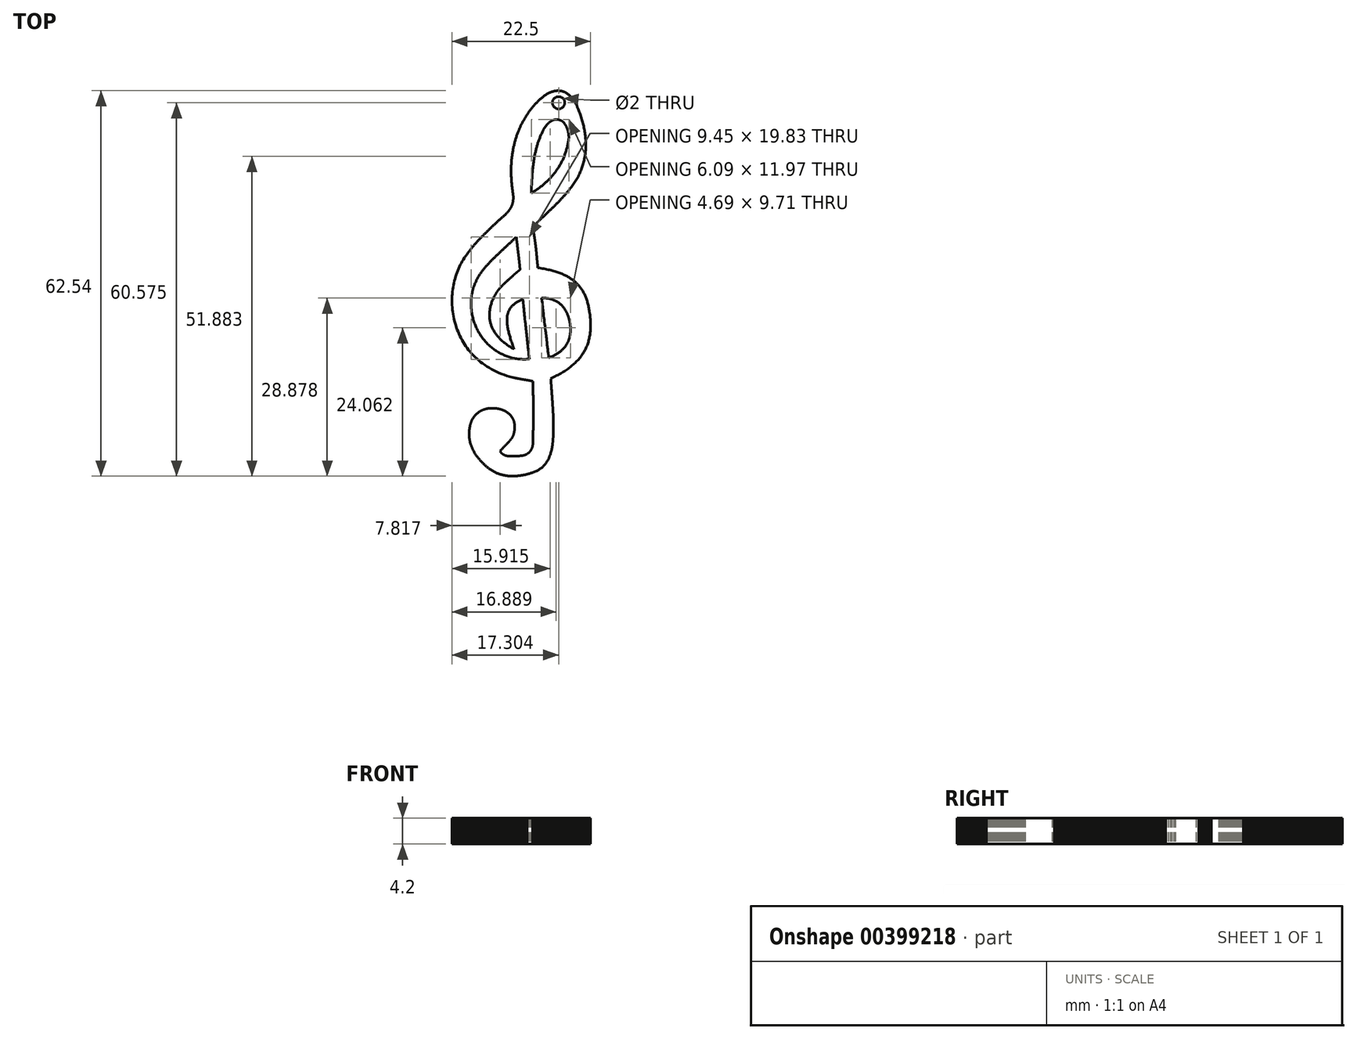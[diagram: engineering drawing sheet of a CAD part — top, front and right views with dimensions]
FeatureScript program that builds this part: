
annotation { "Feature Type Name" : "Feature", "Feature Type Description" : "" }
export const myFeature = defineFeature(function(context is Context, id is Id, definition is map)
    precondition{}
    {
        {
            var Q0;
            Q0=qCreatedBy(makeId("Top.planeOp"),FACE);
            var sketch = newSketch(context, id + "F0", { "sketchPlane" : qUnion([Q0])});
            skLineSegment(sketch, "E0", {"start": v(1.92, -15.87) * mm, "end": v(1.85, -15.86) * mm});
            skLineSegment(sketch, "E1", {"start": v(1.85, -15.86) * mm, "end": v(1.79, -15.85) * mm});
            skLineSegment(sketch, "E2", {"start": v(1.79, -15.85) * mm, "end": v(1.72, -15.84) * mm});
            skLineSegment(sketch, "E3", {"start": v(1.72, -15.84) * mm, "end": v(1.66, -15.82) * mm});
            skLineSegment(sketch, "E4", {"start": v(1.66, -15.82) * mm, "end": v(1.6, -15.81) * mm});
            skLineSegment(sketch, "E5", {"start": v(1.6, -15.81) * mm, "end": v(1.53, -15.8) * mm});
            skLineSegment(sketch, "E6", {"start": v(1.53, -15.8) * mm, "end": v(1.47, -15.8) * mm});
            skLineSegment(sketch, "E7", {"start": v(1.47, -15.8) * mm, "end": v(1.4, -15.78) * mm});
            skLineSegment(sketch, "E8", {"start": v(1.4, -15.78) * mm, "end": v(1.35, -15.77) * mm});
            skLineSegment(sketch, "E9", {"start": v(1.35, -15.77) * mm, "end": v(1.28, -15.76) * mm});
            skLineSegment(sketch, "E10", {"start": v(1.28, -15.76) * mm, "end": v(1.22, -15.75) * mm});
            skLineSegment(sketch, "E11", {"start": v(1.22, -15.75) * mm, "end": v(1.16, -15.74) * mm});
            skLineSegment(sketch, "E12", {"start": v(1.16, -15.74) * mm, "end": v(1.1, -15.73) * mm});
            skLineSegment(sketch, "E13", {"start": v(1.1, -15.73) * mm, "end": v(1.05, -15.72) * mm});
            skLineSegment(sketch, "E14", {"start": v(1.05, -15.72) * mm, "end": v(0.99, -15.7) * mm});
            skLineSegment(sketch, "E15", {"start": v(0.99, -15.7) * mm, "end": v(0.93, -15.7) * mm});
            skLineSegment(sketch, "E16", {"start": v(0.93, -15.7) * mm, "end": v(0.87, -15.69) * mm});
            skLineSegment(sketch, "E17", {"start": v(0.87, -15.69) * mm, "end": v(0.82, -15.68) * mm});
            skLineSegment(sketch, "E18", {"start": v(0.82, -15.68) * mm, "end": v(0.76, -15.67) * mm});
            skLineSegment(sketch, "E19", {"start": v(0.76, -15.67) * mm, "end": v(0.7, -15.66) * mm});
            skLineSegment(sketch, "E20", {"start": v(0.7, -15.66) * mm, "end": v(0.65, -15.65) * mm});
            skLineSegment(sketch, "E21", {"start": v(0.65, -15.65) * mm, "end": v(0.6, -15.64) * mm});
            skLineSegment(sketch, "E22", {"start": v(0.6, -15.64) * mm, "end": v(0.54, -15.63) * mm});
            skLineSegment(sketch, "E23", {"start": v(0.54, -15.63) * mm, "end": v(0.49, -15.62) * mm});
            skLineSegment(sketch, "E24", {"start": v(0.49, -15.62) * mm, "end": v(0.43, -15.61) * mm});
            skLineSegment(sketch, "E25", {"start": v(0.43, -15.61) * mm, "end": v(0.38, -15.6) * mm});
            skLineSegment(sketch, "E26", {"start": v(0.38, -15.6) * mm, "end": v(0.33, -15.6) * mm});
            skLineSegment(sketch, "E27", {"start": v(0.33, -15.6) * mm, "end": v(0.28, -15.58) * mm});
            skLineSegment(sketch, "E28", {"start": v(0.28, -15.58) * mm, "end": v(0.22, -15.57) * mm});
            skLineSegment(sketch, "E29", {"start": v(0.22, -15.57) * mm, "end": v(0.17, -15.57) * mm});
            skLineSegment(sketch, "E30", {"start": v(0.17, -15.57) * mm, "end": v(0.12, -15.56) * mm});
            skLineSegment(sketch, "E31", {"start": v(0.12, -15.56) * mm, "end": v(0.07, -15.55) * mm});
            skLineSegment(sketch, "E32", {"start": v(0.07, -15.55) * mm, "end": v(0.02, -15.54) * mm});
            skLineSegment(sketch, "E33", {"start": v(0.02, -15.54) * mm, "end": v(-0.03, -15.53) * mm});
            skLineSegment(sketch, "E34", {"start": v(-0.03, -15.53) * mm, "end": v(-0.08, -15.52) * mm});
            skLineSegment(sketch, "E35", {"start": v(-0.08, -15.52) * mm, "end": v(-0.13, -15.51) * mm});
            skLineSegment(sketch, "E36", {"start": v(-0.13, -15.51) * mm, "end": v(-0.18, -15.5) * mm});
            skLineSegment(sketch, "E37", {"start": v(-0.18, -15.5) * mm, "end": v(-0.23, -15.5) * mm});
            skLineSegment(sketch, "E38", {"start": v(-0.23, -15.5) * mm, "end": v(-0.28, -15.49) * mm});
            skLineSegment(sketch, "E39", {"start": v(-0.28, -15.49) * mm, "end": v(-0.33, -15.48) * mm});
            skLineSegment(sketch, "E40", {"start": v(-0.33, -15.48) * mm, "end": v(-0.38, -15.47) * mm});
            skLineSegment(sketch, "E41", {"start": v(-0.38, -15.47) * mm, "end": v(-0.42, -15.46) * mm});
            skLineSegment(sketch, "E42", {"start": v(-0.42, -15.46) * mm, "end": v(-0.47, -15.45) * mm});
            skLineSegment(sketch, "E43", {"start": v(-0.47, -15.45) * mm, "end": v(-0.52, -15.44) * mm});
            skLineSegment(sketch, "E44", {"start": v(-0.52, -15.44) * mm, "end": v(-0.57, -15.43) * mm});
            skLineSegment(sketch, "E45", {"start": v(-0.57, -15.43) * mm, "end": v(-0.61, -15.42) * mm});
            skLineSegment(sketch, "E46", {"start": v(-0.61, -15.42) * mm, "end": v(-0.66, -15.41) * mm});
            skLineSegment(sketch, "E47", {"start": v(-0.66, -15.41) * mm, "end": v(-0.7, -15.4) * mm});
            skLineSegment(sketch, "E48", {"start": v(-0.7, -15.4) * mm, "end": v(-0.75, -15.4) * mm});
            skLineSegment(sketch, "E49", {"start": v(-0.75, -15.4) * mm, "end": v(-0.8, -15.38) * mm});
            skLineSegment(sketch, "E50", {"start": v(-0.8, -15.38) * mm, "end": v(-0.85, -15.37) * mm});
            skLineSegment(sketch, "E51", {"start": v(-0.85, -15.37) * mm, "end": v(-0.9, -15.36) * mm});
            skLineSegment(sketch, "E52", {"start": v(-0.9, -15.36) * mm, "end": v(-0.94, -15.35) * mm});
            skLineSegment(sketch, "E53", {"start": v(-0.94, -15.35) * mm, "end": v(-0.98, -15.34) * mm});
            skLineSegment(sketch, "E54", {"start": v(-0.98, -15.34) * mm, "end": v(-1.03, -15.33) * mm});
            skLineSegment(sketch, "E55", {"start": v(-1.03, -15.33) * mm, "end": v(-1.08, -15.32) * mm});
            skLineSegment(sketch, "E56", {"start": v(-1.08, -15.32) * mm, "end": v(-1.12, -15.31) * mm});
            skLineSegment(sketch, "E57", {"start": v(-1.12, -15.31) * mm, "end": v(-1.17, -15.3) * mm});
            skLineSegment(sketch, "E58", {"start": v(-1.17, -15.3) * mm, "end": v(-1.21, -15.3) * mm});
            skLineSegment(sketch, "E59", {"start": v(-1.21, -15.3) * mm, "end": v(-1.26, -15.28) * mm});
            skLineSegment(sketch, "E60", {"start": v(-1.26, -15.28) * mm, "end": v(-1.3, -15.27) * mm});
            skLineSegment(sketch, "E61", {"start": v(-1.3, -15.27) * mm, "end": v(-1.35, -15.26) * mm});
            skLineSegment(sketch, "E62", {"start": v(-1.35, -15.26) * mm, "end": v(-1.4, -15.25) * mm});
            skLineSegment(sketch, "E63", {"start": v(-1.4, -15.25) * mm, "end": v(-1.44, -15.24) * mm});
            skLineSegment(sketch, "E64", {"start": v(-1.44, -15.24) * mm, "end": v(-1.9, -15.11) * mm});
            skLineSegment(sketch, "E65", {"start": v(-1.9, -15.11) * mm, "end": v(-2.36, -14.97) * mm});
            skLineSegment(sketch, "E66", {"start": v(-2.36, -14.97) * mm, "end": v(-2.8, -14.82) * mm});
            skLineSegment(sketch, "E67", {"start": v(-2.8, -14.82) * mm, "end": v(-3.24, -14.66) * mm});
            skLineSegment(sketch, "E68", {"start": v(-3.24, -14.66) * mm, "end": v(-3.66, -14.49) * mm});
            skLineSegment(sketch, "E69", {"start": v(-3.66, -14.49) * mm, "end": v(-4.07, -14.3) * mm});
            skLineSegment(sketch, "E70", {"start": v(-4.07, -14.3) * mm, "end": v(-4.47, -14.11) * mm});
            skLineSegment(sketch, "E71", {"start": v(-4.47, -14.11) * mm, "end": v(-4.85, -13.9) * mm});
            skLineSegment(sketch, "E72", {"start": v(-4.85, -13.9) * mm, "end": v(-5.23, -13.7) * mm});
            skLineSegment(sketch, "E73", {"start": v(-5.23, -13.7) * mm, "end": v(-5.59, -13.47) * mm});
            skLineSegment(sketch, "E74", {"start": v(-5.59, -13.47) * mm, "end": v(-5.94, -13.24) * mm});
            skLineSegment(sketch, "E75", {"start": v(-5.94, -13.24) * mm, "end": v(-6.27, -13) * mm});
            skLineSegment(sketch, "E76", {"start": v(-6.27, -13) * mm, "end": v(-6.6, -12.75) * mm});
            skLineSegment(sketch, "E77", {"start": v(-6.6, -12.75) * mm, "end": v(-6.91, -12.49) * mm});
            skLineSegment(sketch, "E78", {"start": v(-6.91, -12.49) * mm, "end": v(-7.21, -12.22) * mm});
            skLineSegment(sketch, "E79", {"start": v(-7.21, -12.22) * mm, "end": v(-7.5, -11.95) * mm});
            skLineSegment(sketch, "E80", {"start": v(-7.5, -11.95) * mm, "end": v(-7.78, -11.67) * mm});
            skLineSegment(sketch, "E81", {"start": v(-7.78, -11.67) * mm, "end": v(-8.05, -11.38) * mm});
            skLineSegment(sketch, "E82", {"start": v(-8.05, -11.38) * mm, "end": v(-8.3, -11.09) * mm});
            skLineSegment(sketch, "E83", {"start": v(-8.3, -11.09) * mm, "end": v(-8.55, -10.79) * mm});
            skLineSegment(sketch, "E84", {"start": v(-8.55, -10.79) * mm, "end": v(-8.79, -10.48) * mm});
            skLineSegment(sketch, "E85", {"start": v(-8.79, -10.48) * mm, "end": v(-9.01, -10.16) * mm});
            skLineSegment(sketch, "E86", {"start": v(-9.01, -10.16) * mm, "end": v(-9.22, -9.85) * mm});
            skLineSegment(sketch, "E87", {"start": v(-9.22, -9.85) * mm, "end": v(-9.42, -9.52) * mm});
            skLineSegment(sketch, "E88", {"start": v(-9.42, -9.52) * mm, "end": v(-9.61, -9.2) * mm});
            skLineSegment(sketch, "E89", {"start": v(-9.61, -9.2) * mm, "end": v(-9.8, -8.86) * mm});
            skLineSegment(sketch, "E90", {"start": v(-9.8, -8.86) * mm, "end": v(-9.96, -8.52) * mm});
            skLineSegment(sketch, "E91", {"start": v(-9.96, -8.52) * mm, "end": v(-10.12, -8.18) * mm});
            skLineSegment(sketch, "E92", {"start": v(-10.12, -8.18) * mm, "end": v(-10.27, -7.84) * mm});
            skLineSegment(sketch, "E93", {"start": v(-10.27, -7.84) * mm, "end": v(-10.4, -7.49) * mm});
            skLineSegment(sketch, "E94", {"start": v(-10.4, -7.49) * mm, "end": v(-10.53, -7.14) * mm});
            skLineSegment(sketch, "E95", {"start": v(-10.53, -7.14) * mm, "end": v(-10.65, -6.78) * mm});
            skLineSegment(sketch, "E96", {"start": v(-10.65, -6.78) * mm, "end": v(-10.75, -6.43) * mm});
            skLineSegment(sketch, "E97", {"start": v(-10.75, -6.43) * mm, "end": v(-10.85, -6.07) * mm});
            skLineSegment(sketch, "E98", {"start": v(-10.85, -6.07) * mm, "end": v(-10.93, -5.7) * mm});
            skLineSegment(sketch, "E99", {"start": v(-10.93, -5.7) * mm, "end": v(-11, -5.34) * mm});
            skLineSegment(sketch, "E100", {"start": v(-11, -5.34) * mm, "end": v(-11.07, -4.98) * mm});
            skLineSegment(sketch, "E101", {"start": v(-11.07, -4.98) * mm, "end": v(-11.12, -4.62) * mm});
            skLineSegment(sketch, "E102", {"start": v(-11.12, -4.62) * mm, "end": v(-11.17, -4.25) * mm});
            skLineSegment(sketch, "E103", {"start": v(-11.17, -4.25) * mm, "end": v(-11.2, -3.89) * mm});
            skLineSegment(sketch, "E104", {"start": v(-11.2, -3.89) * mm, "end": v(-11.23, -3.52) * mm});
            skLineSegment(sketch, "E105", {"start": v(-11.23, -3.52) * mm, "end": v(-11.24, -3.16) * mm});
            skLineSegment(sketch, "E106", {"start": v(-11.24, -3.16) * mm, "end": v(-11.25, -2.8) * mm});
            skLineSegment(sketch, "E107", {"start": v(-11.25, -2.8) * mm, "end": v(-11.24, -2.43) * mm});
            skLineSegment(sketch, "E108", {"start": v(-11.24, -2.43) * mm, "end": v(-11.23, -2.07) * mm});
            skLineSegment(sketch, "E109", {"start": v(-11.23, -2.07) * mm, "end": v(-11.2, -1.7) * mm});
            skLineSegment(sketch, "E110", {"start": v(-11.2, -1.7) * mm, "end": v(-11.17, -1.35) * mm});
            skLineSegment(sketch, "E111", {"start": v(-11.17, -1.35) * mm, "end": v(-11.13, -1) * mm});
            skLineSegment(sketch, "E112", {"start": v(-11.13, -1) * mm, "end": v(-11.07, -0.64) * mm});
            skLineSegment(sketch, "E113", {"start": v(-11.07, -0.64) * mm, "end": v(-11.01, -0.29) * mm});
            skLineSegment(sketch, "E114", {"start": v(-11.01, -0.29) * mm, "end": v(-10.94, 0.06) * mm});
            skLineSegment(sketch, "E115", {"start": v(-10.94, 0.06) * mm, "end": v(-10.86, 0.4) * mm});
            skLineSegment(sketch, "E116", {"start": v(-10.86, 0.4) * mm, "end": v(-10.77, 0.75) * mm});
            skLineSegment(sketch, "E117", {"start": v(-10.77, 0.75) * mm, "end": v(-10.68, 1.09) * mm});
            skLineSegment(sketch, "E118", {"start": v(-10.68, 1.09) * mm, "end": v(-10.57, 1.42) * mm});
            skLineSegment(sketch, "E119", {"start": v(-10.57, 1.42) * mm, "end": v(-10.45, 1.75) * mm});
            skLineSegment(sketch, "E120", {"start": v(-10.45, 1.75) * mm, "end": v(-10.33, 2.07) * mm});
            skLineSegment(sketch, "E121", {"start": v(-10.33, 2.07) * mm, "end": v(-10.2, 2.39) * mm});
            skLineSegment(sketch, "E122", {"start": v(-10.2, 2.39) * mm, "end": v(-10.06, 2.7) * mm});
            skLineSegment(sketch, "E123", {"start": v(-10.06, 2.7) * mm, "end": v(-9.9, 3) * mm});
            skLineSegment(sketch, "E124", {"start": v(-9.9, 3) * mm, "end": v(-9.75, 3.3) * mm});
            skLineSegment(sketch, "E125", {"start": v(-9.75, 3.3) * mm, "end": v(-9.58, 3.6) * mm});
            skLineSegment(sketch, "E126", {"start": v(-9.58, 3.6) * mm, "end": v(-9.4, 3.9) * mm});
            skLineSegment(sketch, "E127", {"start": v(-9.4, 3.9) * mm, "end": v(-9.22, 4.17) * mm});
            skLineSegment(sketch, "E128", {"start": v(-9.22, 4.17) * mm, "end": v(-9.14, 4.29) * mm});
            skLineSegment(sketch, "E129", {"start": v(-9.14, 4.29) * mm, "end": v(-9.06, 4.4) * mm});
            skLineSegment(sketch, "E130", {"start": v(-9.06, 4.4) * mm, "end": v(-8.97, 4.52) * mm});
            skLineSegment(sketch, "E131", {"start": v(-8.97, 4.52) * mm, "end": v(-8.89, 4.64) * mm});
            skLineSegment(sketch, "E132", {"start": v(-8.89, 4.64) * mm, "end": v(-8.8, 4.76) * mm});
            skLineSegment(sketch, "E133", {"start": v(-8.8, 4.76) * mm, "end": v(-8.72, 4.87) * mm});
            skLineSegment(sketch, "E134", {"start": v(-8.72, 4.87) * mm, "end": v(-8.63, 4.99) * mm});
            skLineSegment(sketch, "E135", {"start": v(-8.63, 4.99) * mm, "end": v(-8.55, 5.1) * mm});
            skLineSegment(sketch, "E136", {"start": v(-8.55, 5.1) * mm, "end": v(-8.46, 5.22) * mm});
            skLineSegment(sketch, "E137", {"start": v(-8.46, 5.22) * mm, "end": v(-8.37, 5.33) * mm});
            skLineSegment(sketch, "E138", {"start": v(-8.37, 5.33) * mm, "end": v(-8.28, 5.44) * mm});
            skLineSegment(sketch, "E139", {"start": v(-8.28, 5.44) * mm, "end": v(-8.2, 5.56) * mm});
            skLineSegment(sketch, "E140", {"start": v(-8.2, 5.56) * mm, "end": v(-8.1, 5.67) * mm});
            skLineSegment(sketch, "E141", {"start": v(-8.1, 5.67) * mm, "end": v(-8, 5.78) * mm});
            skLineSegment(sketch, "E142", {"start": v(-8, 5.78) * mm, "end": v(-7.92, 5.9) * mm});
            skLineSegment(sketch, "E143", {"start": v(-7.92, 5.9) * mm, "end": v(-7.82, 6) * mm});
            skLineSegment(sketch, "E144", {"start": v(-7.82, 6) * mm, "end": v(-7.73, 6.12) * mm});
            skLineSegment(sketch, "E145", {"start": v(-7.73, 6.12) * mm, "end": v(-7.64, 6.23) * mm});
            skLineSegment(sketch, "E146", {"start": v(-7.64, 6.23) * mm, "end": v(-7.54, 6.34) * mm});
            skLineSegment(sketch, "E147", {"start": v(-7.54, 6.34) * mm, "end": v(-7.45, 6.44) * mm});
            skLineSegment(sketch, "E148", {"start": v(-7.45, 6.44) * mm, "end": v(-7.35, 6.55) * mm});
            skLineSegment(sketch, "E149", {"start": v(-7.35, 6.55) * mm, "end": v(-7.25, 6.66) * mm});
            skLineSegment(sketch, "E150", {"start": v(-7.25, 6.66) * mm, "end": v(-7.16, 6.77) * mm});
            skLineSegment(sketch, "E151", {"start": v(-7.16, 6.77) * mm, "end": v(-7.06, 6.88) * mm});
            skLineSegment(sketch, "E152", {"start": v(-7.06, 6.88) * mm, "end": v(-6.96, 6.99) * mm});
            skLineSegment(sketch, "E153", {"start": v(-6.96, 6.99) * mm, "end": v(-6.86, 7.1) * mm});
            skLineSegment(sketch, "E154", {"start": v(-6.86, 7.1) * mm, "end": v(-6.76, 7.2) * mm});
            skLineSegment(sketch, "E155", {"start": v(-6.76, 7.2) * mm, "end": v(-6.66, 7.3) * mm});
            skLineSegment(sketch, "E156", {"start": v(-6.66, 7.3) * mm, "end": v(-6.56, 7.41) * mm});
            skLineSegment(sketch, "E157", {"start": v(-6.56, 7.41) * mm, "end": v(-6.46, 7.52) * mm});
            skLineSegment(sketch, "E158", {"start": v(-6.46, 7.52) * mm, "end": v(-6.36, 7.62) * mm});
            skLineSegment(sketch, "E159", {"start": v(-6.36, 7.62) * mm, "end": v(-6.26, 7.73) * mm});
            skLineSegment(sketch, "E160", {"start": v(-6.26, 7.73) * mm, "end": v(-6.16, 7.83) * mm});
            skLineSegment(sketch, "E161", {"start": v(-6.16, 7.83) * mm, "end": v(-6.06, 7.93) * mm});
            skLineSegment(sketch, "E162", {"start": v(-6.06, 7.93) * mm, "end": v(-5.95, 8.04) * mm});
            skLineSegment(sketch, "E163", {"start": v(-5.95, 8.04) * mm, "end": v(-5.85, 8.14) * mm});
            skLineSegment(sketch, "E164", {"start": v(-5.85, 8.14) * mm, "end": v(-5.75, 8.25) * mm});
            skLineSegment(sketch, "E165", {"start": v(-5.75, 8.25) * mm, "end": v(-5.64, 8.35) * mm});
            skLineSegment(sketch, "E166", {"start": v(-5.64, 8.35) * mm, "end": v(-5.54, 8.45) * mm});
            skLineSegment(sketch, "E167", {"start": v(-5.54, 8.45) * mm, "end": v(-5.43, 8.55) * mm});
            skLineSegment(sketch, "E168", {"start": v(-5.43, 8.55) * mm, "end": v(-5.33, 8.65) * mm});
            skLineSegment(sketch, "E169", {"start": v(-5.33, 8.65) * mm, "end": v(-5.22, 8.76) * mm});
            skLineSegment(sketch, "E170", {"start": v(-5.22, 8.76) * mm, "end": v(-5.12, 8.86) * mm});
            skLineSegment(sketch, "E171", {"start": v(-5.12, 8.86) * mm, "end": v(-5.01, 8.96) * mm});
            skLineSegment(sketch, "E172", {"start": v(-5.01, 8.96) * mm, "end": v(-4.9, 9.06) * mm});
            skLineSegment(sketch, "E173", {"start": v(-4.9, 9.06) * mm, "end": v(-4.8, 9.16) * mm});
            skLineSegment(sketch, "E174", {"start": v(-4.8, 9.16) * mm, "end": v(-4.7, 9.26) * mm});
            skLineSegment(sketch, "E175", {"start": v(-4.7, 9.26) * mm, "end": v(-4.59, 9.36) * mm});
            skLineSegment(sketch, "E176", {"start": v(-4.59, 9.36) * mm, "end": v(-4.48, 9.46) * mm});
            skLineSegment(sketch, "E177", {"start": v(-4.48, 9.46) * mm, "end": v(-4.37, 9.56) * mm});
            skLineSegment(sketch, "E178", {"start": v(-4.37, 9.56) * mm, "end": v(-4.26, 9.65) * mm});
            skLineSegment(sketch, "E179", {"start": v(-4.26, 9.65) * mm, "end": v(-4.16, 9.75) * mm});
            skLineSegment(sketch, "E180", {"start": v(-4.16, 9.75) * mm, "end": v(-4.05, 9.85) * mm});
            skLineSegment(sketch, "E181", {"start": v(-4.05, 9.85) * mm, "end": v(-3.94, 9.95) * mm});
            skLineSegment(sketch, "E182", {"start": v(-3.94, 9.95) * mm, "end": v(-3.83, 10.05) * mm});
            skLineSegment(sketch, "E183", {"start": v(-3.83, 10.05) * mm, "end": v(-3.72, 10.15) * mm});
            skLineSegment(sketch, "E184", {"start": v(-3.72, 10.15) * mm, "end": v(-3.62, 10.24) * mm});
            skLineSegment(sketch, "E185", {"start": v(-3.62, 10.24) * mm, "end": v(-3.5, 10.34) * mm});
            skLineSegment(sketch, "E186", {"start": v(-3.5, 10.34) * mm, "end": v(-3.4, 10.44) * mm});
            skLineSegment(sketch, "E187", {"start": v(-3.4, 10.44) * mm, "end": v(-3.3, 10.53) * mm});
            skLineSegment(sketch, "E188", {"start": v(-3.3, 10.53) * mm, "end": v(-3.18, 10.63) * mm});
            skLineSegment(sketch, "E189", {"start": v(-3.18, 10.63) * mm, "end": v(-3.08, 10.73) * mm});
            skLineSegment(sketch, "E190", {"start": v(-3.08, 10.73) * mm, "end": v(-2.97, 10.82) * mm});
            skLineSegment(sketch, "E191", {"start": v(-2.97, 10.82) * mm, "end": v(-2.86, 10.92) * mm});
            skLineSegment(sketch, "E192", {"start": v(-2.86, 10.92) * mm, "end": v(-2.8, 10.97) * mm});
            skLineSegment(sketch, "E193", {"start": v(-2.8, 10.97) * mm, "end": v(-2.74, 11.02) * mm});
            skLineSegment(sketch, "E194", {"start": v(-2.74, 11.02) * mm, "end": v(-2.69, 11.08) * mm});
            skLineSegment(sketch, "E195", {"start": v(-2.69, 11.08) * mm, "end": v(-2.63, 11.13) * mm});
            skLineSegment(sketch, "E196", {"start": v(-2.63, 11.13) * mm, "end": v(-2.58, 11.18) * mm});
            skLineSegment(sketch, "E197", {"start": v(-2.58, 11.18) * mm, "end": v(-2.52, 11.23) * mm});
            skLineSegment(sketch, "E198", {"start": v(-2.52, 11.23) * mm, "end": v(-2.47, 11.28) * mm});
            skLineSegment(sketch, "E199", {"start": v(-2.47, 11.28) * mm, "end": v(-2.42, 11.33) * mm});
            skLineSegment(sketch, "E200", {"start": v(-2.42, 11.33) * mm, "end": v(-2.37, 11.39) * mm});
            skLineSegment(sketch, "E201", {"start": v(-2.37, 11.39) * mm, "end": v(-2.32, 11.44) * mm});
            skLineSegment(sketch, "E202", {"start": v(-2.32, 11.44) * mm, "end": v(-2.28, 11.49) * mm});
            skLineSegment(sketch, "E203", {"start": v(-2.28, 11.49) * mm, "end": v(-2.23, 11.54) * mm});
            skLineSegment(sketch, "E204", {"start": v(-2.23, 11.54) * mm, "end": v(-2.18, 11.6) * mm});
            skLineSegment(sketch, "E205", {"start": v(-2.18, 11.6) * mm, "end": v(-2.14, 11.64) * mm});
            skLineSegment(sketch, "E206", {"start": v(-2.14, 11.64) * mm, "end": v(-2.1, 11.7) * mm});
            skLineSegment(sketch, "E207", {"start": v(-2.1, 11.7) * mm, "end": v(-2.06, 11.75) * mm});
            skLineSegment(sketch, "E208", {"start": v(-2.06, 11.75) * mm, "end": v(-2.02, 11.8) * mm});
            skLineSegment(sketch, "E209", {"start": v(-2.02, 11.8) * mm, "end": v(-1.98, 11.85) * mm});
            skLineSegment(sketch, "E210", {"start": v(-1.98, 11.85) * mm, "end": v(-1.94, 11.9) * mm});
            skLineSegment(sketch, "E211", {"start": v(-1.94, 11.9) * mm, "end": v(-1.9, 11.96) * mm});
            skLineSegment(sketch, "E212", {"start": v(-1.9, 11.96) * mm, "end": v(-1.87, 12) * mm});
            skLineSegment(sketch, "E213", {"start": v(-1.87, 12) * mm, "end": v(-1.83, 12.06) * mm});
            skLineSegment(sketch, "E214", {"start": v(-1.83, 12.06) * mm, "end": v(-1.8, 12.11) * mm});
            skLineSegment(sketch, "E215", {"start": v(-1.8, 12.11) * mm, "end": v(-1.76, 12.17) * mm});
            skLineSegment(sketch, "E216", {"start": v(-1.76, 12.17) * mm, "end": v(-1.73, 12.22) * mm});
            skLineSegment(sketch, "E217", {"start": v(-1.73, 12.22) * mm, "end": v(-1.7, 12.27) * mm});
            skLineSegment(sketch, "E218", {"start": v(-1.7, 12.27) * mm, "end": v(-1.67, 12.33) * mm});
            skLineSegment(sketch, "E219", {"start": v(-1.67, 12.33) * mm, "end": v(-1.65, 12.38) * mm});
            skLineSegment(sketch, "E220", {"start": v(-1.65, 12.38) * mm, "end": v(-1.62, 12.44) * mm});
            skLineSegment(sketch, "E221", {"start": v(-1.62, 12.44) * mm, "end": v(-1.6, 12.5) * mm});
            skLineSegment(sketch, "E222", {"start": v(-1.6, 12.5) * mm, "end": v(-1.57, 12.55) * mm});
            skLineSegment(sketch, "E223", {"start": v(-1.57, 12.55) * mm, "end": v(-1.54, 12.6) * mm});
            skLineSegment(sketch, "E224", {"start": v(-1.54, 12.6) * mm, "end": v(-1.52, 12.66) * mm});
            skLineSegment(sketch, "E225", {"start": v(-1.52, 12.66) * mm, "end": v(-1.5, 12.71) * mm});
            skLineSegment(sketch, "E226", {"start": v(-1.5, 12.71) * mm, "end": v(-1.48, 12.77) * mm});
            skLineSegment(sketch, "E227", {"start": v(-1.48, 12.77) * mm, "end": v(-1.46, 12.83) * mm});
            skLineSegment(sketch, "E228", {"start": v(-1.46, 12.83) * mm, "end": v(-1.44, 12.88) * mm});
            skLineSegment(sketch, "E229", {"start": v(-1.44, 12.88) * mm, "end": v(-1.43, 12.94) * mm});
            skLineSegment(sketch, "E230", {"start": v(-1.43, 12.94) * mm, "end": v(-1.4, 13) * mm});
            skLineSegment(sketch, "E231", {"start": v(-1.4, 13) * mm, "end": v(-1.4, 13.06) * mm});
            skLineSegment(sketch, "E232", {"start": v(-1.4, 13.06) * mm, "end": v(-1.38, 13.12) * mm});
            skLineSegment(sketch, "E233", {"start": v(-1.38, 13.12) * mm, "end": v(-1.37, 13.18) * mm});
            skLineSegment(sketch, "E234", {"start": v(-1.37, 13.18) * mm, "end": v(-1.36, 13.24) * mm});
            skLineSegment(sketch, "E235", {"start": v(-1.36, 13.24) * mm, "end": v(-1.35, 13.3) * mm});
            skLineSegment(sketch, "E236", {"start": v(-1.35, 13.3) * mm, "end": v(-1.34, 13.36) * mm});
            skLineSegment(sketch, "E237", {"start": v(-1.34, 13.36) * mm, "end": v(-1.33, 13.42) * mm});
            skLineSegment(sketch, "E238", {"start": v(-1.33, 13.42) * mm, "end": v(-1.32, 13.48) * mm});
            skLineSegment(sketch, "E239", {"start": v(-1.32, 13.48) * mm, "end": v(-1.32, 13.55) * mm});
            skLineSegment(sketch, "E240", {"start": v(-1.32, 13.55) * mm, "end": v(-1.31, 13.61) * mm});
            skLineSegment(sketch, "E241", {"start": v(-1.31, 13.61) * mm, "end": v(-1.3, 13.68) * mm});
            skLineSegment(sketch, "E242", {"start": v(-1.3, 13.68) * mm, "end": v(-1.3, 13.74) * mm});
            skLineSegment(sketch, "E243", {"start": v(-1.3, 13.74) * mm, "end": v(-1.3, 13.8) * mm});
            skLineSegment(sketch, "E244", {"start": v(-1.3, 13.8) * mm, "end": v(-1.3, 13.87) * mm});
            skLineSegment(sketch, "E245", {"start": v(-1.3, 13.87) * mm, "end": v(-1.3, 13.94) * mm});
            skLineSegment(sketch, "E246", {"start": v(-1.3, 13.94) * mm, "end": v(-1.3, 14) * mm});
            skLineSegment(sketch, "E247", {"start": v(-1.3, 14) * mm, "end": v(-1.3, 14.08) * mm});
            skLineSegment(sketch, "E248", {"start": v(-1.3, 14.08) * mm, "end": v(-1.3, 14.14) * mm});
            skLineSegment(sketch, "E249", {"start": v(-1.3, 14.14) * mm, "end": v(-1.31, 14.21) * mm});
            skLineSegment(sketch, "E250", {"start": v(-1.31, 14.21) * mm, "end": v(-1.32, 14.29) * mm});
            skLineSegment(sketch, "E251", {"start": v(-1.32, 14.29) * mm, "end": v(-1.33, 14.36) * mm});
            skLineSegment(sketch, "E252", {"start": v(-1.33, 14.36) * mm, "end": v(-1.33, 14.43) * mm});
            skLineSegment(sketch, "E253", {"start": v(-1.33, 14.43) * mm, "end": v(-1.34, 14.5) * mm});
            skLineSegment(sketch, "E254", {"start": v(-1.34, 14.5) * mm, "end": v(-1.35, 14.58) * mm});
            skLineSegment(sketch, "E255", {"start": v(-1.35, 14.58) * mm, "end": v(-1.36, 14.65) * mm});
            skLineSegment(sketch, "E256", {"start": v(-1.36, 14.65) * mm, "end": v(-1.39, 14.81) * mm});
            skLineSegment(sketch, "E257", {"start": v(-1.39, 14.81) * mm, "end": v(-1.41, 14.97) * mm});
            skLineSegment(sketch, "E258", {"start": v(-1.41, 14.97) * mm, "end": v(-1.43, 15.13) * mm});
            skLineSegment(sketch, "E259", {"start": v(-1.43, 15.13) * mm, "end": v(-1.45, 15.3) * mm});
            skLineSegment(sketch, "E260", {"start": v(-1.45, 15.3) * mm, "end": v(-1.47, 15.45) * mm});
            skLineSegment(sketch, "E261", {"start": v(-1.47, 15.45) * mm, "end": v(-1.5, 15.61) * mm});
            skLineSegment(sketch, "E262", {"start": v(-1.5, 15.61) * mm, "end": v(-1.51, 15.77) * mm});
            skLineSegment(sketch, "E263", {"start": v(-1.51, 15.77) * mm, "end": v(-1.53, 15.93) * mm});
            skLineSegment(sketch, "E264", {"start": v(-1.53, 15.93) * mm, "end": v(-1.54, 16.1) * mm});
            skLineSegment(sketch, "E265", {"start": v(-1.54, 16.1) * mm, "end": v(-1.56, 16.25) * mm});
            skLineSegment(sketch, "E266", {"start": v(-1.56, 16.25) * mm, "end": v(-1.57, 16.41) * mm});
            skLineSegment(sketch, "E267", {"start": v(-1.57, 16.41) * mm, "end": v(-1.59, 16.58) * mm});
            skLineSegment(sketch, "E268", {"start": v(-1.59, 16.58) * mm, "end": v(-1.6, 16.74) * mm});
            skLineSegment(sketch, "E269", {"start": v(-1.6, 16.74) * mm, "end": v(-1.6, 16.9) * mm});
            skLineSegment(sketch, "E270", {"start": v(-1.6, 16.9) * mm, "end": v(-1.62, 17.06) * mm});
            skLineSegment(sketch, "E271", {"start": v(-1.62, 17.06) * mm, "end": v(-1.63, 17.22) * mm});
            skLineSegment(sketch, "E272", {"start": v(-1.63, 17.22) * mm, "end": v(-1.63, 17.38) * mm});
            skLineSegment(sketch, "E273", {"start": v(-1.63, 17.38) * mm, "end": v(-1.64, 17.54) * mm});
            skLineSegment(sketch, "E274", {"start": v(-1.64, 17.54) * mm, "end": v(-1.64, 17.7) * mm});
            skLineSegment(sketch, "E275", {"start": v(-1.64, 17.7) * mm, "end": v(-1.65, 17.86) * mm});
            skLineSegment(sketch, "E276", {"start": v(-1.65, 17.86) * mm, "end": v(-1.65, 18.02) * mm});
            skLineSegment(sketch, "E277", {"start": v(-1.65, 18.02) * mm, "end": v(-1.65, 18.18) * mm});
            skLineSegment(sketch, "E278", {"start": v(-1.65, 18.18) * mm, "end": v(-1.65, 18.34) * mm});
            skLineSegment(sketch, "E279", {"start": v(-1.65, 18.34) * mm, "end": v(-1.65, 18.5) * mm});
            skLineSegment(sketch, "E280", {"start": v(-1.65, 18.5) * mm, "end": v(-1.65, 18.65) * mm});
            skLineSegment(sketch, "E281", {"start": v(-1.65, 18.65) * mm, "end": v(-1.64, 18.81) * mm});
            skLineSegment(sketch, "E282", {"start": v(-1.64, 18.81) * mm, "end": v(-1.64, 18.97) * mm});
            skLineSegment(sketch, "E283", {"start": v(-1.64, 18.97) * mm, "end": v(-1.63, 19.13) * mm});
            skLineSegment(sketch, "E284", {"start": v(-1.63, 19.13) * mm, "end": v(-1.62, 19.3) * mm});
            skLineSegment(sketch, "E285", {"start": v(-1.62, 19.3) * mm, "end": v(-1.61, 19.45) * mm});
            skLineSegment(sketch, "E286", {"start": v(-1.61, 19.45) * mm, "end": v(-1.6, 19.6) * mm});
            skLineSegment(sketch, "E287", {"start": v(-1.6, 19.6) * mm, "end": v(-1.6, 19.77) * mm});
            skLineSegment(sketch, "E288", {"start": v(-1.6, 19.77) * mm, "end": v(-1.58, 19.93) * mm});
            skLineSegment(sketch, "E289", {"start": v(-1.58, 19.93) * mm, "end": v(-1.57, 20.08) * mm});
            skLineSegment(sketch, "E290", {"start": v(-1.57, 20.08) * mm, "end": v(-1.55, 20.24) * mm});
            skLineSegment(sketch, "E291", {"start": v(-1.55, 20.24) * mm, "end": v(-1.53, 20.4) * mm});
            skLineSegment(sketch, "E292", {"start": v(-1.53, 20.4) * mm, "end": v(-1.52, 20.56) * mm});
            skLineSegment(sketch, "E293", {"start": v(-1.52, 20.56) * mm, "end": v(-1.5, 20.71) * mm});
            skLineSegment(sketch, "E294", {"start": v(-1.5, 20.71) * mm, "end": v(-1.48, 20.87) * mm});
            skLineSegment(sketch, "E295", {"start": v(-1.48, 20.87) * mm, "end": v(-1.45, 21.03) * mm});
            skLineSegment(sketch, "E296", {"start": v(-1.45, 21.03) * mm, "end": v(-1.43, 21.19) * mm});
            skLineSegment(sketch, "E297", {"start": v(-1.43, 21.19) * mm, "end": v(-1.4, 21.34) * mm});
            skLineSegment(sketch, "E298", {"start": v(-1.4, 21.34) * mm, "end": v(-1.38, 21.5) * mm});
            skLineSegment(sketch, "E299", {"start": v(-1.38, 21.5) * mm, "end": v(-1.35, 21.65) * mm});
            skLineSegment(sketch, "E300", {"start": v(-1.35, 21.65) * mm, "end": v(-1.32, 21.81) * mm});
            skLineSegment(sketch, "E301", {"start": v(-1.32, 21.81) * mm, "end": v(-1.29, 21.97) * mm});
            skLineSegment(sketch, "E302", {"start": v(-1.29, 21.97) * mm, "end": v(-1.26, 22.12) * mm});
            skLineSegment(sketch, "E303", {"start": v(-1.26, 22.12) * mm, "end": v(-1.22, 22.28) * mm});
            skLineSegment(sketch, "E304", {"start": v(-1.22, 22.28) * mm, "end": v(-1.19, 22.43) * mm});
            skLineSegment(sketch, "E305", {"start": v(-1.19, 22.43) * mm, "end": v(-1.15, 22.59) * mm});
            skLineSegment(sketch, "E306", {"start": v(-1.15, 22.59) * mm, "end": v(-1.11, 22.74) * mm});
            skLineSegment(sketch, "E307", {"start": v(-1.11, 22.74) * mm, "end": v(-1.07, 22.9) * mm});
            skLineSegment(sketch, "E308", {"start": v(-1.07, 22.9) * mm, "end": v(-1.03, 23.05) * mm});
            skLineSegment(sketch, "E309", {"start": v(-1.03, 23.05) * mm, "end": v(-0.99, 23.2) * mm});
            skLineSegment(sketch, "E310", {"start": v(-0.99, 23.2) * mm, "end": v(-0.94, 23.35) * mm});
            skLineSegment(sketch, "E311", {"start": v(-0.94, 23.35) * mm, "end": v(-0.9, 23.5) * mm});
            skLineSegment(sketch, "E312", {"start": v(-0.9, 23.5) * mm, "end": v(-0.85, 23.66) * mm});
            skLineSegment(sketch, "E313", {"start": v(-0.85, 23.66) * mm, "end": v(-0.8, 23.81) * mm});
            skLineSegment(sketch, "E314", {"start": v(-0.8, 23.81) * mm, "end": v(-0.75, 23.96) * mm});
            skLineSegment(sketch, "E315", {"start": v(-0.75, 23.96) * mm, "end": v(-0.7, 24.11) * mm});
            skLineSegment(sketch, "E316", {"start": v(-0.7, 24.11) * mm, "end": v(-0.64, 24.26) * mm});
            skLineSegment(sketch, "E317", {"start": v(-0.64, 24.26) * mm, "end": v(-0.58, 24.41) * mm});
            skLineSegment(sketch, "E318", {"start": v(-0.58, 24.41) * mm, "end": v(-0.53, 24.56) * mm});
            skLineSegment(sketch, "E319", {"start": v(-0.53, 24.56) * mm, "end": v(-0.47, 24.71) * mm});
            skLineSegment(sketch, "E320", {"start": v(-0.47, 24.71) * mm, "end": v(-0.43, 24.8) * mm});
            skLineSegment(sketch, "E321", {"start": v(-0.43, 24.8) * mm, "end": v(-0.4, 24.9) * mm});
            skLineSegment(sketch, "E322", {"start": v(-0.4, 24.9) * mm, "end": v(-0.36, 24.99) * mm});
            skLineSegment(sketch, "E323", {"start": v(-0.36, 24.99) * mm, "end": v(-0.32, 25.08) * mm});
            skLineSegment(sketch, "E324", {"start": v(-0.32, 25.08) * mm, "end": v(-0.28, 25.17) * mm});
            skLineSegment(sketch, "E325", {"start": v(-0.28, 25.17) * mm, "end": v(-0.24, 25.26) * mm});
            skLineSegment(sketch, "E326", {"start": v(-0.24, 25.26) * mm, "end": v(-0.2, 25.35) * mm});
            skLineSegment(sketch, "E327", {"start": v(-0.2, 25.35) * mm, "end": v(-0.15, 25.44) * mm});
            skLineSegment(sketch, "E328", {"start": v(-0.15, 25.44) * mm, "end": v(-0.11, 25.53) * mm});
            skLineSegment(sketch, "E329", {"start": v(-0.11, 25.53) * mm, "end": v(-0.07, 25.62) * mm});
            skLineSegment(sketch, "E330", {"start": v(-0.07, 25.62) * mm, "end": v(-0.02, 25.7) * mm});
            skLineSegment(sketch, "E331", {"start": v(-0.02, 25.7) * mm, "end": v(0.02, 25.8) * mm});
            skLineSegment(sketch, "E332", {"start": v(0.02, 25.8) * mm, "end": v(0.07, 25.89) * mm});
            skLineSegment(sketch, "E333", {"start": v(0.07, 25.89) * mm, "end": v(0.11, 25.98) * mm});
            skLineSegment(sketch, "E334", {"start": v(0.11, 25.98) * mm, "end": v(0.16, 26.07) * mm});
            skLineSegment(sketch, "E335", {"start": v(0.16, 26.07) * mm, "end": v(0.2, 26.16) * mm});
            skLineSegment(sketch, "E336", {"start": v(0.2, 26.16) * mm, "end": v(0.25, 26.24) * mm});
            skLineSegment(sketch, "E337", {"start": v(0.25, 26.24) * mm, "end": v(0.3, 26.33) * mm});
            skLineSegment(sketch, "E338", {"start": v(0.3, 26.33) * mm, "end": v(0.35, 26.42) * mm});
            skLineSegment(sketch, "E339", {"start": v(0.35, 26.42) * mm, "end": v(0.4, 26.5) * mm});
            skLineSegment(sketch, "E340", {"start": v(0.4, 26.5) * mm, "end": v(0.45, 26.6) * mm});
            skLineSegment(sketch, "E341", {"start": v(0.45, 26.6) * mm, "end": v(0.5, 26.69) * mm});
            skLineSegment(sketch, "E342", {"start": v(0.5, 26.69) * mm, "end": v(0.55, 26.77) * mm});
            skLineSegment(sketch, "E343", {"start": v(0.55, 26.77) * mm, "end": v(0.6, 26.86) * mm});
            skLineSegment(sketch, "E344", {"start": v(0.6, 26.86) * mm, "end": v(0.66, 26.95) * mm});
            skLineSegment(sketch, "E345", {"start": v(0.66, 26.95) * mm, "end": v(0.71, 27.03) * mm});
            skLineSegment(sketch, "E346", {"start": v(0.71, 27.03) * mm, "end": v(0.77, 27.12) * mm});
            skLineSegment(sketch, "E347", {"start": v(0.77, 27.12) * mm, "end": v(0.82, 27.2) * mm});
            skLineSegment(sketch, "E348", {"start": v(0.82, 27.2) * mm, "end": v(0.88, 27.3) * mm});
            skLineSegment(sketch, "E349", {"start": v(0.88, 27.3) * mm, "end": v(0.93, 27.38) * mm});
            skLineSegment(sketch, "E350", {"start": v(0.93, 27.38) * mm, "end": v(0.99, 27.46) * mm});
            skLineSegment(sketch, "E351", {"start": v(0.99, 27.46) * mm, "end": v(1.04, 27.55) * mm});
            skLineSegment(sketch, "E352", {"start": v(1.04, 27.55) * mm, "end": v(1.1, 27.63) * mm});
            skLineSegment(sketch, "E353", {"start": v(1.1, 27.63) * mm, "end": v(1.16, 27.71) * mm});
            skLineSegment(sketch, "E354", {"start": v(1.16, 27.71) * mm, "end": v(1.22, 27.8) * mm});
            skLineSegment(sketch, "E355", {"start": v(1.22, 27.8) * mm, "end": v(1.28, 27.88) * mm});
            skLineSegment(sketch, "E356", {"start": v(1.28, 27.88) * mm, "end": v(1.34, 27.96) * mm});
            skLineSegment(sketch, "E357", {"start": v(1.34, 27.96) * mm, "end": v(1.4, 28.04) * mm});
            skLineSegment(sketch, "E358", {"start": v(1.4, 28.04) * mm, "end": v(1.46, 28.12) * mm});
            skLineSegment(sketch, "E359", {"start": v(1.46, 28.12) * mm, "end": v(1.52, 28.2) * mm});
            skLineSegment(sketch, "E360", {"start": v(1.52, 28.2) * mm, "end": v(1.58, 28.28) * mm});
            skLineSegment(sketch, "E361", {"start": v(1.58, 28.28) * mm, "end": v(1.64, 28.36) * mm});
            skLineSegment(sketch, "E362", {"start": v(1.64, 28.36) * mm, "end": v(1.7, 28.44) * mm});
            skLineSegment(sketch, "E363", {"start": v(1.7, 28.44) * mm, "end": v(1.77, 28.52) * mm});
            skLineSegment(sketch, "E364", {"start": v(1.77, 28.52) * mm, "end": v(1.83, 28.6) * mm});
            skLineSegment(sketch, "E365", {"start": v(1.83, 28.6) * mm, "end": v(1.9, 28.68) * mm});
            skLineSegment(sketch, "E366", {"start": v(1.9, 28.68) * mm, "end": v(1.96, 28.75) * mm});
            skLineSegment(sketch, "E367", {"start": v(1.96, 28.75) * mm, "end": v(2.03, 28.83) * mm});
            skLineSegment(sketch, "E368", {"start": v(2.03, 28.83) * mm, "end": v(2.1, 28.9) * mm});
            skLineSegment(sketch, "E369", {"start": v(2.1, 28.9) * mm, "end": v(2.16, 28.98) * mm});
            skLineSegment(sketch, "E370", {"start": v(2.16, 28.98) * mm, "end": v(2.23, 29.05) * mm});
            skLineSegment(sketch, "E371", {"start": v(2.23, 29.05) * mm, "end": v(2.3, 29.13) * mm});
            skLineSegment(sketch, "E372", {"start": v(2.3, 29.13) * mm, "end": v(2.36, 29.2) * mm});
            skLineSegment(sketch, "E373", {"start": v(2.36, 29.2) * mm, "end": v(2.43, 29.27) * mm});
            skLineSegment(sketch, "E374", {"start": v(2.43, 29.27) * mm, "end": v(2.5, 29.35) * mm});
            skLineSegment(sketch, "E375", {"start": v(2.5, 29.35) * mm, "end": v(2.57, 29.42) * mm});
            skLineSegment(sketch, "E376", {"start": v(2.57, 29.42) * mm, "end": v(2.64, 29.49) * mm});
            skLineSegment(sketch, "E377", {"start": v(2.64, 29.49) * mm, "end": v(2.7, 29.56) * mm});
            skLineSegment(sketch, "E378", {"start": v(2.7, 29.56) * mm, "end": v(2.78, 29.63) * mm});
            skLineSegment(sketch, "E379", {"start": v(2.78, 29.63) * mm, "end": v(2.85, 29.7) * mm});
            skLineSegment(sketch, "E380", {"start": v(2.85, 29.7) * mm, "end": v(2.92, 29.76) * mm});
            skLineSegment(sketch, "E381", {"start": v(2.92, 29.76) * mm, "end": v(3, 29.83) * mm});
            skLineSegment(sketch, "E382", {"start": v(3, 29.83) * mm, "end": v(3.06, 29.9) * mm});
            skLineSegment(sketch, "E383", {"start": v(3.06, 29.9) * mm, "end": v(3.14, 29.96) * mm});
            skLineSegment(sketch, "E384", {"start": v(3.14, 29.96) * mm, "end": v(3.26, 30.07) * mm});
            skLineSegment(sketch, "E385", {"start": v(3.26, 30.07) * mm, "end": v(3.39, 30.17) * mm});
            skLineSegment(sketch, "E386", {"start": v(3.39, 30.17) * mm, "end": v(3.51, 30.27) * mm});
            skLineSegment(sketch, "E387", {"start": v(3.51, 30.27) * mm, "end": v(3.64, 30.37) * mm});
            skLineSegment(sketch, "E388", {"start": v(3.64, 30.37) * mm, "end": v(3.76, 30.46) * mm});
            skLineSegment(sketch, "E389", {"start": v(3.76, 30.46) * mm, "end": v(3.88, 30.54) * mm});
            skLineSegment(sketch, "E390", {"start": v(3.88, 30.54) * mm, "end": v(4, 30.62) * mm});
            skLineSegment(sketch, "E391", {"start": v(4, 30.62) * mm, "end": v(4.12, 30.7) * mm});
            skLineSegment(sketch, "E392", {"start": v(4.12, 30.7) * mm, "end": v(4.24, 30.76) * mm});
            skLineSegment(sketch, "E393", {"start": v(4.24, 30.76) * mm, "end": v(4.36, 30.83) * mm});
            skLineSegment(sketch, "E394", {"start": v(4.36, 30.83) * mm, "end": v(4.48, 30.9) * mm});
            skLineSegment(sketch, "E395", {"start": v(4.48, 30.9) * mm, "end": v(4.6, 30.95) * mm});
            skLineSegment(sketch, "E396", {"start": v(4.6, 30.95) * mm, "end": v(4.71, 31) * mm});
            skLineSegment(sketch, "E397", {"start": v(4.71, 31) * mm, "end": v(4.83, 31.04) * mm});
            skLineSegment(sketch, "E398", {"start": v(4.83, 31.04) * mm, "end": v(4.94, 31.09) * mm});
            skLineSegment(sketch, "E399", {"start": v(4.94, 31.09) * mm, "end": v(5.05, 31.12) * mm});
            skLineSegment(sketch, "E400", {"start": v(5.05, 31.12) * mm, "end": v(5.17, 31.16) * mm});
            skLineSegment(sketch, "E401", {"start": v(5.17, 31.16) * mm, "end": v(5.28, 31.19) * mm});
            skLineSegment(sketch, "E402", {"start": v(5.28, 31.19) * mm, "end": v(5.39, 31.2) * mm});
            skLineSegment(sketch, "E403", {"start": v(5.39, 31.2) * mm, "end": v(5.5, 31.23) * mm});
            skLineSegment(sketch, "E404", {"start": v(5.5, 31.23) * mm, "end": v(5.6, 31.25) * mm});
            skLineSegment(sketch, "E405", {"start": v(5.6, 31.25) * mm, "end": v(5.71, 31.26) * mm});
            skLineSegment(sketch, "E406", {"start": v(5.71, 31.26) * mm, "end": v(5.82, 31.26) * mm});
            skLineSegment(sketch, "E407", {"start": v(5.82, 31.26) * mm, "end": v(5.92, 31.27) * mm});
            skLineSegment(sketch, "E408", {"start": v(5.92, 31.27) * mm, "end": v(6.03, 31.27) * mm});
            skLineSegment(sketch, "E409", {"start": v(6.03, 31.27) * mm, "end": v(6.13, 31.26) * mm});
            skLineSegment(sketch, "E410", {"start": v(6.13, 31.26) * mm, "end": v(6.23, 31.25) * mm});
            skLineSegment(sketch, "E411", {"start": v(6.23, 31.25) * mm, "end": v(6.33, 31.24) * mm});
            skLineSegment(sketch, "E412", {"start": v(6.33, 31.24) * mm, "end": v(6.43, 31.22) * mm});
            skLineSegment(sketch, "E413", {"start": v(6.43, 31.22) * mm, "end": v(6.53, 31.2) * mm});
            skLineSegment(sketch, "E414", {"start": v(6.53, 31.2) * mm, "end": v(6.63, 31.18) * mm});
            skLineSegment(sketch, "E415", {"start": v(6.63, 31.18) * mm, "end": v(6.73, 31.15) * mm});
            skLineSegment(sketch, "E416", {"start": v(6.73, 31.15) * mm, "end": v(6.82, 31.12) * mm});
            skLineSegment(sketch, "E417", {"start": v(6.82, 31.12) * mm, "end": v(6.91, 31.08) * mm});
            skLineSegment(sketch, "E418", {"start": v(6.91, 31.08) * mm, "end": v(7, 31.04) * mm});
            skLineSegment(sketch, "E419", {"start": v(7, 31.04) * mm, "end": v(7.1, 31) * mm});
            skLineSegment(sketch, "E420", {"start": v(7.1, 31) * mm, "end": v(7.19, 30.95) * mm});
            skLineSegment(sketch, "E421", {"start": v(7.19, 30.95) * mm, "end": v(7.28, 30.9) * mm});
            skLineSegment(sketch, "E422", {"start": v(7.28, 30.9) * mm, "end": v(7.37, 30.84) * mm});
            skLineSegment(sketch, "E423", {"start": v(7.37, 30.84) * mm, "end": v(7.45, 30.79) * mm});
            skLineSegment(sketch, "E424", {"start": v(7.45, 30.79) * mm, "end": v(7.54, 30.73) * mm});
            skLineSegment(sketch, "E425", {"start": v(7.54, 30.73) * mm, "end": v(7.62, 30.66) * mm});
            skLineSegment(sketch, "E426", {"start": v(7.62, 30.66) * mm, "end": v(7.7, 30.6) * mm});
            skLineSegment(sketch, "E427", {"start": v(7.7, 30.6) * mm, "end": v(7.79, 30.52) * mm});
            skLineSegment(sketch, "E428", {"start": v(7.79, 30.52) * mm, "end": v(7.87, 30.45) * mm});
            skLineSegment(sketch, "E429", {"start": v(7.87, 30.45) * mm, "end": v(7.95, 30.37) * mm});
            skLineSegment(sketch, "E430", {"start": v(7.95, 30.37) * mm, "end": v(8.03, 30.3) * mm});
            skLineSegment(sketch, "E431", {"start": v(8.03, 30.3) * mm, "end": v(8.1, 30.2) * mm});
            skLineSegment(sketch, "E432", {"start": v(8.1, 30.2) * mm, "end": v(8.18, 30.12) * mm});
            skLineSegment(sketch, "E433", {"start": v(8.18, 30.12) * mm, "end": v(8.25, 30.03) * mm});
            skLineSegment(sketch, "E434", {"start": v(8.25, 30.03) * mm, "end": v(8.33, 29.94) * mm});
            skLineSegment(sketch, "E435", {"start": v(8.33, 29.94) * mm, "end": v(8.4, 29.84) * mm});
            skLineSegment(sketch, "E436", {"start": v(8.4, 29.84) * mm, "end": v(8.47, 29.75) * mm});
            skLineSegment(sketch, "E437", {"start": v(8.47, 29.75) * mm, "end": v(8.54, 29.65) * mm});
            skLineSegment(sketch, "E438", {"start": v(8.54, 29.65) * mm, "end": v(8.6, 29.54) * mm});
            skLineSegment(sketch, "E439", {"start": v(8.6, 29.54) * mm, "end": v(8.67, 29.43) * mm});
            skLineSegment(sketch, "E440", {"start": v(8.67, 29.43) * mm, "end": v(8.74, 29.33) * mm});
            skLineSegment(sketch, "E441", {"start": v(8.74, 29.33) * mm, "end": v(8.8, 29.21) * mm});
            skLineSegment(sketch, "E442", {"start": v(8.8, 29.21) * mm, "end": v(8.86, 29.1) * mm});
            skLineSegment(sketch, "E443", {"start": v(8.86, 29.1) * mm, "end": v(8.92, 28.98) * mm});
            skLineSegment(sketch, "E444", {"start": v(8.92, 28.98) * mm, "end": v(8.98, 28.86) * mm});
            skLineSegment(sketch, "E445", {"start": v(8.98, 28.86) * mm, "end": v(9.04, 28.74) * mm});
            skLineSegment(sketch, "E446", {"start": v(9.04, 28.74) * mm, "end": v(9.1, 28.61) * mm});
            skLineSegment(sketch, "E447", {"start": v(9.1, 28.61) * mm, "end": v(9.15, 28.49) * mm});
            skLineSegment(sketch, "E448", {"start": v(9.15, 28.49) * mm, "end": v(9.23, 28.27) * mm});
            skLineSegment(sketch, "E449", {"start": v(9.23, 28.27) * mm, "end": v(9.32, 28.06) * mm});
            skLineSegment(sketch, "E450", {"start": v(9.32, 28.06) * mm, "end": v(9.4, 27.84) * mm});
            skLineSegment(sketch, "E451", {"start": v(9.4, 27.84) * mm, "end": v(9.48, 27.63) * mm});
            skLineSegment(sketch, "E452", {"start": v(9.48, 27.63) * mm, "end": v(9.56, 27.42) * mm});
            skLineSegment(sketch, "E453", {"start": v(9.56, 27.42) * mm, "end": v(9.63, 27.2) * mm});
            skLineSegment(sketch, "E454", {"start": v(9.63, 27.2) * mm, "end": v(9.7, 26.99) * mm});
            skLineSegment(sketch, "E455", {"start": v(9.7, 26.99) * mm, "end": v(9.77, 26.77) * mm});
            skLineSegment(sketch, "E456", {"start": v(9.77, 26.77) * mm, "end": v(9.84, 26.56) * mm});
            skLineSegment(sketch, "E457", {"start": v(9.84, 26.56) * mm, "end": v(9.9, 26.34) * mm});
            skLineSegment(sketch, "E458", {"start": v(9.9, 26.34) * mm, "end": v(9.96, 26.13) * mm});
            skLineSegment(sketch, "E459", {"start": v(9.96, 26.13) * mm, "end": v(10.02, 25.92) * mm});
            skLineSegment(sketch, "E460", {"start": v(10.02, 25.92) * mm, "end": v(10.07, 25.7) * mm});
            skLineSegment(sketch, "E461", {"start": v(10.07, 25.7) * mm, "end": v(10.12, 25.49) * mm});
            skLineSegment(sketch, "E462", {"start": v(10.12, 25.49) * mm, "end": v(10.17, 25.27) * mm});
            skLineSegment(sketch, "E463", {"start": v(10.17, 25.27) * mm, "end": v(10.21, 25.06) * mm});
            skLineSegment(sketch, "E464", {"start": v(10.21, 25.06) * mm, "end": v(10.25, 24.84) * mm});
            skLineSegment(sketch, "E465", {"start": v(10.25, 24.84) * mm, "end": v(10.29, 24.63) * mm});
            skLineSegment(sketch, "E466", {"start": v(10.29, 24.63) * mm, "end": v(10.32, 24.42) * mm});
            skLineSegment(sketch, "E467", {"start": v(10.32, 24.42) * mm, "end": v(10.35, 24.2) * mm});
            skLineSegment(sketch, "E468", {"start": v(10.35, 24.2) * mm, "end": v(10.38, 24) * mm});
            skLineSegment(sketch, "E469", {"start": v(10.38, 24) * mm, "end": v(10.4, 23.78) * mm});
            skLineSegment(sketch, "E470", {"start": v(10.4, 23.78) * mm, "end": v(10.42, 23.57) * mm});
            skLineSegment(sketch, "E471", {"start": v(10.42, 23.57) * mm, "end": v(10.44, 23.35) * mm});
            skLineSegment(sketch, "E472", {"start": v(10.44, 23.35) * mm, "end": v(10.45, 23.14) * mm});
            skLineSegment(sketch, "E473", {"start": v(10.45, 23.14) * mm, "end": v(10.46, 22.93) * mm});
            skLineSegment(sketch, "E474", {"start": v(10.46, 22.93) * mm, "end": v(10.47, 22.72) * mm});
            skLineSegment(sketch, "E475", {"start": v(10.47, 22.72) * mm, "end": v(10.47, 22.5) * mm});
            skLineSegment(sketch, "E476", {"start": v(10.47, 22.5) * mm, "end": v(10.47, 22.3) * mm});
            skLineSegment(sketch, "E477", {"start": v(10.47, 22.3) * mm, "end": v(10.46, 22.08) * mm});
            skLineSegment(sketch, "E478", {"start": v(10.46, 22.08) * mm, "end": v(10.45, 21.87) * mm});
            skLineSegment(sketch, "E479", {"start": v(10.45, 21.87) * mm, "end": v(10.44, 21.66) * mm});
            skLineSegment(sketch, "E480", {"start": v(10.44, 21.66) * mm, "end": v(10.42, 21.45) * mm});
            skLineSegment(sketch, "E481", {"start": v(10.42, 21.45) * mm, "end": v(10.4, 21.24) * mm});
            skLineSegment(sketch, "E482", {"start": v(10.4, 21.24) * mm, "end": v(10.38, 21.03) * mm});
            skLineSegment(sketch, "E483", {"start": v(10.38, 21.03) * mm, "end": v(10.35, 20.83) * mm});
            skLineSegment(sketch, "E484", {"start": v(10.35, 20.83) * mm, "end": v(10.32, 20.62) * mm});
            skLineSegment(sketch, "E485", {"start": v(10.32, 20.62) * mm, "end": v(10.28, 20.4) * mm});
            skLineSegment(sketch, "E486", {"start": v(10.28, 20.4) * mm, "end": v(10.24, 20.2) * mm});
            skLineSegment(sketch, "E487", {"start": v(10.24, 20.2) * mm, "end": v(10.2, 20) * mm});
            skLineSegment(sketch, "E488", {"start": v(10.2, 20) * mm, "end": v(10.15, 19.79) * mm});
            skLineSegment(sketch, "E489", {"start": v(10.15, 19.79) * mm, "end": v(10.1, 19.58) * mm});
            skLineSegment(sketch, "E490", {"start": v(10.1, 19.58) * mm, "end": v(10.04, 19.38) * mm});
            skLineSegment(sketch, "E491", {"start": v(10.04, 19.38) * mm, "end": v(9.98, 19.17) * mm});
            skLineSegment(sketch, "E492", {"start": v(9.98, 19.17) * mm, "end": v(9.91, 18.97) * mm});
            skLineSegment(sketch, "E493", {"start": v(9.91, 18.97) * mm, "end": v(9.84, 18.76) * mm});
            skLineSegment(sketch, "E494", {"start": v(9.84, 18.76) * mm, "end": v(9.77, 18.56) * mm});
            skLineSegment(sketch, "E495", {"start": v(9.77, 18.56) * mm, "end": v(9.69, 18.36) * mm});
            skLineSegment(sketch, "E496", {"start": v(9.69, 18.36) * mm, "end": v(9.6, 18.15) * mm});
            skLineSegment(sketch, "E497", {"start": v(9.6, 18.15) * mm, "end": v(9.52, 17.95) * mm});
            skLineSegment(sketch, "E498", {"start": v(9.52, 17.95) * mm, "end": v(9.42, 17.75) * mm});
            skLineSegment(sketch, "E499", {"start": v(9.42, 17.75) * mm, "end": v(9.33, 17.55) * mm});
            skLineSegment(sketch, "E500", {"start": v(9.33, 17.55) * mm, "end": v(9.23, 17.35) * mm});
            skLineSegment(sketch, "E501", {"start": v(9.23, 17.35) * mm, "end": v(9.12, 17.15) * mm});
            skLineSegment(sketch, "E502", {"start": v(9.12, 17.15) * mm, "end": v(9, 16.95) * mm});
            skLineSegment(sketch, "E503", {"start": v(9, 16.95) * mm, "end": v(8.9, 16.76) * mm});
            skLineSegment(sketch, "E504", {"start": v(8.9, 16.76) * mm, "end": v(8.77, 16.56) * mm});
            skLineSegment(sketch, "E505", {"start": v(8.77, 16.56) * mm, "end": v(8.65, 16.36) * mm});
            skLineSegment(sketch, "E506", {"start": v(8.65, 16.36) * mm, "end": v(8.52, 16.17) * mm});
            skLineSegment(sketch, "E507", {"start": v(8.52, 16.17) * mm, "end": v(8.39, 15.97) * mm});
            skLineSegment(sketch, "E508", {"start": v(8.39, 15.97) * mm, "end": v(8.25, 15.78) * mm});
            skLineSegment(sketch, "E509", {"start": v(8.25, 15.78) * mm, "end": v(8.1, 15.58) * mm});
            skLineSegment(sketch, "E510", {"start": v(8.1, 15.58) * mm, "end": v(7.95, 15.4) * mm});
            skLineSegment(sketch, "E511", {"start": v(7.95, 15.4) * mm, "end": v(7.8, 15.2) * mm});
            skLineSegment(sketch, "E512", {"start": v(7.8, 15.2) * mm, "end": v(7.73, 15.12) * mm});
            skLineSegment(sketch, "E513", {"start": v(7.73, 15.12) * mm, "end": v(7.66, 15.03) * mm});
            skLineSegment(sketch, "E514", {"start": v(7.66, 15.03) * mm, "end": v(7.6, 14.95) * mm});
            skLineSegment(sketch, "E515", {"start": v(7.6, 14.95) * mm, "end": v(7.52, 14.86) * mm});
            skLineSegment(sketch, "E516", {"start": v(7.52, 14.86) * mm, "end": v(7.45, 14.78) * mm});
            skLineSegment(sketch, "E517", {"start": v(7.45, 14.78) * mm, "end": v(7.38, 14.7) * mm});
            skLineSegment(sketch, "E518", {"start": v(7.38, 14.7) * mm, "end": v(7.3, 14.61) * mm});
            skLineSegment(sketch, "E519", {"start": v(7.3, 14.61) * mm, "end": v(7.23, 14.53) * mm});
            skLineSegment(sketch, "E520", {"start": v(7.23, 14.53) * mm, "end": v(7.16, 14.45) * mm});
            skLineSegment(sketch, "E521", {"start": v(7.16, 14.45) * mm, "end": v(7.09, 14.37) * mm});
            skLineSegment(sketch, "E522", {"start": v(7.09, 14.37) * mm, "end": v(7.02, 14.28) * mm});
            skLineSegment(sketch, "E523", {"start": v(7.02, 14.28) * mm, "end": v(6.94, 14.2) * mm});
            skLineSegment(sketch, "E524", {"start": v(6.94, 14.2) * mm, "end": v(6.87, 14.12) * mm});
            skLineSegment(sketch, "E525", {"start": v(6.87, 14.12) * mm, "end": v(6.8, 14.04) * mm});
            skLineSegment(sketch, "E526", {"start": v(6.8, 14.04) * mm, "end": v(6.72, 13.96) * mm});
            skLineSegment(sketch, "E527", {"start": v(6.72, 13.96) * mm, "end": v(6.65, 13.88) * mm});
            skLineSegment(sketch, "E528", {"start": v(6.65, 13.88) * mm, "end": v(6.57, 13.8) * mm});
            skLineSegment(sketch, "E529", {"start": v(6.57, 13.8) * mm, "end": v(6.5, 13.72) * mm});
            skLineSegment(sketch, "E530", {"start": v(6.5, 13.72) * mm, "end": v(6.42, 13.64) * mm});
            skLineSegment(sketch, "E531", {"start": v(6.42, 13.64) * mm, "end": v(6.35, 13.56) * mm});
            skLineSegment(sketch, "E532", {"start": v(6.35, 13.56) * mm, "end": v(6.27, 13.48) * mm});
            skLineSegment(sketch, "E533", {"start": v(6.27, 13.48) * mm, "end": v(6.2, 13.4) * mm});
            skLineSegment(sketch, "E534", {"start": v(6.2, 13.4) * mm, "end": v(6.12, 13.32) * mm});
            skLineSegment(sketch, "E535", {"start": v(6.12, 13.32) * mm, "end": v(6.04, 13.24) * mm});
            skLineSegment(sketch, "E536", {"start": v(6.04, 13.24) * mm, "end": v(5.97, 13.16) * mm});
            skLineSegment(sketch, "E537", {"start": v(5.97, 13.16) * mm, "end": v(5.89, 13.08) * mm});
            skLineSegment(sketch, "E538", {"start": v(5.89, 13.08) * mm, "end": v(5.81, 13) * mm});
            skLineSegment(sketch, "E539", {"start": v(5.81, 13) * mm, "end": v(5.73, 12.93) * mm});
            skLineSegment(sketch, "E540", {"start": v(5.73, 12.93) * mm, "end": v(5.66, 12.85) * mm});
            skLineSegment(sketch, "E541", {"start": v(5.66, 12.85) * mm, "end": v(5.58, 12.77) * mm});
            skLineSegment(sketch, "E542", {"start": v(5.58, 12.77) * mm, "end": v(5.5, 12.7) * mm});
            skLineSegment(sketch, "E543", {"start": v(5.5, 12.7) * mm, "end": v(5.42, 12.61) * mm});
            skLineSegment(sketch, "E544", {"start": v(5.42, 12.61) * mm, "end": v(5.34, 12.54) * mm});
            skLineSegment(sketch, "E545", {"start": v(5.34, 12.54) * mm, "end": v(5.27, 12.46) * mm});
            skLineSegment(sketch, "E546", {"start": v(5.27, 12.46) * mm, "end": v(5.19, 12.38) * mm});
            skLineSegment(sketch, "E547", {"start": v(5.19, 12.38) * mm, "end": v(5.1, 12.3) * mm});
            skLineSegment(sketch, "E548", {"start": v(5.1, 12.3) * mm, "end": v(5.03, 12.23) * mm});
            skLineSegment(sketch, "E549", {"start": v(5.03, 12.23) * mm, "end": v(4.95, 12.15) * mm});
            skLineSegment(sketch, "E550", {"start": v(4.95, 12.15) * mm, "end": v(4.87, 12.07) * mm});
            skLineSegment(sketch, "E551", {"start": v(4.87, 12.07) * mm, "end": v(4.8, 12) * mm});
            skLineSegment(sketch, "E552", {"start": v(4.8, 12) * mm, "end": v(4.71, 11.92) * mm});
            skLineSegment(sketch, "E553", {"start": v(4.71, 11.92) * mm, "end": v(4.63, 11.84) * mm});
            skLineSegment(sketch, "E554", {"start": v(4.63, 11.84) * mm, "end": v(4.56, 11.77) * mm});
            skLineSegment(sketch, "E555", {"start": v(4.56, 11.77) * mm, "end": v(4.48, 11.7) * mm});
            skLineSegment(sketch, "E556", {"start": v(4.48, 11.7) * mm, "end": v(4.4, 11.61) * mm});
            skLineSegment(sketch, "E557", {"start": v(4.4, 11.61) * mm, "end": v(4.32, 11.54) * mm});
            skLineSegment(sketch, "E558", {"start": v(4.32, 11.54) * mm, "end": v(4.24, 11.46) * mm});
            skLineSegment(sketch, "E559", {"start": v(4.24, 11.46) * mm, "end": v(4.16, 11.39) * mm});
            skLineSegment(sketch, "E560", {"start": v(4.16, 11.39) * mm, "end": v(4.08, 11.31) * mm});
            skLineSegment(sketch, "E561", {"start": v(4.08, 11.31) * mm, "end": v(4, 11.23) * mm});
            skLineSegment(sketch, "E562", {"start": v(4, 11.23) * mm, "end": v(3.92, 11.16) * mm});
            skLineSegment(sketch, "E563", {"start": v(3.92, 11.16) * mm, "end": v(3.84, 11.08) * mm});
            skLineSegment(sketch, "E564", {"start": v(3.84, 11.08) * mm, "end": v(3.76, 11) * mm});
            skLineSegment(sketch, "E565", {"start": v(3.76, 11) * mm, "end": v(3.68, 10.93) * mm});
            skLineSegment(sketch, "E566", {"start": v(3.68, 10.93) * mm, "end": v(3.6, 10.86) * mm});
            skLineSegment(sketch, "E567", {"start": v(3.6, 10.86) * mm, "end": v(3.52, 10.78) * mm});
            skLineSegment(sketch, "E568", {"start": v(3.52, 10.78) * mm, "end": v(3.44, 10.7) * mm});
            skLineSegment(sketch, "E569", {"start": v(3.44, 10.7) * mm, "end": v(3.36, 10.63) * mm});
            skLineSegment(sketch, "E570", {"start": v(3.36, 10.63) * mm, "end": v(3.28, 10.55) * mm});
            skLineSegment(sketch, "E571", {"start": v(3.28, 10.55) * mm, "end": v(3.2, 10.48) * mm});
            skLineSegment(sketch, "E572", {"start": v(3.2, 10.48) * mm, "end": v(3.12, 10.4) * mm});
            skLineSegment(sketch, "E573", {"start": v(3.12, 10.4) * mm, "end": v(3.04, 10.33) * mm});
            skLineSegment(sketch, "E574", {"start": v(3.04, 10.33) * mm, "end": v(2.96, 10.25) * mm});
            skLineSegment(sketch, "E575", {"start": v(2.96, 10.25) * mm, "end": v(2.88, 10.18) * mm});
            skLineSegment(sketch, "E576", {"start": v(2.88, 10.18) * mm, "end": v(2.84, 10.14) * mm});
            skLineSegment(sketch, "E577", {"start": v(2.84, 10.14) * mm, "end": v(2.81, 10.11) * mm});
            skLineSegment(sketch, "E578", {"start": v(2.81, 10.11) * mm, "end": v(2.78, 10.08) * mm});
            skLineSegment(sketch, "E579", {"start": v(2.78, 10.08) * mm, "end": v(2.75, 10.05) * mm});
            skLineSegment(sketch, "E580", {"start": v(2.75, 10.05) * mm, "end": v(2.72, 10.02) * mm});
            skLineSegment(sketch, "E581", {"start": v(2.72, 10.02) * mm, "end": v(2.69, 9.99) * mm});
            skLineSegment(sketch, "E582", {"start": v(2.69, 9.99) * mm, "end": v(2.66, 9.96) * mm});
            skLineSegment(sketch, "E583", {"start": v(2.66, 9.96) * mm, "end": v(2.63, 9.93) * mm});
            skLineSegment(sketch, "E584", {"start": v(2.63, 9.93) * mm, "end": v(2.6, 9.9) * mm});
            skLineSegment(sketch, "E585", {"start": v(2.6, 9.9) * mm, "end": v(2.57, 9.86) * mm});
            skLineSegment(sketch, "E586", {"start": v(2.57, 9.86) * mm, "end": v(2.55, 9.83) * mm});
            skLineSegment(sketch, "E587", {"start": v(2.55, 9.83) * mm, "end": v(2.52, 9.8) * mm});
            skLineSegment(sketch, "E588", {"start": v(2.52, 9.8) * mm, "end": v(2.5, 9.77) * mm});
            skLineSegment(sketch, "E589", {"start": v(2.5, 9.77) * mm, "end": v(2.47, 9.74) * mm});
            skLineSegment(sketch, "E590", {"start": v(2.47, 9.74) * mm, "end": v(2.45, 9.7) * mm});
            skLineSegment(sketch, "E591", {"start": v(2.45, 9.7) * mm, "end": v(2.42, 9.68) * mm});
            skLineSegment(sketch, "E592", {"start": v(2.42, 9.68) * mm, "end": v(2.4, 9.65) * mm});
            skLineSegment(sketch, "E593", {"start": v(2.4, 9.65) * mm, "end": v(2.38, 9.61) * mm});
            skLineSegment(sketch, "E594", {"start": v(2.38, 9.61) * mm, "end": v(2.36, 9.58) * mm});
            skLineSegment(sketch, "E595", {"start": v(2.36, 9.58) * mm, "end": v(2.34, 9.55) * mm});
            skLineSegment(sketch, "E596", {"start": v(2.34, 9.55) * mm, "end": v(2.32, 9.52) * mm});
            skLineSegment(sketch, "E597", {"start": v(2.32, 9.52) * mm, "end": v(2.3, 9.49) * mm});
            skLineSegment(sketch, "E598", {"start": v(2.3, 9.49) * mm, "end": v(2.28, 9.45) * mm});
            skLineSegment(sketch, "E599", {"start": v(2.28, 9.45) * mm, "end": v(2.26, 9.42) * mm});
            skLineSegment(sketch, "E600", {"start": v(2.26, 9.42) * mm, "end": v(2.24, 9.4) * mm});
            skLineSegment(sketch, "E601", {"start": v(2.24, 9.4) * mm, "end": v(2.23, 9.36) * mm});
            skLineSegment(sketch, "E602", {"start": v(2.23, 9.36) * mm, "end": v(2.21, 9.33) * mm});
            skLineSegment(sketch, "E603", {"start": v(2.21, 9.33) * mm, "end": v(2.2, 9.3) * mm});
            skLineSegment(sketch, "E604", {"start": v(2.2, 9.3) * mm, "end": v(2.18, 9.26) * mm});
            skLineSegment(sketch, "E605", {"start": v(2.18, 9.26) * mm, "end": v(2.17, 9.23) * mm});
            skLineSegment(sketch, "E606", {"start": v(2.17, 9.23) * mm, "end": v(2.15, 9.2) * mm});
            skLineSegment(sketch, "E607", {"start": v(2.15, 9.2) * mm, "end": v(2.14, 9.16) * mm});
            skLineSegment(sketch, "E608", {"start": v(2.14, 9.16) * mm, "end": v(2.13, 9.13) * mm});
            skLineSegment(sketch, "E609", {"start": v(2.13, 9.13) * mm, "end": v(2.12, 9.1) * mm});
            skLineSegment(sketch, "E610", {"start": v(2.12, 9.1) * mm, "end": v(2.1, 9.06) * mm});
            skLineSegment(sketch, "E611", {"start": v(2.1, 9.06) * mm, "end": v(2.1, 9.02) * mm});
            skLineSegment(sketch, "E612", {"start": v(2.1, 9.02) * mm, "end": v(2.08, 8.99) * mm});
            skLineSegment(sketch, "E613", {"start": v(2.08, 8.99) * mm, "end": v(2.08, 8.95) * mm});
            skLineSegment(sketch, "E614", {"start": v(2.08, 8.95) * mm, "end": v(2.07, 8.92) * mm});
            skLineSegment(sketch, "E615", {"start": v(2.07, 8.92) * mm, "end": v(2.06, 8.88) * mm});
            skLineSegment(sketch, "E616", {"start": v(2.06, 8.88) * mm, "end": v(2.05, 8.84) * mm});
            skLineSegment(sketch, "E617", {"start": v(2.05, 8.84) * mm, "end": v(2.05, 8.8) * mm});
            skLineSegment(sketch, "E618", {"start": v(2.05, 8.8) * mm, "end": v(2.04, 8.77) * mm});
            skLineSegment(sketch, "E619", {"start": v(2.04, 8.77) * mm, "end": v(2.04, 8.73) * mm});
            skLineSegment(sketch, "E620", {"start": v(2.04, 8.73) * mm, "end": v(2.03, 8.7) * mm});
            skLineSegment(sketch, "E621", {"start": v(2.03, 8.7) * mm, "end": v(2.03, 8.66) * mm});
            skLineSegment(sketch, "E622", {"start": v(2.03, 8.66) * mm, "end": v(2.02, 8.62) * mm});
            skLineSegment(sketch, "E623", {"start": v(2.02, 8.62) * mm, "end": v(2.02, 8.58) * mm});
            skLineSegment(sketch, "E624", {"start": v(2.02, 8.58) * mm, "end": v(2.02, 8.54) * mm});
            skLineSegment(sketch, "E625", {"start": v(2.02, 8.54) * mm, "end": v(2.02, 8.5) * mm});
            skLineSegment(sketch, "E626", {"start": v(2.02, 8.5) * mm, "end": v(2.02, 8.46) * mm});
            skLineSegment(sketch, "E627", {"start": v(2.02, 8.46) * mm, "end": v(2.02, 8.42) * mm});
            skLineSegment(sketch, "E628", {"start": v(2.02, 8.42) * mm, "end": v(2.02, 8.38) * mm});
            skLineSegment(sketch, "E629", {"start": v(2.02, 8.38) * mm, "end": v(2.02, 8.34) * mm});
            skLineSegment(sketch, "E630", {"start": v(2.02, 8.34) * mm, "end": v(2.02, 8.3) * mm});
            skLineSegment(sketch, "E631", {"start": v(2.02, 8.3) * mm, "end": v(2.03, 8.25) * mm});
            skLineSegment(sketch, "E632", {"start": v(2.03, 8.25) * mm, "end": v(2.03, 8.21) * mm});
            skLineSegment(sketch, "E633", {"start": v(2.03, 8.21) * mm, "end": v(2.03, 8.17) * mm});
            skLineSegment(sketch, "E634", {"start": v(2.03, 8.17) * mm, "end": v(2.04, 8.12) * mm});
            skLineSegment(sketch, "E635", {"start": v(2.04, 8.12) * mm, "end": v(2.04, 8.08) * mm});
            skLineSegment(sketch, "E636", {"start": v(2.04, 8.08) * mm, "end": v(2.05, 8.03) * mm});
            skLineSegment(sketch, "E637", {"start": v(2.05, 8.03) * mm, "end": v(2.06, 7.99) * mm});
            skLineSegment(sketch, "E638", {"start": v(2.06, 7.99) * mm, "end": v(2.06, 7.94) * mm});
            skLineSegment(sketch, "E639", {"start": v(2.06, 7.94) * mm, "end": v(2.07, 7.9) * mm});
            skLineSegment(sketch, "E640", {"start": v(2.07, 7.9) * mm, "end": v(2.09, 7.81) * mm});
            skLineSegment(sketch, "E641", {"start": v(2.09, 7.81) * mm, "end": v(2.1, 7.73) * mm});
            skLineSegment(sketch, "E642", {"start": v(2.1, 7.73) * mm, "end": v(2.11, 7.65) * mm});
            skLineSegment(sketch, "E643", {"start": v(2.11, 7.65) * mm, "end": v(2.13, 7.56) * mm});
            skLineSegment(sketch, "E644", {"start": v(2.13, 7.56) * mm, "end": v(2.14, 7.48) * mm});
            skLineSegment(sketch, "E645", {"start": v(2.14, 7.48) * mm, "end": v(2.15, 7.4) * mm});
            skLineSegment(sketch, "E646", {"start": v(2.15, 7.4) * mm, "end": v(2.17, 7.31) * mm});
            skLineSegment(sketch, "E647", {"start": v(2.17, 7.31) * mm, "end": v(2.18, 7.23) * mm});
            skLineSegment(sketch, "E648", {"start": v(2.18, 7.23) * mm, "end": v(2.2, 7.14) * mm});
            skLineSegment(sketch, "E649", {"start": v(2.2, 7.14) * mm, "end": v(2.2, 7.06) * mm});
            skLineSegment(sketch, "E650", {"start": v(2.2, 7.06) * mm, "end": v(2.22, 6.98) * mm});
            skLineSegment(sketch, "E651", {"start": v(2.22, 6.98) * mm, "end": v(2.23, 6.9) * mm});
            skLineSegment(sketch, "E652", {"start": v(2.23, 6.9) * mm, "end": v(2.24, 6.8) * mm});
            skLineSegment(sketch, "E653", {"start": v(2.24, 6.8) * mm, "end": v(2.25, 6.73) * mm});
            skLineSegment(sketch, "E654", {"start": v(2.25, 6.73) * mm, "end": v(2.26, 6.64) * mm});
            skLineSegment(sketch, "E655", {"start": v(2.26, 6.64) * mm, "end": v(2.27, 6.56) * mm});
            skLineSegment(sketch, "E656", {"start": v(2.27, 6.56) * mm, "end": v(2.28, 6.47) * mm});
            skLineSegment(sketch, "E657", {"start": v(2.28, 6.47) * mm, "end": v(2.3, 6.39) * mm});
            skLineSegment(sketch, "E658", {"start": v(2.3, 6.39) * mm, "end": v(2.3, 6.3) * mm});
            skLineSegment(sketch, "E659", {"start": v(2.3, 6.3) * mm, "end": v(2.31, 6.22) * mm});
            skLineSegment(sketch, "E660", {"start": v(2.31, 6.22) * mm, "end": v(2.32, 6.14) * mm});
            skLineSegment(sketch, "E661", {"start": v(2.32, 6.14) * mm, "end": v(2.33, 6.05) * mm});
            skLineSegment(sketch, "E662", {"start": v(2.33, 6.05) * mm, "end": v(2.34, 5.97) * mm});
            skLineSegment(sketch, "E663", {"start": v(2.34, 5.97) * mm, "end": v(2.35, 5.89) * mm});
            skLineSegment(sketch, "E664", {"start": v(2.35, 5.89) * mm, "end": v(2.36, 5.8) * mm});
            skLineSegment(sketch, "E665", {"start": v(2.36, 5.8) * mm, "end": v(2.37, 5.72) * mm});
            skLineSegment(sketch, "E666", {"start": v(2.37, 5.72) * mm, "end": v(2.38, 5.63) * mm});
            skLineSegment(sketch, "E667", {"start": v(2.38, 5.63) * mm, "end": v(2.39, 5.55) * mm});
            skLineSegment(sketch, "E668", {"start": v(2.39, 5.55) * mm, "end": v(2.4, 5.47) * mm});
            skLineSegment(sketch, "E669", {"start": v(2.4, 5.47) * mm, "end": v(2.4, 5.38) * mm});
            skLineSegment(sketch, "E670", {"start": v(2.4, 5.38) * mm, "end": v(2.42, 5.3) * mm});
            skLineSegment(sketch, "E671", {"start": v(2.42, 5.3) * mm, "end": v(2.42, 5.21) * mm});
            skLineSegment(sketch, "E672", {"start": v(2.42, 5.21) * mm, "end": v(2.43, 5.13) * mm});
            skLineSegment(sketch, "E673", {"start": v(2.43, 5.13) * mm, "end": v(2.44, 5.05) * mm});
            skLineSegment(sketch, "E674", {"start": v(2.44, 5.05) * mm, "end": v(2.45, 4.96) * mm});
            skLineSegment(sketch, "E675", {"start": v(2.45, 4.96) * mm, "end": v(2.46, 4.88) * mm});
            skLineSegment(sketch, "E676", {"start": v(2.46, 4.88) * mm, "end": v(2.47, 4.8) * mm});
            skLineSegment(sketch, "E677", {"start": v(2.47, 4.8) * mm, "end": v(2.47, 4.71) * mm});
            skLineSegment(sketch, "E678", {"start": v(2.47, 4.71) * mm, "end": v(2.48, 4.63) * mm});
            skLineSegment(sketch, "E679", {"start": v(2.48, 4.63) * mm, "end": v(2.5, 4.54) * mm});
            skLineSegment(sketch, "E680", {"start": v(2.5, 4.54) * mm, "end": v(2.5, 4.46) * mm});
            skLineSegment(sketch, "E681", {"start": v(2.5, 4.46) * mm, "end": v(2.5, 4.38) * mm});
            skLineSegment(sketch, "E682", {"start": v(2.5, 4.38) * mm, "end": v(2.51, 4.3) * mm});
            skLineSegment(sketch, "E683", {"start": v(2.51, 4.3) * mm, "end": v(2.52, 4.2) * mm});
            skLineSegment(sketch, "E684", {"start": v(2.52, 4.2) * mm, "end": v(2.53, 4.12) * mm});
            skLineSegment(sketch, "E685", {"start": v(2.53, 4.12) * mm, "end": v(2.54, 4.04) * mm});
            skLineSegment(sketch, "E686", {"start": v(2.54, 4.04) * mm, "end": v(2.55, 3.96) * mm});
            skLineSegment(sketch, "E687", {"start": v(2.55, 3.96) * mm, "end": v(2.55, 3.87) * mm});
            skLineSegment(sketch, "E688", {"start": v(2.55, 3.87) * mm, "end": v(2.56, 3.79) * mm});
            skLineSegment(sketch, "E689", {"start": v(2.56, 3.79) * mm, "end": v(2.57, 3.7) * mm});
            skLineSegment(sketch, "E690", {"start": v(2.57, 3.7) * mm, "end": v(2.58, 3.62) * mm});
            skLineSegment(sketch, "E691", {"start": v(2.58, 3.62) * mm, "end": v(2.59, 3.54) * mm});
            skLineSegment(sketch, "E692", {"start": v(2.59, 3.54) * mm, "end": v(2.6, 3.46) * mm});
            skLineSegment(sketch, "E693", {"start": v(2.6, 3.46) * mm, "end": v(2.6, 3.37) * mm});
            skLineSegment(sketch, "E694", {"start": v(2.6, 3.37) * mm, "end": v(2.6, 3.29) * mm});
            skLineSegment(sketch, "E695", {"start": v(2.6, 3.29) * mm, "end": v(2.62, 3.2) * mm});
            skLineSegment(sketch, "E696", {"start": v(2.62, 3.2) * mm, "end": v(2.63, 3.12) * mm});
            skLineSegment(sketch, "E697", {"start": v(2.63, 3.12) * mm, "end": v(2.63, 3.04) * mm});
            skLineSegment(sketch, "E698", {"start": v(2.63, 3.04) * mm, "end": v(2.64, 2.96) * mm});
            skLineSegment(sketch, "E699", {"start": v(2.64, 2.96) * mm, "end": v(2.65, 2.87) * mm});
            skLineSegment(sketch, "E700", {"start": v(2.65, 2.87) * mm, "end": v(2.66, 2.8) * mm});
            skLineSegment(sketch, "E701", {"start": v(2.66, 2.8) * mm, "end": v(2.67, 2.7) * mm});
            skLineSegment(sketch, "E702", {"start": v(2.67, 2.7) * mm, "end": v(2.68, 2.63) * mm});
            skLineSegment(sketch, "E703", {"start": v(2.68, 2.63) * mm, "end": v(2.69, 2.54) * mm});
            skLineSegment(sketch, "E704", {"start": v(2.69, 2.54) * mm, "end": v(2.94, 2.5) * mm});
            skLineSegment(sketch, "E705", {"start": v(2.94, 2.5) * mm, "end": v(3.19, 2.46) * mm});
            skLineSegment(sketch, "E706", {"start": v(3.19, 2.46) * mm, "end": v(3.43, 2.42) * mm});
            skLineSegment(sketch, "E707", {"start": v(3.43, 2.42) * mm, "end": v(3.67, 2.38) * mm});
            skLineSegment(sketch, "E708", {"start": v(3.67, 2.38) * mm, "end": v(3.9, 2.33) * mm});
            skLineSegment(sketch, "E709", {"start": v(3.9, 2.33) * mm, "end": v(4.13, 2.28) * mm});
            skLineSegment(sketch, "E710", {"start": v(4.13, 2.28) * mm, "end": v(4.36, 2.23) * mm});
            skLineSegment(sketch, "E711", {"start": v(4.36, 2.23) * mm, "end": v(4.58, 2.18) * mm});
            skLineSegment(sketch, "E712", {"start": v(4.58, 2.18) * mm, "end": v(4.8, 2.13) * mm});
            skLineSegment(sketch, "E713", {"start": v(4.8, 2.13) * mm, "end": v(5.01, 2.07) * mm});
            skLineSegment(sketch, "E714", {"start": v(5.01, 2.07) * mm, "end": v(5.22, 2.02) * mm});
            skLineSegment(sketch, "E715", {"start": v(5.22, 2.02) * mm, "end": v(5.42, 1.96) * mm});
            skLineSegment(sketch, "E716", {"start": v(5.42, 1.96) * mm, "end": v(5.62, 1.9) * mm});
            skLineSegment(sketch, "E717", {"start": v(5.62, 1.9) * mm, "end": v(5.82, 1.83) * mm});
            skLineSegment(sketch, "E718", {"start": v(5.82, 1.83) * mm, "end": v(6.01, 1.77) * mm});
            skLineSegment(sketch, "E719", {"start": v(6.01, 1.77) * mm, "end": v(6.2, 1.7) * mm});
            skLineSegment(sketch, "E720", {"start": v(6.2, 1.7) * mm, "end": v(6.38, 1.63) * mm});
            skLineSegment(sketch, "E721", {"start": v(6.38, 1.63) * mm, "end": v(6.56, 1.56) * mm});
            skLineSegment(sketch, "E722", {"start": v(6.56, 1.56) * mm, "end": v(6.74, 1.48) * mm});
            skLineSegment(sketch, "E723", {"start": v(6.74, 1.48) * mm, "end": v(6.9, 1.4) * mm});
            skLineSegment(sketch, "E724", {"start": v(6.9, 1.4) * mm, "end": v(7.08, 1.33) * mm});
            skLineSegment(sketch, "E725", {"start": v(7.08, 1.33) * mm, "end": v(7.24, 1.25) * mm});
            skLineSegment(sketch, "E726", {"start": v(7.24, 1.25) * mm, "end": v(7.4, 1.16) * mm});
            skLineSegment(sketch, "E727", {"start": v(7.4, 1.16) * mm, "end": v(7.56, 1.08) * mm});
            skLineSegment(sketch, "E728", {"start": v(7.56, 1.08) * mm, "end": v(7.7, 0.99) * mm});
            skLineSegment(sketch, "E729", {"start": v(7.7, 0.99) * mm, "end": v(7.86, 0.9) * mm});
            skLineSegment(sketch, "E730", {"start": v(7.86, 0.9) * mm, "end": v(8, 0.8) * mm});
            skLineSegment(sketch, "E731", {"start": v(8, 0.8) * mm, "end": v(8.14, 0.71) * mm});
            skLineSegment(sketch, "E732", {"start": v(8.14, 0.71) * mm, "end": v(8.28, 0.61) * mm});
            skLineSegment(sketch, "E733", {"start": v(8.28, 0.61) * mm, "end": v(8.41, 0.51) * mm});
            skLineSegment(sketch, "E734", {"start": v(8.41, 0.51) * mm, "end": v(8.54, 0.41) * mm});
            skLineSegment(sketch, "E735", {"start": v(8.54, 0.41) * mm, "end": v(8.67, 0.3) * mm});
            skLineSegment(sketch, "E736", {"start": v(8.67, 0.3) * mm, "end": v(8.8, 0.2) * mm});
            skLineSegment(sketch, "E737", {"start": v(8.8, 0.2) * mm, "end": v(8.91, 0.09) * mm});
            skLineSegment(sketch, "E738", {"start": v(8.91, 0.09) * mm, "end": v(9.03, -0.03) * mm});
            skLineSegment(sketch, "E739", {"start": v(9.03, -0.03) * mm, "end": v(9.14, -0.14) * mm});
            skLineSegment(sketch, "E740", {"start": v(9.14, -0.14) * mm, "end": v(9.25, -0.26) * mm});
            skLineSegment(sketch, "E741", {"start": v(9.25, -0.26) * mm, "end": v(9.36, -0.38) * mm});
            skLineSegment(sketch, "E742", {"start": v(9.36, -0.38) * mm, "end": v(9.46, -0.5) * mm});
            skLineSegment(sketch, "E743", {"start": v(9.46, -0.5) * mm, "end": v(9.56, -0.63) * mm});
            skLineSegment(sketch, "E744", {"start": v(9.56, -0.63) * mm, "end": v(9.66, -0.76) * mm});
            skLineSegment(sketch, "E745", {"start": v(9.66, -0.76) * mm, "end": v(9.75, -0.9) * mm});
            skLineSegment(sketch, "E746", {"start": v(9.75, -0.9) * mm, "end": v(9.84, -1.03) * mm});
            skLineSegment(sketch, "E747", {"start": v(9.84, -1.03) * mm, "end": v(9.93, -1.17) * mm});
            skLineSegment(sketch, "E748", {"start": v(9.93, -1.17) * mm, "end": v(10.01, -1.3) * mm});
            skLineSegment(sketch, "E749", {"start": v(10.01, -1.3) * mm, "end": v(10.1, -1.45) * mm});
            skLineSegment(sketch, "E750", {"start": v(10.1, -1.45) * mm, "end": v(10.17, -1.6) * mm});
            skLineSegment(sketch, "E751", {"start": v(10.17, -1.6) * mm, "end": v(10.24, -1.75) * mm});
            skLineSegment(sketch, "E752", {"start": v(10.24, -1.75) * mm, "end": v(10.32, -1.9) * mm});
            skLineSegment(sketch, "E753", {"start": v(10.32, -1.9) * mm, "end": v(10.39, -2.06) * mm});
            skLineSegment(sketch, "E754", {"start": v(10.39, -2.06) * mm, "end": v(10.45, -2.22) * mm});
            skLineSegment(sketch, "E755", {"start": v(10.45, -2.22) * mm, "end": v(10.52, -2.38) * mm});
            skLineSegment(sketch, "E756", {"start": v(10.52, -2.38) * mm, "end": v(10.58, -2.55) * mm});
            skLineSegment(sketch, "E757", {"start": v(10.58, -2.55) * mm, "end": v(10.63, -2.72) * mm});
            skLineSegment(sketch, "E758", {"start": v(10.63, -2.72) * mm, "end": v(10.69, -2.89) * mm});
            skLineSegment(sketch, "E759", {"start": v(10.69, -2.89) * mm, "end": v(10.74, -3.06) * mm});
            skLineSegment(sketch, "E760", {"start": v(10.74, -3.06) * mm, "end": v(10.8, -3.24) * mm});
            skLineSegment(sketch, "E761", {"start": v(10.8, -3.24) * mm, "end": v(10.84, -3.42) * mm});
            skLineSegment(sketch, "E762", {"start": v(10.84, -3.42) * mm, "end": v(10.88, -3.6) * mm});
            skLineSegment(sketch, "E763", {"start": v(10.88, -3.6) * mm, "end": v(10.92, -3.8) * mm});
            skLineSegment(sketch, "E764", {"start": v(10.92, -3.8) * mm, "end": v(10.96, -3.99) * mm});
            skLineSegment(sketch, "E765", {"start": v(10.96, -3.99) * mm, "end": v(11, -4.18) * mm});
            skLineSegment(sketch, "E766", {"start": v(11, -4.18) * mm, "end": v(11.03, -4.38) * mm});
            skLineSegment(sketch, "E767", {"start": v(11.03, -4.38) * mm, "end": v(11.07, -4.58) * mm});
            skLineSegment(sketch, "E768", {"start": v(11.07, -4.58) * mm, "end": v(11.1, -4.83) * mm});
            skLineSegment(sketch, "E769", {"start": v(11.1, -4.83) * mm, "end": v(11.13, -5.07) * mm});
            skLineSegment(sketch, "E770", {"start": v(11.13, -5.07) * mm, "end": v(11.16, -5.3) * mm});
            skLineSegment(sketch, "E771", {"start": v(11.16, -5.3) * mm, "end": v(11.18, -5.54) * mm});
            skLineSegment(sketch, "E772", {"start": v(11.18, -5.54) * mm, "end": v(11.2, -5.78) * mm});
            skLineSegment(sketch, "E773", {"start": v(11.2, -5.78) * mm, "end": v(11.22, -6) * mm});
            skLineSegment(sketch, "E774", {"start": v(11.22, -6) * mm, "end": v(11.23, -6.23) * mm});
            skLineSegment(sketch, "E775", {"start": v(11.23, -6.23) * mm, "end": v(11.24, -6.46) * mm});
            skLineSegment(sketch, "E776", {"start": v(11.24, -6.46) * mm, "end": v(11.25, -6.68) * mm});
            skLineSegment(sketch, "E777", {"start": v(11.25, -6.68) * mm, "end": v(11.25, -6.9) * mm});
            skLineSegment(sketch, "E778", {"start": v(11.25, -6.9) * mm, "end": v(11.24, -7.11) * mm});
            skLineSegment(sketch, "E779", {"start": v(11.24, -7.11) * mm, "end": v(11.23, -7.33) * mm});
            skLineSegment(sketch, "E780", {"start": v(11.23, -7.33) * mm, "end": v(11.22, -7.54) * mm});
            skLineSegment(sketch, "E781", {"start": v(11.22, -7.54) * mm, "end": v(11.2, -7.74) * mm});
            skLineSegment(sketch, "E782", {"start": v(11.2, -7.74) * mm, "end": v(11.19, -7.95) * mm});
            skLineSegment(sketch, "E783", {"start": v(11.19, -7.95) * mm, "end": v(11.16, -8.15) * mm});
            skLineSegment(sketch, "E784", {"start": v(11.16, -8.15) * mm, "end": v(11.13, -8.35) * mm});
            skLineSegment(sketch, "E785", {"start": v(11.13, -8.35) * mm, "end": v(11.1, -8.55) * mm});
            skLineSegment(sketch, "E786", {"start": v(11.1, -8.55) * mm, "end": v(11.07, -8.74) * mm});
            skLineSegment(sketch, "E787", {"start": v(11.07, -8.74) * mm, "end": v(11.02, -8.93) * mm});
            skLineSegment(sketch, "E788", {"start": v(11.02, -8.93) * mm, "end": v(10.98, -9.12) * mm});
            skLineSegment(sketch, "E789", {"start": v(10.98, -9.12) * mm, "end": v(10.93, -9.3) * mm});
            skLineSegment(sketch, "E790", {"start": v(10.93, -9.3) * mm, "end": v(10.88, -9.5) * mm});
            skLineSegment(sketch, "E791", {"start": v(10.88, -9.5) * mm, "end": v(10.82, -9.68) * mm});
            skLineSegment(sketch, "E792", {"start": v(10.82, -9.68) * mm, "end": v(10.76, -9.86) * mm});
            skLineSegment(sketch, "E793", {"start": v(10.76, -9.86) * mm, "end": v(10.7, -10.03) * mm});
            skLineSegment(sketch, "E794", {"start": v(10.7, -10.03) * mm, "end": v(10.62, -10.21) * mm});
            skLineSegment(sketch, "E795", {"start": v(10.62, -10.21) * mm, "end": v(10.55, -10.38) * mm});
            skLineSegment(sketch, "E796", {"start": v(10.55, -10.38) * mm, "end": v(10.47, -10.56) * mm});
            skLineSegment(sketch, "E797", {"start": v(10.47, -10.56) * mm, "end": v(10.38, -10.72) * mm});
            skLineSegment(sketch, "E798", {"start": v(10.38, -10.72) * mm, "end": v(10.3, -10.9) * mm});
            skLineSegment(sketch, "E799", {"start": v(10.3, -10.9) * mm, "end": v(10.2, -11.06) * mm});
            skLineSegment(sketch, "E800", {"start": v(10.2, -11.06) * mm, "end": v(10.1, -11.22) * mm});
            skLineSegment(sketch, "E801", {"start": v(10.1, -11.22) * mm, "end": v(10, -11.38) * mm});
            skLineSegment(sketch, "E802", {"start": v(10, -11.38) * mm, "end": v(9.9, -11.54) * mm});
            skLineSegment(sketch, "E803", {"start": v(9.9, -11.54) * mm, "end": v(9.79, -11.7) * mm});
            skLineSegment(sketch, "E804", {"start": v(9.79, -11.7) * mm, "end": v(9.67, -11.85) * mm});
            skLineSegment(sketch, "E805", {"start": v(9.67, -11.85) * mm, "end": v(9.55, -12) * mm});
            skLineSegment(sketch, "E806", {"start": v(9.55, -12) * mm, "end": v(9.43, -12.16) * mm});
            skLineSegment(sketch, "E807", {"start": v(9.43, -12.16) * mm, "end": v(9.3, -12.3) * mm});
            skLineSegment(sketch, "E808", {"start": v(9.3, -12.3) * mm, "end": v(9.17, -12.45) * mm});
            skLineSegment(sketch, "E809", {"start": v(9.17, -12.45) * mm, "end": v(9.03, -12.6) * mm});
            skLineSegment(sketch, "E810", {"start": v(9.03, -12.6) * mm, "end": v(8.89, -12.74) * mm});
            skLineSegment(sketch, "E811", {"start": v(8.89, -12.74) * mm, "end": v(8.74, -12.89) * mm});
            skLineSegment(sketch, "E812", {"start": v(8.74, -12.89) * mm, "end": v(8.59, -13.03) * mm});
            skLineSegment(sketch, "E813", {"start": v(8.59, -13.03) * mm, "end": v(8.43, -13.17) * mm});
            skLineSegment(sketch, "E814", {"start": v(8.43, -13.17) * mm, "end": v(8.27, -13.3) * mm});
            skLineSegment(sketch, "E815", {"start": v(8.27, -13.3) * mm, "end": v(8.1, -13.44) * mm});
            skLineSegment(sketch, "E816", {"start": v(8.1, -13.44) * mm, "end": v(7.93, -13.57) * mm});
            skLineSegment(sketch, "E817", {"start": v(7.93, -13.57) * mm, "end": v(7.76, -13.7) * mm});
            skLineSegment(sketch, "E818", {"start": v(7.76, -13.7) * mm, "end": v(7.58, -13.84) * mm});
            skLineSegment(sketch, "E819", {"start": v(7.58, -13.84) * mm, "end": v(7.4, -13.97) * mm});
            skLineSegment(sketch, "E820", {"start": v(7.4, -13.97) * mm, "end": v(7.2, -14.1) * mm});
            skLineSegment(sketch, "E821", {"start": v(7.2, -14.1) * mm, "end": v(7, -14.23) * mm});
            skLineSegment(sketch, "E822", {"start": v(7, -14.23) * mm, "end": v(6.8, -14.35) * mm});
            skLineSegment(sketch, "E823", {"start": v(6.8, -14.35) * mm, "end": v(6.6, -14.48) * mm});
            skLineSegment(sketch, "E824", {"start": v(6.6, -14.48) * mm, "end": v(6.4, -14.6) * mm});
            skLineSegment(sketch, "E825", {"start": v(6.4, -14.6) * mm, "end": v(6.18, -14.72) * mm});
            skLineSegment(sketch, "E826", {"start": v(6.18, -14.72) * mm, "end": v(5.96, -14.85) * mm});
            skLineSegment(sketch, "E827", {"start": v(5.96, -14.85) * mm, "end": v(5.73, -14.97) * mm});
            skLineSegment(sketch, "E828", {"start": v(5.73, -14.97) * mm, "end": v(5.5, -15.08) * mm});
            skLineSegment(sketch, "E829", {"start": v(5.5, -15.08) * mm, "end": v(5.27, -15.2) * mm});
            skLineSegment(sketch, "E830", {"start": v(5.27, -15.2) * mm, "end": v(5.03, -15.32) * mm});
            skLineSegment(sketch, "E831", {"start": v(5.03, -15.32) * mm, "end": v(4.78, -15.44) * mm});
            skLineSegment(sketch, "E832", {"start": v(4.78, -15.44) * mm, "end": v(4.79, -15.53) * mm});
            skLineSegment(sketch, "E833", {"start": v(4.79, -15.53) * mm, "end": v(4.8, -15.63) * mm});
            skLineSegment(sketch, "E834", {"start": v(4.8, -15.63) * mm, "end": v(4.8, -15.73) * mm});
            skLineSegment(sketch, "E835", {"start": v(4.8, -15.73) * mm, "end": v(4.8, -15.82) * mm});
            skLineSegment(sketch, "E836", {"start": v(4.8, -15.82) * mm, "end": v(4.81, -15.92) * mm});
            skLineSegment(sketch, "E837", {"start": v(4.81, -15.92) * mm, "end": v(4.82, -16.02) * mm});
            skLineSegment(sketch, "E838", {"start": v(4.82, -16.02) * mm, "end": v(4.83, -16.11) * mm});
            skLineSegment(sketch, "E839", {"start": v(4.83, -16.11) * mm, "end": v(4.84, -16.21) * mm});
            skLineSegment(sketch, "E840", {"start": v(4.84, -16.21) * mm, "end": v(4.84, -16.3) * mm});
            skLineSegment(sketch, "E841", {"start": v(4.84, -16.3) * mm, "end": v(4.85, -16.4) * mm});
            skLineSegment(sketch, "E842", {"start": v(4.85, -16.4) * mm, "end": v(4.86, -16.5) * mm});
            skLineSegment(sketch, "E843", {"start": v(4.86, -16.5) * mm, "end": v(4.86, -16.6) * mm});
            skLineSegment(sketch, "E844", {"start": v(4.86, -16.6) * mm, "end": v(4.87, -16.7) * mm});
            skLineSegment(sketch, "E845", {"start": v(4.87, -16.7) * mm, "end": v(4.88, -16.8) * mm});
            skLineSegment(sketch, "E846", {"start": v(4.88, -16.8) * mm, "end": v(4.88, -16.9) * mm});
            skLineSegment(sketch, "E847", {"start": v(4.88, -16.9) * mm, "end": v(4.9, -16.99) * mm});
            skLineSegment(sketch, "E848", {"start": v(4.9, -16.99) * mm, "end": v(4.9, -17.09) * mm});
            skLineSegment(sketch, "E849", {"start": v(4.9, -17.09) * mm, "end": v(4.9, -17.18) * mm});
            skLineSegment(sketch, "E850", {"start": v(4.9, -17.18) * mm, "end": v(4.91, -17.28) * mm});
            skLineSegment(sketch, "E851", {"start": v(4.91, -17.28) * mm, "end": v(4.92, -17.38) * mm});
            skLineSegment(sketch, "E852", {"start": v(4.92, -17.38) * mm, "end": v(4.93, -17.48) * mm});
            skLineSegment(sketch, "E853", {"start": v(4.93, -17.48) * mm, "end": v(4.93, -17.57) * mm});
            skLineSegment(sketch, "E854", {"start": v(4.93, -17.57) * mm, "end": v(4.94, -17.67) * mm});
            skLineSegment(sketch, "E855", {"start": v(4.94, -17.67) * mm, "end": v(4.95, -17.77) * mm});
            skLineSegment(sketch, "E856", {"start": v(4.95, -17.77) * mm, "end": v(4.96, -17.87) * mm});
            skLineSegment(sketch, "E857", {"start": v(4.96, -17.87) * mm, "end": v(4.96, -17.97) * mm});
            skLineSegment(sketch, "E858", {"start": v(4.96, -17.97) * mm, "end": v(4.97, -18.06) * mm});
            skLineSegment(sketch, "E859", {"start": v(4.97, -18.06) * mm, "end": v(4.98, -18.16) * mm});
            skLineSegment(sketch, "E860", {"start": v(4.98, -18.16) * mm, "end": v(4.98, -18.26) * mm});
            skLineSegment(sketch, "E861", {"start": v(4.98, -18.26) * mm, "end": v(5, -18.36) * mm});
            skLineSegment(sketch, "E862", {"start": v(5, -18.36) * mm, "end": v(5, -18.46) * mm});
            skLineSegment(sketch, "E863", {"start": v(5, -18.46) * mm, "end": v(5, -18.55) * mm});
            skLineSegment(sketch, "E864", {"start": v(5, -18.55) * mm, "end": v(5.01, -18.65) * mm});
            skLineSegment(sketch, "E865", {"start": v(5.01, -18.65) * mm, "end": v(5.02, -18.75) * mm});
            skLineSegment(sketch, "E866", {"start": v(5.02, -18.75) * mm, "end": v(5.02, -18.85) * mm});
            skLineSegment(sketch, "E867", {"start": v(5.02, -18.85) * mm, "end": v(5.03, -18.95) * mm});
            skLineSegment(sketch, "E868", {"start": v(5.03, -18.95) * mm, "end": v(5.04, -19.04) * mm});
            skLineSegment(sketch, "E869", {"start": v(5.04, -19.04) * mm, "end": v(5.04, -19.14) * mm});
            skLineSegment(sketch, "E870", {"start": v(5.04, -19.14) * mm, "end": v(5.05, -19.24) * mm});
            skLineSegment(sketch, "E871", {"start": v(5.05, -19.24) * mm, "end": v(5.06, -19.34) * mm});
            skLineSegment(sketch, "E872", {"start": v(5.06, -19.34) * mm, "end": v(5.06, -19.44) * mm});
            skLineSegment(sketch, "E873", {"start": v(5.06, -19.44) * mm, "end": v(5.07, -19.53) * mm});
            skLineSegment(sketch, "E874", {"start": v(5.07, -19.53) * mm, "end": v(5.08, -19.63) * mm});
            skLineSegment(sketch, "E875", {"start": v(5.08, -19.63) * mm, "end": v(5.08, -19.73) * mm});
            skLineSegment(sketch, "E876", {"start": v(5.08, -19.73) * mm, "end": v(5.09, -19.83) * mm});
            skLineSegment(sketch, "E877", {"start": v(5.09, -19.83) * mm, "end": v(5.1, -19.93) * mm});
            skLineSegment(sketch, "E878", {"start": v(5.1, -19.93) * mm, "end": v(5.1, -20.03) * mm});
            skLineSegment(sketch, "E879", {"start": v(5.1, -20.03) * mm, "end": v(5.1, -20.12) * mm});
            skLineSegment(sketch, "E880", {"start": v(5.1, -20.12) * mm, "end": v(5.11, -20.22) * mm});
            skLineSegment(sketch, "E881", {"start": v(5.11, -20.22) * mm, "end": v(5.12, -20.32) * mm});
            skLineSegment(sketch, "E882", {"start": v(5.12, -20.32) * mm, "end": v(5.13, -20.42) * mm});
            skLineSegment(sketch, "E883", {"start": v(5.13, -20.42) * mm, "end": v(5.13, -20.52) * mm});
            skLineSegment(sketch, "E884", {"start": v(5.13, -20.52) * mm, "end": v(5.14, -20.62) * mm});
            skLineSegment(sketch, "E885", {"start": v(5.14, -20.62) * mm, "end": v(5.14, -20.72) * mm});
            skLineSegment(sketch, "E886", {"start": v(5.14, -20.72) * mm, "end": v(5.15, -20.81) * mm});
            skLineSegment(sketch, "E887", {"start": v(5.15, -20.81) * mm, "end": v(5.15, -20.91) * mm});
            skLineSegment(sketch, "E888", {"start": v(5.15, -20.91) * mm, "end": v(5.16, -21.01) * mm});
            skLineSegment(sketch, "E889", {"start": v(5.16, -21.01) * mm, "end": v(5.16, -21.1) * mm});
            skLineSegment(sketch, "E890", {"start": v(5.16, -21.1) * mm, "end": v(5.17, -21.2) * mm});
            skLineSegment(sketch, "E891", {"start": v(5.17, -21.2) * mm, "end": v(5.17, -21.3) * mm});
            skLineSegment(sketch, "E892", {"start": v(5.17, -21.3) * mm, "end": v(5.18, -21.4) * mm});
            skLineSegment(sketch, "E893", {"start": v(5.18, -21.4) * mm, "end": v(5.18, -21.5) * mm});
            skLineSegment(sketch, "E894", {"start": v(5.18, -21.5) * mm, "end": v(5.19, -21.6) * mm});
            skLineSegment(sketch, "E895", {"start": v(5.19, -21.6) * mm, "end": v(5.2, -21.7) * mm});
            skLineSegment(sketch, "E896", {"start": v(5.2, -21.7) * mm, "end": v(5.2, -21.76) * mm});
            skLineSegment(sketch, "E897", {"start": v(5.2, -21.76) * mm, "end": v(5.2, -21.82) * mm});
            skLineSegment(sketch, "E898", {"start": v(5.2, -21.82) * mm, "end": v(5.2, -21.88) * mm});
            skLineSegment(sketch, "E899", {"start": v(5.2, -21.88) * mm, "end": v(5.2, -21.94) * mm});
            skLineSegment(sketch, "E900", {"start": v(5.2, -21.94) * mm, "end": v(5.2, -22) * mm});
            skLineSegment(sketch, "E901", {"start": v(5.2, -22) * mm, "end": v(5.2, -22.06) * mm});
            skLineSegment(sketch, "E902", {"start": v(5.2, -22.06) * mm, "end": v(5.2, -22.12) * mm});
            skLineSegment(sketch, "E903", {"start": v(5.2, -22.12) * mm, "end": v(5.2, -22.18) * mm});
            skLineSegment(sketch, "E904", {"start": v(5.2, -22.18) * mm, "end": v(5.2, -22.24) * mm});
            skLineSegment(sketch, "E905", {"start": v(5.2, -22.24) * mm, "end": v(5.21, -22.3) * mm});
            skLineSegment(sketch, "E906", {"start": v(5.21, -22.3) * mm, "end": v(5.21, -22.36) * mm});
            skLineSegment(sketch, "E907", {"start": v(5.21, -22.36) * mm, "end": v(5.21, -22.42) * mm});
            skLineSegment(sketch, "E908", {"start": v(5.21, -22.42) * mm, "end": v(5.22, -22.48) * mm});
            skLineSegment(sketch, "E909", {"start": v(5.22, -22.48) * mm, "end": v(5.22, -22.54) * mm});
            skLineSegment(sketch, "E910", {"start": v(5.22, -22.54) * mm, "end": v(5.22, -22.6) * mm});
            skLineSegment(sketch, "E911", {"start": v(5.22, -22.6) * mm, "end": v(5.22, -22.67) * mm});
            skLineSegment(sketch, "E912", {"start": v(5.22, -22.67) * mm, "end": v(5.22, -22.73) * mm});
            skLineSegment(sketch, "E913", {"start": v(5.22, -22.73) * mm, "end": v(5.22, -22.79) * mm});
            skLineSegment(sketch, "E914", {"start": v(5.22, -22.79) * mm, "end": v(5.22, -22.85) * mm});
            skLineSegment(sketch, "E915", {"start": v(5.22, -22.85) * mm, "end": v(5.22, -22.9) * mm});
            skLineSegment(sketch, "E916", {"start": v(5.22, -22.9) * mm, "end": v(5.22, -22.97) * mm});
            skLineSegment(sketch, "E917", {"start": v(5.22, -22.97) * mm, "end": v(5.22, -23.03) * mm});
            skLineSegment(sketch, "E918", {"start": v(5.22, -23.03) * mm, "end": v(5.22, -23.09) * mm});
            skLineSegment(sketch, "E919", {"start": v(5.22, -23.09) * mm, "end": v(5.22, -23.15) * mm});
            skLineSegment(sketch, "E920", {"start": v(5.22, -23.15) * mm, "end": v(5.22, -23.2) * mm});
            skLineSegment(sketch, "E921", {"start": v(5.22, -23.2) * mm, "end": v(5.22, -23.27) * mm});
            skLineSegment(sketch, "E922", {"start": v(5.22, -23.27) * mm, "end": v(5.22, -23.33) * mm});
            skLineSegment(sketch, "E923", {"start": v(5.22, -23.33) * mm, "end": v(5.22, -23.4) * mm});
            skLineSegment(sketch, "E924", {"start": v(5.22, -23.4) * mm, "end": v(5.22, -23.45) * mm});
            skLineSegment(sketch, "E925", {"start": v(5.22, -23.45) * mm, "end": v(5.22, -23.51) * mm});
            skLineSegment(sketch, "E926", {"start": v(5.22, -23.51) * mm, "end": v(5.22, -23.57) * mm});
            skLineSegment(sketch, "E927", {"start": v(5.22, -23.57) * mm, "end": v(5.22, -23.63) * mm});
            skLineSegment(sketch, "E928", {"start": v(5.22, -23.63) * mm, "end": v(5.22, -23.7) * mm});
            skLineSegment(sketch, "E929", {"start": v(5.22, -23.7) * mm, "end": v(5.22, -23.75) * mm});
            skLineSegment(sketch, "E930", {"start": v(5.22, -23.75) * mm, "end": v(5.22, -23.81) * mm});
            skLineSegment(sketch, "E931", {"start": v(5.22, -23.81) * mm, "end": v(5.22, -23.87) * mm});
            skLineSegment(sketch, "E932", {"start": v(5.22, -23.87) * mm, "end": v(5.21, -23.93) * mm});
            skLineSegment(sketch, "E933", {"start": v(5.21, -23.93) * mm, "end": v(5.21, -24) * mm});
            skLineSegment(sketch, "E934", {"start": v(5.21, -24) * mm, "end": v(5.21, -24.06) * mm});
            skLineSegment(sketch, "E935", {"start": v(5.21, -24.06) * mm, "end": v(5.2, -24.12) * mm});
            skLineSegment(sketch, "E936", {"start": v(5.2, -24.12) * mm, "end": v(5.2, -24.18) * mm});
            skLineSegment(sketch, "E937", {"start": v(5.2, -24.18) * mm, "end": v(5.2, -24.24) * mm});
            skLineSegment(sketch, "E938", {"start": v(5.2, -24.24) * mm, "end": v(5.2, -24.3) * mm});
            skLineSegment(sketch, "E939", {"start": v(5.2, -24.3) * mm, "end": v(5.2, -24.36) * mm});
            skLineSegment(sketch, "E940", {"start": v(5.2, -24.36) * mm, "end": v(5.2, -24.42) * mm});
            skLineSegment(sketch, "E941", {"start": v(5.2, -24.42) * mm, "end": v(5.2, -24.48) * mm});
            skLineSegment(sketch, "E942", {"start": v(5.2, -24.48) * mm, "end": v(5.2, -24.54) * mm});
            skLineSegment(sketch, "E943", {"start": v(5.2, -24.54) * mm, "end": v(5.19, -24.6) * mm});
            skLineSegment(sketch, "E944", {"start": v(5.19, -24.6) * mm, "end": v(5.19, -24.66) * mm});
            skLineSegment(sketch, "E945", {"start": v(5.19, -24.66) * mm, "end": v(5.18, -24.72) * mm});
            skLineSegment(sketch, "E946", {"start": v(5.18, -24.72) * mm, "end": v(5.18, -24.78) * mm});
            skLineSegment(sketch, "E947", {"start": v(5.18, -24.78) * mm, "end": v(5.18, -24.84) * mm});
            skLineSegment(sketch, "E948", {"start": v(5.18, -24.84) * mm, "end": v(5.17, -24.9) * mm});
            skLineSegment(sketch, "E949", {"start": v(5.17, -24.9) * mm, "end": v(5.17, -24.96) * mm});
            skLineSegment(sketch, "E950", {"start": v(5.17, -24.96) * mm, "end": v(5.17, -25.02) * mm});
            skLineSegment(sketch, "E951", {"start": v(5.17, -25.02) * mm, "end": v(5.16, -25.08) * mm});
            skLineSegment(sketch, "E952", {"start": v(5.16, -25.08) * mm, "end": v(5.16, -25.14) * mm});
            skLineSegment(sketch, "E953", {"start": v(5.16, -25.14) * mm, "end": v(5.15, -25.2) * mm});
            skLineSegment(sketch, "E954", {"start": v(5.15, -25.2) * mm, "end": v(5.15, -25.26) * mm});
            skLineSegment(sketch, "E955", {"start": v(5.15, -25.26) * mm, "end": v(5.14, -25.32) * mm});
            skLineSegment(sketch, "E956", {"start": v(5.14, -25.32) * mm, "end": v(5.14, -25.38) * mm});
            skLineSegment(sketch, "E957", {"start": v(5.14, -25.38) * mm, "end": v(5.14, -25.44) * mm});
            skLineSegment(sketch, "E958", {"start": v(5.14, -25.44) * mm, "end": v(5.13, -25.5) * mm});
            skLineSegment(sketch, "E959", {"start": v(5.13, -25.5) * mm, "end": v(5.13, -25.56) * mm});
            skLineSegment(sketch, "E960", {"start": v(5.13, -25.56) * mm, "end": v(5.12, -25.67) * mm});
            skLineSegment(sketch, "E961", {"start": v(5.12, -25.67) * mm, "end": v(5.1, -25.77) * mm});
            skLineSegment(sketch, "E962", {"start": v(5.1, -25.77) * mm, "end": v(5.1, -25.88) * mm});
            skLineSegment(sketch, "E963", {"start": v(5.1, -25.88) * mm, "end": v(5.08, -25.99) * mm});
            skLineSegment(sketch, "E964", {"start": v(5.08, -25.99) * mm, "end": v(5.07, -26.1) * mm});
            skLineSegment(sketch, "E965", {"start": v(5.07, -26.1) * mm, "end": v(5.06, -26.2) * mm});
            skLineSegment(sketch, "E966", {"start": v(5.06, -26.2) * mm, "end": v(5.04, -26.3) * mm});
            skLineSegment(sketch, "E967", {"start": v(5.04, -26.3) * mm, "end": v(5.03, -26.4) * mm});
            skLineSegment(sketch, "E968", {"start": v(5.03, -26.4) * mm, "end": v(5, -26.5) * mm});
            skLineSegment(sketch, "E969", {"start": v(5, -26.5) * mm, "end": v(5, -26.61) * mm});
            skLineSegment(sketch, "E970", {"start": v(5, -26.61) * mm, "end": v(4.97, -26.71) * mm});
            skLineSegment(sketch, "E971", {"start": v(4.97, -26.71) * mm, "end": v(4.95, -26.82) * mm});
            skLineSegment(sketch, "E972", {"start": v(4.95, -26.82) * mm, "end": v(4.93, -26.92) * mm});
            skLineSegment(sketch, "E973", {"start": v(4.93, -26.92) * mm, "end": v(4.91, -27.02) * mm});
            skLineSegment(sketch, "E974", {"start": v(4.91, -27.02) * mm, "end": v(4.89, -27.12) * mm});
            skLineSegment(sketch, "E975", {"start": v(4.89, -27.12) * mm, "end": v(4.86, -27.22) * mm});
            skLineSegment(sketch, "E976", {"start": v(4.86, -27.22) * mm, "end": v(4.84, -27.32) * mm});
            skLineSegment(sketch, "E977", {"start": v(4.84, -27.32) * mm, "end": v(4.81, -27.41) * mm});
            skLineSegment(sketch, "E978", {"start": v(4.81, -27.41) * mm, "end": v(4.78, -27.51) * mm});
            skLineSegment(sketch, "E979", {"start": v(4.78, -27.51) * mm, "end": v(4.75, -27.6) * mm});
            skLineSegment(sketch, "E980", {"start": v(4.75, -27.6) * mm, "end": v(4.72, -27.7) * mm});
            skLineSegment(sketch, "E981", {"start": v(4.72, -27.7) * mm, "end": v(4.7, -27.8) * mm});
            skLineSegment(sketch, "E982", {"start": v(4.7, -27.8) * mm, "end": v(4.66, -27.9) * mm});
            skLineSegment(sketch, "E983", {"start": v(4.66, -27.9) * mm, "end": v(4.62, -27.99) * mm});
            skLineSegment(sketch, "E984", {"start": v(4.62, -27.99) * mm, "end": v(4.59, -28.08) * mm});
            skLineSegment(sketch, "E985", {"start": v(4.59, -28.08) * mm, "end": v(4.55, -28.17) * mm});
            skLineSegment(sketch, "E986", {"start": v(4.55, -28.17) * mm, "end": v(4.51, -28.26) * mm});
            skLineSegment(sketch, "E987", {"start": v(4.51, -28.26) * mm, "end": v(4.47, -28.35) * mm});
            skLineSegment(sketch, "E988", {"start": v(4.47, -28.35) * mm, "end": v(4.43, -28.44) * mm});
            skLineSegment(sketch, "E989", {"start": v(4.43, -28.44) * mm, "end": v(4.39, -28.53) * mm});
            skLineSegment(sketch, "E990", {"start": v(4.39, -28.53) * mm, "end": v(4.34, -28.61) * mm});
            skLineSegment(sketch, "E991", {"start": v(4.34, -28.61) * mm, "end": v(4.3, -28.7) * mm});
            skLineSegment(sketch, "E992", {"start": v(4.3, -28.7) * mm, "end": v(4.25, -28.78) * mm});
            skLineSegment(sketch, "E993", {"start": v(4.25, -28.78) * mm, "end": v(4.2, -28.86) * mm});
            skLineSegment(sketch, "E994", {"start": v(4.2, -28.86) * mm, "end": v(4.15, -28.95) * mm});
            skLineSegment(sketch, "E995", {"start": v(4.15, -28.95) * mm, "end": v(4.1, -29.03) * mm});
            skLineSegment(sketch, "E996", {"start": v(4.1, -29.03) * mm, "end": v(4.04, -29.1) * mm});
            skLineSegment(sketch, "E997", {"start": v(4.04, -29.1) * mm, "end": v(3.98, -29.19) * mm});
            skLineSegment(sketch, "E998", {"start": v(3.98, -29.19) * mm, "end": v(3.92, -29.26) * mm});
            skLineSegment(sketch, "E999", {"start": v(3.92, -29.26) * mm, "end": v(3.87, -29.34) * mm});
            skLineSegment(sketch, "E1000", {"start": v(3.87, -29.34) * mm, "end": v(3.8, -29.41) * mm});
            skLineSegment(sketch, "E1001", {"start": v(3.8, -29.41) * mm, "end": v(3.74, -29.49) * mm});
            skLineSegment(sketch, "E1002", {"start": v(3.74, -29.49) * mm, "end": v(3.67, -29.56) * mm});
            skLineSegment(sketch, "E1003", {"start": v(3.67, -29.56) * mm, "end": v(3.6, -29.63) * mm});
            skLineSegment(sketch, "E1004", {"start": v(3.6, -29.63) * mm, "end": v(3.54, -29.7) * mm});
            skLineSegment(sketch, "E1005", {"start": v(3.54, -29.7) * mm, "end": v(3.47, -29.76) * mm});
            skLineSegment(sketch, "E1006", {"start": v(3.47, -29.76) * mm, "end": v(3.4, -29.83) * mm});
            skLineSegment(sketch, "E1007", {"start": v(3.4, -29.83) * mm, "end": v(3.32, -29.9) * mm});
            skLineSegment(sketch, "E1008", {"start": v(3.32, -29.9) * mm, "end": v(3.24, -29.96) * mm});
            skLineSegment(sketch, "E1009", {"start": v(3.24, -29.96) * mm, "end": v(3.16, -30.02) * mm});
            skLineSegment(sketch, "E1010", {"start": v(3.16, -30.02) * mm, "end": v(3.08, -30.08) * mm});
            skLineSegment(sketch, "E1011", {"start": v(3.08, -30.08) * mm, "end": v(3, -30.14) * mm});
            skLineSegment(sketch, "E1012", {"start": v(3, -30.14) * mm, "end": v(2.9, -30.2) * mm});
            skLineSegment(sketch, "E1013", {"start": v(2.9, -30.2) * mm, "end": v(2.82, -30.25) * mm});
            skLineSegment(sketch, "E1014", {"start": v(2.82, -30.25) * mm, "end": v(2.73, -30.3) * mm});
            skLineSegment(sketch, "E1015", {"start": v(2.73, -30.3) * mm, "end": v(2.64, -30.35) * mm});
            skLineSegment(sketch, "E1016", {"start": v(2.64, -30.35) * mm, "end": v(2.55, -30.4) * mm});
            skLineSegment(sketch, "E1017", {"start": v(2.55, -30.4) * mm, "end": v(2.45, -30.45) * mm});
            skLineSegment(sketch, "E1018", {"start": v(2.45, -30.45) * mm, "end": v(2.35, -30.5) * mm});
            skLineSegment(sketch, "E1019", {"start": v(2.35, -30.5) * mm, "end": v(2.25, -30.54) * mm});
            skLineSegment(sketch, "E1020", {"start": v(2.25, -30.54) * mm, "end": v(2.14, -30.59) * mm});
            skLineSegment(sketch, "E1021", {"start": v(2.14, -30.59) * mm, "end": v(2.04, -30.63) * mm});
            skLineSegment(sketch, "E1022", {"start": v(2.04, -30.63) * mm, "end": v(1.93, -30.67) * mm});
            skLineSegment(sketch, "E1023", {"start": v(1.93, -30.67) * mm, "end": v(1.82, -30.7) * mm});
            skLineSegment(sketch, "E1024", {"start": v(1.82, -30.7) * mm, "end": v(1.7, -30.74) * mm});
            skLineSegment(sketch, "E1025", {"start": v(1.7, -30.74) * mm, "end": v(1.57, -30.78) * mm});
            skLineSegment(sketch, "E1026", {"start": v(1.57, -30.78) * mm, "end": v(1.45, -30.82) * mm});
            skLineSegment(sketch, "E1027", {"start": v(1.45, -30.82) * mm, "end": v(1.33, -30.85) * mm});
            skLineSegment(sketch, "E1028", {"start": v(1.33, -30.85) * mm, "end": v(1.2, -30.89) * mm});
            skLineSegment(sketch, "E1029", {"start": v(1.2, -30.89) * mm, "end": v(1.09, -30.92) * mm});
            skLineSegment(sketch, "E1030", {"start": v(1.09, -30.92) * mm, "end": v(0.96, -30.95) * mm});
            skLineSegment(sketch, "E1031", {"start": v(0.96, -30.95) * mm, "end": v(0.84, -30.98) * mm});
            skLineSegment(sketch, "E1032", {"start": v(0.84, -30.98) * mm, "end": v(0.72, -31) * mm});
            skLineSegment(sketch, "E1033", {"start": v(0.72, -31) * mm, "end": v(0.6, -31.04) * mm});
            skLineSegment(sketch, "E1034", {"start": v(0.6, -31.04) * mm, "end": v(0.47, -31.06) * mm});
            skLineSegment(sketch, "E1035", {"start": v(0.47, -31.06) * mm, "end": v(0.35, -31.09) * mm});
            skLineSegment(sketch, "E1036", {"start": v(0.35, -31.09) * mm, "end": v(0.23, -31.1) * mm});
            skLineSegment(sketch, "E1037", {"start": v(0.23, -31.1) * mm, "end": v(0.1, -31.13) * mm});
            skLineSegment(sketch, "E1038", {"start": v(0.1, -31.13) * mm, "end": v(-0.01, -31.15) * mm});
            skLineSegment(sketch, "E1039", {"start": v(-0.01, -31.15) * mm, "end": v(-0.14, -31.17) * mm});
            skLineSegment(sketch, "E1040", {"start": v(-0.14, -31.17) * mm, "end": v(-0.26, -31.19) * mm});
            skLineSegment(sketch, "E1041", {"start": v(-0.26, -31.19) * mm, "end": v(-0.38, -31.2) * mm});
            skLineSegment(sketch, "E1042", {"start": v(-0.38, -31.2) * mm, "end": v(-0.5, -31.22) * mm});
            skLineSegment(sketch, "E1043", {"start": v(-0.5, -31.22) * mm, "end": v(-0.62, -31.23) * mm});
            skLineSegment(sketch, "E1044", {"start": v(-0.62, -31.23) * mm, "end": v(-0.75, -31.24) * mm});
            skLineSegment(sketch, "E1045", {"start": v(-0.75, -31.24) * mm, "end": v(-0.87, -31.25) * mm});
            skLineSegment(sketch, "E1046", {"start": v(-0.87, -31.25) * mm, "end": v(-0.99, -31.26) * mm});
            skLineSegment(sketch, "E1047", {"start": v(-0.99, -31.26) * mm, "end": v(-1.11, -31.26) * mm});
            skLineSegment(sketch, "E1048", {"start": v(-1.11, -31.26) * mm, "end": v(-1.23, -31.27) * mm});
            skLineSegment(sketch, "E1049", {"start": v(-1.23, -31.27) * mm, "end": v(-1.35, -31.27) * mm});
            skLineSegment(sketch, "E1050", {"start": v(-1.35, -31.27) * mm, "end": v(-1.47, -31.27) * mm});
            skLineSegment(sketch, "E1051", {"start": v(-1.47, -31.27) * mm, "end": v(-1.6, -31.27) * mm});
            skLineSegment(sketch, "E1052", {"start": v(-1.6, -31.27) * mm, "end": v(-1.71, -31.26) * mm});
            skLineSegment(sketch, "E1053", {"start": v(-1.71, -31.26) * mm, "end": v(-1.83, -31.26) * mm});
            skLineSegment(sketch, "E1054", {"start": v(-1.83, -31.26) * mm, "end": v(-1.95, -31.25) * mm});
            skLineSegment(sketch, "E1055", {"start": v(-1.95, -31.25) * mm, "end": v(-2.07, -31.24) * mm});
            skLineSegment(sketch, "E1056", {"start": v(-2.07, -31.24) * mm, "end": v(-2.2, -31.23) * mm});
            skLineSegment(sketch, "E1057", {"start": v(-2.2, -31.23) * mm, "end": v(-2.31, -31.21) * mm});
            skLineSegment(sketch, "E1058", {"start": v(-2.31, -31.21) * mm, "end": v(-2.43, -31.2) * mm});
            skLineSegment(sketch, "E1059", {"start": v(-2.43, -31.2) * mm, "end": v(-2.55, -31.18) * mm});
            skLineSegment(sketch, "E1060", {"start": v(-2.55, -31.18) * mm, "end": v(-2.66, -31.16) * mm});
            skLineSegment(sketch, "E1061", {"start": v(-2.66, -31.16) * mm, "end": v(-2.78, -31.14) * mm});
            skLineSegment(sketch, "E1062", {"start": v(-2.78, -31.14) * mm, "end": v(-2.9, -31.11) * mm});
            skLineSegment(sketch, "E1063", {"start": v(-2.9, -31.11) * mm, "end": v(-3.02, -31.08) * mm});
            skLineSegment(sketch, "E1064", {"start": v(-3.02, -31.08) * mm, "end": v(-3.13, -31.06) * mm});
            skLineSegment(sketch, "E1065", {"start": v(-3.13, -31.06) * mm, "end": v(-3.25, -31.02) * mm});
            skLineSegment(sketch, "E1066", {"start": v(-3.25, -31.02) * mm, "end": v(-3.36, -30.99) * mm});
            skLineSegment(sketch, "E1067", {"start": v(-3.36, -30.99) * mm, "end": v(-3.48, -30.95) * mm});
            skLineSegment(sketch, "E1068", {"start": v(-3.48, -30.95) * mm, "end": v(-3.6, -30.92) * mm});
            skLineSegment(sketch, "E1069", {"start": v(-3.6, -30.92) * mm, "end": v(-3.7, -30.87) * mm});
            skLineSegment(sketch, "E1070", {"start": v(-3.7, -30.87) * mm, "end": v(-3.82, -30.83) * mm});
            skLineSegment(sketch, "E1071", {"start": v(-3.82, -30.83) * mm, "end": v(-3.94, -30.79) * mm});
            skLineSegment(sketch, "E1072", {"start": v(-3.94, -30.79) * mm, "end": v(-4.05, -30.74) * mm});
            skLineSegment(sketch, "E1073", {"start": v(-4.05, -30.74) * mm, "end": v(-4.16, -30.69) * mm});
            skLineSegment(sketch, "E1074", {"start": v(-4.16, -30.69) * mm, "end": v(-4.27, -30.63) * mm});
            skLineSegment(sketch, "E1075", {"start": v(-4.27, -30.63) * mm, "end": v(-4.38, -30.58) * mm});
            skLineSegment(sketch, "E1076", {"start": v(-4.38, -30.58) * mm, "end": v(-4.5, -30.52) * mm});
            skLineSegment(sketch, "E1077", {"start": v(-4.5, -30.52) * mm, "end": v(-4.6, -30.46) * mm});
            skLineSegment(sketch, "E1078", {"start": v(-4.6, -30.46) * mm, "end": v(-4.71, -30.4) * mm});
            skLineSegment(sketch, "E1079", {"start": v(-4.71, -30.4) * mm, "end": v(-4.82, -30.33) * mm});
            skLineSegment(sketch, "E1080", {"start": v(-4.82, -30.33) * mm, "end": v(-4.93, -30.26) * mm});
            skLineSegment(sketch, "E1081", {"start": v(-4.93, -30.26) * mm, "end": v(-5.04, -30.18) * mm});
            skLineSegment(sketch, "E1082", {"start": v(-5.04, -30.18) * mm, "end": v(-5.15, -30.1) * mm});
            skLineSegment(sketch, "E1083", {"start": v(-5.15, -30.1) * mm, "end": v(-5.25, -30.03) * mm});
            skLineSegment(sketch, "E1084", {"start": v(-5.25, -30.03) * mm, "end": v(-5.36, -29.95) * mm});
            skLineSegment(sketch, "E1085", {"start": v(-5.36, -29.95) * mm, "end": v(-5.47, -29.87) * mm});
            skLineSegment(sketch, "E1086", {"start": v(-5.47, -29.87) * mm, "end": v(-5.57, -29.78) * mm});
            skLineSegment(sketch, "E1087", {"start": v(-5.57, -29.78) * mm, "end": v(-5.68, -29.7) * mm});
            skLineSegment(sketch, "E1088", {"start": v(-5.68, -29.7) * mm, "end": v(-5.77, -29.6) * mm});
            skLineSegment(sketch, "E1089", {"start": v(-5.77, -29.6) * mm, "end": v(-5.86, -29.53) * mm});
            skLineSegment(sketch, "E1090", {"start": v(-5.86, -29.53) * mm, "end": v(-5.95, -29.44) * mm});
            skLineSegment(sketch, "E1091", {"start": v(-5.95, -29.44) * mm, "end": v(-6.04, -29.36) * mm});
            skLineSegment(sketch, "E1092", {"start": v(-6.04, -29.36) * mm, "end": v(-6.13, -29.28) * mm});
            skLineSegment(sketch, "E1093", {"start": v(-6.13, -29.28) * mm, "end": v(-6.21, -29.2) * mm});
            skLineSegment(sketch, "E1094", {"start": v(-6.21, -29.2) * mm, "end": v(-6.3, -29.1) * mm});
            skLineSegment(sketch, "E1095", {"start": v(-6.3, -29.1) * mm, "end": v(-6.38, -29.02) * mm});
            skLineSegment(sketch, "E1096", {"start": v(-6.38, -29.02) * mm, "end": v(-6.46, -28.94) * mm});
            skLineSegment(sketch, "E1097", {"start": v(-6.46, -28.94) * mm, "end": v(-6.55, -28.85) * mm});
            skLineSegment(sketch, "E1098", {"start": v(-6.55, -28.85) * mm, "end": v(-6.63, -28.76) * mm});
            skLineSegment(sketch, "E1099", {"start": v(-6.63, -28.76) * mm, "end": v(-6.7, -28.67) * mm});
            skLineSegment(sketch, "E1100", {"start": v(-6.7, -28.67) * mm, "end": v(-6.78, -28.58) * mm});
            skLineSegment(sketch, "E1101", {"start": v(-6.78, -28.58) * mm, "end": v(-6.86, -28.5) * mm});
            skLineSegment(sketch, "E1102", {"start": v(-6.86, -28.5) * mm, "end": v(-6.94, -28.4) * mm});
            skLineSegment(sketch, "E1103", {"start": v(-6.94, -28.4) * mm, "end": v(-7.01, -28.31) * mm});
            skLineSegment(sketch, "E1104", {"start": v(-7.01, -28.31) * mm, "end": v(-7.08, -28.22) * mm});
            skLineSegment(sketch, "E1105", {"start": v(-7.08, -28.22) * mm, "end": v(-7.15, -28.13) * mm});
            skLineSegment(sketch, "E1106", {"start": v(-7.15, -28.13) * mm, "end": v(-7.22, -28.03) * mm});
            skLineSegment(sketch, "E1107", {"start": v(-7.22, -28.03) * mm, "end": v(-7.3, -27.94) * mm});
            skLineSegment(sketch, "E1108", {"start": v(-7.3, -27.94) * mm, "end": v(-7.36, -27.84) * mm});
            skLineSegment(sketch, "E1109", {"start": v(-7.36, -27.84) * mm, "end": v(-7.42, -27.75) * mm});
            skLineSegment(sketch, "E1110", {"start": v(-7.42, -27.75) * mm, "end": v(-7.48, -27.65) * mm});
            skLineSegment(sketch, "E1111", {"start": v(-7.48, -27.65) * mm, "end": v(-7.55, -27.55) * mm});
            skLineSegment(sketch, "E1112", {"start": v(-7.55, -27.55) * mm, "end": v(-7.6, -27.46) * mm});
            skLineSegment(sketch, "E1113", {"start": v(-7.6, -27.46) * mm, "end": v(-7.66, -27.36) * mm});
            skLineSegment(sketch, "E1114", {"start": v(-7.66, -27.36) * mm, "end": v(-7.72, -27.26) * mm});
            skLineSegment(sketch, "E1115", {"start": v(-7.72, -27.26) * mm, "end": v(-7.77, -27.16) * mm});
            skLineSegment(sketch, "E1116", {"start": v(-7.77, -27.16) * mm, "end": v(-7.83, -27.06) * mm});
            skLineSegment(sketch, "E1117", {"start": v(-7.83, -27.06) * mm, "end": v(-7.88, -26.96) * mm});
            skLineSegment(sketch, "E1118", {"start": v(-7.88, -26.96) * mm, "end": v(-7.93, -26.85) * mm});
            skLineSegment(sketch, "E1119", {"start": v(-7.93, -26.85) * mm, "end": v(-7.97, -26.75) * mm});
            skLineSegment(sketch, "E1120", {"start": v(-7.97, -26.75) * mm, "end": v(-8.02, -26.65) * mm});
            skLineSegment(sketch, "E1121", {"start": v(-8.02, -26.65) * mm, "end": v(-8.06, -26.54) * mm});
            skLineSegment(sketch, "E1122", {"start": v(-8.06, -26.54) * mm, "end": v(-8.1, -26.44) * mm});
            skLineSegment(sketch, "E1123", {"start": v(-8.1, -26.44) * mm, "end": v(-8.14, -26.33) * mm});
            skLineSegment(sketch, "E1124", {"start": v(-8.14, -26.33) * mm, "end": v(-8.18, -26.22) * mm});
            skLineSegment(sketch, "E1125", {"start": v(-8.18, -26.22) * mm, "end": v(-8.21, -26.12) * mm});
            skLineSegment(sketch, "E1126", {"start": v(-8.21, -26.12) * mm, "end": v(-8.25, -26) * mm});
            skLineSegment(sketch, "E1127", {"start": v(-8.25, -26) * mm, "end": v(-8.28, -25.9) * mm});
            skLineSegment(sketch, "E1128", {"start": v(-8.28, -25.9) * mm, "end": v(-8.3, -25.79) * mm});
            skLineSegment(sketch, "E1129", {"start": v(-8.3, -25.79) * mm, "end": v(-8.33, -25.68) * mm});
            skLineSegment(sketch, "E1130", {"start": v(-8.33, -25.68) * mm, "end": v(-8.36, -25.56) * mm});
            skLineSegment(sketch, "E1131", {"start": v(-8.36, -25.56) * mm, "end": v(-8.38, -25.45) * mm});
            skLineSegment(sketch, "E1132", {"start": v(-8.38, -25.45) * mm, "end": v(-8.4, -25.34) * mm});
            skLineSegment(sketch, "E1133", {"start": v(-8.4, -25.34) * mm, "end": v(-8.42, -25.22) * mm});
            skLineSegment(sketch, "E1134", {"start": v(-8.42, -25.22) * mm, "end": v(-8.43, -25.1) * mm});
            skLineSegment(sketch, "E1135", {"start": v(-8.43, -25.1) * mm, "end": v(-8.44, -25) * mm});
            skLineSegment(sketch, "E1136", {"start": v(-8.44, -25) * mm, "end": v(-8.45, -24.88) * mm});
            skLineSegment(sketch, "E1137", {"start": v(-8.45, -24.88) * mm, "end": v(-8.46, -24.76) * mm});
            skLineSegment(sketch, "E1138", {"start": v(-8.46, -24.76) * mm, "end": v(-8.47, -24.64) * mm});
            skLineSegment(sketch, "E1139", {"start": v(-8.47, -24.64) * mm, "end": v(-8.47, -24.52) * mm});
            skLineSegment(sketch, "E1140", {"start": v(-8.47, -24.52) * mm, "end": v(-8.47, -24.4) * mm});
            skLineSegment(sketch, "E1141", {"start": v(-8.47, -24.4) * mm, "end": v(-8.47, -24.28) * mm});
            skLineSegment(sketch, "E1142", {"start": v(-8.47, -24.28) * mm, "end": v(-8.46, -24.16) * mm});
            skLineSegment(sketch, "E1143", {"start": v(-8.46, -24.16) * mm, "end": v(-8.46, -24.03) * mm});
            skLineSegment(sketch, "E1144", {"start": v(-8.46, -24.03) * mm, "end": v(-8.45, -23.9) * mm});
            skLineSegment(sketch, "E1145", {"start": v(-8.45, -23.9) * mm, "end": v(-8.43, -23.78) * mm});
            skLineSegment(sketch, "E1146", {"start": v(-8.43, -23.78) * mm, "end": v(-8.42, -23.66) * mm});
            skLineSegment(sketch, "E1147", {"start": v(-8.42, -23.66) * mm, "end": v(-8.4, -23.53) * mm});
            skLineSegment(sketch, "E1148", {"start": v(-8.4, -23.53) * mm, "end": v(-8.38, -23.4) * mm});
            skLineSegment(sketch, "E1149", {"start": v(-8.38, -23.4) * mm, "end": v(-8.36, -23.27) * mm});
            skLineSegment(sketch, "E1150", {"start": v(-8.36, -23.27) * mm, "end": v(-8.33, -23.14) * mm});
            skLineSegment(sketch, "E1151", {"start": v(-8.33, -23.14) * mm, "end": v(-8.3, -23.01) * mm});
            skLineSegment(sketch, "E1152", {"start": v(-8.3, -23.01) * mm, "end": v(-8.28, -22.92) * mm});
            skLineSegment(sketch, "E1153", {"start": v(-8.28, -22.92) * mm, "end": v(-8.25, -22.82) * mm});
            skLineSegment(sketch, "E1154", {"start": v(-8.25, -22.82) * mm, "end": v(-8.22, -22.73) * mm});
            skLineSegment(sketch, "E1155", {"start": v(-8.22, -22.73) * mm, "end": v(-8.2, -22.63) * mm});
            skLineSegment(sketch, "E1156", {"start": v(-8.2, -22.63) * mm, "end": v(-8.16, -22.54) * mm});
            skLineSegment(sketch, "E1157", {"start": v(-8.16, -22.54) * mm, "end": v(-8.13, -22.45) * mm});
            skLineSegment(sketch, "E1158", {"start": v(-8.13, -22.45) * mm, "end": v(-8.1, -22.36) * mm});
            skLineSegment(sketch, "E1159", {"start": v(-8.1, -22.36) * mm, "end": v(-8.05, -22.28) * mm});
            skLineSegment(sketch, "E1160", {"start": v(-8.05, -22.28) * mm, "end": v(-8.01, -22.2) * mm});
            skLineSegment(sketch, "E1161", {"start": v(-8.01, -22.2) * mm, "end": v(-7.97, -22.11) * mm});
            skLineSegment(sketch, "E1162", {"start": v(-7.97, -22.11) * mm, "end": v(-7.93, -22.03) * mm});
            skLineSegment(sketch, "E1163", {"start": v(-7.93, -22.03) * mm, "end": v(-7.88, -21.95) * mm});
            skLineSegment(sketch, "E1164", {"start": v(-7.88, -21.95) * mm, "end": v(-7.83, -21.87) * mm});
            skLineSegment(sketch, "E1165", {"start": v(-7.83, -21.87) * mm, "end": v(-7.79, -21.8) * mm});
            skLineSegment(sketch, "E1166", {"start": v(-7.79, -21.8) * mm, "end": v(-7.73, -21.72) * mm});
            skLineSegment(sketch, "E1167", {"start": v(-7.73, -21.72) * mm, "end": v(-7.68, -21.65) * mm});
            skLineSegment(sketch, "E1168", {"start": v(-7.68, -21.65) * mm, "end": v(-7.63, -21.57) * mm});
            skLineSegment(sketch, "E1169", {"start": v(-7.63, -21.57) * mm, "end": v(-7.57, -21.5) * mm});
            skLineSegment(sketch, "E1170", {"start": v(-7.57, -21.5) * mm, "end": v(-7.51, -21.44) * mm});
            skLineSegment(sketch, "E1171", {"start": v(-7.51, -21.44) * mm, "end": v(-7.46, -21.37) * mm});
            skLineSegment(sketch, "E1172", {"start": v(-7.46, -21.37) * mm, "end": v(-7.4, -21.3) * mm});
            skLineSegment(sketch, "E1173", {"start": v(-7.4, -21.3) * mm, "end": v(-7.33, -21.24) * mm});
            skLineSegment(sketch, "E1174", {"start": v(-7.33, -21.24) * mm, "end": v(-7.27, -21.18) * mm});
            skLineSegment(sketch, "E1175", {"start": v(-7.27, -21.18) * mm, "end": v(-7.2, -21.12) * mm});
            skLineSegment(sketch, "E1176", {"start": v(-7.2, -21.12) * mm, "end": v(-7.14, -21.07) * mm});
            skLineSegment(sketch, "E1177", {"start": v(-7.14, -21.07) * mm, "end": v(-7.07, -21.01) * mm});
            skLineSegment(sketch, "E1178", {"start": v(-7.07, -21.01) * mm, "end": v(-7, -20.96) * mm});
            skLineSegment(sketch, "E1179", {"start": v(-7, -20.96) * mm, "end": v(-6.93, -20.9) * mm});
            skLineSegment(sketch, "E1180", {"start": v(-6.93, -20.9) * mm, "end": v(-6.85, -20.86) * mm});
            skLineSegment(sketch, "E1181", {"start": v(-6.85, -20.86) * mm, "end": v(-6.78, -20.8) * mm});
            skLineSegment(sketch, "E1182", {"start": v(-6.78, -20.8) * mm, "end": v(-6.7, -20.76) * mm});
            skLineSegment(sketch, "E1183", {"start": v(-6.7, -20.76) * mm, "end": v(-6.63, -20.72) * mm});
            skLineSegment(sketch, "E1184", {"start": v(-6.63, -20.72) * mm, "end": v(-6.55, -20.67) * mm});
            skLineSegment(sketch, "E1185", {"start": v(-6.55, -20.67) * mm, "end": v(-6.47, -20.63) * mm});
            skLineSegment(sketch, "E1186", {"start": v(-6.47, -20.63) * mm, "end": v(-6.4, -20.6) * mm});
            skLineSegment(sketch, "E1187", {"start": v(-6.4, -20.6) * mm, "end": v(-6.31, -20.56) * mm});
            skLineSegment(sketch, "E1188", {"start": v(-6.31, -20.56) * mm, "end": v(-6.23, -20.52) * mm});
            skLineSegment(sketch, "E1189", {"start": v(-6.23, -20.52) * mm, "end": v(-6.14, -20.5) * mm});
            skLineSegment(sketch, "E1190", {"start": v(-6.14, -20.5) * mm, "end": v(-6.06, -20.46) * mm});
            skLineSegment(sketch, "E1191", {"start": v(-6.06, -20.46) * mm, "end": v(-5.97, -20.43) * mm});
            skLineSegment(sketch, "E1192", {"start": v(-5.97, -20.43) * mm, "end": v(-5.89, -20.4) * mm});
            skLineSegment(sketch, "E1193", {"start": v(-5.89, -20.4) * mm, "end": v(-5.8, -20.38) * mm});
            skLineSegment(sketch, "E1194", {"start": v(-5.8, -20.38) * mm, "end": v(-5.7, -20.36) * mm});
            skLineSegment(sketch, "E1195", {"start": v(-5.7, -20.36) * mm, "end": v(-5.62, -20.34) * mm});
            skLineSegment(sketch, "E1196", {"start": v(-5.62, -20.34) * mm, "end": v(-5.53, -20.32) * mm});
            skLineSegment(sketch, "E1197", {"start": v(-5.53, -20.32) * mm, "end": v(-5.44, -20.3) * mm});
            skLineSegment(sketch, "E1198", {"start": v(-5.44, -20.3) * mm, "end": v(-5.34, -20.28) * mm});
            skLineSegment(sketch, "E1199", {"start": v(-5.34, -20.28) * mm, "end": v(-5.25, -20.27) * mm});
            skLineSegment(sketch, "E1200", {"start": v(-5.25, -20.27) * mm, "end": v(-5.16, -20.26) * mm});
            skLineSegment(sketch, "E1201", {"start": v(-5.16, -20.26) * mm, "end": v(-5.06, -20.25) * mm});
            skLineSegment(sketch, "E1202", {"start": v(-5.06, -20.25) * mm, "end": v(-4.96, -20.25) * mm});
            skLineSegment(sketch, "E1203", {"start": v(-4.96, -20.25) * mm, "end": v(-4.87, -20.24) * mm});
            skLineSegment(sketch, "E1204", {"start": v(-4.87, -20.24) * mm, "end": v(-4.77, -20.24) * mm});
            skLineSegment(sketch, "E1205", {"start": v(-4.77, -20.24) * mm, "end": v(-4.67, -20.24) * mm});
            skLineSegment(sketch, "E1206", {"start": v(-4.67, -20.24) * mm, "end": v(-4.57, -20.24) * mm});
            skLineSegment(sketch, "E1207", {"start": v(-4.57, -20.24) * mm, "end": v(-4.47, -20.25) * mm});
            skLineSegment(sketch, "E1208", {"start": v(-4.47, -20.25) * mm, "end": v(-4.37, -20.25) * mm});
            skLineSegment(sketch, "E1209", {"start": v(-4.37, -20.25) * mm, "end": v(-4.27, -20.26) * mm});
            skLineSegment(sketch, "E1210", {"start": v(-4.27, -20.26) * mm, "end": v(-4.17, -20.27) * mm});
            skLineSegment(sketch, "E1211", {"start": v(-4.17, -20.27) * mm, "end": v(-4.07, -20.29) * mm});
            skLineSegment(sketch, "E1212", {"start": v(-4.07, -20.29) * mm, "end": v(-3.96, -20.3) * mm});
            skLineSegment(sketch, "E1213", {"start": v(-3.96, -20.3) * mm, "end": v(-3.86, -20.32) * mm});
            skLineSegment(sketch, "E1214", {"start": v(-3.86, -20.32) * mm, "end": v(-3.76, -20.34) * mm});
            skLineSegment(sketch, "E1215", {"start": v(-3.76, -20.34) * mm, "end": v(-3.65, -20.36) * mm});
            skLineSegment(sketch, "E1216", {"start": v(-3.65, -20.36) * mm, "end": v(-3.56, -20.38) * mm});
            skLineSegment(sketch, "E1217", {"start": v(-3.56, -20.38) * mm, "end": v(-3.47, -20.4) * mm});
            skLineSegment(sketch, "E1218", {"start": v(-3.47, -20.4) * mm, "end": v(-3.38, -20.43) * mm});
            skLineSegment(sketch, "E1219", {"start": v(-3.38, -20.43) * mm, "end": v(-3.29, -20.45) * mm});
            skLineSegment(sketch, "E1220", {"start": v(-3.29, -20.45) * mm, "end": v(-3.2, -20.48) * mm});
            skLineSegment(sketch, "E1221", {"start": v(-3.2, -20.48) * mm, "end": v(-3.11, -20.51) * mm});
            skLineSegment(sketch, "E1222", {"start": v(-3.11, -20.51) * mm, "end": v(-3.03, -20.54) * mm});
            skLineSegment(sketch, "E1223", {"start": v(-3.03, -20.54) * mm, "end": v(-2.95, -20.57) * mm});
            skLineSegment(sketch, "E1224", {"start": v(-2.95, -20.57) * mm, "end": v(-2.87, -20.6) * mm});
            skLineSegment(sketch, "E1225", {"start": v(-2.87, -20.6) * mm, "end": v(-2.79, -20.64) * mm});
            skLineSegment(sketch, "E1226", {"start": v(-2.79, -20.64) * mm, "end": v(-2.7, -20.68) * mm});
            skLineSegment(sketch, "E1227", {"start": v(-2.7, -20.68) * mm, "end": v(-2.63, -20.72) * mm});
            skLineSegment(sketch, "E1228", {"start": v(-2.63, -20.72) * mm, "end": v(-2.56, -20.76) * mm});
            skLineSegment(sketch, "E1229", {"start": v(-2.56, -20.76) * mm, "end": v(-2.49, -20.8) * mm});
            skLineSegment(sketch, "E1230", {"start": v(-2.49, -20.8) * mm, "end": v(-2.41, -20.84) * mm});
            skLineSegment(sketch, "E1231", {"start": v(-2.41, -20.84) * mm, "end": v(-2.34, -20.88) * mm});
            skLineSegment(sketch, "E1232", {"start": v(-2.34, -20.88) * mm, "end": v(-2.28, -20.93) * mm});
            skLineSegment(sketch, "E1233", {"start": v(-2.28, -20.93) * mm, "end": v(-2.2, -20.98) * mm});
            skLineSegment(sketch, "E1234", {"start": v(-2.2, -20.98) * mm, "end": v(-2.14, -21.02) * mm});
            skLineSegment(sketch, "E1235", {"start": v(-2.14, -21.02) * mm, "end": v(-2.08, -21.07) * mm});
            skLineSegment(sketch, "E1236", {"start": v(-2.08, -21.07) * mm, "end": v(-2.02, -21.13) * mm});
            skLineSegment(sketch, "E1237", {"start": v(-2.02, -21.13) * mm, "end": v(-1.96, -21.18) * mm});
            skLineSegment(sketch, "E1238", {"start": v(-1.96, -21.18) * mm, "end": v(-1.9, -21.23) * mm});
            skLineSegment(sketch, "E1239", {"start": v(-1.9, -21.23) * mm, "end": v(-1.85, -21.29) * mm});
            skLineSegment(sketch, "E1240", {"start": v(-1.85, -21.29) * mm, "end": v(-1.8, -21.34) * mm});
            skLineSegment(sketch, "E1241", {"start": v(-1.8, -21.34) * mm, "end": v(-1.74, -21.4) * mm});
            skLineSegment(sketch, "E1242", {"start": v(-1.74, -21.4) * mm, "end": v(-1.69, -21.46) * mm});
            skLineSegment(sketch, "E1243", {"start": v(-1.69, -21.46) * mm, "end": v(-1.64, -21.52) * mm});
            skLineSegment(sketch, "E1244", {"start": v(-1.64, -21.52) * mm, "end": v(-1.6, -21.58) * mm});
            skLineSegment(sketch, "E1245", {"start": v(-1.6, -21.58) * mm, "end": v(-1.55, -21.64) * mm});
            skLineSegment(sketch, "E1246", {"start": v(-1.55, -21.64) * mm, "end": v(-1.5, -21.7) * mm});
            skLineSegment(sketch, "E1247", {"start": v(-1.5, -21.7) * mm, "end": v(-1.46, -21.77) * mm});
            skLineSegment(sketch, "E1248", {"start": v(-1.46, -21.77) * mm, "end": v(-1.43, -21.84) * mm});
            skLineSegment(sketch, "E1249", {"start": v(-1.43, -21.84) * mm, "end": v(-1.39, -21.9) * mm});
            skLineSegment(sketch, "E1250", {"start": v(-1.39, -21.9) * mm, "end": v(-1.35, -21.98) * mm});
            skLineSegment(sketch, "E1251", {"start": v(-1.35, -21.98) * mm, "end": v(-1.32, -22.05) * mm});
            skLineSegment(sketch, "E1252", {"start": v(-1.32, -22.05) * mm, "end": v(-1.29, -22.12) * mm});
            skLineSegment(sketch, "E1253", {"start": v(-1.29, -22.12) * mm, "end": v(-1.26, -22.2) * mm});
            skLineSegment(sketch, "E1254", {"start": v(-1.26, -22.2) * mm, "end": v(-1.23, -22.27) * mm});
            skLineSegment(sketch, "E1255", {"start": v(-1.23, -22.27) * mm, "end": v(-1.2, -22.34) * mm});
            skLineSegment(sketch, "E1256", {"start": v(-1.2, -22.34) * mm, "end": v(-1.18, -22.42) * mm});
            skLineSegment(sketch, "E1257", {"start": v(-1.18, -22.42) * mm, "end": v(-1.16, -22.5) * mm});
            skLineSegment(sketch, "E1258", {"start": v(-1.16, -22.5) * mm, "end": v(-1.14, -22.57) * mm});
            skLineSegment(sketch, "E1259", {"start": v(-1.14, -22.57) * mm, "end": v(-1.12, -22.65) * mm});
            skLineSegment(sketch, "E1260", {"start": v(-1.12, -22.65) * mm, "end": v(-1.1, -22.74) * mm});
            skLineSegment(sketch, "E1261", {"start": v(-1.1, -22.74) * mm, "end": v(-1.1, -22.82) * mm});
            skLineSegment(sketch, "E1262", {"start": v(-1.1, -22.82) * mm, "end": v(-1.09, -22.9) * mm});
            skLineSegment(sketch, "E1263", {"start": v(-1.09, -22.9) * mm, "end": v(-1.08, -22.98) * mm});
            skLineSegment(sketch, "E1264", {"start": v(-1.08, -22.98) * mm, "end": v(-1.07, -23.07) * mm});
            skLineSegment(sketch, "E1265", {"start": v(-1.07, -23.07) * mm, "end": v(-1.07, -23.16) * mm});
            skLineSegment(sketch, "E1266", {"start": v(-1.07, -23.16) * mm, "end": v(-1.06, -23.24) * mm});
            skLineSegment(sketch, "E1267", {"start": v(-1.06, -23.24) * mm, "end": v(-1.06, -23.33) * mm});
            skLineSegment(sketch, "E1268", {"start": v(-1.06, -23.33) * mm, "end": v(-1.07, -23.42) * mm});
            skLineSegment(sketch, "E1269", {"start": v(-1.07, -23.42) * mm, "end": v(-1.07, -23.51) * mm});
            skLineSegment(sketch, "E1270", {"start": v(-1.07, -23.51) * mm, "end": v(-1.08, -23.6) * mm});
            skLineSegment(sketch, "E1271", {"start": v(-1.08, -23.6) * mm, "end": v(-1.09, -23.7) * mm});
            skLineSegment(sketch, "E1272", {"start": v(-1.09, -23.7) * mm, "end": v(-1.1, -23.8) * mm});
            skLineSegment(sketch, "E1273", {"start": v(-1.1, -23.8) * mm, "end": v(-1.11, -23.89) * mm});
            skLineSegment(sketch, "E1274", {"start": v(-1.11, -23.89) * mm, "end": v(-1.13, -23.98) * mm});
            skLineSegment(sketch, "E1275", {"start": v(-1.13, -23.98) * mm, "end": v(-1.15, -24.08) * mm});
            skLineSegment(sketch, "E1276", {"start": v(-1.15, -24.08) * mm, "end": v(-1.17, -24.18) * mm});
            skLineSegment(sketch, "E1277", {"start": v(-1.17, -24.18) * mm, "end": v(-1.2, -24.28) * mm});
            skLineSegment(sketch, "E1278", {"start": v(-1.2, -24.28) * mm, "end": v(-1.22, -24.38) * mm});
            skLineSegment(sketch, "E1279", {"start": v(-1.22, -24.38) * mm, "end": v(-1.25, -24.48) * mm});
            skLineSegment(sketch, "E1280", {"start": v(-1.25, -24.48) * mm, "end": v(-1.26, -24.52) * mm});
            skLineSegment(sketch, "E1281", {"start": v(-1.26, -24.52) * mm, "end": v(-1.27, -24.57) * mm});
            skLineSegment(sketch, "E1282", {"start": v(-1.27, -24.57) * mm, "end": v(-1.3, -24.61) * mm});
            skLineSegment(sketch, "E1283", {"start": v(-1.3, -24.61) * mm, "end": v(-1.3, -24.65) * mm});
            skLineSegment(sketch, "E1284", {"start": v(-1.3, -24.65) * mm, "end": v(-1.32, -24.7) * mm});
            skLineSegment(sketch, "E1285", {"start": v(-1.32, -24.7) * mm, "end": v(-1.34, -24.74) * mm});
            skLineSegment(sketch, "E1286", {"start": v(-1.34, -24.74) * mm, "end": v(-1.36, -24.78) * mm});
            skLineSegment(sketch, "E1287", {"start": v(-1.36, -24.78) * mm, "end": v(-1.38, -24.82) * mm});
            skLineSegment(sketch, "E1288", {"start": v(-1.38, -24.82) * mm, "end": v(-1.4, -24.87) * mm});
            skLineSegment(sketch, "E1289", {"start": v(-1.4, -24.87) * mm, "end": v(-1.43, -24.9) * mm});
            skLineSegment(sketch, "E1290", {"start": v(-1.43, -24.9) * mm, "end": v(-1.45, -24.95) * mm});
            skLineSegment(sketch, "E1291", {"start": v(-1.45, -24.95) * mm, "end": v(-1.48, -25) * mm});
            skLineSegment(sketch, "E1292", {"start": v(-1.48, -25) * mm, "end": v(-1.5, -25.03) * mm});
            skLineSegment(sketch, "E1293", {"start": v(-1.5, -25.03) * mm, "end": v(-1.53, -25.08) * mm});
            skLineSegment(sketch, "E1294", {"start": v(-1.53, -25.08) * mm, "end": v(-1.55, -25.12) * mm});
            skLineSegment(sketch, "E1295", {"start": v(-1.55, -25.12) * mm, "end": v(-1.58, -25.16) * mm});
            skLineSegment(sketch, "E1296", {"start": v(-1.58, -25.16) * mm, "end": v(-1.61, -25.2) * mm});
            skLineSegment(sketch, "E1297", {"start": v(-1.61, -25.2) * mm, "end": v(-1.64, -25.24) * mm});
            skLineSegment(sketch, "E1298", {"start": v(-1.64, -25.24) * mm, "end": v(-1.67, -25.28) * mm});
            skLineSegment(sketch, "E1299", {"start": v(-1.67, -25.28) * mm, "end": v(-1.7, -25.32) * mm});
            skLineSegment(sketch, "E1300", {"start": v(-1.7, -25.32) * mm, "end": v(-1.73, -25.36) * mm});
            skLineSegment(sketch, "E1301", {"start": v(-1.73, -25.36) * mm, "end": v(-1.76, -25.4) * mm});
            skLineSegment(sketch, "E1302", {"start": v(-1.76, -25.4) * mm, "end": v(-1.8, -25.44) * mm});
            skLineSegment(sketch, "E1303", {"start": v(-1.8, -25.44) * mm, "end": v(-1.83, -25.48) * mm});
            skLineSegment(sketch, "E1304", {"start": v(-1.83, -25.48) * mm, "end": v(-1.86, -25.52) * mm});
            skLineSegment(sketch, "E1305", {"start": v(-1.86, -25.52) * mm, "end": v(-1.9, -25.56) * mm});
            skLineSegment(sketch, "E1306", {"start": v(-1.9, -25.56) * mm, "end": v(-1.93, -25.6) * mm});
            skLineSegment(sketch, "E1307", {"start": v(-1.93, -25.6) * mm, "end": v(-1.97, -25.64) * mm});
            skLineSegment(sketch, "E1308", {"start": v(-1.97, -25.64) * mm, "end": v(-2, -25.68) * mm});
            skLineSegment(sketch, "E1309", {"start": v(-2, -25.68) * mm, "end": v(-2.04, -25.72) * mm});
            skLineSegment(sketch, "E1310", {"start": v(-2.04, -25.72) * mm, "end": v(-2.08, -25.76) * mm});
            skLineSegment(sketch, "E1311", {"start": v(-2.08, -25.76) * mm, "end": v(-2.12, -25.8) * mm});
            skLineSegment(sketch, "E1312", {"start": v(-2.12, -25.8) * mm, "end": v(-2.15, -25.85) * mm});
            skLineSegment(sketch, "E1313", {"start": v(-2.15, -25.85) * mm, "end": v(-2.2, -25.89) * mm});
            skLineSegment(sketch, "E1314", {"start": v(-2.2, -25.89) * mm, "end": v(-2.23, -25.93) * mm});
            skLineSegment(sketch, "E1315", {"start": v(-2.23, -25.93) * mm, "end": v(-2.27, -25.97) * mm});
            skLineSegment(sketch, "E1316", {"start": v(-2.27, -25.97) * mm, "end": v(-2.3, -26) * mm});
            skLineSegment(sketch, "E1317", {"start": v(-2.3, -26) * mm, "end": v(-2.35, -26.05) * mm});
            skLineSegment(sketch, "E1318", {"start": v(-2.35, -26.05) * mm, "end": v(-2.4, -26.1) * mm});
            skLineSegment(sketch, "E1319", {"start": v(-2.4, -26.1) * mm, "end": v(-2.43, -26.13) * mm});
            skLineSegment(sketch, "E1320", {"start": v(-2.43, -26.13) * mm, "end": v(-2.47, -26.17) * mm});
            skLineSegment(sketch, "E1321", {"start": v(-2.47, -26.17) * mm, "end": v(-2.51, -26.22) * mm});
            skLineSegment(sketch, "E1322", {"start": v(-2.51, -26.22) * mm, "end": v(-2.55, -26.26) * mm});
            skLineSegment(sketch, "E1323", {"start": v(-2.55, -26.26) * mm, "end": v(-2.6, -26.3) * mm});
            skLineSegment(sketch, "E1324", {"start": v(-2.6, -26.3) * mm, "end": v(-2.64, -26.34) * mm});
            skLineSegment(sketch, "E1325", {"start": v(-2.64, -26.34) * mm, "end": v(-2.68, -26.39) * mm});
            skLineSegment(sketch, "E1326", {"start": v(-2.68, -26.39) * mm, "end": v(-2.72, -26.43) * mm});
            skLineSegment(sketch, "E1327", {"start": v(-2.72, -26.43) * mm, "end": v(-2.76, -26.47) * mm});
            skLineSegment(sketch, "E1328", {"start": v(-2.76, -26.47) * mm, "end": v(-2.8, -26.51) * mm});
            skLineSegment(sketch, "E1329", {"start": v(-2.8, -26.51) * mm, "end": v(-2.85, -26.56) * mm});
            skLineSegment(sketch, "E1330", {"start": v(-2.85, -26.56) * mm, "end": v(-2.89, -26.6) * mm});
            skLineSegment(sketch, "E1331", {"start": v(-2.89, -26.6) * mm, "end": v(-2.93, -26.65) * mm});
            skLineSegment(sketch, "E1332", {"start": v(-2.93, -26.65) * mm, "end": v(-2.97, -26.7) * mm});
            skLineSegment(sketch, "E1333", {"start": v(-2.97, -26.7) * mm, "end": v(-3.02, -26.74) * mm});
            skLineSegment(sketch, "E1334", {"start": v(-3.02, -26.74) * mm, "end": v(-3.06, -26.78) * mm});
            skLineSegment(sketch, "E1335", {"start": v(-3.06, -26.78) * mm, "end": v(-3.1, -26.83) * mm});
            skLineSegment(sketch, "E1336", {"start": v(-3.1, -26.83) * mm, "end": v(-3.14, -26.87) * mm});
            skLineSegment(sketch, "E1337", {"start": v(-3.14, -26.87) * mm, "end": v(-3.19, -26.92) * mm});
            skLineSegment(sketch, "E1338", {"start": v(-3.19, -26.92) * mm, "end": v(-3.23, -26.97) * mm});
            skLineSegment(sketch, "E1339", {"start": v(-3.23, -26.97) * mm, "end": v(-3.27, -27.01) * mm});
            skLineSegment(sketch, "E1340", {"start": v(-3.27, -27.01) * mm, "end": v(-3.31, -27.06) * mm});
            skLineSegment(sketch, "E1341", {"start": v(-3.31, -27.06) * mm, "end": v(-3.35, -27.11) * mm});
            skLineSegment(sketch, "E1342", {"start": v(-3.35, -27.11) * mm, "end": v(-3.4, -27.16) * mm});
            skLineSegment(sketch, "E1343", {"start": v(-3.4, -27.16) * mm, "end": v(-3.44, -27.2) * mm});
            skLineSegment(sketch, "E1344", {"start": v(-3.44, -27.2) * mm, "end": v(-3.4, -27.26) * mm});
            skLineSegment(sketch, "E1345", {"start": v(-3.4, -27.26) * mm, "end": v(-3.38, -27.3) * mm});
            skLineSegment(sketch, "E1346", {"start": v(-3.38, -27.3) * mm, "end": v(-3.35, -27.35) * mm});
            skLineSegment(sketch, "E1347", {"start": v(-3.35, -27.35) * mm, "end": v(-3.32, -27.4) * mm});
            skLineSegment(sketch, "E1348", {"start": v(-3.32, -27.4) * mm, "end": v(-3.29, -27.44) * mm});
            skLineSegment(sketch, "E1349", {"start": v(-3.29, -27.44) * mm, "end": v(-3.26, -27.48) * mm});
            skLineSegment(sketch, "E1350", {"start": v(-3.26, -27.48) * mm, "end": v(-3.22, -27.52) * mm});
            skLineSegment(sketch, "E1351", {"start": v(-3.22, -27.52) * mm, "end": v(-3.19, -27.56) * mm});
            skLineSegment(sketch, "E1352", {"start": v(-3.19, -27.56) * mm, "end": v(-3.15, -27.6) * mm});
            skLineSegment(sketch, "E1353", {"start": v(-3.15, -27.6) * mm, "end": v(-3.12, -27.62) * mm});
            skLineSegment(sketch, "E1354", {"start": v(-3.12, -27.62) * mm, "end": v(-3.08, -27.66) * mm});
            skLineSegment(sketch, "E1355", {"start": v(-3.08, -27.66) * mm, "end": v(-3.04, -27.69) * mm});
            skLineSegment(sketch, "E1356", {"start": v(-3.04, -27.69) * mm, "end": v(-3, -27.72) * mm});
            skLineSegment(sketch, "E1357", {"start": v(-3, -27.72) * mm, "end": v(-2.96, -27.74) * mm});
            skLineSegment(sketch, "E1358", {"start": v(-2.96, -27.74) * mm, "end": v(-2.92, -27.77) * mm});
            skLineSegment(sketch, "E1359", {"start": v(-2.92, -27.77) * mm, "end": v(-2.87, -27.8) * mm});
            skLineSegment(sketch, "E1360", {"start": v(-2.87, -27.8) * mm, "end": v(-2.83, -27.82) * mm});
            skLineSegment(sketch, "E1361", {"start": v(-2.83, -27.82) * mm, "end": v(-2.78, -27.84) * mm});
            skLineSegment(sketch, "E1362", {"start": v(-2.78, -27.84) * mm, "end": v(-2.74, -27.86) * mm});
            skLineSegment(sketch, "E1363", {"start": v(-2.74, -27.86) * mm, "end": v(-2.7, -27.88) * mm});
            skLineSegment(sketch, "E1364", {"start": v(-2.7, -27.88) * mm, "end": v(-2.65, -27.9) * mm});
            skLineSegment(sketch, "E1365", {"start": v(-2.65, -27.9) * mm, "end": v(-2.6, -27.91) * mm});
            skLineSegment(sketch, "E1366", {"start": v(-2.6, -27.91) * mm, "end": v(-2.55, -27.93) * mm});
            skLineSegment(sketch, "E1367", {"start": v(-2.55, -27.93) * mm, "end": v(-2.5, -27.94) * mm});
            skLineSegment(sketch, "E1368", {"start": v(-2.5, -27.94) * mm, "end": v(-2.45, -27.96) * mm});
            skLineSegment(sketch, "E1369", {"start": v(-2.45, -27.96) * mm, "end": v(-2.4, -27.97) * mm});
            skLineSegment(sketch, "E1370", {"start": v(-2.4, -27.97) * mm, "end": v(-2.35, -27.98) * mm});
            skLineSegment(sketch, "E1371", {"start": v(-2.35, -27.98) * mm, "end": v(-2.3, -27.99) * mm});
            skLineSegment(sketch, "E1372", {"start": v(-2.3, -27.99) * mm, "end": v(-2.24, -28) * mm});
            skLineSegment(sketch, "E1373", {"start": v(-2.24, -28) * mm, "end": v(-2.19, -28) * mm});
            skLineSegment(sketch, "E1374", {"start": v(-2.19, -28) * mm, "end": v(-2.14, -28.01) * mm});
            skLineSegment(sketch, "E1375", {"start": v(-2.14, -28.01) * mm, "end": v(-2.08, -28.02) * mm});
            skLineSegment(sketch, "E1376", {"start": v(-2.08, -28.02) * mm, "end": v(-2.03, -28.03) * mm});
            skLineSegment(sketch, "E1377", {"start": v(-2.03, -28.03) * mm, "end": v(-1.97, -28.03) * mm});
            skLineSegment(sketch, "E1378", {"start": v(-1.97, -28.03) * mm, "end": v(-1.91, -28.03) * mm});
            skLineSegment(sketch, "E1379", {"start": v(-1.91, -28.03) * mm, "end": v(-1.86, -28.04) * mm});
            skLineSegment(sketch, "E1380", {"start": v(-1.86, -28.04) * mm, "end": v(-1.8, -28.04) * mm});
            skLineSegment(sketch, "E1381", {"start": v(-1.8, -28.04) * mm, "end": v(-1.74, -28.04) * mm});
            skLineSegment(sketch, "E1382", {"start": v(-1.74, -28.04) * mm, "end": v(-1.69, -28.04) * mm});
            skLineSegment(sketch, "E1383", {"start": v(-1.69, -28.04) * mm, "end": v(-1.63, -28.04) * mm});
            skLineSegment(sketch, "E1384", {"start": v(-1.63, -28.04) * mm, "end": v(-1.57, -28.04) * mm});
            skLineSegment(sketch, "E1385", {"start": v(-1.57, -28.04) * mm, "end": v(-1.51, -28.04) * mm});
            skLineSegment(sketch, "E1386", {"start": v(-1.51, -28.04) * mm, "end": v(-1.45, -28.04) * mm});
            skLineSegment(sketch, "E1387", {"start": v(-1.45, -28.04) * mm, "end": v(-1.4, -28.04) * mm});
            skLineSegment(sketch, "E1388", {"start": v(-1.4, -28.04) * mm, "end": v(-1.33, -28.04) * mm});
            skLineSegment(sketch, "E1389", {"start": v(-1.33, -28.04) * mm, "end": v(-1.27, -28.04) * mm});
            skLineSegment(sketch, "E1390", {"start": v(-1.27, -28.04) * mm, "end": v(-1.21, -28.04) * mm});
            skLineSegment(sketch, "E1391", {"start": v(-1.21, -28.04) * mm, "end": v(-1.15, -28.03) * mm});
            skLineSegment(sketch, "E1392", {"start": v(-1.15, -28.03) * mm, "end": v(-1.1, -28.03) * mm});
            skLineSegment(sketch, "E1393", {"start": v(-1.1, -28.03) * mm, "end": v(-1.03, -28.03) * mm});
            skLineSegment(sketch, "E1394", {"start": v(-1.03, -28.03) * mm, "end": v(-0.97, -28.02) * mm});
            skLineSegment(sketch, "E1395", {"start": v(-0.97, -28.02) * mm, "end": v(-0.91, -28.02) * mm});
            skLineSegment(sketch, "E1396", {"start": v(-0.91, -28.02) * mm, "end": v(-0.85, -28.02) * mm});
            skLineSegment(sketch, "E1397", {"start": v(-0.85, -28.02) * mm, "end": v(-0.8, -28.01) * mm});
            skLineSegment(sketch, "E1398", {"start": v(-0.8, -28.01) * mm, "end": v(-0.73, -28.01) * mm});
            skLineSegment(sketch, "E1399", {"start": v(-0.73, -28.01) * mm, "end": v(-0.67, -28) * mm});
            skLineSegment(sketch, "E1400", {"start": v(-0.67, -28) * mm, "end": v(-0.6, -28) * mm});
            skLineSegment(sketch, "E1401", {"start": v(-0.6, -28) * mm, "end": v(-0.55, -28) * mm});
            skLineSegment(sketch, "E1402", {"start": v(-0.55, -28) * mm, "end": v(-0.49, -28) * mm});
            skLineSegment(sketch, "E1403", {"start": v(-0.49, -28) * mm, "end": v(-0.43, -28) * mm});
            skLineSegment(sketch, "E1404", {"start": v(-0.43, -28) * mm, "end": v(-0.36, -28) * mm});
            skLineSegment(sketch, "E1405", {"start": v(-0.36, -28) * mm, "end": v(-0.3, -27.99) * mm});
            skLineSegment(sketch, "E1406", {"start": v(-0.3, -27.99) * mm, "end": v(-0.24, -27.99) * mm});
            skLineSegment(sketch, "E1407", {"start": v(-0.24, -27.99) * mm, "end": v(-0.18, -27.98) * mm});
            skLineSegment(sketch, "E1408", {"start": v(-0.18, -27.98) * mm, "end": v(-0.13, -27.98) * mm});
            skLineSegment(sketch, "E1409", {"start": v(-0.13, -27.98) * mm, "end": v(-0.07, -27.98) * mm});
            skLineSegment(sketch, "E1410", {"start": v(-0.07, -27.98) * mm, "end": v(-0.01, -27.97) * mm});
            skLineSegment(sketch, "E1411", {"start": v(-0.01, -27.97) * mm, "end": v(0.05, -27.97) * mm});
            skLineSegment(sketch, "E1412", {"start": v(0.05, -27.97) * mm, "end": v(0.1, -27.96) * mm});
            skLineSegment(sketch, "E1413", {"start": v(0.1, -27.96) * mm, "end": v(0.16, -27.95) * mm});
            skLineSegment(sketch, "E1414", {"start": v(0.16, -27.95) * mm, "end": v(0.21, -27.94) * mm});
            skLineSegment(sketch, "E1415", {"start": v(0.21, -27.94) * mm, "end": v(0.26, -27.93) * mm});
            skLineSegment(sketch, "E1416", {"start": v(0.26, -27.93) * mm, "end": v(0.32, -27.92) * mm});
            skLineSegment(sketch, "E1417", {"start": v(0.32, -27.92) * mm, "end": v(0.37, -27.9) * mm});
            skLineSegment(sketch, "E1418", {"start": v(0.37, -27.9) * mm, "end": v(0.42, -27.9) * mm});
            skLineSegment(sketch, "E1419", {"start": v(0.42, -27.9) * mm, "end": v(0.47, -27.88) * mm});
            skLineSegment(sketch, "E1420", {"start": v(0.47, -27.88) * mm, "end": v(0.52, -27.86) * mm});
            skLineSegment(sketch, "E1421", {"start": v(0.52, -27.86) * mm, "end": v(0.57, -27.85) * mm});
            skLineSegment(sketch, "E1422", {"start": v(0.57, -27.85) * mm, "end": v(0.62, -27.83) * mm});
            skLineSegment(sketch, "E1423", {"start": v(0.62, -27.83) * mm, "end": v(0.66, -27.81) * mm});
            skLineSegment(sketch, "E1424", {"start": v(0.66, -27.81) * mm, "end": v(0.71, -27.8) * mm});
            skLineSegment(sketch, "E1425", {"start": v(0.71, -27.8) * mm, "end": v(0.76, -27.77) * mm});
            skLineSegment(sketch, "E1426", {"start": v(0.76, -27.77) * mm, "end": v(0.8, -27.75) * mm});
            skLineSegment(sketch, "E1427", {"start": v(0.8, -27.75) * mm, "end": v(0.85, -27.73) * mm});
            skLineSegment(sketch, "E1428", {"start": v(0.85, -27.73) * mm, "end": v(0.89, -27.7) * mm});
            skLineSegment(sketch, "E1429", {"start": v(0.89, -27.7) * mm, "end": v(0.93, -27.68) * mm});
            skLineSegment(sketch, "E1430", {"start": v(0.93, -27.68) * mm, "end": v(0.97, -27.65) * mm});
            skLineSegment(sketch, "E1431", {"start": v(0.97, -27.65) * mm, "end": v(1.01, -27.62) * mm});
            skLineSegment(sketch, "E1432", {"start": v(1.01, -27.62) * mm, "end": v(1.05, -27.6) * mm});
            skLineSegment(sketch, "E1433", {"start": v(1.05, -27.6) * mm, "end": v(1.1, -27.57) * mm});
            skLineSegment(sketch, "E1434", {"start": v(1.1, -27.57) * mm, "end": v(1.13, -27.54) * mm});
            skLineSegment(sketch, "E1435", {"start": v(1.13, -27.54) * mm, "end": v(1.17, -27.5) * mm});
            skLineSegment(sketch, "E1436", {"start": v(1.17, -27.5) * mm, "end": v(1.2, -27.48) * mm});
            skLineSegment(sketch, "E1437", {"start": v(1.2, -27.48) * mm, "end": v(1.24, -27.45) * mm});
            skLineSegment(sketch, "E1438", {"start": v(1.24, -27.45) * mm, "end": v(1.27, -27.41) * mm});
            skLineSegment(sketch, "E1439", {"start": v(1.27, -27.41) * mm, "end": v(1.3, -27.38) * mm});
            skLineSegment(sketch, "E1440", {"start": v(1.3, -27.38) * mm, "end": v(1.34, -27.35) * mm});
            skLineSegment(sketch, "E1441", {"start": v(1.34, -27.35) * mm, "end": v(1.37, -27.31) * mm});
            skLineSegment(sketch, "E1442", {"start": v(1.37, -27.31) * mm, "end": v(1.4, -27.28) * mm});
            skLineSegment(sketch, "E1443", {"start": v(1.4, -27.28) * mm, "end": v(1.43, -27.24) * mm});
            skLineSegment(sketch, "E1444", {"start": v(1.43, -27.24) * mm, "end": v(1.46, -27.2) * mm});
            skLineSegment(sketch, "E1445", {"start": v(1.46, -27.2) * mm, "end": v(1.49, -27.17) * mm});
            skLineSegment(sketch, "E1446", {"start": v(1.49, -27.17) * mm, "end": v(1.52, -27.13) * mm});
            skLineSegment(sketch, "E1447", {"start": v(1.52, -27.13) * mm, "end": v(1.54, -27.09) * mm});
            skLineSegment(sketch, "E1448", {"start": v(1.54, -27.09) * mm, "end": v(1.57, -27.05) * mm});
            skLineSegment(sketch, "E1449", {"start": v(1.57, -27.05) * mm, "end": v(1.6, -27) * mm});
            skLineSegment(sketch, "E1450", {"start": v(1.6, -27) * mm, "end": v(1.62, -26.97) * mm});
            skLineSegment(sketch, "E1451", {"start": v(1.62, -26.97) * mm, "end": v(1.64, -26.92) * mm});
            skLineSegment(sketch, "E1452", {"start": v(1.64, -26.92) * mm, "end": v(1.66, -26.88) * mm});
            skLineSegment(sketch, "E1453", {"start": v(1.66, -26.88) * mm, "end": v(1.68, -26.84) * mm});
            skLineSegment(sketch, "E1454", {"start": v(1.68, -26.84) * mm, "end": v(1.7, -26.8) * mm});
            skLineSegment(sketch, "E1455", {"start": v(1.7, -26.8) * mm, "end": v(1.72, -26.75) * mm});
            skLineSegment(sketch, "E1456", {"start": v(1.72, -26.75) * mm, "end": v(1.74, -26.7) * mm});
            skLineSegment(sketch, "E1457", {"start": v(1.74, -26.7) * mm, "end": v(1.75, -26.66) * mm});
            skLineSegment(sketch, "E1458", {"start": v(1.75, -26.66) * mm, "end": v(1.77, -26.61) * mm});
            skLineSegment(sketch, "E1459", {"start": v(1.77, -26.61) * mm, "end": v(1.78, -26.56) * mm});
            skLineSegment(sketch, "E1460", {"start": v(1.78, -26.56) * mm, "end": v(1.8, -26.52) * mm});
            skLineSegment(sketch, "E1461", {"start": v(1.8, -26.52) * mm, "end": v(1.8, -26.47) * mm});
            skLineSegment(sketch, "E1462", {"start": v(1.8, -26.47) * mm, "end": v(1.82, -26.42) * mm});
            skLineSegment(sketch, "E1463", {"start": v(1.82, -26.42) * mm, "end": v(1.83, -26.37) * mm});
            skLineSegment(sketch, "E1464", {"start": v(1.83, -26.37) * mm, "end": v(1.84, -26.32) * mm});
            skLineSegment(sketch, "E1465", {"start": v(1.84, -26.32) * mm, "end": v(1.85, -26.27) * mm});
            skLineSegment(sketch, "E1466", {"start": v(1.85, -26.27) * mm, "end": v(1.86, -26.22) * mm});
            skLineSegment(sketch, "E1467", {"start": v(1.86, -26.22) * mm, "end": v(1.86, -26.17) * mm});
            skLineSegment(sketch, "E1468", {"start": v(1.86, -26.17) * mm, "end": v(1.87, -26.12) * mm});
            skLineSegment(sketch, "E1469", {"start": v(1.87, -26.12) * mm, "end": v(1.87, -26.07) * mm});
            skLineSegment(sketch, "E1470", {"start": v(1.87, -26.07) * mm, "end": v(1.88, -26.02) * mm});
            skLineSegment(sketch, "E1471", {"start": v(1.88, -26.02) * mm, "end": v(1.88, -25.96) * mm});
            skLineSegment(sketch, "E1472", {"start": v(1.88, -25.96) * mm, "end": v(1.88, -25.8) * mm});
            skLineSegment(sketch, "E1473", {"start": v(1.88, -25.8) * mm, "end": v(1.89, -25.65) * mm});
            skLineSegment(sketch, "E1474", {"start": v(1.89, -25.65) * mm, "end": v(1.9, -25.49) * mm});
            skLineSegment(sketch, "E1475", {"start": v(1.9, -25.49) * mm, "end": v(1.9, -25.33) * mm});
            skLineSegment(sketch, "E1476", {"start": v(1.9, -25.33) * mm, "end": v(1.9, -25.17) * mm});
            skLineSegment(sketch, "E1477", {"start": v(1.9, -25.17) * mm, "end": v(1.9, -25.01) * mm});
            skLineSegment(sketch, "E1478", {"start": v(1.9, -25.01) * mm, "end": v(1.9, -24.86) * mm});
            skLineSegment(sketch, "E1479", {"start": v(1.9, -24.86) * mm, "end": v(1.91, -24.7) * mm});
            skLineSegment(sketch, "E1480", {"start": v(1.91, -24.7) * mm, "end": v(1.91, -24.54) * mm});
            skLineSegment(sketch, "E1481", {"start": v(1.91, -24.54) * mm, "end": v(1.92, -24.38) * mm});
            skLineSegment(sketch, "E1482", {"start": v(1.92, -24.38) * mm, "end": v(1.92, -24.22) * mm});
            skLineSegment(sketch, "E1483", {"start": v(1.92, -24.22) * mm, "end": v(1.92, -24.07) * mm});
            skLineSegment(sketch, "E1484", {"start": v(1.92, -24.07) * mm, "end": v(1.92, -23.9) * mm});
            skLineSegment(sketch, "E1485", {"start": v(1.92, -23.9) * mm, "end": v(1.93, -23.75) * mm});
            skLineSegment(sketch, "E1486", {"start": v(1.93, -23.75) * mm, "end": v(1.93, -23.6) * mm});
            skLineSegment(sketch, "E1487", {"start": v(1.93, -23.6) * mm, "end": v(1.93, -23.43) * mm});
            skLineSegment(sketch, "E1488", {"start": v(1.93, -23.43) * mm, "end": v(1.93, -23.27) * mm});
            skLineSegment(sketch, "E1489", {"start": v(1.93, -23.27) * mm, "end": v(1.93, -23.12) * mm});
            skLineSegment(sketch, "E1490", {"start": v(1.93, -23.12) * mm, "end": v(1.93, -22.96) * mm});
            skLineSegment(sketch, "E1491", {"start": v(1.93, -22.96) * mm, "end": v(1.93, -22.8) * mm});
            skLineSegment(sketch, "E1492", {"start": v(1.93, -22.8) * mm, "end": v(1.93, -22.64) * mm});
            skLineSegment(sketch, "E1493", {"start": v(1.93, -22.64) * mm, "end": v(1.94, -22.48) * mm});
            skLineSegment(sketch, "E1494", {"start": v(1.94, -22.48) * mm, "end": v(1.94, -22.33) * mm});
            skLineSegment(sketch, "E1495", {"start": v(1.94, -22.33) * mm, "end": v(1.94, -22.17) * mm});
            skLineSegment(sketch, "E1496", {"start": v(1.94, -22.17) * mm, "end": v(1.94, -22.01) * mm});
            skLineSegment(sketch, "E1497", {"start": v(1.94, -22.01) * mm, "end": v(1.94, -21.85) * mm});
            skLineSegment(sketch, "E1498", {"start": v(1.94, -21.85) * mm, "end": v(1.94, -21.7) * mm});
            skLineSegment(sketch, "E1499", {"start": v(1.94, -21.7) * mm, "end": v(1.94, -21.54) * mm});
            skLineSegment(sketch, "E1500", {"start": v(1.94, -21.54) * mm, "end": v(1.94, -21.38) * mm});
            skLineSegment(sketch, "E1501", {"start": v(1.94, -21.38) * mm, "end": v(1.94, -21.22) * mm});
            skLineSegment(sketch, "E1502", {"start": v(1.94, -21.22) * mm, "end": v(1.94, -21.06) * mm});
            skLineSegment(sketch, "E1503", {"start": v(1.94, -21.06) * mm, "end": v(1.94, -20.9) * mm});
            skLineSegment(sketch, "E1504", {"start": v(1.94, -20.9) * mm, "end": v(1.94, -20.75) * mm});
            skLineSegment(sketch, "E1505", {"start": v(1.94, -20.75) * mm, "end": v(1.94, -20.59) * mm});
            skLineSegment(sketch, "E1506", {"start": v(1.94, -20.59) * mm, "end": v(1.94, -20.43) * mm});
            skLineSegment(sketch, "E1507", {"start": v(1.94, -20.43) * mm, "end": v(1.93, -20.27) * mm});
            skLineSegment(sketch, "E1508", {"start": v(1.93, -20.27) * mm, "end": v(1.93, -20.12) * mm});
            skLineSegment(sketch, "E1509", {"start": v(1.93, -20.12) * mm, "end": v(1.93, -19.96) * mm});
            skLineSegment(sketch, "E1510", {"start": v(1.93, -19.96) * mm, "end": v(1.93, -19.8) * mm});
            skLineSegment(sketch, "E1511", {"start": v(1.93, -19.8) * mm, "end": v(1.93, -19.64) * mm});
            skLineSegment(sketch, "E1512", {"start": v(1.93, -19.64) * mm, "end": v(1.93, -19.49) * mm});
            skLineSegment(sketch, "E1513", {"start": v(1.93, -19.49) * mm, "end": v(1.93, -19.33) * mm});
            skLineSegment(sketch, "E1514", {"start": v(1.93, -19.33) * mm, "end": v(1.93, -19.17) * mm});
            skLineSegment(sketch, "E1515", {"start": v(1.93, -19.17) * mm, "end": v(1.93, -19.01) * mm});
            skLineSegment(sketch, "E1516", {"start": v(1.93, -19.01) * mm, "end": v(1.93, -18.86) * mm});
            skLineSegment(sketch, "E1517", {"start": v(1.93, -18.86) * mm, "end": v(1.93, -18.7) * mm});
            skLineSegment(sketch, "E1518", {"start": v(1.93, -18.7) * mm, "end": v(1.93, -18.54) * mm});
            skLineSegment(sketch, "E1519", {"start": v(1.93, -18.54) * mm, "end": v(1.93, -18.38) * mm});
            skLineSegment(sketch, "E1520", {"start": v(1.93, -18.38) * mm, "end": v(1.92, -18.23) * mm});
            skLineSegment(sketch, "E1521", {"start": v(1.92, -18.23) * mm, "end": v(1.92, -18.07) * mm});
            skLineSegment(sketch, "E1522", {"start": v(1.92, -18.07) * mm, "end": v(1.92, -17.91) * mm});
            skLineSegment(sketch, "E1523", {"start": v(1.92, -17.91) * mm, "end": v(1.92, -17.75) * mm});
            skLineSegment(sketch, "E1524", {"start": v(1.92, -17.75) * mm, "end": v(1.92, -17.6) * mm});
            skLineSegment(sketch, "E1525", {"start": v(1.92, -17.6) * mm, "end": v(1.92, -17.44) * mm});
            skLineSegment(sketch, "E1526", {"start": v(1.92, -17.44) * mm, "end": v(1.92, -17.28) * mm});
            skLineSegment(sketch, "E1527", {"start": v(1.92, -17.28) * mm, "end": v(1.92, -17.13) * mm});
            skLineSegment(sketch, "E1528", {"start": v(1.92, -17.13) * mm, "end": v(1.92, -16.97) * mm});
            skLineSegment(sketch, "E1529", {"start": v(1.92, -16.97) * mm, "end": v(1.92, -16.81) * mm});
            skLineSegment(sketch, "E1530", {"start": v(1.92, -16.81) * mm, "end": v(1.92, -16.66) * mm});
            skLineSegment(sketch, "E1531", {"start": v(1.92, -16.66) * mm, "end": v(1.92, -16.5) * mm});
            skLineSegment(sketch, "E1532", {"start": v(1.92, -16.5) * mm, "end": v(1.92, -16.34) * mm});
            skLineSegment(sketch, "E1533", {"start": v(1.92, -16.34) * mm, "end": v(1.92, -16.19) * mm});
            skLineSegment(sketch, "E1534", {"start": v(1.92, -16.19) * mm, "end": v(1.92, -16.03) * mm});
            skLineSegment(sketch, "E1535", {"start": v(1.92, -16.03) * mm, "end": v(1.92, -15.87) * mm});
            skLineSegment(sketch, "E1536", {"start": v(-1.17, -10.66) * mm, "end": v(-1.35, -10.56) * mm});
            skLineSegment(sketch, "E1537", {"start": v(-1.35, -10.56) * mm, "end": v(-1.53, -10.46) * mm});
            skLineSegment(sketch, "E1538", {"start": v(-1.53, -10.46) * mm, "end": v(-1.7, -10.36) * mm});
            skLineSegment(sketch, "E1539", {"start": v(-1.7, -10.36) * mm, "end": v(-1.88, -10.25) * mm});
            skLineSegment(sketch, "E1540", {"start": v(-1.88, -10.25) * mm, "end": v(-2.04, -10.14) * mm});
            skLineSegment(sketch, "E1541", {"start": v(-2.04, -10.14) * mm, "end": v(-2.2, -10.03) * mm});
            skLineSegment(sketch, "E1542", {"start": v(-2.2, -10.03) * mm, "end": v(-2.37, -9.92) * mm});
            skLineSegment(sketch, "E1543", {"start": v(-2.37, -9.92) * mm, "end": v(-2.52, -9.81) * mm});
            skLineSegment(sketch, "E1544", {"start": v(-2.52, -9.81) * mm, "end": v(-2.67, -9.7) * mm});
            skLineSegment(sketch, "E1545", {"start": v(-2.67, -9.7) * mm, "end": v(-2.82, -9.58) * mm});
            skLineSegment(sketch, "E1546", {"start": v(-2.82, -9.58) * mm, "end": v(-2.96, -9.46) * mm});
            skLineSegment(sketch, "E1547", {"start": v(-2.96, -9.46) * mm, "end": v(-3.1, -9.34) * mm});
            skLineSegment(sketch, "E1548", {"start": v(-3.1, -9.34) * mm, "end": v(-3.23, -9.22) * mm});
            skLineSegment(sketch, "E1549", {"start": v(-3.23, -9.22) * mm, "end": v(-3.35, -9.1) * mm});
            skLineSegment(sketch, "E1550", {"start": v(-3.35, -9.1) * mm, "end": v(-3.48, -8.98) * mm});
            skLineSegment(sketch, "E1551", {"start": v(-3.48, -8.98) * mm, "end": v(-3.6, -8.85) * mm});
            skLineSegment(sketch, "E1552", {"start": v(-3.6, -8.85) * mm, "end": v(-3.71, -8.73) * mm});
            skLineSegment(sketch, "E1553", {"start": v(-3.71, -8.73) * mm, "end": v(-3.83, -8.6) * mm});
            skLineSegment(sketch, "E1554", {"start": v(-3.83, -8.6) * mm, "end": v(-3.93, -8.47) * mm});
            skLineSegment(sketch, "E1555", {"start": v(-3.93, -8.47) * mm, "end": v(-4.04, -8.34) * mm});
            skLineSegment(sketch, "E1556", {"start": v(-4.04, -8.34) * mm, "end": v(-4.13, -8.2) * mm});
            skLineSegment(sketch, "E1557", {"start": v(-4.13, -8.2) * mm, "end": v(-4.23, -8.07) * mm});
            skLineSegment(sketch, "E1558", {"start": v(-4.23, -8.07) * mm, "end": v(-4.32, -7.94) * mm});
            skLineSegment(sketch, "E1559", {"start": v(-4.32, -7.94) * mm, "end": v(-4.4, -7.8) * mm});
            skLineSegment(sketch, "E1560", {"start": v(-4.4, -7.8) * mm, "end": v(-4.48, -7.67) * mm});
            skLineSegment(sketch, "E1561", {"start": v(-4.48, -7.67) * mm, "end": v(-4.56, -7.53) * mm});
            skLineSegment(sketch, "E1562", {"start": v(-4.56, -7.53) * mm, "end": v(-4.63, -7.39) * mm});
            skLineSegment(sketch, "E1563", {"start": v(-4.63, -7.39) * mm, "end": v(-4.7, -7.25) * mm});
            skLineSegment(sketch, "E1564", {"start": v(-4.7, -7.25) * mm, "end": v(-4.76, -7.1) * mm});
            skLineSegment(sketch, "E1565", {"start": v(-4.76, -7.1) * mm, "end": v(-4.82, -6.96) * mm});
            skLineSegment(sketch, "E1566", {"start": v(-4.82, -6.96) * mm, "end": v(-4.87, -6.82) * mm});
            skLineSegment(sketch, "E1567", {"start": v(-4.87, -6.82) * mm, "end": v(-4.92, -6.67) * mm});
            skLineSegment(sketch, "E1568", {"start": v(-4.92, -6.67) * mm, "end": v(-4.97, -6.53) * mm});
            skLineSegment(sketch, "E1569", {"start": v(-4.97, -6.53) * mm, "end": v(-5, -6.38) * mm});
            skLineSegment(sketch, "E1570", {"start": v(-5, -6.38) * mm, "end": v(-5.04, -6.23) * mm});
            skLineSegment(sketch, "E1571", {"start": v(-5.04, -6.23) * mm, "end": v(-5.08, -6.08) * mm});
            skLineSegment(sketch, "E1572", {"start": v(-5.08, -6.08) * mm, "end": v(-5.1, -5.93) * mm});
            skLineSegment(sketch, "E1573", {"start": v(-5.1, -5.93) * mm, "end": v(-5.13, -5.78) * mm});
            skLineSegment(sketch, "E1574", {"start": v(-5.13, -5.78) * mm, "end": v(-5.14, -5.63) * mm});
            skLineSegment(sketch, "E1575", {"start": v(-5.14, -5.63) * mm, "end": v(-5.16, -5.47) * mm});
            skLineSegment(sketch, "E1576", {"start": v(-5.16, -5.47) * mm, "end": v(-5.17, -5.32) * mm});
            skLineSegment(sketch, "E1577", {"start": v(-5.17, -5.32) * mm, "end": v(-5.17, -5.17) * mm});
            skLineSegment(sketch, "E1578", {"start": v(-5.17, -5.17) * mm, "end": v(-5.17, -5) * mm});
            skLineSegment(sketch, "E1579", {"start": v(-5.17, -5) * mm, "end": v(-5.17, -4.85) * mm});
            skLineSegment(sketch, "E1580", {"start": v(-5.17, -4.85) * mm, "end": v(-5.16, -4.7) * mm});
            skLineSegment(sketch, "E1581", {"start": v(-5.16, -4.7) * mm, "end": v(-5.14, -4.54) * mm});
            skLineSegment(sketch, "E1582", {"start": v(-5.14, -4.54) * mm, "end": v(-5.12, -4.38) * mm});
            skLineSegment(sketch, "E1583", {"start": v(-5.12, -4.38) * mm, "end": v(-5.1, -4.22) * mm});
            skLineSegment(sketch, "E1584", {"start": v(-5.1, -4.22) * mm, "end": v(-5.07, -4.06) * mm});
            skLineSegment(sketch, "E1585", {"start": v(-5.07, -4.06) * mm, "end": v(-5.04, -3.9) * mm});
            skLineSegment(sketch, "E1586", {"start": v(-5.04, -3.9) * mm, "end": v(-5, -3.74) * mm});
            skLineSegment(sketch, "E1587", {"start": v(-5, -3.74) * mm, "end": v(-4.96, -3.58) * mm});
            skLineSegment(sketch, "E1588", {"start": v(-4.96, -3.58) * mm, "end": v(-4.91, -3.41) * mm});
            skLineSegment(sketch, "E1589", {"start": v(-4.91, -3.41) * mm, "end": v(-4.86, -3.25) * mm});
            skLineSegment(sketch, "E1590", {"start": v(-4.86, -3.25) * mm, "end": v(-4.8, -3.09) * mm});
            skLineSegment(sketch, "E1591", {"start": v(-4.8, -3.09) * mm, "end": v(-4.75, -2.92) * mm});
            skLineSegment(sketch, "E1592", {"start": v(-4.75, -2.92) * mm, "end": v(-4.68, -2.76) * mm});
            skLineSegment(sketch, "E1593", {"start": v(-4.68, -2.76) * mm, "end": v(-4.61, -2.6) * mm});
            skLineSegment(sketch, "E1594", {"start": v(-4.61, -2.6) * mm, "end": v(-4.54, -2.43) * mm});
            skLineSegment(sketch, "E1595", {"start": v(-4.54, -2.43) * mm, "end": v(-4.46, -2.26) * mm});
            skLineSegment(sketch, "E1596", {"start": v(-4.46, -2.26) * mm, "end": v(-4.37, -2.1) * mm});
            skLineSegment(sketch, "E1597", {"start": v(-4.37, -2.1) * mm, "end": v(-4.29, -1.93) * mm});
            skLineSegment(sketch, "E1598", {"start": v(-4.29, -1.93) * mm, "end": v(-4.2, -1.77) * mm});
            skLineSegment(sketch, "E1599", {"start": v(-4.2, -1.77) * mm, "end": v(-4.1, -1.6) * mm});
            skLineSegment(sketch, "E1600", {"start": v(-4.1, -1.6) * mm, "end": v(-4.06, -1.55) * mm});
            skLineSegment(sketch, "E1601", {"start": v(-4.06, -1.55) * mm, "end": v(-4.03, -1.5) * mm});
            skLineSegment(sketch, "E1602", {"start": v(-4.03, -1.5) * mm, "end": v(-4, -1.44) * mm});
            skLineSegment(sketch, "E1603", {"start": v(-4, -1.44) * mm, "end": v(-3.96, -1.39) * mm});
            skLineSegment(sketch, "E1604", {"start": v(-3.96, -1.39) * mm, "end": v(-3.92, -1.34) * mm});
            skLineSegment(sketch, "E1605", {"start": v(-3.92, -1.34) * mm, "end": v(-3.89, -1.28) * mm});
            skLineSegment(sketch, "E1606", {"start": v(-3.89, -1.28) * mm, "end": v(-3.85, -1.23) * mm});
            skLineSegment(sketch, "E1607", {"start": v(-3.85, -1.23) * mm, "end": v(-3.82, -1.18) * mm});
            skLineSegment(sketch, "E1608", {"start": v(-3.82, -1.18) * mm, "end": v(-3.78, -1.13) * mm});
            skLineSegment(sketch, "E1609", {"start": v(-3.78, -1.13) * mm, "end": v(-3.74, -1.08) * mm});
            skLineSegment(sketch, "E1610", {"start": v(-3.74, -1.08) * mm, "end": v(-3.7, -1.04) * mm});
            skLineSegment(sketch, "E1611", {"start": v(-3.7, -1.04) * mm, "end": v(-3.67, -0.99) * mm});
            skLineSegment(sketch, "E1612", {"start": v(-3.67, -0.99) * mm, "end": v(-3.63, -0.94) * mm});
            skLineSegment(sketch, "E1613", {"start": v(-3.63, -0.94) * mm, "end": v(-3.59, -0.9) * mm});
            skLineSegment(sketch, "E1614", {"start": v(-3.59, -0.9) * mm, "end": v(-3.55, -0.84) * mm});
            skLineSegment(sketch, "E1615", {"start": v(-3.55, -0.84) * mm, "end": v(-3.5, -0.8) * mm});
            skLineSegment(sketch, "E1616", {"start": v(-3.5, -0.8) * mm, "end": v(-3.47, -0.75) * mm});
            skLineSegment(sketch, "E1617", {"start": v(-3.47, -0.75) * mm, "end": v(-3.43, -0.7) * mm});
            skLineSegment(sketch, "E1618", {"start": v(-3.43, -0.7) * mm, "end": v(-3.38, -0.66) * mm});
            skLineSegment(sketch, "E1619", {"start": v(-3.38, -0.66) * mm, "end": v(-3.34, -0.6) * mm});
            skLineSegment(sketch, "E1620", {"start": v(-3.34, -0.6) * mm, "end": v(-3.3, -0.56) * mm});
            skLineSegment(sketch, "E1621", {"start": v(-3.3, -0.56) * mm, "end": v(-3.26, -0.52) * mm});
            skLineSegment(sketch, "E1622", {"start": v(-3.26, -0.52) * mm, "end": v(-3.22, -0.47) * mm});
            skLineSegment(sketch, "E1623", {"start": v(-3.22, -0.47) * mm, "end": v(-3.17, -0.43) * mm});
            skLineSegment(sketch, "E1624", {"start": v(-3.17, -0.43) * mm, "end": v(-3.13, -0.38) * mm});
            skLineSegment(sketch, "E1625", {"start": v(-3.13, -0.38) * mm, "end": v(-3.08, -0.34) * mm});
            skLineSegment(sketch, "E1626", {"start": v(-3.08, -0.34) * mm, "end": v(-3.04, -0.3) * mm});
            skLineSegment(sketch, "E1627", {"start": v(-3.04, -0.3) * mm, "end": v(-3, -0.25) * mm});
            skLineSegment(sketch, "E1628", {"start": v(-3, -0.25) * mm, "end": v(-2.95, -0.2) * mm});
            skLineSegment(sketch, "E1629", {"start": v(-2.95, -0.2) * mm, "end": v(-2.9, -0.16) * mm});
            skLineSegment(sketch, "E1630", {"start": v(-2.9, -0.16) * mm, "end": v(-2.86, -0.12) * mm});
            skLineSegment(sketch, "E1631", {"start": v(-2.86, -0.12) * mm, "end": v(-2.82, -0.08) * mm});
            skLineSegment(sketch, "E1632", {"start": v(-2.82, -0.08) * mm, "end": v(-2.77, -0.03) * mm});
            skLineSegment(sketch, "E1633", {"start": v(-2.77, -0.03) * mm, "end": v(-2.72, 0.01) * mm});
            skLineSegment(sketch, "E1634", {"start": v(-2.72, 0.01) * mm, "end": v(-2.68, 0.05) * mm});
            skLineSegment(sketch, "E1635", {"start": v(-2.68, 0.05) * mm, "end": v(-2.63, 0.1) * mm});
            skLineSegment(sketch, "E1636", {"start": v(-2.63, 0.1) * mm, "end": v(-2.58, 0.14) * mm});
            skLineSegment(sketch, "E1637", {"start": v(-2.58, 0.14) * mm, "end": v(-2.54, 0.18) * mm});
            skLineSegment(sketch, "E1638", {"start": v(-2.54, 0.18) * mm, "end": v(-2.5, 0.23) * mm});
            skLineSegment(sketch, "E1639", {"start": v(-2.5, 0.23) * mm, "end": v(-2.44, 0.27) * mm});
            skLineSegment(sketch, "E1640", {"start": v(-2.44, 0.27) * mm, "end": v(-2.4, 0.31) * mm});
            skLineSegment(sketch, "E1641", {"start": v(-2.4, 0.31) * mm, "end": v(-2.35, 0.35) * mm});
            skLineSegment(sketch, "E1642", {"start": v(-2.35, 0.35) * mm, "end": v(-2.3, 0.4) * mm});
            skLineSegment(sketch, "E1643", {"start": v(-2.3, 0.4) * mm, "end": v(-2.25, 0.44) * mm});
            skLineSegment(sketch, "E1644", {"start": v(-2.25, 0.44) * mm, "end": v(-2.2, 0.48) * mm});
            skLineSegment(sketch, "E1645", {"start": v(-2.2, 0.48) * mm, "end": v(-2.16, 0.53) * mm});
            skLineSegment(sketch, "E1646", {"start": v(-2.16, 0.53) * mm, "end": v(-2.1, 0.57) * mm});
            skLineSegment(sketch, "E1647", {"start": v(-2.1, 0.57) * mm, "end": v(-2.06, 0.61) * mm});
            skLineSegment(sketch, "E1648", {"start": v(-2.06, 0.61) * mm, "end": v(-2.01, 0.65) * mm});
            skLineSegment(sketch, "E1649", {"start": v(-2.01, 0.65) * mm, "end": v(-1.96, 0.7) * mm});
            skLineSegment(sketch, "E1650", {"start": v(-1.96, 0.7) * mm, "end": v(-1.91, 0.74) * mm});
            skLineSegment(sketch, "E1651", {"start": v(-1.91, 0.74) * mm, "end": v(-1.87, 0.78) * mm});
            skLineSegment(sketch, "E1652", {"start": v(-1.87, 0.78) * mm, "end": v(-1.82, 0.83) * mm});
            skLineSegment(sketch, "E1653", {"start": v(-1.82, 0.83) * mm, "end": v(-1.77, 0.87) * mm});
            skLineSegment(sketch, "E1654", {"start": v(-1.77, 0.87) * mm, "end": v(-1.72, 0.91) * mm});
            skLineSegment(sketch, "E1655", {"start": v(-1.72, 0.91) * mm, "end": v(-1.67, 0.96) * mm});
            skLineSegment(sketch, "E1656", {"start": v(-1.67, 0.96) * mm, "end": v(-1.62, 1) * mm});
            skLineSegment(sketch, "E1657", {"start": v(-1.62, 1) * mm, "end": v(-1.58, 1.04) * mm});
            skLineSegment(sketch, "E1658", {"start": v(-1.58, 1.04) * mm, "end": v(-1.53, 1.09) * mm});
            skLineSegment(sketch, "E1659", {"start": v(-1.53, 1.09) * mm, "end": v(-1.48, 1.13) * mm});
            skLineSegment(sketch, "E1660", {"start": v(-1.48, 1.13) * mm, "end": v(-1.43, 1.18) * mm});
            skLineSegment(sketch, "E1661", {"start": v(-1.43, 1.18) * mm, "end": v(-1.38, 1.22) * mm});
            skLineSegment(sketch, "E1662", {"start": v(-1.38, 1.22) * mm, "end": v(-1.33, 1.27) * mm});
            skLineSegment(sketch, "E1663", {"start": v(-1.33, 1.27) * mm, "end": v(-1.29, 1.31) * mm});
            skLineSegment(sketch, "E1664", {"start": v(-1.29, 1.31) * mm, "end": v(-1.27, 1.33) * mm});
            skLineSegment(sketch, "E1665", {"start": v(-1.27, 1.33) * mm, "end": v(-1.25, 1.35) * mm});
            skLineSegment(sketch, "E1666", {"start": v(-1.25, 1.35) * mm, "end": v(-1.23, 1.37) * mm});
            skLineSegment(sketch, "E1667", {"start": v(-1.23, 1.37) * mm, "end": v(-1.2, 1.39) * mm});
            skLineSegment(sketch, "E1668", {"start": v(-1.2, 1.39) * mm, "end": v(-1.19, 1.4) * mm});
            skLineSegment(sketch, "E1669", {"start": v(-1.19, 1.4) * mm, "end": v(-1.16, 1.42) * mm});
            skLineSegment(sketch, "E1670", {"start": v(-1.16, 1.42) * mm, "end": v(-1.14, 1.44) * mm});
            skLineSegment(sketch, "E1671", {"start": v(-1.14, 1.44) * mm, "end": v(-1.12, 1.46) * mm});
            skLineSegment(sketch, "E1672", {"start": v(-1.12, 1.46) * mm, "end": v(-1.1, 1.48) * mm});
            skLineSegment(sketch, "E1673", {"start": v(-1.1, 1.48) * mm, "end": v(-1.08, 1.5) * mm});
            skLineSegment(sketch, "E1674", {"start": v(-1.08, 1.5) * mm, "end": v(-1.06, 1.52) * mm});
            skLineSegment(sketch, "E1675", {"start": v(-1.06, 1.52) * mm, "end": v(-1.03, 1.54) * mm});
            skLineSegment(sketch, "E1676", {"start": v(-1.03, 1.54) * mm, "end": v(-1.01, 1.56) * mm});
            skLineSegment(sketch, "E1677", {"start": v(-1.01, 1.56) * mm, "end": v(-0.99, 1.58) * mm});
            skLineSegment(sketch, "E1678", {"start": v(-0.99, 1.58) * mm, "end": v(-0.97, 1.6) * mm});
            skLineSegment(sketch, "E1679", {"start": v(-0.97, 1.6) * mm, "end": v(-0.94, 1.62) * mm});
            skLineSegment(sketch, "E1680", {"start": v(-0.94, 1.62) * mm, "end": v(-0.92, 1.64) * mm});
            skLineSegment(sketch, "E1681", {"start": v(-0.92, 1.64) * mm, "end": v(-0.9, 1.66) * mm});
            skLineSegment(sketch, "E1682", {"start": v(-0.9, 1.66) * mm, "end": v(-0.88, 1.67) * mm});
            skLineSegment(sketch, "E1683", {"start": v(-0.88, 1.67) * mm, "end": v(-0.85, 1.7) * mm});
            skLineSegment(sketch, "E1684", {"start": v(-0.85, 1.7) * mm, "end": v(-0.83, 1.71) * mm});
            skLineSegment(sketch, "E1685", {"start": v(-0.83, 1.71) * mm, "end": v(-0.8, 1.73) * mm});
            skLineSegment(sketch, "E1686", {"start": v(-0.8, 1.73) * mm, "end": v(-0.79, 1.75) * mm});
            skLineSegment(sketch, "E1687", {"start": v(-0.79, 1.75) * mm, "end": v(-0.77, 1.77) * mm});
            skLineSegment(sketch, "E1688", {"start": v(-0.77, 1.77) * mm, "end": v(-0.74, 1.79) * mm});
            skLineSegment(sketch, "E1689", {"start": v(-0.74, 1.79) * mm, "end": v(-0.72, 1.8) * mm});
            skLineSegment(sketch, "E1690", {"start": v(-0.72, 1.8) * mm, "end": v(-0.7, 1.83) * mm});
            skLineSegment(sketch, "E1691", {"start": v(-0.7, 1.83) * mm, "end": v(-0.68, 1.84) * mm});
            skLineSegment(sketch, "E1692", {"start": v(-0.68, 1.84) * mm, "end": v(-0.66, 1.86) * mm});
            skLineSegment(sketch, "E1693", {"start": v(-0.66, 1.86) * mm, "end": v(-0.64, 1.88) * mm});
            skLineSegment(sketch, "E1694", {"start": v(-0.64, 1.88) * mm, "end": v(-0.61, 1.9) * mm});
            skLineSegment(sketch, "E1695", {"start": v(-0.61, 1.9) * mm, "end": v(-0.6, 1.91) * mm});
            skLineSegment(sketch, "E1696", {"start": v(-0.6, 1.91) * mm, "end": v(-0.57, 1.93) * mm});
            skLineSegment(sketch, "E1697", {"start": v(-0.57, 1.93) * mm, "end": v(-0.55, 1.95) * mm});
            skLineSegment(sketch, "E1698", {"start": v(-0.55, 1.95) * mm, "end": v(-0.53, 1.96) * mm});
            skLineSegment(sketch, "E1699", {"start": v(-0.53, 1.96) * mm, "end": v(-0.51, 1.98) * mm});
            skLineSegment(sketch, "E1700", {"start": v(-0.51, 1.98) * mm, "end": v(-0.5, 2) * mm});
            skLineSegment(sketch, "E1701", {"start": v(-0.5, 2) * mm, "end": v(-0.48, 2.01) * mm});
            skLineSegment(sketch, "E1702", {"start": v(-0.48, 2.01) * mm, "end": v(-0.46, 2.03) * mm});
            skLineSegment(sketch, "E1703", {"start": v(-0.46, 2.03) * mm, "end": v(-0.44, 2.04) * mm});
            skLineSegment(sketch, "E1704", {"start": v(-0.44, 2.04) * mm, "end": v(-0.42, 2.05) * mm});
            skLineSegment(sketch, "E1705", {"start": v(-0.42, 2.05) * mm, "end": v(-0.4, 2.07) * mm});
            skLineSegment(sketch, "E1706", {"start": v(-0.4, 2.07) * mm, "end": v(-0.4, 2.08) * mm});
            skLineSegment(sketch, "E1707", {"start": v(-0.4, 2.08) * mm, "end": v(-0.38, 2.1) * mm});
            skLineSegment(sketch, "E1708", {"start": v(-0.38, 2.1) * mm, "end": v(-0.36, 2.1) * mm});
            skLineSegment(sketch, "E1709", {"start": v(-0.36, 2.1) * mm, "end": v(-0.35, 2.12) * mm});
            skLineSegment(sketch, "E1710", {"start": v(-0.35, 2.12) * mm, "end": v(-0.33, 2.13) * mm});
            skLineSegment(sketch, "E1711", {"start": v(-0.33, 2.13) * mm, "end": v(-0.32, 2.14) * mm});
            skLineSegment(sketch, "E1712", {"start": v(-0.32, 2.14) * mm, "end": v(-0.3, 2.15) * mm});
            skLineSegment(sketch, "E1713", {"start": v(-0.3, 2.15) * mm, "end": v(-0.3, 2.16) * mm});
            skLineSegment(sketch, "E1714", {"start": v(-0.3, 2.16) * mm, "end": v(-0.28, 2.17) * mm});
            skLineSegment(sketch, "E1715", {"start": v(-0.28, 2.17) * mm, "end": v(-0.27, 2.18) * mm});
            skLineSegment(sketch, "E1716", {"start": v(-0.27, 2.18) * mm, "end": v(-0.26, 2.2) * mm});
            skLineSegment(sketch, "E1717", {"start": v(-0.26, 2.2) * mm, "end": v(-0.25, 2.2) * mm});
            skLineSegment(sketch, "E1718", {"start": v(-0.25, 2.2) * mm, "end": v(-0.25, 2.2) * mm});
            skLineSegment(sketch, "E1719", {"start": v(-0.25, 2.2) * mm, "end": v(-0.24, 2.21) * mm});
            skLineSegment(sketch, "E1720", {"start": v(-0.24, 2.21) * mm, "end": v(-0.23, 2.22) * mm});
            skLineSegment(sketch, "E1721", {"start": v(-0.23, 2.22) * mm, "end": v(-0.23, 2.22) * mm});
            skLineSegment(sketch, "E1722", {"start": v(-0.23, 2.22) * mm, "end": v(-0.22, 2.23) * mm});
            skLineSegment(sketch, "E1723", {"start": v(-0.22, 2.23) * mm, "end": v(-0.22, 2.23) * mm});
            skLineSegment(sketch, "E1724", {"start": v(-0.22, 2.23) * mm, "end": v(-0.21, 2.24) * mm});
            skLineSegment(sketch, "E1725", {"start": v(-0.21, 2.24) * mm, "end": v(-0.21, 2.24) * mm});
            skLineSegment(sketch, "E1726", {"start": v(-0.21, 2.24) * mm, "end": v(-0.2, 2.24) * mm});
            skLineSegment(sketch, "E1727", {"start": v(-0.2, 2.24) * mm, "end": v(-0.2, 2.24) * mm});
            skLineSegment(sketch, "E1728", {"start": v(-0.2, 2.24) * mm, "end": v(-0.21, 2.3) * mm});
            skLineSegment(sketch, "E1729", {"start": v(-0.21, 2.3) * mm, "end": v(-0.22, 2.37) * mm});
            skLineSegment(sketch, "E1730", {"start": v(-0.22, 2.37) * mm, "end": v(-0.23, 2.44) * mm});
            skLineSegment(sketch, "E1731", {"start": v(-0.23, 2.44) * mm, "end": v(-0.23, 2.5) * mm});
            skLineSegment(sketch, "E1732", {"start": v(-0.23, 2.5) * mm, "end": v(-0.24, 2.57) * mm});
            skLineSegment(sketch, "E1733", {"start": v(-0.24, 2.57) * mm, "end": v(-0.25, 2.64) * mm});
            skLineSegment(sketch, "E1734", {"start": v(-0.25, 2.64) * mm, "end": v(-0.25, 2.71) * mm});
            skLineSegment(sketch, "E1735", {"start": v(-0.25, 2.71) * mm, "end": v(-0.26, 2.78) * mm});
            skLineSegment(sketch, "E1736", {"start": v(-0.26, 2.78) * mm, "end": v(-0.27, 2.85) * mm});
            skLineSegment(sketch, "E1737", {"start": v(-0.27, 2.85) * mm, "end": v(-0.27, 2.92) * mm});
            skLineSegment(sketch, "E1738", {"start": v(-0.27, 2.92) * mm, "end": v(-0.28, 3) * mm});
            skLineSegment(sketch, "E1739", {"start": v(-0.28, 3) * mm, "end": v(-0.29, 3.07) * mm});
            skLineSegment(sketch, "E1740", {"start": v(-0.29, 3.07) * mm, "end": v(-0.3, 3.14) * mm});
            skLineSegment(sketch, "E1741", {"start": v(-0.3, 3.14) * mm, "end": v(-0.3, 3.21) * mm});
            skLineSegment(sketch, "E1742", {"start": v(-0.3, 3.21) * mm, "end": v(-0.31, 3.29) * mm});
            skLineSegment(sketch, "E1743", {"start": v(-0.31, 3.29) * mm, "end": v(-0.32, 3.36) * mm});
            skLineSegment(sketch, "E1744", {"start": v(-0.32, 3.36) * mm, "end": v(-0.33, 3.44) * mm});
            skLineSegment(sketch, "E1745", {"start": v(-0.33, 3.44) * mm, "end": v(-0.33, 3.51) * mm});
            skLineSegment(sketch, "E1746", {"start": v(-0.33, 3.51) * mm, "end": v(-0.34, 3.6) * mm});
            skLineSegment(sketch, "E1747", {"start": v(-0.34, 3.6) * mm, "end": v(-0.35, 3.67) * mm});
            skLineSegment(sketch, "E1748", {"start": v(-0.35, 3.67) * mm, "end": v(-0.36, 3.75) * mm});
            skLineSegment(sketch, "E1749", {"start": v(-0.36, 3.75) * mm, "end": v(-0.37, 3.83) * mm});
            skLineSegment(sketch, "E1750", {"start": v(-0.37, 3.83) * mm, "end": v(-0.38, 3.9) * mm});
            skLineSegment(sketch, "E1751", {"start": v(-0.38, 3.9) * mm, "end": v(-0.39, 3.98) * mm});
            skLineSegment(sketch, "E1752", {"start": v(-0.39, 3.98) * mm, "end": v(-0.4, 4.06) * mm});
            skLineSegment(sketch, "E1753", {"start": v(-0.4, 4.06) * mm, "end": v(-0.4, 4.14) * mm});
            skLineSegment(sketch, "E1754", {"start": v(-0.4, 4.14) * mm, "end": v(-0.41, 4.23) * mm});
            skLineSegment(sketch, "E1755", {"start": v(-0.41, 4.23) * mm, "end": v(-0.42, 4.3) * mm});
            skLineSegment(sketch, "E1756", {"start": v(-0.42, 4.3) * mm, "end": v(-0.43, 4.39) * mm});
            skLineSegment(sketch, "E1757", {"start": v(-0.43, 4.39) * mm, "end": v(-0.44, 4.47) * mm});
            skLineSegment(sketch, "E1758", {"start": v(-0.44, 4.47) * mm, "end": v(-0.45, 4.56) * mm});
            skLineSegment(sketch, "E1759", {"start": v(-0.45, 4.56) * mm, "end": v(-0.46, 4.64) * mm});
            skLineSegment(sketch, "E1760", {"start": v(-0.46, 4.64) * mm, "end": v(-0.47, 4.72) * mm});
            skLineSegment(sketch, "E1761", {"start": v(-0.47, 4.72) * mm, "end": v(-0.48, 4.8) * mm});
            skLineSegment(sketch, "E1762", {"start": v(-0.48, 4.8) * mm, "end": v(-0.5, 4.9) * mm});
            skLineSegment(sketch, "E1763", {"start": v(-0.5, 4.9) * mm, "end": v(-0.5, 4.98) * mm});
            skLineSegment(sketch, "E1764", {"start": v(-0.5, 4.98) * mm, "end": v(-0.51, 5.06) * mm});
            skLineSegment(sketch, "E1765", {"start": v(-0.51, 5.06) * mm, "end": v(-0.52, 5.15) * mm});
            skLineSegment(sketch, "E1766", {"start": v(-0.52, 5.15) * mm, "end": v(-0.53, 5.24) * mm});
            skLineSegment(sketch, "E1767", {"start": v(-0.53, 5.24) * mm, "end": v(-0.54, 5.33) * mm});
            skLineSegment(sketch, "E1768", {"start": v(-0.54, 5.33) * mm, "end": v(-0.55, 5.41) * mm});
            skLineSegment(sketch, "E1769", {"start": v(-0.55, 5.41) * mm, "end": v(-0.56, 5.5) * mm});
            skLineSegment(sketch, "E1770", {"start": v(-0.56, 5.5) * mm, "end": v(-0.57, 5.59) * mm});
            skLineSegment(sketch, "E1771", {"start": v(-0.57, 5.59) * mm, "end": v(-0.59, 5.68) * mm});
            skLineSegment(sketch, "E1772", {"start": v(-0.59, 5.68) * mm, "end": v(-0.6, 5.77) * mm});
            skLineSegment(sketch, "E1773", {"start": v(-0.6, 5.77) * mm, "end": v(-0.6, 5.86) * mm});
            skLineSegment(sketch, "E1774", {"start": v(-0.6, 5.86) * mm, "end": v(-0.62, 5.95) * mm});
            skLineSegment(sketch, "E1775", {"start": v(-0.62, 5.95) * mm, "end": v(-0.63, 6.04) * mm});
            skLineSegment(sketch, "E1776", {"start": v(-0.63, 6.04) * mm, "end": v(-0.64, 6.13) * mm});
            skLineSegment(sketch, "E1777", {"start": v(-0.64, 6.13) * mm, "end": v(-0.65, 6.22) * mm});
            skLineSegment(sketch, "E1778", {"start": v(-0.65, 6.22) * mm, "end": v(-0.66, 6.31) * mm});
            skLineSegment(sketch, "E1779", {"start": v(-0.66, 6.31) * mm, "end": v(-0.67, 6.4) * mm});
            skLineSegment(sketch, "E1780", {"start": v(-0.67, 6.4) * mm, "end": v(-0.69, 6.5) * mm});
            skLineSegment(sketch, "E1781", {"start": v(-0.69, 6.5) * mm, "end": v(-0.7, 6.59) * mm});
            skLineSegment(sketch, "E1782", {"start": v(-0.7, 6.59) * mm, "end": v(-0.7, 6.68) * mm});
            skLineSegment(sketch, "E1783", {"start": v(-0.7, 6.68) * mm, "end": v(-0.72, 6.77) * mm});
            skLineSegment(sketch, "E1784", {"start": v(-0.72, 6.77) * mm, "end": v(-0.73, 6.87) * mm});
            skLineSegment(sketch, "E1785", {"start": v(-0.73, 6.87) * mm, "end": v(-0.74, 6.96) * mm});
            skLineSegment(sketch, "E1786", {"start": v(-0.74, 6.96) * mm, "end": v(-0.76, 7.05) * mm});
            skLineSegment(sketch, "E1787", {"start": v(-0.76, 7.05) * mm, "end": v(-0.77, 7.15) * mm});
            skLineSegment(sketch, "E1788", {"start": v(-0.77, 7.15) * mm, "end": v(-0.78, 7.24) * mm});
            skLineSegment(sketch, "E1789", {"start": v(-0.78, 7.24) * mm, "end": v(-0.8, 7.33) * mm});
            skLineSegment(sketch, "E1790", {"start": v(-0.8, 7.33) * mm, "end": v(-0.8, 7.43) * mm});
            skLineSegment(sketch, "E1791", {"start": v(-0.8, 7.43) * mm, "end": v(-0.81, 7.52) * mm});
            skLineSegment(sketch, "E1792", {"start": v(-0.81, 7.52) * mm, "end": v(-0.9, 7.44) * mm});
            skLineSegment(sketch, "E1793", {"start": v(-0.9, 7.44) * mm, "end": v(-1, 7.35) * mm});
            skLineSegment(sketch, "E1794", {"start": v(-1, 7.35) * mm, "end": v(-1.08, 7.27) * mm});
            skLineSegment(sketch, "E1795", {"start": v(-1.08, 7.27) * mm, "end": v(-1.17, 7.18) * mm});
            skLineSegment(sketch, "E1796", {"start": v(-1.17, 7.18) * mm, "end": v(-1.26, 7.1) * mm});
            skLineSegment(sketch, "E1797", {"start": v(-1.26, 7.1) * mm, "end": v(-1.35, 7.02) * mm});
            skLineSegment(sketch, "E1798", {"start": v(-1.35, 7.02) * mm, "end": v(-1.44, 6.93) * mm});
            skLineSegment(sketch, "E1799", {"start": v(-1.44, 6.93) * mm, "end": v(-1.52, 6.85) * mm});
            skLineSegment(sketch, "E1800", {"start": v(-1.52, 6.85) * mm, "end": v(-1.61, 6.77) * mm});
            skLineSegment(sketch, "E1801", {"start": v(-1.61, 6.77) * mm, "end": v(-1.7, 6.69) * mm});
            skLineSegment(sketch, "E1802", {"start": v(-1.7, 6.69) * mm, "end": v(-1.78, 6.6) * mm});
            skLineSegment(sketch, "E1803", {"start": v(-1.78, 6.6) * mm, "end": v(-1.87, 6.53) * mm});
            skLineSegment(sketch, "E1804", {"start": v(-1.87, 6.53) * mm, "end": v(-1.96, 6.45) * mm});
            skLineSegment(sketch, "E1805", {"start": v(-1.96, 6.45) * mm, "end": v(-2.04, 6.37) * mm});
            skLineSegment(sketch, "E1806", {"start": v(-2.04, 6.37) * mm, "end": v(-2.13, 6.29) * mm});
            skLineSegment(sketch, "E1807", {"start": v(-2.13, 6.29) * mm, "end": v(-2.21, 6.21) * mm});
            skLineSegment(sketch, "E1808", {"start": v(-2.21, 6.21) * mm, "end": v(-2.3, 6.13) * mm});
            skLineSegment(sketch, "E1809", {"start": v(-2.3, 6.13) * mm, "end": v(-2.38, 6.06) * mm});
            skLineSegment(sketch, "E1810", {"start": v(-2.38, 6.06) * mm, "end": v(-2.46, 5.98) * mm});
            skLineSegment(sketch, "E1811", {"start": v(-2.46, 5.98) * mm, "end": v(-2.55, 5.9) * mm});
            skLineSegment(sketch, "E1812", {"start": v(-2.55, 5.9) * mm, "end": v(-2.63, 5.82) * mm});
            skLineSegment(sketch, "E1813", {"start": v(-2.63, 5.82) * mm, "end": v(-2.71, 5.75) * mm});
            skLineSegment(sketch, "E1814", {"start": v(-2.71, 5.75) * mm, "end": v(-2.8, 5.67) * mm});
            skLineSegment(sketch, "E1815", {"start": v(-2.8, 5.67) * mm, "end": v(-2.87, 5.6) * mm});
            skLineSegment(sketch, "E1816", {"start": v(-2.87, 5.6) * mm, "end": v(-2.96, 5.52) * mm});
            skLineSegment(sketch, "E1817", {"start": v(-2.96, 5.52) * mm, "end": v(-3.04, 5.45) * mm});
            skLineSegment(sketch, "E1818", {"start": v(-3.04, 5.45) * mm, "end": v(-3.12, 5.37) * mm});
            skLineSegment(sketch, "E1819", {"start": v(-3.12, 5.37) * mm, "end": v(-3.2, 5.3) * mm});
            skLineSegment(sketch, "E1820", {"start": v(-3.2, 5.3) * mm, "end": v(-3.28, 5.22) * mm});
            skLineSegment(sketch, "E1821", {"start": v(-3.28, 5.22) * mm, "end": v(-3.36, 5.15) * mm});
            skLineSegment(sketch, "E1822", {"start": v(-3.36, 5.15) * mm, "end": v(-3.44, 5.07) * mm});
            skLineSegment(sketch, "E1823", {"start": v(-3.44, 5.07) * mm, "end": v(-3.52, 5) * mm});
            skLineSegment(sketch, "E1824", {"start": v(-3.52, 5) * mm, "end": v(-3.6, 4.93) * mm});
            skLineSegment(sketch, "E1825", {"start": v(-3.6, 4.93) * mm, "end": v(-3.67, 4.85) * mm});
            skLineSegment(sketch, "E1826", {"start": v(-3.67, 4.85) * mm, "end": v(-3.75, 4.78) * mm});
            skLineSegment(sketch, "E1827", {"start": v(-3.75, 4.78) * mm, "end": v(-3.83, 4.7) * mm});
            skLineSegment(sketch, "E1828", {"start": v(-3.83, 4.7) * mm, "end": v(-3.9, 4.63) * mm});
            skLineSegment(sketch, "E1829", {"start": v(-3.9, 4.63) * mm, "end": v(-3.98, 4.56) * mm});
            skLineSegment(sketch, "E1830", {"start": v(-3.98, 4.56) * mm, "end": v(-4.06, 4.49) * mm});
            skLineSegment(sketch, "E1831", {"start": v(-4.06, 4.49) * mm, "end": v(-4.13, 4.41) * mm});
            skLineSegment(sketch, "E1832", {"start": v(-4.13, 4.41) * mm, "end": v(-4.21, 4.34) * mm});
            skLineSegment(sketch, "E1833", {"start": v(-4.21, 4.34) * mm, "end": v(-4.29, 4.27) * mm});
            skLineSegment(sketch, "E1834", {"start": v(-4.29, 4.27) * mm, "end": v(-4.36, 4.2) * mm});
            skLineSegment(sketch, "E1835", {"start": v(-4.36, 4.2) * mm, "end": v(-4.44, 4.12) * mm});
            skLineSegment(sketch, "E1836", {"start": v(-4.44, 4.12) * mm, "end": v(-4.5, 4.05) * mm});
            skLineSegment(sketch, "E1837", {"start": v(-4.5, 4.05) * mm, "end": v(-4.58, 3.97) * mm});
            skLineSegment(sketch, "E1838", {"start": v(-4.58, 3.97) * mm, "end": v(-4.66, 3.9) * mm});
            skLineSegment(sketch, "E1839", {"start": v(-4.66, 3.9) * mm, "end": v(-4.73, 3.83) * mm});
            skLineSegment(sketch, "E1840", {"start": v(-4.73, 3.83) * mm, "end": v(-4.8, 3.75) * mm});
            skLineSegment(sketch, "E1841", {"start": v(-4.8, 3.75) * mm, "end": v(-4.87, 3.68) * mm});
            skLineSegment(sketch, "E1842", {"start": v(-4.87, 3.68) * mm, "end": v(-4.95, 3.6) * mm});
            skLineSegment(sketch, "E1843", {"start": v(-4.95, 3.6) * mm, "end": v(-5.02, 3.53) * mm});
            skLineSegment(sketch, "E1844", {"start": v(-5.02, 3.53) * mm, "end": v(-5.09, 3.46) * mm});
            skLineSegment(sketch, "E1845", {"start": v(-5.09, 3.46) * mm, "end": v(-5.16, 3.38) * mm});
            skLineSegment(sketch, "E1846", {"start": v(-5.16, 3.38) * mm, "end": v(-5.23, 3.31) * mm});
            skLineSegment(sketch, "E1847", {"start": v(-5.23, 3.31) * mm, "end": v(-5.3, 3.24) * mm});
            skLineSegment(sketch, "E1848", {"start": v(-5.3, 3.24) * mm, "end": v(-5.37, 3.16) * mm});
            skLineSegment(sketch, "E1849", {"start": v(-5.37, 3.16) * mm, "end": v(-5.44, 3.09) * mm});
            skLineSegment(sketch, "E1850", {"start": v(-5.44, 3.09) * mm, "end": v(-5.5, 3.01) * mm});
            skLineSegment(sketch, "E1851", {"start": v(-5.5, 3.01) * mm, "end": v(-5.58, 2.94) * mm});
            skLineSegment(sketch, "E1852", {"start": v(-5.58, 2.94) * mm, "end": v(-5.64, 2.86) * mm});
            skLineSegment(sketch, "E1853", {"start": v(-5.64, 2.86) * mm, "end": v(-5.71, 2.78) * mm});
            skLineSegment(sketch, "E1854", {"start": v(-5.71, 2.78) * mm, "end": v(-5.78, 2.7) * mm});
            skLineSegment(sketch, "E1855", {"start": v(-5.78, 2.7) * mm, "end": v(-5.85, 2.63) * mm});
            skLineSegment(sketch, "E1856", {"start": v(-5.85, 2.63) * mm, "end": v(-5.93, 2.53) * mm});
            skLineSegment(sketch, "E1857", {"start": v(-5.93, 2.53) * mm, "end": v(-6.02, 2.43) * mm});
            skLineSegment(sketch, "E1858", {"start": v(-6.02, 2.43) * mm, "end": v(-6.1, 2.32) * mm});
            skLineSegment(sketch, "E1859", {"start": v(-6.1, 2.32) * mm, "end": v(-6.19, 2.22) * mm});
            skLineSegment(sketch, "E1860", {"start": v(-6.19, 2.22) * mm, "end": v(-6.27, 2.11) * mm});
            skLineSegment(sketch, "E1861", {"start": v(-6.27, 2.11) * mm, "end": v(-6.35, 2.01) * mm});
            skLineSegment(sketch, "E1862", {"start": v(-6.35, 2.01) * mm, "end": v(-6.42, 1.9) * mm});
            skLineSegment(sketch, "E1863", {"start": v(-6.42, 1.9) * mm, "end": v(-6.5, 1.8) * mm});
            skLineSegment(sketch, "E1864", {"start": v(-6.5, 1.8) * mm, "end": v(-6.57, 1.7) * mm});
            skLineSegment(sketch, "E1865", {"start": v(-6.57, 1.7) * mm, "end": v(-6.65, 1.59) * mm});
            skLineSegment(sketch, "E1866", {"start": v(-6.65, 1.59) * mm, "end": v(-6.72, 1.48) * mm});
            skLineSegment(sketch, "E1867", {"start": v(-6.72, 1.48) * mm, "end": v(-6.79, 1.37) * mm});
            skLineSegment(sketch, "E1868", {"start": v(-6.79, 1.37) * mm, "end": v(-6.86, 1.26) * mm});
            skLineSegment(sketch, "E1869", {"start": v(-6.86, 1.26) * mm, "end": v(-6.92, 1.15) * mm});
            skLineSegment(sketch, "E1870", {"start": v(-6.92, 1.15) * mm, "end": v(-6.99, 1.04) * mm});
            skLineSegment(sketch, "E1871", {"start": v(-6.99, 1.04) * mm, "end": v(-7.05, 0.93) * mm});
            skLineSegment(sketch, "E1872", {"start": v(-7.05, 0.93) * mm, "end": v(-7.11, 0.82) * mm});
            skLineSegment(sketch, "E1873", {"start": v(-7.11, 0.82) * mm, "end": v(-7.17, 0.7) * mm});
            skLineSegment(sketch, "E1874", {"start": v(-7.17, 0.7) * mm, "end": v(-7.23, 0.6) * mm});
            skLineSegment(sketch, "E1875", {"start": v(-7.23, 0.6) * mm, "end": v(-7.29, 0.48) * mm});
            skLineSegment(sketch, "E1876", {"start": v(-7.29, 0.48) * mm, "end": v(-7.34, 0.37) * mm});
            skLineSegment(sketch, "E1877", {"start": v(-7.34, 0.37) * mm, "end": v(-7.4, 0.26) * mm});
            skLineSegment(sketch, "E1878", {"start": v(-7.4, 0.26) * mm, "end": v(-7.44, 0.14) * mm});
            skLineSegment(sketch, "E1879", {"start": v(-7.44, 0.14) * mm, "end": v(-7.5, 0.03) * mm});
            skLineSegment(sketch, "E1880", {"start": v(-7.5, 0.03) * mm, "end": v(-7.54, -0.09) * mm});
            skLineSegment(sketch, "E1881", {"start": v(-7.54, -0.09) * mm, "end": v(-7.59, -0.2) * mm});
            skLineSegment(sketch, "E1882", {"start": v(-7.59, -0.2) * mm, "end": v(-7.63, -0.32) * mm});
            skLineSegment(sketch, "E1883", {"start": v(-7.63, -0.32) * mm, "end": v(-7.68, -0.44) * mm});
            skLineSegment(sketch, "E1884", {"start": v(-7.68, -0.44) * mm, "end": v(-7.72, -0.55) * mm});
            skLineSegment(sketch, "E1885", {"start": v(-7.72, -0.55) * mm, "end": v(-7.75, -0.67) * mm});
            skLineSegment(sketch, "E1886", {"start": v(-7.75, -0.67) * mm, "end": v(-7.8, -0.8) * mm});
            skLineSegment(sketch, "E1887", {"start": v(-7.8, -0.8) * mm, "end": v(-7.83, -0.91) * mm});
            skLineSegment(sketch, "E1888", {"start": v(-7.83, -0.91) * mm, "end": v(-7.86, -1.03) * mm});
            skLineSegment(sketch, "E1889", {"start": v(-7.86, -1.03) * mm, "end": v(-7.9, -1.15) * mm});
            skLineSegment(sketch, "E1890", {"start": v(-7.9, -1.15) * mm, "end": v(-7.92, -1.27) * mm});
            skLineSegment(sketch, "E1891", {"start": v(-7.92, -1.27) * mm, "end": v(-7.95, -1.4) * mm});
            skLineSegment(sketch, "E1892", {"start": v(-7.95, -1.4) * mm, "end": v(-7.98, -1.52) * mm});
            skLineSegment(sketch, "E1893", {"start": v(-7.98, -1.52) * mm, "end": v(-8, -1.64) * mm});
            skLineSegment(sketch, "E1894", {"start": v(-8, -1.64) * mm, "end": v(-8.03, -1.76) * mm});
            skLineSegment(sketch, "E1895", {"start": v(-8.03, -1.76) * mm, "end": v(-8.05, -1.89) * mm});
            skLineSegment(sketch, "E1896", {"start": v(-8.05, -1.89) * mm, "end": v(-8.07, -2.01) * mm});
            skLineSegment(sketch, "E1897", {"start": v(-8.07, -2.01) * mm, "end": v(-8.08, -2.14) * mm});
            skLineSegment(sketch, "E1898", {"start": v(-8.08, -2.14) * mm, "end": v(-8.1, -2.26) * mm});
            skLineSegment(sketch, "E1899", {"start": v(-8.1, -2.26) * mm, "end": v(-8.11, -2.39) * mm});
            skLineSegment(sketch, "E1900", {"start": v(-8.11, -2.39) * mm, "end": v(-8.12, -2.52) * mm});
            skLineSegment(sketch, "E1901", {"start": v(-8.12, -2.52) * mm, "end": v(-8.13, -2.64) * mm});
            skLineSegment(sketch, "E1902", {"start": v(-8.13, -2.64) * mm, "end": v(-8.14, -2.77) * mm});
            skLineSegment(sketch, "E1903", {"start": v(-8.14, -2.77) * mm, "end": v(-8.15, -2.9) * mm});
            skLineSegment(sketch, "E1904", {"start": v(-8.15, -2.9) * mm, "end": v(-8.15, -3.03) * mm});
            skLineSegment(sketch, "E1905", {"start": v(-8.15, -3.03) * mm, "end": v(-8.16, -3.16) * mm});
            skLineSegment(sketch, "E1906", {"start": v(-8.16, -3.16) * mm, "end": v(-8.16, -3.29) * mm});
            skLineSegment(sketch, "E1907", {"start": v(-8.16, -3.29) * mm, "end": v(-8.15, -3.42) * mm});
            skLineSegment(sketch, "E1908", {"start": v(-8.15, -3.42) * mm, "end": v(-8.15, -3.55) * mm});
            skLineSegment(sketch, "E1909", {"start": v(-8.15, -3.55) * mm, "end": v(-8.15, -3.68) * mm});
            skLineSegment(sketch, "E1910", {"start": v(-8.15, -3.68) * mm, "end": v(-8.14, -3.82) * mm});
            skLineSegment(sketch, "E1911", {"start": v(-8.14, -3.82) * mm, "end": v(-8.13, -3.95) * mm});
            skLineSegment(sketch, "E1912", {"start": v(-8.13, -3.95) * mm, "end": v(-8.12, -4.08) * mm});
            skLineSegment(sketch, "E1913", {"start": v(-8.12, -4.08) * mm, "end": v(-8.1, -4.22) * mm});
            skLineSegment(sketch, "E1914", {"start": v(-8.1, -4.22) * mm, "end": v(-8.1, -4.35) * mm});
            skLineSegment(sketch, "E1915", {"start": v(-8.1, -4.35) * mm, "end": v(-8.07, -4.49) * mm});
            skLineSegment(sketch, "E1916", {"start": v(-8.07, -4.49) * mm, "end": v(-8.06, -4.63) * mm});
            skLineSegment(sketch, "E1917", {"start": v(-8.06, -4.63) * mm, "end": v(-8.03, -4.76) * mm});
            skLineSegment(sketch, "E1918", {"start": v(-8.03, -4.76) * mm, "end": v(-8.01, -4.9) * mm});
            skLineSegment(sketch, "E1919", {"start": v(-8.01, -4.9) * mm, "end": v(-7.99, -5.04) * mm});
            skLineSegment(sketch, "E1920", {"start": v(-7.99, -5.04) * mm, "end": v(-7.95, -5.25) * mm});
            skLineSegment(sketch, "E1921", {"start": v(-7.95, -5.25) * mm, "end": v(-7.9, -5.45) * mm});
            skLineSegment(sketch, "E1922", {"start": v(-7.9, -5.45) * mm, "end": v(-7.85, -5.65) * mm});
            skLineSegment(sketch, "E1923", {"start": v(-7.85, -5.65) * mm, "end": v(-7.8, -5.86) * mm});
            skLineSegment(sketch, "E1924", {"start": v(-7.8, -5.86) * mm, "end": v(-7.74, -6.06) * mm});
            skLineSegment(sketch, "E1925", {"start": v(-7.74, -6.06) * mm, "end": v(-7.67, -6.25) * mm});
            skLineSegment(sketch, "E1926", {"start": v(-7.67, -6.25) * mm, "end": v(-7.6, -6.45) * mm});
            skLineSegment(sketch, "E1927", {"start": v(-7.6, -6.45) * mm, "end": v(-7.53, -6.64) * mm});
            skLineSegment(sketch, "E1928", {"start": v(-7.53, -6.64) * mm, "end": v(-7.46, -6.83) * mm});
            skLineSegment(sketch, "E1929", {"start": v(-7.46, -6.83) * mm, "end": v(-7.38, -7.02) * mm});
            skLineSegment(sketch, "E1930", {"start": v(-7.38, -7.02) * mm, "end": v(-7.3, -7.2) * mm});
            skLineSegment(sketch, "E1931", {"start": v(-7.3, -7.2) * mm, "end": v(-7.2, -7.4) * mm});
            skLineSegment(sketch, "E1932", {"start": v(-7.2, -7.4) * mm, "end": v(-7.1, -7.58) * mm});
            skLineSegment(sketch, "E1933", {"start": v(-7.1, -7.58) * mm, "end": v(-7.01, -7.75) * mm});
            skLineSegment(sketch, "E1934", {"start": v(-7.01, -7.75) * mm, "end": v(-6.91, -7.93) * mm});
            skLineSegment(sketch, "E1935", {"start": v(-6.91, -7.93) * mm, "end": v(-6.81, -8.1) * mm});
            skLineSegment(sketch, "E1936", {"start": v(-6.81, -8.1) * mm, "end": v(-6.7, -8.28) * mm});
            skLineSegment(sketch, "E1937", {"start": v(-6.7, -8.28) * mm, "end": v(-6.6, -8.45) * mm});
            skLineSegment(sketch, "E1938", {"start": v(-6.6, -8.45) * mm, "end": v(-6.48, -8.61) * mm});
            skLineSegment(sketch, "E1939", {"start": v(-6.48, -8.61) * mm, "end": v(-6.36, -8.78) * mm});
            skLineSegment(sketch, "E1940", {"start": v(-6.36, -8.78) * mm, "end": v(-6.24, -8.94) * mm});
            skLineSegment(sketch, "E1941", {"start": v(-6.24, -8.94) * mm, "end": v(-6.11, -9.1) * mm});
            skLineSegment(sketch, "E1942", {"start": v(-6.11, -9.1) * mm, "end": v(-5.99, -9.25) * mm});
            skLineSegment(sketch, "E1943", {"start": v(-5.99, -9.25) * mm, "end": v(-5.85, -9.4) * mm});
            skLineSegment(sketch, "E1944", {"start": v(-5.85, -9.4) * mm, "end": v(-5.72, -9.55) * mm});
            skLineSegment(sketch, "E1945", {"start": v(-5.72, -9.55) * mm, "end": v(-5.58, -9.7) * mm});
            skLineSegment(sketch, "E1946", {"start": v(-5.58, -9.7) * mm, "end": v(-5.44, -9.84) * mm});
            skLineSegment(sketch, "E1947", {"start": v(-5.44, -9.84) * mm, "end": v(-5.3, -9.97) * mm});
            skLineSegment(sketch, "E1948", {"start": v(-5.3, -9.97) * mm, "end": v(-5.15, -10.1) * mm});
            skLineSegment(sketch, "E1949", {"start": v(-5.15, -10.1) * mm, "end": v(-5, -10.24) * mm});
            skLineSegment(sketch, "E1950", {"start": v(-5, -10.24) * mm, "end": v(-4.85, -10.37) * mm});
            skLineSegment(sketch, "E1951", {"start": v(-4.85, -10.37) * mm, "end": v(-4.7, -10.5) * mm});
            skLineSegment(sketch, "E1952", {"start": v(-4.7, -10.5) * mm, "end": v(-4.54, -10.61) * mm});
            skLineSegment(sketch, "E1953", {"start": v(-4.54, -10.61) * mm, "end": v(-4.38, -10.73) * mm});
            skLineSegment(sketch, "E1954", {"start": v(-4.38, -10.73) * mm, "end": v(-4.22, -10.85) * mm});
            skLineSegment(sketch, "E1955", {"start": v(-4.22, -10.85) * mm, "end": v(-4.05, -10.96) * mm});
            skLineSegment(sketch, "E1956", {"start": v(-4.05, -10.96) * mm, "end": v(-3.89, -11.06) * mm});
            skLineSegment(sketch, "E1957", {"start": v(-3.89, -11.06) * mm, "end": v(-3.72, -11.16) * mm});
            skLineSegment(sketch, "E1958", {"start": v(-3.72, -11.16) * mm, "end": v(-3.55, -11.26) * mm});
            skLineSegment(sketch, "E1959", {"start": v(-3.55, -11.26) * mm, "end": v(-3.37, -11.36) * mm});
            skLineSegment(sketch, "E1960", {"start": v(-3.37, -11.36) * mm, "end": v(-3.2, -11.45) * mm});
            skLineSegment(sketch, "E1961", {"start": v(-3.2, -11.45) * mm, "end": v(-3.02, -11.53) * mm});
            skLineSegment(sketch, "E1962", {"start": v(-3.02, -11.53) * mm, "end": v(-2.84, -11.62) * mm});
            skLineSegment(sketch, "E1963", {"start": v(-2.84, -11.62) * mm, "end": v(-2.66, -11.7) * mm});
            skLineSegment(sketch, "E1964", {"start": v(-2.66, -11.7) * mm, "end": v(-2.47, -11.77) * mm});
            skLineSegment(sketch, "E1965", {"start": v(-2.47, -11.77) * mm, "end": v(-2.29, -11.84) * mm});
            skLineSegment(sketch, "E1966", {"start": v(-2.29, -11.84) * mm, "end": v(-2.1, -11.9) * mm});
            skLineSegment(sketch, "E1967", {"start": v(-2.1, -11.9) * mm, "end": v(-1.91, -11.96) * mm});
            skLineSegment(sketch, "E1968", {"start": v(-1.91, -11.96) * mm, "end": v(-1.72, -12.02) * mm});
            skLineSegment(sketch, "E1969", {"start": v(-1.72, -12.02) * mm, "end": v(-1.53, -12.07) * mm});
            skLineSegment(sketch, "E1970", {"start": v(-1.53, -12.07) * mm, "end": v(-1.33, -12.11) * mm});
            skLineSegment(sketch, "E1971", {"start": v(-1.33, -12.11) * mm, "end": v(-1.14, -12.15) * mm});
            skLineSegment(sketch, "E1972", {"start": v(-1.14, -12.15) * mm, "end": v(-0.94, -12.2) * mm});
            skLineSegment(sketch, "E1973", {"start": v(-0.94, -12.2) * mm, "end": v(-0.74, -12.22) * mm});
            skLineSegment(sketch, "E1974", {"start": v(-0.74, -12.22) * mm, "end": v(-0.55, -12.25) * mm});
            skLineSegment(sketch, "E1975", {"start": v(-0.55, -12.25) * mm, "end": v(-0.35, -12.27) * mm});
            skLineSegment(sketch, "E1976", {"start": v(-0.35, -12.27) * mm, "end": v(-0.14, -12.29) * mm});
            skLineSegment(sketch, "E1977", {"start": v(-0.14, -12.29) * mm, "end": v(0.06, -12.3) * mm});
            skLineSegment(sketch, "E1978", {"start": v(0.06, -12.3) * mm, "end": v(0.26, -12.3) * mm});
            skLineSegment(sketch, "E1979", {"start": v(0.26, -12.3) * mm, "end": v(0.47, -12.3) * mm});
            skLineSegment(sketch, "E1980", {"start": v(0.47, -12.3) * mm, "end": v(0.67, -12.3) * mm});
            skLineSegment(sketch, "E1981", {"start": v(0.67, -12.3) * mm, "end": v(0.88, -12.3) * mm});
            skLineSegment(sketch, "E1982", {"start": v(0.88, -12.3) * mm, "end": v(1.08, -12.28) * mm});
            skLineSegment(sketch, "E1983", {"start": v(1.08, -12.28) * mm, "end": v(1.29, -12.26) * mm});
            skLineSegment(sketch, "E1984", {"start": v(1.29, -12.26) * mm, "end": v(1.27, -12.11) * mm});
            skLineSegment(sketch, "E1985", {"start": v(1.27, -12.11) * mm, "end": v(1.26, -11.96) * mm});
            skLineSegment(sketch, "E1986", {"start": v(1.26, -11.96) * mm, "end": v(1.24, -11.8) * mm});
            skLineSegment(sketch, "E1987", {"start": v(1.24, -11.8) * mm, "end": v(1.23, -11.66) * mm});
            skLineSegment(sketch, "E1988", {"start": v(1.23, -11.66) * mm, "end": v(1.2, -11.5) * mm});
            skLineSegment(sketch, "E1989", {"start": v(1.2, -11.5) * mm, "end": v(1.2, -11.36) * mm});
            skLineSegment(sketch, "E1990", {"start": v(1.2, -11.36) * mm, "end": v(1.18, -11.2) * mm});
            skLineSegment(sketch, "E1991", {"start": v(1.18, -11.2) * mm, "end": v(1.16, -11.05) * mm});
            skLineSegment(sketch, "E1992", {"start": v(1.16, -11.05) * mm, "end": v(1.14, -10.9) * mm});
            skLineSegment(sketch, "E1993", {"start": v(1.14, -10.9) * mm, "end": v(1.13, -10.75) * mm});
            skLineSegment(sketch, "E1994", {"start": v(1.13, -10.75) * mm, "end": v(1.11, -10.6) * mm});
            skLineSegment(sketch, "E1995", {"start": v(1.11, -10.6) * mm, "end": v(1.1, -10.45) * mm});
            skLineSegment(sketch, "E1996", {"start": v(1.1, -10.45) * mm, "end": v(1.08, -10.3) * mm});
            skLineSegment(sketch, "E1997", {"start": v(1.08, -10.3) * mm, "end": v(1.06, -10.15) * mm});
            skLineSegment(sketch, "E1998", {"start": v(1.06, -10.15) * mm, "end": v(1.05, -10) * mm});
            skLineSegment(sketch, "E1999", {"start": v(1.05, -10) * mm, "end": v(1.03, -9.85) * mm});
            skLineSegment(sketch, "E2000", {"start": v(1.03, -9.85) * mm, "end": v(1.02, -9.7) * mm});
            skLineSegment(sketch, "E2001", {"start": v(1.02, -9.7) * mm, "end": v(1, -9.55) * mm});
            skLineSegment(sketch, "E2002", {"start": v(1, -9.55) * mm, "end": v(0.98, -9.4) * mm});
            skLineSegment(sketch, "E2003", {"start": v(0.98, -9.4) * mm, "end": v(0.97, -9.24) * mm});
            skLineSegment(sketch, "E2004", {"start": v(0.97, -9.24) * mm, "end": v(0.95, -9.1) * mm});
            skLineSegment(sketch, "E2005", {"start": v(0.95, -9.1) * mm, "end": v(0.93, -8.94) * mm});
            skLineSegment(sketch, "E2006", {"start": v(0.93, -8.94) * mm, "end": v(0.92, -8.79) * mm});
            skLineSegment(sketch, "E2007", {"start": v(0.92, -8.79) * mm, "end": v(0.9, -8.64) * mm});
            skLineSegment(sketch, "E2008", {"start": v(0.9, -8.64) * mm, "end": v(0.89, -8.49) * mm});
            skLineSegment(sketch, "E2009", {"start": v(0.89, -8.49) * mm, "end": v(0.87, -8.34) * mm});
            skLineSegment(sketch, "E2010", {"start": v(0.87, -8.34) * mm, "end": v(0.85, -8.18) * mm});
            skLineSegment(sketch, "E2011", {"start": v(0.85, -8.18) * mm, "end": v(0.84, -8.03) * mm});
            skLineSegment(sketch, "E2012", {"start": v(0.84, -8.03) * mm, "end": v(0.82, -7.88) * mm});
            skLineSegment(sketch, "E2013", {"start": v(0.82, -7.88) * mm, "end": v(0.8, -7.73) * mm});
            skLineSegment(sketch, "E2014", {"start": v(0.8, -7.73) * mm, "end": v(0.79, -7.58) * mm});
            skLineSegment(sketch, "E2015", {"start": v(0.79, -7.58) * mm, "end": v(0.77, -7.43) * mm});
            skLineSegment(sketch, "E2016", {"start": v(0.77, -7.43) * mm, "end": v(0.76, -7.27) * mm});
            skLineSegment(sketch, "E2017", {"start": v(0.76, -7.27) * mm, "end": v(0.74, -7.12) * mm});
            skLineSegment(sketch, "E2018", {"start": v(0.74, -7.12) * mm, "end": v(0.72, -6.97) * mm});
            skLineSegment(sketch, "E2019", {"start": v(0.72, -6.97) * mm, "end": v(0.7, -6.82) * mm});
            skLineSegment(sketch, "E2020", {"start": v(0.7, -6.82) * mm, "end": v(0.7, -6.67) * mm});
            skLineSegment(sketch, "E2021", {"start": v(0.7, -6.67) * mm, "end": v(0.67, -6.51) * mm});
            skLineSegment(sketch, "E2022", {"start": v(0.67, -6.51) * mm, "end": v(0.66, -6.36) * mm});
            skLineSegment(sketch, "E2023", {"start": v(0.66, -6.36) * mm, "end": v(0.64, -6.2) * mm});
            skLineSegment(sketch, "E2024", {"start": v(0.64, -6.2) * mm, "end": v(0.63, -6.06) * mm});
            skLineSegment(sketch, "E2025", {"start": v(0.63, -6.06) * mm, "end": v(0.6, -5.9) * mm});
            skLineSegment(sketch, "E2026", {"start": v(0.6, -5.9) * mm, "end": v(0.6, -5.75) * mm});
            skLineSegment(sketch, "E2027", {"start": v(0.6, -5.75) * mm, "end": v(0.58, -5.6) * mm});
            skLineSegment(sketch, "E2028", {"start": v(0.58, -5.6) * mm, "end": v(0.56, -5.45) * mm});
            skLineSegment(sketch, "E2029", {"start": v(0.56, -5.45) * mm, "end": v(0.54, -5.3) * mm});
            skLineSegment(sketch, "E2030", {"start": v(0.54, -5.3) * mm, "end": v(0.53, -5.14) * mm});
            skLineSegment(sketch, "E2031", {"start": v(0.53, -5.14) * mm, "end": v(0.51, -4.99) * mm});
            skLineSegment(sketch, "E2032", {"start": v(0.51, -4.99) * mm, "end": v(0.5, -4.84) * mm});
            skLineSegment(sketch, "E2033", {"start": v(0.5, -4.84) * mm, "end": v(0.48, -4.68) * mm});
            skLineSegment(sketch, "E2034", {"start": v(0.48, -4.68) * mm, "end": v(0.46, -4.53) * mm});
            skLineSegment(sketch, "E2035", {"start": v(0.46, -4.53) * mm, "end": v(0.45, -4.38) * mm});
            skLineSegment(sketch, "E2036", {"start": v(0.45, -4.38) * mm, "end": v(0.43, -4.22) * mm});
            skLineSegment(sketch, "E2037", {"start": v(0.43, -4.22) * mm, "end": v(0.41, -4.07) * mm});
            skLineSegment(sketch, "E2038", {"start": v(0.41, -4.07) * mm, "end": v(0.4, -3.91) * mm});
            skLineSegment(sketch, "E2039", {"start": v(0.4, -3.91) * mm, "end": v(0.38, -3.76) * mm});
            skLineSegment(sketch, "E2040", {"start": v(0.38, -3.76) * mm, "end": v(0.36, -3.6) * mm});
            skLineSegment(sketch, "E2041", {"start": v(0.36, -3.6) * mm, "end": v(0.35, -3.45) * mm});
            skLineSegment(sketch, "E2042", {"start": v(0.35, -3.45) * mm, "end": v(0.33, -3.3) * mm});
            skLineSegment(sketch, "E2043", {"start": v(0.33, -3.3) * mm, "end": v(0.31, -3.14) * mm});
            skLineSegment(sketch, "E2044", {"start": v(0.31, -3.14) * mm, "end": v(0.3, -2.99) * mm});
            skLineSegment(sketch, "E2045", {"start": v(0.3, -2.99) * mm, "end": v(0.28, -2.84) * mm});
            skLineSegment(sketch, "E2046", {"start": v(0.28, -2.84) * mm, "end": v(0.26, -2.68) * mm});
            skLineSegment(sketch, "E2047", {"start": v(0.26, -2.68) * mm, "end": v(0.25, -2.53) * mm});
            skLineSegment(sketch, "E2048", {"start": v(0.25, -2.53) * mm, "end": v(0.1, -2.59) * mm});
            skLineSegment(sketch, "E2049", {"start": v(0.1, -2.59) * mm, "end": v(-0.02, -2.65) * mm});
            skLineSegment(sketch, "E2050", {"start": v(-0.02, -2.65) * mm, "end": v(-0.15, -2.72) * mm});
            skLineSegment(sketch, "E2051", {"start": v(-0.15, -2.72) * mm, "end": v(-0.28, -2.79) * mm});
            skLineSegment(sketch, "E2052", {"start": v(-0.28, -2.79) * mm, "end": v(-0.4, -2.85) * mm});
            skLineSegment(sketch, "E2053", {"start": v(-0.4, -2.85) * mm, "end": v(-0.52, -2.92) * mm});
            skLineSegment(sketch, "E2054", {"start": v(-0.52, -2.92) * mm, "end": v(-0.63, -2.99) * mm});
            skLineSegment(sketch, "E2055", {"start": v(-0.63, -2.99) * mm, "end": v(-0.75, -3.06) * mm});
            skLineSegment(sketch, "E2056", {"start": v(-0.75, -3.06) * mm, "end": v(-0.85, -3.13) * mm});
            skLineSegment(sketch, "E2057", {"start": v(-0.85, -3.13) * mm, "end": v(-0.95, -3.2) * mm});
            skLineSegment(sketch, "E2058", {"start": v(-0.95, -3.2) * mm, "end": v(-1.05, -3.28) * mm});
            skLineSegment(sketch, "E2059", {"start": v(-1.05, -3.28) * mm, "end": v(-1.15, -3.35) * mm});
            skLineSegment(sketch, "E2060", {"start": v(-1.15, -3.35) * mm, "end": v(-1.24, -3.43) * mm});
            skLineSegment(sketch, "E2061", {"start": v(-1.24, -3.43) * mm, "end": v(-1.33, -3.5) * mm});
            skLineSegment(sketch, "E2062", {"start": v(-1.33, -3.5) * mm, "end": v(-1.41, -3.59) * mm});
            skLineSegment(sketch, "E2063", {"start": v(-1.41, -3.59) * mm, "end": v(-1.5, -3.67) * mm});
            skLineSegment(sketch, "E2064", {"start": v(-1.5, -3.67) * mm, "end": v(-1.57, -3.75) * mm});
            skLineSegment(sketch, "E2065", {"start": v(-1.57, -3.75) * mm, "end": v(-1.64, -3.84) * mm});
            skLineSegment(sketch, "E2066", {"start": v(-1.64, -3.84) * mm, "end": v(-1.7, -3.92) * mm});
            skLineSegment(sketch, "E2067", {"start": v(-1.7, -3.92) * mm, "end": v(-1.77, -4) * mm});
            skLineSegment(sketch, "E2068", {"start": v(-1.77, -4) * mm, "end": v(-1.84, -4.1) * mm});
            skLineSegment(sketch, "E2069", {"start": v(-1.84, -4.1) * mm, "end": v(-1.9, -4.2) * mm});
            skLineSegment(sketch, "E2070", {"start": v(-1.9, -4.2) * mm, "end": v(-1.95, -4.29) * mm});
            skLineSegment(sketch, "E2071", {"start": v(-1.95, -4.29) * mm, "end": v(-2, -4.38) * mm});
            skLineSegment(sketch, "E2072", {"start": v(-2, -4.38) * mm, "end": v(-2.04, -4.48) * mm});
            skLineSegment(sketch, "E2073", {"start": v(-2.04, -4.48) * mm, "end": v(-2.09, -4.58) * mm});
            skLineSegment(sketch, "E2074", {"start": v(-2.09, -4.58) * mm, "end": v(-2.13, -4.68) * mm});
            skLineSegment(sketch, "E2075", {"start": v(-2.13, -4.68) * mm, "end": v(-2.16, -4.8) * mm});
            skLineSegment(sketch, "E2076", {"start": v(-2.16, -4.8) * mm, "end": v(-2.2, -4.9) * mm});
            skLineSegment(sketch, "E2077", {"start": v(-2.2, -4.9) * mm, "end": v(-2.22, -5) * mm});
            skLineSegment(sketch, "E2078", {"start": v(-2.22, -5) * mm, "end": v(-2.25, -5.12) * mm});
            skLineSegment(sketch, "E2079", {"start": v(-2.25, -5.12) * mm, "end": v(-2.27, -5.24) * mm});
            skLineSegment(sketch, "E2080", {"start": v(-2.27, -5.24) * mm, "end": v(-2.29, -5.35) * mm});
            skLineSegment(sketch, "E2081", {"start": v(-2.29, -5.35) * mm, "end": v(-2.3, -5.47) * mm});
            skLineSegment(sketch, "E2082", {"start": v(-2.3, -5.47) * mm, "end": v(-2.32, -5.6) * mm});
            skLineSegment(sketch, "E2083", {"start": v(-2.32, -5.6) * mm, "end": v(-2.32, -5.72) * mm});
            skLineSegment(sketch, "E2084", {"start": v(-2.32, -5.72) * mm, "end": v(-2.33, -5.85) * mm});
            skLineSegment(sketch, "E2085", {"start": v(-2.33, -5.85) * mm, "end": v(-2.33, -5.99) * mm});
            skLineSegment(sketch, "E2086", {"start": v(-2.33, -5.99) * mm, "end": v(-2.32, -6.12) * mm});
            skLineSegment(sketch, "E2087", {"start": v(-2.32, -6.12) * mm, "end": v(-2.32, -6.26) * mm});
            skLineSegment(sketch, "E2088", {"start": v(-2.32, -6.26) * mm, "end": v(-2.3, -6.4) * mm});
            skLineSegment(sketch, "E2089", {"start": v(-2.3, -6.4) * mm, "end": v(-2.3, -6.54) * mm});
            skLineSegment(sketch, "E2090", {"start": v(-2.3, -6.54) * mm, "end": v(-2.28, -6.7) * mm});
            skLineSegment(sketch, "E2091", {"start": v(-2.28, -6.7) * mm, "end": v(-2.26, -6.84) * mm});
            skLineSegment(sketch, "E2092", {"start": v(-2.26, -6.84) * mm, "end": v(-2.24, -7) * mm});
            skLineSegment(sketch, "E2093", {"start": v(-2.24, -7) * mm, "end": v(-2.2, -7.16) * mm});
            skLineSegment(sketch, "E2094", {"start": v(-2.2, -7.16) * mm, "end": v(-2.18, -7.32) * mm});
            skLineSegment(sketch, "E2095", {"start": v(-2.18, -7.32) * mm, "end": v(-2.15, -7.48) * mm});
            skLineSegment(sketch, "E2096", {"start": v(-2.15, -7.48) * mm, "end": v(-2.1, -7.65) * mm});
            skLineSegment(sketch, "E2097", {"start": v(-2.1, -7.65) * mm, "end": v(-2.07, -7.82) * mm});
            skLineSegment(sketch, "E2098", {"start": v(-2.07, -7.82) * mm, "end": v(-2.03, -8) * mm});
            skLineSegment(sketch, "E2099", {"start": v(-2.03, -8) * mm, "end": v(-1.98, -8.18) * mm});
            skLineSegment(sketch, "E2100", {"start": v(-1.98, -8.18) * mm, "end": v(-1.93, -8.37) * mm});
            skLineSegment(sketch, "E2101", {"start": v(-1.93, -8.37) * mm, "end": v(-1.88, -8.55) * mm});
            skLineSegment(sketch, "E2102", {"start": v(-1.88, -8.55) * mm, "end": v(-1.82, -8.75) * mm});
            skLineSegment(sketch, "E2103", {"start": v(-1.82, -8.75) * mm, "end": v(-1.76, -8.94) * mm});
            skLineSegment(sketch, "E2104", {"start": v(-1.76, -8.94) * mm, "end": v(-1.7, -9.14) * mm});
            skLineSegment(sketch, "E2105", {"start": v(-1.7, -9.14) * mm, "end": v(-1.63, -9.35) * mm});
            skLineSegment(sketch, "E2106", {"start": v(-1.63, -9.35) * mm, "end": v(-1.56, -9.55) * mm});
            skLineSegment(sketch, "E2107", {"start": v(-1.56, -9.55) * mm, "end": v(-1.49, -9.77) * mm});
            skLineSegment(sketch, "E2108", {"start": v(-1.49, -9.77) * mm, "end": v(-1.41, -9.98) * mm});
            skLineSegment(sketch, "E2109", {"start": v(-1.41, -9.98) * mm, "end": v(-1.33, -10.2) * mm});
            skLineSegment(sketch, "E2110", {"start": v(-1.33, -10.2) * mm, "end": v(-1.25, -10.43) * mm});
            skLineSegment(sketch, "E2111", {"start": v(-1.25, -10.43) * mm, "end": v(-1.17, -10.66) * mm});
            skLineSegment(sketch, "E2112", {"start": v(1.62, 14.63) * mm, "end": v(1.79, 14.73) * mm});
            skLineSegment(sketch, "E2113", {"start": v(1.79, 14.73) * mm, "end": v(1.95, 14.84) * mm});
            skLineSegment(sketch, "E2114", {"start": v(1.95, 14.84) * mm, "end": v(2.11, 14.94) * mm});
            skLineSegment(sketch, "E2115", {"start": v(2.11, 14.94) * mm, "end": v(2.27, 15.05) * mm});
            skLineSegment(sketch, "E2116", {"start": v(2.27, 15.05) * mm, "end": v(2.43, 15.16) * mm});
            skLineSegment(sketch, "E2117", {"start": v(2.43, 15.16) * mm, "end": v(2.58, 15.27) * mm});
            skLineSegment(sketch, "E2118", {"start": v(2.58, 15.27) * mm, "end": v(2.74, 15.37) * mm});
            skLineSegment(sketch, "E2119", {"start": v(2.74, 15.37) * mm, "end": v(2.89, 15.49) * mm});
            skLineSegment(sketch, "E2120", {"start": v(2.89, 15.49) * mm, "end": v(3.03, 15.6) * mm});
            skLineSegment(sketch, "E2121", {"start": v(3.03, 15.6) * mm, "end": v(3.18, 15.7) * mm});
            skLineSegment(sketch, "E2122", {"start": v(3.18, 15.7) * mm, "end": v(3.32, 15.82) * mm});
            skLineSegment(sketch, "E2123", {"start": v(3.32, 15.82) * mm, "end": v(3.46, 15.94) * mm});
            skLineSegment(sketch, "E2124", {"start": v(3.46, 15.94) * mm, "end": v(3.6, 16.05) * mm});
            skLineSegment(sketch, "E2125", {"start": v(3.6, 16.05) * mm, "end": v(3.74, 16.17) * mm});
            skLineSegment(sketch, "E2126", {"start": v(3.74, 16.17) * mm, "end": v(3.87, 16.29) * mm});
            skLineSegment(sketch, "E2127", {"start": v(3.87, 16.29) * mm, "end": v(4, 16.4) * mm});
            skLineSegment(sketch, "E2128", {"start": v(4, 16.4) * mm, "end": v(4.13, 16.52) * mm});
            skLineSegment(sketch, "E2129", {"start": v(4.13, 16.52) * mm, "end": v(4.26, 16.64) * mm});
            skLineSegment(sketch, "E2130", {"start": v(4.26, 16.64) * mm, "end": v(4.38, 16.77) * mm});
            skLineSegment(sketch, "E2131", {"start": v(4.38, 16.77) * mm, "end": v(4.5, 16.89) * mm});
            skLineSegment(sketch, "E2132", {"start": v(4.5, 16.89) * mm, "end": v(4.62, 17.01) * mm});
            skLineSegment(sketch, "E2133", {"start": v(4.62, 17.01) * mm, "end": v(4.74, 17.14) * mm});
            skLineSegment(sketch, "E2134", {"start": v(4.74, 17.14) * mm, "end": v(4.85, 17.26) * mm});
            skLineSegment(sketch, "E2135", {"start": v(4.85, 17.26) * mm, "end": v(4.97, 17.39) * mm});
            skLineSegment(sketch, "E2136", {"start": v(4.97, 17.39) * mm, "end": v(5.08, 17.52) * mm});
            skLineSegment(sketch, "E2137", {"start": v(5.08, 17.52) * mm, "end": v(5.19, 17.65) * mm});
            skLineSegment(sketch, "E2138", {"start": v(5.19, 17.65) * mm, "end": v(5.3, 17.78) * mm});
            skLineSegment(sketch, "E2139", {"start": v(5.3, 17.78) * mm, "end": v(5.4, 17.9) * mm});
            skLineSegment(sketch, "E2140", {"start": v(5.4, 17.9) * mm, "end": v(5.5, 18.04) * mm});
            skLineSegment(sketch, "E2141", {"start": v(5.5, 18.04) * mm, "end": v(5.6, 18.17) * mm});
            skLineSegment(sketch, "E2142", {"start": v(5.6, 18.17) * mm, "end": v(5.7, 18.3) * mm});
            skLineSegment(sketch, "E2143", {"start": v(5.7, 18.3) * mm, "end": v(5.79, 18.44) * mm});
            skLineSegment(sketch, "E2144", {"start": v(5.79, 18.44) * mm, "end": v(5.88, 18.58) * mm});
            skLineSegment(sketch, "E2145", {"start": v(5.88, 18.58) * mm, "end": v(5.97, 18.71) * mm});
            skLineSegment(sketch, "E2146", {"start": v(5.97, 18.71) * mm, "end": v(6.06, 18.85) * mm});
            skLineSegment(sketch, "E2147", {"start": v(6.06, 18.85) * mm, "end": v(6.15, 19) * mm});
            skLineSegment(sketch, "E2148", {"start": v(6.15, 19) * mm, "end": v(6.23, 19.13) * mm});
            skLineSegment(sketch, "E2149", {"start": v(6.23, 19.13) * mm, "end": v(6.31, 19.27) * mm});
            skLineSegment(sketch, "E2150", {"start": v(6.31, 19.27) * mm, "end": v(6.4, 19.42) * mm});
            skLineSegment(sketch, "E2151", {"start": v(6.4, 19.42) * mm, "end": v(6.47, 19.56) * mm});
            skLineSegment(sketch, "E2152", {"start": v(6.47, 19.56) * mm, "end": v(6.54, 19.7) * mm});
            skLineSegment(sketch, "E2153", {"start": v(6.54, 19.7) * mm, "end": v(6.62, 19.85) * mm});
            skLineSegment(sketch, "E2154", {"start": v(6.62, 19.85) * mm, "end": v(6.69, 20) * mm});
            skLineSegment(sketch, "E2155", {"start": v(6.69, 20) * mm, "end": v(6.76, 20.15) * mm});
            skLineSegment(sketch, "E2156", {"start": v(6.76, 20.15) * mm, "end": v(6.82, 20.3) * mm});
            skLineSegment(sketch, "E2157", {"start": v(6.82, 20.3) * mm, "end": v(6.89, 20.45) * mm});
            skLineSegment(sketch, "E2158", {"start": v(6.89, 20.45) * mm, "end": v(6.95, 20.6) * mm});
            skLineSegment(sketch, "E2159", {"start": v(6.95, 20.6) * mm, "end": v(7, 20.75) * mm});
            skLineSegment(sketch, "E2160", {"start": v(7, 20.75) * mm, "end": v(7.07, 20.9) * mm});
            skLineSegment(sketch, "E2161", {"start": v(7.07, 20.9) * mm, "end": v(7.12, 21.06) * mm});
            skLineSegment(sketch, "E2162", {"start": v(7.12, 21.06) * mm, "end": v(7.18, 21.21) * mm});
            skLineSegment(sketch, "E2163", {"start": v(7.18, 21.21) * mm, "end": v(7.23, 21.37) * mm});
            skLineSegment(sketch, "E2164", {"start": v(7.23, 21.37) * mm, "end": v(7.28, 21.53) * mm});
            skLineSegment(sketch, "E2165", {"start": v(7.28, 21.53) * mm, "end": v(7.32, 21.69) * mm});
            skLineSegment(sketch, "E2166", {"start": v(7.32, 21.69) * mm, "end": v(7.37, 21.85) * mm});
            skLineSegment(sketch, "E2167", {"start": v(7.37, 21.85) * mm, "end": v(7.41, 22) * mm});
            skLineSegment(sketch, "E2168", {"start": v(7.41, 22) * mm, "end": v(7.45, 22.17) * mm});
            skLineSegment(sketch, "E2169", {"start": v(7.45, 22.17) * mm, "end": v(7.5, 22.34) * mm});
            skLineSegment(sketch, "E2170", {"start": v(7.5, 22.34) * mm, "end": v(7.53, 22.5) * mm});
            skLineSegment(sketch, "E2171", {"start": v(7.53, 22.5) * mm, "end": v(7.57, 22.67) * mm});
            skLineSegment(sketch, "E2172", {"start": v(7.57, 22.67) * mm, "end": v(7.6, 22.83) * mm});
            skLineSegment(sketch, "E2173", {"start": v(7.6, 22.83) * mm, "end": v(7.63, 23) * mm});
            skLineSegment(sketch, "E2174", {"start": v(7.63, 23) * mm, "end": v(7.66, 23.17) * mm});
            skLineSegment(sketch, "E2175", {"start": v(7.66, 23.17) * mm, "end": v(7.68, 23.34) * mm});
            skLineSegment(sketch, "E2176", {"start": v(7.68, 23.34) * mm, "end": v(7.7, 23.39) * mm});
            skLineSegment(sketch, "E2177", {"start": v(7.7, 23.39) * mm, "end": v(7.7, 23.43) * mm});
            skLineSegment(sketch, "E2178", {"start": v(7.7, 23.43) * mm, "end": v(7.7, 23.48) * mm});
            skLineSegment(sketch, "E2179", {"start": v(7.7, 23.48) * mm, "end": v(7.7, 23.53) * mm});
            skLineSegment(sketch, "E2180", {"start": v(7.7, 23.53) * mm, "end": v(7.7, 23.58) * mm});
            skLineSegment(sketch, "E2181", {"start": v(7.7, 23.58) * mm, "end": v(7.7, 23.62) * mm});
            skLineSegment(sketch, "E2182", {"start": v(7.7, 23.62) * mm, "end": v(7.7, 23.67) * mm});
            skLineSegment(sketch, "E2183", {"start": v(7.7, 23.67) * mm, "end": v(7.7, 23.72) * mm});
            skLineSegment(sketch, "E2184", {"start": v(7.7, 23.72) * mm, "end": v(7.7, 23.78) * mm});
            skLineSegment(sketch, "E2185", {"start": v(7.7, 23.78) * mm, "end": v(7.7, 23.83) * mm});
            skLineSegment(sketch, "E2186", {"start": v(7.7, 23.83) * mm, "end": v(7.7, 23.88) * mm});
            skLineSegment(sketch, "E2187", {"start": v(7.7, 23.88) * mm, "end": v(7.7, 23.93) * mm});
            skLineSegment(sketch, "E2188", {"start": v(7.7, 23.93) * mm, "end": v(7.7, 23.98) * mm});
            skLineSegment(sketch, "E2189", {"start": v(7.7, 23.98) * mm, "end": v(7.7, 24.04) * mm});
            skLineSegment(sketch, "E2190", {"start": v(7.7, 24.04) * mm, "end": v(7.69, 24.1) * mm});
            skLineSegment(sketch, "E2191", {"start": v(7.69, 24.1) * mm, "end": v(7.68, 24.14) * mm});
            skLineSegment(sketch, "E2192", {"start": v(7.68, 24.14) * mm, "end": v(7.67, 24.2) * mm});
            skLineSegment(sketch, "E2193", {"start": v(7.67, 24.2) * mm, "end": v(7.67, 24.25) * mm});
            skLineSegment(sketch, "E2194", {"start": v(7.67, 24.25) * mm, "end": v(7.66, 24.3) * mm});
            skLineSegment(sketch, "E2195", {"start": v(7.66, 24.3) * mm, "end": v(7.65, 24.36) * mm});
            skLineSegment(sketch, "E2196", {"start": v(7.65, 24.36) * mm, "end": v(7.64, 24.42) * mm});
            skLineSegment(sketch, "E2197", {"start": v(7.64, 24.42) * mm, "end": v(7.63, 24.47) * mm});
            skLineSegment(sketch, "E2198", {"start": v(7.63, 24.47) * mm, "end": v(7.61, 24.53) * mm});
            skLineSegment(sketch, "E2199", {"start": v(7.61, 24.53) * mm, "end": v(7.6, 24.58) * mm});
            skLineSegment(sketch, "E2200", {"start": v(7.6, 24.58) * mm, "end": v(7.59, 24.64) * mm});
            skLineSegment(sketch, "E2201", {"start": v(7.59, 24.64) * mm, "end": v(7.58, 24.7) * mm});
            skLineSegment(sketch, "E2202", {"start": v(7.58, 24.7) * mm, "end": v(7.56, 24.75) * mm});
            skLineSegment(sketch, "E2203", {"start": v(7.56, 24.75) * mm, "end": v(7.55, 24.8) * mm});
            skLineSegment(sketch, "E2204", {"start": v(7.55, 24.8) * mm, "end": v(7.53, 24.85) * mm});
            skLineSegment(sketch, "E2205", {"start": v(7.53, 24.85) * mm, "end": v(7.51, 24.9) * mm});
            skLineSegment(sketch, "E2206", {"start": v(7.51, 24.9) * mm, "end": v(7.5, 24.96) * mm});
            skLineSegment(sketch, "E2207", {"start": v(7.5, 24.96) * mm, "end": v(7.48, 25.01) * mm});
            skLineSegment(sketch, "E2208", {"start": v(7.48, 25.01) * mm, "end": v(7.46, 25.07) * mm});
            skLineSegment(sketch, "E2209", {"start": v(7.46, 25.07) * mm, "end": v(7.44, 25.12) * mm});
            skLineSegment(sketch, "E2210", {"start": v(7.44, 25.12) * mm, "end": v(7.42, 25.17) * mm});
            skLineSegment(sketch, "E2211", {"start": v(7.42, 25.17) * mm, "end": v(7.4, 25.22) * mm});
            skLineSegment(sketch, "E2212", {"start": v(7.4, 25.22) * mm, "end": v(7.38, 25.27) * mm});
            skLineSegment(sketch, "E2213", {"start": v(7.38, 25.27) * mm, "end": v(7.36, 25.33) * mm});
            skLineSegment(sketch, "E2214", {"start": v(7.36, 25.33) * mm, "end": v(7.34, 25.38) * mm});
            skLineSegment(sketch, "E2215", {"start": v(7.34, 25.38) * mm, "end": v(7.31, 25.42) * mm});
            skLineSegment(sketch, "E2216", {"start": v(7.31, 25.42) * mm, "end": v(7.3, 25.47) * mm});
            skLineSegment(sketch, "E2217", {"start": v(7.3, 25.47) * mm, "end": v(7.27, 25.52) * mm});
            skLineSegment(sketch, "E2218", {"start": v(7.27, 25.52) * mm, "end": v(7.24, 25.57) * mm});
            skLineSegment(sketch, "E2219", {"start": v(7.24, 25.57) * mm, "end": v(7.22, 25.61) * mm});
            skLineSegment(sketch, "E2220", {"start": v(7.22, 25.61) * mm, "end": v(7.2, 25.66) * mm});
            skLineSegment(sketch, "E2221", {"start": v(7.2, 25.66) * mm, "end": v(7.17, 25.7) * mm});
            skLineSegment(sketch, "E2222", {"start": v(7.17, 25.7) * mm, "end": v(7.14, 25.75) * mm});
            skLineSegment(sketch, "E2223", {"start": v(7.14, 25.75) * mm, "end": v(7.11, 25.8) * mm});
            skLineSegment(sketch, "E2224", {"start": v(7.11, 25.8) * mm, "end": v(7.09, 25.83) * mm});
            skLineSegment(sketch, "E2225", {"start": v(7.09, 25.83) * mm, "end": v(7.06, 25.87) * mm});
            skLineSegment(sketch, "E2226", {"start": v(7.06, 25.87) * mm, "end": v(7.03, 25.91) * mm});
            skLineSegment(sketch, "E2227", {"start": v(7.03, 25.91) * mm, "end": v(7, 25.95) * mm});
            skLineSegment(sketch, "E2228", {"start": v(7, 25.95) * mm, "end": v(6.97, 25.99) * mm});
            skLineSegment(sketch, "E2229", {"start": v(6.97, 25.99) * mm, "end": v(6.94, 26.02) * mm});
            skLineSegment(sketch, "E2230", {"start": v(6.94, 26.02) * mm, "end": v(6.91, 26.06) * mm});
            skLineSegment(sketch, "E2231", {"start": v(6.91, 26.06) * mm, "end": v(6.88, 26.1) * mm});
            skLineSegment(sketch, "E2232", {"start": v(6.88, 26.1) * mm, "end": v(6.85, 26.12) * mm});
            skLineSegment(sketch, "E2233", {"start": v(6.85, 26.12) * mm, "end": v(6.82, 26.15) * mm});
            skLineSegment(sketch, "E2234", {"start": v(6.82, 26.15) * mm, "end": v(6.8, 26.18) * mm});
            skLineSegment(sketch, "E2235", {"start": v(6.8, 26.18) * mm, "end": v(6.76, 26.21) * mm});
            skLineSegment(sketch, "E2236", {"start": v(6.76, 26.21) * mm, "end": v(6.73, 26.24) * mm});
            skLineSegment(sketch, "E2237", {"start": v(6.73, 26.24) * mm, "end": v(6.7, 26.26) * mm});
            skLineSegment(sketch, "E2238", {"start": v(6.7, 26.26) * mm, "end": v(6.66, 26.29) * mm});
            skLineSegment(sketch, "E2239", {"start": v(6.66, 26.29) * mm, "end": v(6.63, 26.3) * mm});
            skLineSegment(sketch, "E2240", {"start": v(6.63, 26.3) * mm, "end": v(6.56, 26.35) * mm});
            skLineSegment(sketch, "E2241", {"start": v(6.56, 26.35) * mm, "end": v(6.5, 26.38) * mm});
            skLineSegment(sketch, "E2242", {"start": v(6.5, 26.38) * mm, "end": v(6.44, 26.41) * mm});
            skLineSegment(sketch, "E2243", {"start": v(6.44, 26.41) * mm, "end": v(6.38, 26.44) * mm});
            skLineSegment(sketch, "E2244", {"start": v(6.38, 26.44) * mm, "end": v(6.32, 26.47) * mm});
            skLineSegment(sketch, "E2245", {"start": v(6.32, 26.47) * mm, "end": v(6.26, 26.5) * mm});
            skLineSegment(sketch, "E2246", {"start": v(6.26, 26.5) * mm, "end": v(6.2, 26.51) * mm});
            skLineSegment(sketch, "E2247", {"start": v(6.2, 26.51) * mm, "end": v(6.14, 26.53) * mm});
            skLineSegment(sketch, "E2248", {"start": v(6.14, 26.53) * mm, "end": v(6.08, 26.55) * mm});
            skLineSegment(sketch, "E2249", {"start": v(6.08, 26.55) * mm, "end": v(6.02, 26.56) * mm});
            skLineSegment(sketch, "E2250", {"start": v(6.02, 26.56) * mm, "end": v(5.96, 26.57) * mm});
            skLineSegment(sketch, "E2251", {"start": v(5.96, 26.57) * mm, "end": v(5.9, 26.58) * mm});
            skLineSegment(sketch, "E2252", {"start": v(5.9, 26.58) * mm, "end": v(5.85, 26.59) * mm});
            skLineSegment(sketch, "E2253", {"start": v(5.85, 26.59) * mm, "end": v(5.79, 26.6) * mm});
            skLineSegment(sketch, "E2254", {"start": v(5.79, 26.6) * mm, "end": v(5.73, 26.6) * mm});
            skLineSegment(sketch, "E2255", {"start": v(5.73, 26.6) * mm, "end": v(5.68, 26.6) * mm});
            skLineSegment(sketch, "E2256", {"start": v(5.68, 26.6) * mm, "end": v(5.62, 26.6) * mm});
            skLineSegment(sketch, "E2257", {"start": v(5.62, 26.6) * mm, "end": v(5.56, 26.6) * mm});
            skLineSegment(sketch, "E2258", {"start": v(5.56, 26.6) * mm, "end": v(5.5, 26.59) * mm});
            skLineSegment(sketch, "E2259", {"start": v(5.5, 26.59) * mm, "end": v(5.45, 26.58) * mm});
            skLineSegment(sketch, "E2260", {"start": v(5.45, 26.58) * mm, "end": v(5.4, 26.57) * mm});
            skLineSegment(sketch, "E2261", {"start": v(5.4, 26.57) * mm, "end": v(5.34, 26.56) * mm});
            skLineSegment(sketch, "E2262", {"start": v(5.34, 26.56) * mm, "end": v(5.29, 26.54) * mm});
            skLineSegment(sketch, "E2263", {"start": v(5.29, 26.54) * mm, "end": v(5.24, 26.53) * mm});
            skLineSegment(sketch, "E2264", {"start": v(5.24, 26.53) * mm, "end": v(5.18, 26.5) * mm});
            skLineSegment(sketch, "E2265", {"start": v(5.18, 26.5) * mm, "end": v(5.13, 26.49) * mm});
            skLineSegment(sketch, "E2266", {"start": v(5.13, 26.49) * mm, "end": v(5.08, 26.47) * mm});
            skLineSegment(sketch, "E2267", {"start": v(5.08, 26.47) * mm, "end": v(5.03, 26.44) * mm});
            skLineSegment(sketch, "E2268", {"start": v(5.03, 26.44) * mm, "end": v(4.98, 26.42) * mm});
            skLineSegment(sketch, "E2269", {"start": v(4.98, 26.42) * mm, "end": v(4.93, 26.4) * mm});
            skLineSegment(sketch, "E2270", {"start": v(4.93, 26.4) * mm, "end": v(4.87, 26.37) * mm});
            skLineSegment(sketch, "E2271", {"start": v(4.87, 26.37) * mm, "end": v(4.83, 26.34) * mm});
            skLineSegment(sketch, "E2272", {"start": v(4.83, 26.34) * mm, "end": v(4.78, 26.3) * mm});
            skLineSegment(sketch, "E2273", {"start": v(4.78, 26.3) * mm, "end": v(4.73, 26.27) * mm});
            skLineSegment(sketch, "E2274", {"start": v(4.73, 26.27) * mm, "end": v(4.68, 26.24) * mm});
            skLineSegment(sketch, "E2275", {"start": v(4.68, 26.24) * mm, "end": v(4.63, 26.2) * mm});
            skLineSegment(sketch, "E2276", {"start": v(4.63, 26.2) * mm, "end": v(4.58, 26.17) * mm});
            skLineSegment(sketch, "E2277", {"start": v(4.58, 26.17) * mm, "end": v(4.54, 26.13) * mm});
            skLineSegment(sketch, "E2278", {"start": v(4.54, 26.13) * mm, "end": v(4.5, 26.1) * mm});
            skLineSegment(sketch, "E2279", {"start": v(4.5, 26.1) * mm, "end": v(4.45, 26.05) * mm});
            skLineSegment(sketch, "E2280", {"start": v(4.45, 26.05) * mm, "end": v(4.4, 26.01) * mm});
            skLineSegment(sketch, "E2281", {"start": v(4.4, 26.01) * mm, "end": v(4.36, 25.97) * mm});
            skLineSegment(sketch, "E2282", {"start": v(4.36, 25.97) * mm, "end": v(4.31, 25.93) * mm});
            skLineSegment(sketch, "E2283", {"start": v(4.31, 25.93) * mm, "end": v(4.27, 25.88) * mm});
            skLineSegment(sketch, "E2284", {"start": v(4.27, 25.88) * mm, "end": v(4.23, 25.83) * mm});
            skLineSegment(sketch, "E2285", {"start": v(4.23, 25.83) * mm, "end": v(4.19, 25.79) * mm});
            skLineSegment(sketch, "E2286", {"start": v(4.19, 25.79) * mm, "end": v(4.15, 25.74) * mm});
            skLineSegment(sketch, "E2287", {"start": v(4.15, 25.74) * mm, "end": v(4.1, 25.7) * mm});
            skLineSegment(sketch, "E2288", {"start": v(4.1, 25.7) * mm, "end": v(4.06, 25.64) * mm});
            skLineSegment(sketch, "E2289", {"start": v(4.06, 25.64) * mm, "end": v(4.02, 25.6) * mm});
            skLineSegment(sketch, "E2290", {"start": v(4.02, 25.6) * mm, "end": v(3.99, 25.54) * mm});
            skLineSegment(sketch, "E2291", {"start": v(3.99, 25.54) * mm, "end": v(3.95, 25.49) * mm});
            skLineSegment(sketch, "E2292", {"start": v(3.95, 25.49) * mm, "end": v(3.91, 25.44) * mm});
            skLineSegment(sketch, "E2293", {"start": v(3.91, 25.44) * mm, "end": v(3.87, 25.38) * mm});
            skLineSegment(sketch, "E2294", {"start": v(3.87, 25.38) * mm, "end": v(3.84, 25.33) * mm});
            skLineSegment(sketch, "E2295", {"start": v(3.84, 25.33) * mm, "end": v(3.8, 25.28) * mm});
            skLineSegment(sketch, "E2296", {"start": v(3.8, 25.28) * mm, "end": v(3.77, 25.22) * mm});
            skLineSegment(sketch, "E2297", {"start": v(3.77, 25.22) * mm, "end": v(3.73, 25.17) * mm});
            skLineSegment(sketch, "E2298", {"start": v(3.73, 25.17) * mm, "end": v(3.7, 25.1) * mm});
            skLineSegment(sketch, "E2299", {"start": v(3.7, 25.1) * mm, "end": v(3.67, 25.05) * mm});
            skLineSegment(sketch, "E2300", {"start": v(3.67, 25.05) * mm, "end": v(3.63, 25) * mm});
            skLineSegment(sketch, "E2301", {"start": v(3.63, 25) * mm, "end": v(3.6, 24.94) * mm});
            skLineSegment(sketch, "E2302", {"start": v(3.6, 24.94) * mm, "end": v(3.57, 24.88) * mm});
            skLineSegment(sketch, "E2303", {"start": v(3.57, 24.88) * mm, "end": v(3.54, 24.82) * mm});
            skLineSegment(sketch, "E2304", {"start": v(3.54, 24.82) * mm, "end": v(3.47, 24.68) * mm});
            skLineSegment(sketch, "E2305", {"start": v(3.47, 24.68) * mm, "end": v(3.4, 24.53) * mm});
            skLineSegment(sketch, "E2306", {"start": v(3.4, 24.53) * mm, "end": v(3.33, 24.39) * mm});
            skLineSegment(sketch, "E2307", {"start": v(3.33, 24.39) * mm, "end": v(3.26, 24.24) * mm});
            skLineSegment(sketch, "E2308", {"start": v(3.26, 24.24) * mm, "end": v(3.2, 24.1) * mm});
            skLineSegment(sketch, "E2309", {"start": v(3.2, 24.1) * mm, "end": v(3.13, 23.95) * mm});
            skLineSegment(sketch, "E2310", {"start": v(3.13, 23.95) * mm, "end": v(3.07, 23.8) * mm});
            skLineSegment(sketch, "E2311", {"start": v(3.07, 23.8) * mm, "end": v(3, 23.65) * mm});
            skLineSegment(sketch, "E2312", {"start": v(3, 23.65) * mm, "end": v(2.95, 23.5) * mm});
            skLineSegment(sketch, "E2313", {"start": v(2.95, 23.5) * mm, "end": v(2.9, 23.35) * mm});
            skLineSegment(sketch, "E2314", {"start": v(2.9, 23.35) * mm, "end": v(2.84, 23.2) * mm});
            skLineSegment(sketch, "E2315", {"start": v(2.84, 23.2) * mm, "end": v(2.79, 23.05) * mm});
            skLineSegment(sketch, "E2316", {"start": v(2.79, 23.05) * mm, "end": v(2.74, 22.9) * mm});
            skLineSegment(sketch, "E2317", {"start": v(2.74, 22.9) * mm, "end": v(2.69, 22.75) * mm});
            skLineSegment(sketch, "E2318", {"start": v(2.69, 22.75) * mm, "end": v(2.64, 22.6) * mm});
            skLineSegment(sketch, "E2319", {"start": v(2.64, 22.6) * mm, "end": v(2.6, 22.45) * mm});
            skLineSegment(sketch, "E2320", {"start": v(2.6, 22.45) * mm, "end": v(2.55, 22.3) * mm});
            skLineSegment(sketch, "E2321", {"start": v(2.55, 22.3) * mm, "end": v(2.5, 22.15) * mm});
            skLineSegment(sketch, "E2322", {"start": v(2.5, 22.15) * mm, "end": v(2.46, 22) * mm});
            skLineSegment(sketch, "E2323", {"start": v(2.46, 22) * mm, "end": v(2.42, 21.84) * mm});
            skLineSegment(sketch, "E2324", {"start": v(2.42, 21.84) * mm, "end": v(2.38, 21.69) * mm});
            skLineSegment(sketch, "E2325", {"start": v(2.38, 21.69) * mm, "end": v(2.34, 21.53) * mm});
            skLineSegment(sketch, "E2326", {"start": v(2.34, 21.53) * mm, "end": v(2.3, 21.38) * mm});
            skLineSegment(sketch, "E2327", {"start": v(2.3, 21.38) * mm, "end": v(2.27, 21.22) * mm});
            skLineSegment(sketch, "E2328", {"start": v(2.27, 21.22) * mm, "end": v(2.24, 21.07) * mm});
            skLineSegment(sketch, "E2329", {"start": v(2.24, 21.07) * mm, "end": v(2.2, 20.91) * mm});
            skLineSegment(sketch, "E2330", {"start": v(2.2, 20.91) * mm, "end": v(2.18, 20.76) * mm});
            skLineSegment(sketch, "E2331", {"start": v(2.18, 20.76) * mm, "end": v(2.15, 20.6) * mm});
            skLineSegment(sketch, "E2332", {"start": v(2.15, 20.6) * mm, "end": v(2.12, 20.44) * mm});
            skLineSegment(sketch, "E2333", {"start": v(2.12, 20.44) * mm, "end": v(2.09, 20.28) * mm});
            skLineSegment(sketch, "E2334", {"start": v(2.09, 20.28) * mm, "end": v(2.06, 20.13) * mm});
            skLineSegment(sketch, "E2335", {"start": v(2.06, 20.13) * mm, "end": v(2.04, 19.97) * mm});
            skLineSegment(sketch, "E2336", {"start": v(2.04, 19.97) * mm, "end": v(2.01, 19.8) * mm});
            skLineSegment(sketch, "E2337", {"start": v(2.01, 19.8) * mm, "end": v(2, 19.65) * mm});
            skLineSegment(sketch, "E2338", {"start": v(2, 19.65) * mm, "end": v(1.97, 19.49) * mm});
            skLineSegment(sketch, "E2339", {"start": v(1.97, 19.49) * mm, "end": v(1.95, 19.33) * mm});
            skLineSegment(sketch, "E2340", {"start": v(1.95, 19.33) * mm, "end": v(1.93, 19.17) * mm});
            skLineSegment(sketch, "E2341", {"start": v(1.93, 19.17) * mm, "end": v(1.9, 19) * mm});
            skLineSegment(sketch, "E2342", {"start": v(1.9, 19) * mm, "end": v(1.89, 18.84) * mm});
            skLineSegment(sketch, "E2343", {"start": v(1.89, 18.84) * mm, "end": v(1.87, 18.68) * mm});
            skLineSegment(sketch, "E2344", {"start": v(1.87, 18.68) * mm, "end": v(1.85, 18.52) * mm});
            skLineSegment(sketch, "E2345", {"start": v(1.85, 18.52) * mm, "end": v(1.84, 18.35) * mm});
            skLineSegment(sketch, "E2346", {"start": v(1.84, 18.35) * mm, "end": v(1.82, 18.2) * mm});
            skLineSegment(sketch, "E2347", {"start": v(1.82, 18.2) * mm, "end": v(1.8, 18.03) * mm});
            skLineSegment(sketch, "E2348", {"start": v(1.8, 18.03) * mm, "end": v(1.8, 17.86) * mm});
            skLineSegment(sketch, "E2349", {"start": v(1.8, 17.86) * mm, "end": v(1.78, 17.7) * mm});
            skLineSegment(sketch, "E2350", {"start": v(1.78, 17.7) * mm, "end": v(1.77, 17.53) * mm});
            skLineSegment(sketch, "E2351", {"start": v(1.77, 17.53) * mm, "end": v(1.76, 17.36) * mm});
            skLineSegment(sketch, "E2352", {"start": v(1.76, 17.36) * mm, "end": v(1.74, 17.2) * mm});
            skLineSegment(sketch, "E2353", {"start": v(1.74, 17.2) * mm, "end": v(1.73, 17.03) * mm});
            skLineSegment(sketch, "E2354", {"start": v(1.73, 17.03) * mm, "end": v(1.72, 16.86) * mm});
            skLineSegment(sketch, "E2355", {"start": v(1.72, 16.86) * mm, "end": v(1.71, 16.7) * mm});
            skLineSegment(sketch, "E2356", {"start": v(1.71, 16.7) * mm, "end": v(1.7, 16.52) * mm});
            skLineSegment(sketch, "E2357", {"start": v(1.7, 16.52) * mm, "end": v(1.7, 16.35) * mm});
            skLineSegment(sketch, "E2358", {"start": v(1.7, 16.35) * mm, "end": v(1.69, 16.18) * mm});
            skLineSegment(sketch, "E2359", {"start": v(1.69, 16.18) * mm, "end": v(1.68, 16.01) * mm});
            skLineSegment(sketch, "E2360", {"start": v(1.68, 16.01) * mm, "end": v(1.67, 15.84) * mm});
            skLineSegment(sketch, "E2361", {"start": v(1.67, 15.84) * mm, "end": v(1.66, 15.67) * mm});
            skLineSegment(sketch, "E2362", {"start": v(1.66, 15.67) * mm, "end": v(1.65, 15.5) * mm});
            skLineSegment(sketch, "E2363", {"start": v(1.65, 15.5) * mm, "end": v(1.65, 15.33) * mm});
            skLineSegment(sketch, "E2364", {"start": v(1.65, 15.33) * mm, "end": v(1.64, 15.15) * mm});
            skLineSegment(sketch, "E2365", {"start": v(1.64, 15.15) * mm, "end": v(1.63, 14.98) * mm});
            skLineSegment(sketch, "E2366", {"start": v(1.63, 14.98) * mm, "end": v(1.63, 14.8) * mm});
            skLineSegment(sketch, "E2367", {"start": v(1.63, 14.8) * mm, "end": v(1.62, 14.63) * mm});
            skLineSegment(sketch, "E2368", {"start": v(4.45, -12.06) * mm, "end": v(4.58, -12.02) * mm});
            skLineSegment(sketch, "E2369", {"start": v(4.58, -12.02) * mm, "end": v(4.7, -11.97) * mm});
            skLineSegment(sketch, "E2370", {"start": v(4.7, -11.97) * mm, "end": v(4.83, -11.92) * mm});
            skLineSegment(sketch, "E2371", {"start": v(4.83, -11.92) * mm, "end": v(4.95, -11.86) * mm});
            skLineSegment(sketch, "E2372", {"start": v(4.95, -11.86) * mm, "end": v(5.07, -11.8) * mm});
            skLineSegment(sketch, "E2373", {"start": v(5.07, -11.8) * mm, "end": v(5.18, -11.75) * mm});
            skLineSegment(sketch, "E2374", {"start": v(5.18, -11.75) * mm, "end": v(5.3, -11.7) * mm});
            skLineSegment(sketch, "E2375", {"start": v(5.3, -11.7) * mm, "end": v(5.41, -11.64) * mm});
            skLineSegment(sketch, "E2376", {"start": v(5.41, -11.64) * mm, "end": v(5.52, -11.58) * mm});
            skLineSegment(sketch, "E2377", {"start": v(5.52, -11.58) * mm, "end": v(5.63, -11.52) * mm});
            skLineSegment(sketch, "E2378", {"start": v(5.63, -11.52) * mm, "end": v(5.73, -11.46) * mm});
            skLineSegment(sketch, "E2379", {"start": v(5.73, -11.46) * mm, "end": v(5.83, -11.4) * mm});
            skLineSegment(sketch, "E2380", {"start": v(5.83, -11.4) * mm, "end": v(5.93, -11.33) * mm});
            skLineSegment(sketch, "E2381", {"start": v(5.93, -11.33) * mm, "end": v(6.03, -11.27) * mm});
            skLineSegment(sketch, "E2382", {"start": v(6.03, -11.27) * mm, "end": v(6.13, -11.2) * mm});
            skLineSegment(sketch, "E2383", {"start": v(6.13, -11.2) * mm, "end": v(6.22, -11.13) * mm});
            skLineSegment(sketch, "E2384", {"start": v(6.22, -11.13) * mm, "end": v(6.3, -11.06) * mm});
            skLineSegment(sketch, "E2385", {"start": v(6.3, -11.06) * mm, "end": v(6.4, -11) * mm});
            skLineSegment(sketch, "E2386", {"start": v(6.4, -11) * mm, "end": v(6.48, -10.92) * mm});
            skLineSegment(sketch, "E2387", {"start": v(6.48, -10.92) * mm, "end": v(6.57, -10.85) * mm});
            skLineSegment(sketch, "E2388", {"start": v(6.57, -10.85) * mm, "end": v(6.65, -10.77) * mm});
            skLineSegment(sketch, "E2389", {"start": v(6.65, -10.77) * mm, "end": v(6.73, -10.7) * mm});
            skLineSegment(sketch, "E2390", {"start": v(6.73, -10.7) * mm, "end": v(6.8, -10.62) * mm});
            skLineSegment(sketch, "E2391", {"start": v(6.8, -10.62) * mm, "end": v(6.87, -10.54) * mm});
            skLineSegment(sketch, "E2392", {"start": v(6.87, -10.54) * mm, "end": v(6.95, -10.46) * mm});
            skLineSegment(sketch, "E2393", {"start": v(6.95, -10.46) * mm, "end": v(7.01, -10.38) * mm});
            skLineSegment(sketch, "E2394", {"start": v(7.01, -10.38) * mm, "end": v(7.08, -10.3) * mm});
            skLineSegment(sketch, "E2395", {"start": v(7.08, -10.3) * mm, "end": v(7.15, -10.21) * mm});
            skLineSegment(sketch, "E2396", {"start": v(7.15, -10.21) * mm, "end": v(7.2, -10.13) * mm});
            skLineSegment(sketch, "E2397", {"start": v(7.2, -10.13) * mm, "end": v(7.27, -10.04) * mm});
            skLineSegment(sketch, "E2398", {"start": v(7.27, -10.04) * mm, "end": v(7.32, -9.95) * mm});
            skLineSegment(sketch, "E2399", {"start": v(7.32, -9.95) * mm, "end": v(7.38, -9.87) * mm});
            skLineSegment(sketch, "E2400", {"start": v(7.38, -9.87) * mm, "end": v(7.43, -9.78) * mm});
            skLineSegment(sketch, "E2401", {"start": v(7.43, -9.78) * mm, "end": v(7.48, -9.68) * mm});
            skLineSegment(sketch, "E2402", {"start": v(7.48, -9.68) * mm, "end": v(7.53, -9.6) * mm});
            skLineSegment(sketch, "E2403", {"start": v(7.53, -9.6) * mm, "end": v(7.57, -9.5) * mm});
            skLineSegment(sketch, "E2404", {"start": v(7.57, -9.5) * mm, "end": v(7.62, -9.4) * mm});
            skLineSegment(sketch, "E2405", {"start": v(7.62, -9.4) * mm, "end": v(7.66, -9.3) * mm});
            skLineSegment(sketch, "E2406", {"start": v(7.66, -9.3) * mm, "end": v(7.7, -9.21) * mm});
            skLineSegment(sketch, "E2407", {"start": v(7.7, -9.21) * mm, "end": v(7.73, -9.11) * mm});
            skLineSegment(sketch, "E2408", {"start": v(7.73, -9.11) * mm, "end": v(7.76, -9.01) * mm});
            skLineSegment(sketch, "E2409", {"start": v(7.76, -9.01) * mm, "end": v(7.8, -8.91) * mm});
            skLineSegment(sketch, "E2410", {"start": v(7.8, -8.91) * mm, "end": v(7.82, -8.8) * mm});
            skLineSegment(sketch, "E2411", {"start": v(7.82, -8.8) * mm, "end": v(7.85, -8.7) * mm});
            skLineSegment(sketch, "E2412", {"start": v(7.85, -8.7) * mm, "end": v(7.87, -8.6) * mm});
            skLineSegment(sketch, "E2413", {"start": v(7.87, -8.6) * mm, "end": v(7.9, -8.5) * mm});
            skLineSegment(sketch, "E2414", {"start": v(7.9, -8.5) * mm, "end": v(7.91, -8.39) * mm});
            skLineSegment(sketch, "E2415", {"start": v(7.91, -8.39) * mm, "end": v(7.93, -8.28) * mm});
            skLineSegment(sketch, "E2416", {"start": v(7.93, -8.28) * mm, "end": v(7.94, -8.17) * mm});
            skLineSegment(sketch, "E2417", {"start": v(7.94, -8.17) * mm, "end": v(7.96, -8.06) * mm});
            skLineSegment(sketch, "E2418", {"start": v(7.96, -8.06) * mm, "end": v(7.97, -7.95) * mm});
            skLineSegment(sketch, "E2419", {"start": v(7.97, -7.95) * mm, "end": v(7.97, -7.84) * mm});
            skLineSegment(sketch, "E2420", {"start": v(7.97, -7.84) * mm, "end": v(7.98, -7.72) * mm});
            skLineSegment(sketch, "E2421", {"start": v(7.98, -7.72) * mm, "end": v(7.98, -7.6) * mm});
            skLineSegment(sketch, "E2422", {"start": v(7.98, -7.6) * mm, "end": v(7.98, -7.5) * mm});
            skLineSegment(sketch, "E2423", {"start": v(7.98, -7.5) * mm, "end": v(7.98, -7.37) * mm});
            skLineSegment(sketch, "E2424", {"start": v(7.98, -7.37) * mm, "end": v(7.98, -7.26) * mm});
            skLineSegment(sketch, "E2425", {"start": v(7.98, -7.26) * mm, "end": v(7.97, -7.14) * mm});
            skLineSegment(sketch, "E2426", {"start": v(7.97, -7.14) * mm, "end": v(7.96, -7.01) * mm});
            skLineSegment(sketch, "E2427", {"start": v(7.96, -7.01) * mm, "end": v(7.95, -6.9) * mm});
            skLineSegment(sketch, "E2428", {"start": v(7.95, -6.9) * mm, "end": v(7.93, -6.77) * mm});
            skLineSegment(sketch, "E2429", {"start": v(7.93, -6.77) * mm, "end": v(7.92, -6.65) * mm});
            skLineSegment(sketch, "E2430", {"start": v(7.92, -6.65) * mm, "end": v(7.9, -6.52) * mm});
            skLineSegment(sketch, "E2431", {"start": v(7.9, -6.52) * mm, "end": v(7.88, -6.4) * mm});
            skLineSegment(sketch, "E2432", {"start": v(7.88, -6.4) * mm, "end": v(7.86, -6.27) * mm});
            skLineSegment(sketch, "E2433", {"start": v(7.86, -6.27) * mm, "end": v(7.83, -6.15) * mm});
            skLineSegment(sketch, "E2434", {"start": v(7.83, -6.15) * mm, "end": v(7.8, -6.04) * mm});
            skLineSegment(sketch, "E2435", {"start": v(7.8, -6.04) * mm, "end": v(7.78, -5.92) * mm});
            skLineSegment(sketch, "E2436", {"start": v(7.78, -5.92) * mm, "end": v(7.75, -5.8) * mm});
            skLineSegment(sketch, "E2437", {"start": v(7.75, -5.8) * mm, "end": v(7.72, -5.7) * mm});
            skLineSegment(sketch, "E2438", {"start": v(7.72, -5.7) * mm, "end": v(7.7, -5.58) * mm});
            skLineSegment(sketch, "E2439", {"start": v(7.7, -5.58) * mm, "end": v(7.66, -5.47) * mm});
            skLineSegment(sketch, "E2440", {"start": v(7.66, -5.47) * mm, "end": v(7.62, -5.37) * mm});
            skLineSegment(sketch, "E2441", {"start": v(7.62, -5.37) * mm, "end": v(7.58, -5.26) * mm});
            skLineSegment(sketch, "E2442", {"start": v(7.58, -5.26) * mm, "end": v(7.55, -5.16) * mm});
            skLineSegment(sketch, "E2443", {"start": v(7.55, -5.16) * mm, "end": v(7.5, -5.05) * mm});
            skLineSegment(sketch, "E2444", {"start": v(7.5, -5.05) * mm, "end": v(7.46, -4.95) * mm});
            skLineSegment(sketch, "E2445", {"start": v(7.46, -4.95) * mm, "end": v(7.42, -4.85) * mm});
            skLineSegment(sketch, "E2446", {"start": v(7.42, -4.85) * mm, "end": v(7.38, -4.76) * mm});
            skLineSegment(sketch, "E2447", {"start": v(7.38, -4.76) * mm, "end": v(7.33, -4.66) * mm});
            skLineSegment(sketch, "E2448", {"start": v(7.33, -4.66) * mm, "end": v(7.28, -4.57) * mm});
            skLineSegment(sketch, "E2449", {"start": v(7.28, -4.57) * mm, "end": v(7.23, -4.48) * mm});
            skLineSegment(sketch, "E2450", {"start": v(7.23, -4.48) * mm, "end": v(7.18, -4.39) * mm});
            skLineSegment(sketch, "E2451", {"start": v(7.18, -4.39) * mm, "end": v(7.13, -4.3) * mm});
            skLineSegment(sketch, "E2452", {"start": v(7.13, -4.3) * mm, "end": v(7.07, -4.21) * mm});
            skLineSegment(sketch, "E2453", {"start": v(7.07, -4.21) * mm, "end": v(7.01, -4.13) * mm});
            skLineSegment(sketch, "E2454", {"start": v(7.01, -4.13) * mm, "end": v(6.96, -4.05) * mm});
            skLineSegment(sketch, "E2455", {"start": v(6.96, -4.05) * mm, "end": v(6.9, -3.97) * mm});
            skLineSegment(sketch, "E2456", {"start": v(6.9, -3.97) * mm, "end": v(6.84, -3.89) * mm});
            skLineSegment(sketch, "E2457", {"start": v(6.84, -3.89) * mm, "end": v(6.77, -3.81) * mm});
            skLineSegment(sketch, "E2458", {"start": v(6.77, -3.81) * mm, "end": v(6.7, -3.74) * mm});
            skLineSegment(sketch, "E2459", {"start": v(6.7, -3.74) * mm, "end": v(6.64, -3.66) * mm});
            skLineSegment(sketch, "E2460", {"start": v(6.64, -3.66) * mm, "end": v(6.58, -3.6) * mm});
            skLineSegment(sketch, "E2461", {"start": v(6.58, -3.6) * mm, "end": v(6.5, -3.52) * mm});
            skLineSegment(sketch, "E2462", {"start": v(6.5, -3.52) * mm, "end": v(6.44, -3.45) * mm});
            skLineSegment(sketch, "E2463", {"start": v(6.44, -3.45) * mm, "end": v(6.37, -3.39) * mm});
            skLineSegment(sketch, "E2464", {"start": v(6.37, -3.39) * mm, "end": v(6.3, -3.32) * mm});
            skLineSegment(sketch, "E2465", {"start": v(6.3, -3.32) * mm, "end": v(6.22, -3.26) * mm});
            skLineSegment(sketch, "E2466", {"start": v(6.22, -3.26) * mm, "end": v(6.14, -3.2) * mm});
            skLineSegment(sketch, "E2467", {"start": v(6.14, -3.2) * mm, "end": v(6.06, -3.15) * mm});
            skLineSegment(sketch, "E2468", {"start": v(6.06, -3.15) * mm, "end": v(5.98, -3.09) * mm});
            skLineSegment(sketch, "E2469", {"start": v(5.98, -3.09) * mm, "end": v(5.9, -3.04) * mm});
            skLineSegment(sketch, "E2470", {"start": v(5.9, -3.04) * mm, "end": v(5.82, -2.98) * mm});
            skLineSegment(sketch, "E2471", {"start": v(5.82, -2.98) * mm, "end": v(5.74, -2.93) * mm});
            skLineSegment(sketch, "E2472", {"start": v(5.74, -2.93) * mm, "end": v(5.65, -2.89) * mm});
            skLineSegment(sketch, "E2473", {"start": v(5.65, -2.89) * mm, "end": v(5.57, -2.84) * mm});
            skLineSegment(sketch, "E2474", {"start": v(5.57, -2.84) * mm, "end": v(5.48, -2.8) * mm});
            skLineSegment(sketch, "E2475", {"start": v(5.48, -2.8) * mm, "end": v(5.39, -2.75) * mm});
            skLineSegment(sketch, "E2476", {"start": v(5.39, -2.75) * mm, "end": v(5.3, -2.71) * mm});
            skLineSegment(sketch, "E2477", {"start": v(5.3, -2.71) * mm, "end": v(5.2, -2.68) * mm});
            skLineSegment(sketch, "E2478", {"start": v(5.2, -2.68) * mm, "end": v(5.11, -2.64) * mm});
            skLineSegment(sketch, "E2479", {"start": v(5.11, -2.64) * mm, "end": v(5.01, -2.6) * mm});
            skLineSegment(sketch, "E2480", {"start": v(5.01, -2.6) * mm, "end": v(4.92, -2.57) * mm});
            skLineSegment(sketch, "E2481", {"start": v(4.92, -2.57) * mm, "end": v(4.82, -2.54) * mm});
            skLineSegment(sketch, "E2482", {"start": v(4.82, -2.54) * mm, "end": v(4.72, -2.52) * mm});
            skLineSegment(sketch, "E2483", {"start": v(4.72, -2.52) * mm, "end": v(4.62, -2.5) * mm});
            skLineSegment(sketch, "E2484", {"start": v(4.62, -2.5) * mm, "end": v(4.52, -2.47) * mm});
            skLineSegment(sketch, "E2485", {"start": v(4.52, -2.47) * mm, "end": v(4.41, -2.45) * mm});
            skLineSegment(sketch, "E2486", {"start": v(4.41, -2.45) * mm, "end": v(4.3, -2.43) * mm});
            skLineSegment(sketch, "E2487", {"start": v(4.3, -2.43) * mm, "end": v(4.2, -2.41) * mm});
            skLineSegment(sketch, "E2488", {"start": v(4.2, -2.41) * mm, "end": v(4.1, -2.4) * mm});
            skLineSegment(sketch, "E2489", {"start": v(4.1, -2.4) * mm, "end": v(3.98, -2.38) * mm});
            skLineSegment(sketch, "E2490", {"start": v(3.98, -2.38) * mm, "end": v(3.87, -2.37) * mm});
            skLineSegment(sketch, "E2491", {"start": v(3.87, -2.37) * mm, "end": v(3.76, -2.36) * mm});
            skLineSegment(sketch, "E2492", {"start": v(3.76, -2.36) * mm, "end": v(3.65, -2.36) * mm});
            skLineSegment(sketch, "E2493", {"start": v(3.65, -2.36) * mm, "end": v(3.53, -2.35) * mm});
            skLineSegment(sketch, "E2494", {"start": v(3.53, -2.35) * mm, "end": v(3.41, -2.35) * mm});
            skLineSegment(sketch, "E2495", {"start": v(3.41, -2.35) * mm, "end": v(3.3, -2.35) * mm});
            skLineSegment(sketch, "E2496", {"start": v(3.3, -2.35) * mm, "end": v(3.31, -2.5) * mm});
            skLineSegment(sketch, "E2497", {"start": v(3.31, -2.5) * mm, "end": v(3.33, -2.65) * mm});
            skLineSegment(sketch, "E2498", {"start": v(3.33, -2.65) * mm, "end": v(3.35, -2.8) * mm});
            skLineSegment(sketch, "E2499", {"start": v(3.35, -2.8) * mm, "end": v(3.37, -2.95) * mm});
            skLineSegment(sketch, "E2500", {"start": v(3.37, -2.95) * mm, "end": v(3.39, -3.1) * mm});
            skLineSegment(sketch, "E2501", {"start": v(3.39, -3.1) * mm, "end": v(3.4, -3.25) * mm});
            skLineSegment(sketch, "E2502", {"start": v(3.4, -3.25) * mm, "end": v(3.42, -3.4) * mm});
            skLineSegment(sketch, "E2503", {"start": v(3.42, -3.4) * mm, "end": v(3.44, -3.55) * mm});
            skLineSegment(sketch, "E2504", {"start": v(3.44, -3.55) * mm, "end": v(3.46, -3.7) * mm});
            skLineSegment(sketch, "E2505", {"start": v(3.46, -3.7) * mm, "end": v(3.47, -3.85) * mm});
            skLineSegment(sketch, "E2506", {"start": v(3.47, -3.85) * mm, "end": v(3.5, -4) * mm});
            skLineSegment(sketch, "E2507", {"start": v(3.5, -4) * mm, "end": v(3.51, -4.15) * mm});
            skLineSegment(sketch, "E2508", {"start": v(3.51, -4.15) * mm, "end": v(3.53, -4.3) * mm});
            skLineSegment(sketch, "E2509", {"start": v(3.53, -4.3) * mm, "end": v(3.55, -4.45) * mm});
            skLineSegment(sketch, "E2510", {"start": v(3.55, -4.45) * mm, "end": v(3.56, -4.6) * mm});
            skLineSegment(sketch, "E2511", {"start": v(3.56, -4.6) * mm, "end": v(3.58, -4.75) * mm});
            skLineSegment(sketch, "E2512", {"start": v(3.58, -4.75) * mm, "end": v(3.6, -4.9) * mm});
            skLineSegment(sketch, "E2513", {"start": v(3.6, -4.9) * mm, "end": v(3.62, -5.05) * mm});
            skLineSegment(sketch, "E2514", {"start": v(3.62, -5.05) * mm, "end": v(3.63, -5.2) * mm});
            skLineSegment(sketch, "E2515", {"start": v(3.63, -5.2) * mm, "end": v(3.65, -5.35) * mm});
            skLineSegment(sketch, "E2516", {"start": v(3.65, -5.35) * mm, "end": v(3.67, -5.5) * mm});
            skLineSegment(sketch, "E2517", {"start": v(3.67, -5.5) * mm, "end": v(3.69, -5.65) * mm});
            skLineSegment(sketch, "E2518", {"start": v(3.69, -5.65) * mm, "end": v(3.7, -5.8) * mm});
            skLineSegment(sketch, "E2519", {"start": v(3.7, -5.8) * mm, "end": v(3.72, -5.95) * mm});
            skLineSegment(sketch, "E2520", {"start": v(3.72, -5.95) * mm, "end": v(3.74, -6.1) * mm});
            skLineSegment(sketch, "E2521", {"start": v(3.74, -6.1) * mm, "end": v(3.76, -6.26) * mm});
            skLineSegment(sketch, "E2522", {"start": v(3.76, -6.26) * mm, "end": v(3.78, -6.4) * mm});
            skLineSegment(sketch, "E2523", {"start": v(3.78, -6.4) * mm, "end": v(3.8, -6.56) * mm});
            skLineSegment(sketch, "E2524", {"start": v(3.8, -6.56) * mm, "end": v(3.81, -6.7) * mm});
            skLineSegment(sketch, "E2525", {"start": v(3.81, -6.7) * mm, "end": v(3.83, -6.86) * mm});
            skLineSegment(sketch, "E2526", {"start": v(3.83, -6.86) * mm, "end": v(3.85, -7) * mm});
            skLineSegment(sketch, "E2527", {"start": v(3.85, -7) * mm, "end": v(3.87, -7.16) * mm});
            skLineSegment(sketch, "E2528", {"start": v(3.87, -7.16) * mm, "end": v(3.89, -7.31) * mm});
            skLineSegment(sketch, "E2529", {"start": v(3.89, -7.31) * mm, "end": v(3.9, -7.46) * mm});
            skLineSegment(sketch, "E2530", {"start": v(3.9, -7.46) * mm, "end": v(3.92, -7.61) * mm});
            skLineSegment(sketch, "E2531", {"start": v(3.92, -7.61) * mm, "end": v(3.94, -7.77) * mm});
            skLineSegment(sketch, "E2532", {"start": v(3.94, -7.77) * mm, "end": v(3.96, -7.92) * mm});
            skLineSegment(sketch, "E2533", {"start": v(3.96, -7.92) * mm, "end": v(3.98, -8.07) * mm});
            skLineSegment(sketch, "E2534", {"start": v(3.98, -8.07) * mm, "end": v(4, -8.22) * mm});
            skLineSegment(sketch, "E2535", {"start": v(4, -8.22) * mm, "end": v(4.01, -8.37) * mm});
            skLineSegment(sketch, "E2536", {"start": v(4.01, -8.37) * mm, "end": v(4.03, -8.53) * mm});
            skLineSegment(sketch, "E2537", {"start": v(4.03, -8.53) * mm, "end": v(4.05, -8.68) * mm});
            skLineSegment(sketch, "E2538", {"start": v(4.05, -8.68) * mm, "end": v(4.07, -8.83) * mm});
            skLineSegment(sketch, "E2539", {"start": v(4.07, -8.83) * mm, "end": v(4.08, -8.98) * mm});
            skLineSegment(sketch, "E2540", {"start": v(4.08, -8.98) * mm, "end": v(4.1, -9.13) * mm});
            skLineSegment(sketch, "E2541", {"start": v(4.1, -9.13) * mm, "end": v(4.12, -9.29) * mm});
            skLineSegment(sketch, "E2542", {"start": v(4.12, -9.29) * mm, "end": v(4.14, -9.44) * mm});
            skLineSegment(sketch, "E2543", {"start": v(4.14, -9.44) * mm, "end": v(4.16, -9.6) * mm});
            skLineSegment(sketch, "E2544", {"start": v(4.16, -9.6) * mm, "end": v(4.17, -9.75) * mm});
            skLineSegment(sketch, "E2545", {"start": v(4.17, -9.75) * mm, "end": v(4.2, -9.9) * mm});
            skLineSegment(sketch, "E2546", {"start": v(4.2, -9.9) * mm, "end": v(4.21, -10.05) * mm});
            skLineSegment(sketch, "E2547", {"start": v(4.21, -10.05) * mm, "end": v(4.23, -10.2) * mm});
            skLineSegment(sketch, "E2548", {"start": v(4.23, -10.2) * mm, "end": v(4.25, -10.36) * mm});
            skLineSegment(sketch, "E2549", {"start": v(4.25, -10.36) * mm, "end": v(4.27, -10.51) * mm});
            skLineSegment(sketch, "E2550", {"start": v(4.27, -10.51) * mm, "end": v(4.28, -10.67) * mm});
            skLineSegment(sketch, "E2551", {"start": v(4.28, -10.67) * mm, "end": v(4.3, -10.82) * mm});
            skLineSegment(sketch, "E2552", {"start": v(4.3, -10.82) * mm, "end": v(4.32, -10.98) * mm});
            skLineSegment(sketch, "E2553", {"start": v(4.32, -10.98) * mm, "end": v(4.34, -11.13) * mm});
            skLineSegment(sketch, "E2554", {"start": v(4.34, -11.13) * mm, "end": v(4.36, -11.29) * mm});
            skLineSegment(sketch, "E2555", {"start": v(4.36, -11.29) * mm, "end": v(4.38, -11.44) * mm});
            skLineSegment(sketch, "E2556", {"start": v(4.38, -11.44) * mm, "end": v(4.4, -11.6) * mm});
            skLineSegment(sketch, "E2557", {"start": v(4.4, -11.6) * mm, "end": v(4.41, -11.75) * mm});
            skLineSegment(sketch, "E2558", {"start": v(4.41, -11.75) * mm, "end": v(4.43, -11.9) * mm});
            skLineSegment(sketch, "E2559", {"start": v(4.43, -11.9) * mm, "end": v(4.45, -12.06) * mm});
            skSolve(sketch);
        }
        {
            var Q0;
            Q0=makeQuery(id+"F0.imprint","IMPRINT",FACE,{"disambiguationData":[TD([[makeQuery(id+"F0.imprint","IMPRINT",EDGE,{"derivedFrom":sQuery(id+"F0.wireOp",EDGE,"E0")}),-1.0]])]});
            extrude(context, id + "F1", {"entities" : qUnion([Q0]), "depth" : 4.2 * mm});
        }
        {
            var Q0;
            Q0=makeQuery(id+"F1.opExtrude","CAP_FACE",FACE,{"disambiguationData":[OSD([sQuery(id+"F0.wireOp",EDGE,"E0"),sQuery(id+"F0.wireOp",EDGE,"E1"),sQuery(id+"F0.wireOp",EDGE,"E2"),sQuery(id+"F0.wireOp",EDGE,"E3"),sQuery(id+"F0.wireOp",EDGE,"E4"),sQuery(id+"F0.wireOp",EDGE,"E5"),sQuery(id+"F0.wireOp",EDGE,"E6"),sQuery(id+"F0.wireOp",EDGE,"E7"),sQuery(id+"F0.wireOp",EDGE,"E8"),sQuery(id+"F0.wireOp",EDGE,"E9"),sQuery(id+"F0.wireOp",EDGE,"E10"),sQuery(id+"F0.wireOp",EDGE,"E11"),sQuery(id+"F0.wireOp",EDGE,"E12"),sQuery(id+"F0.wireOp",EDGE,"E13"),sQuery(id+"F0.wireOp",EDGE,"E14"),sQuery(id+"F0.wireOp",EDGE,"E15"),sQuery(id+"F0.wireOp",EDGE,"E16"),sQuery(id+"F0.wireOp",EDGE,"E17"),sQuery(id+"F0.wireOp",EDGE,"E18"),sQuery(id+"F0.wireOp",EDGE,"E19"),sQuery(id+"F0.wireOp",EDGE,"E20"),sQuery(id+"F0.wireOp",EDGE,"E21"),sQuery(id+"F0.wireOp",EDGE,"E22"),sQuery(id+"F0.wireOp",EDGE,"E23"),sQuery(id+"F0.wireOp",EDGE,"E24"),sQuery(id+"F0.wireOp",EDGE,"E25"),sQuery(id+"F0.wireOp",EDGE,"E26"),sQuery(id+"F0.wireOp",EDGE,"E27"),sQuery(id+"F0.wireOp",EDGE,"E28"),sQuery(id+"F0.wireOp",EDGE,"E29"),sQuery(id+"F0.wireOp",EDGE,"E30"),sQuery(id+"F0.wireOp",EDGE,"E31"),sQuery(id+"F0.wireOp",EDGE,"E32"),sQuery(id+"F0.wireOp",EDGE,"E33"),sQuery(id+"F0.wireOp",EDGE,"E34"),sQuery(id+"F0.wireOp",EDGE,"E35"),sQuery(id+"F0.wireOp",EDGE,"E36"),sQuery(id+"F0.wireOp",EDGE,"E37"),sQuery(id+"F0.wireOp",EDGE,"E38"),sQuery(id+"F0.wireOp",EDGE,"E39"),sQuery(id+"F0.wireOp",EDGE,"E40"),sQuery(id+"F0.wireOp",EDGE,"E41"),sQuery(id+"F0.wireOp",EDGE,"E42"),sQuery(id+"F0.wireOp",EDGE,"E43"),sQuery(id+"F0.wireOp",EDGE,"E44"),sQuery(id+"F0.wireOp",EDGE,"E45"),sQuery(id+"F0.wireOp",EDGE,"E46"),sQuery(id+"F0.wireOp",EDGE,"E47"),sQuery(id+"F0.wireOp",EDGE,"E48"),sQuery(id+"F0.wireOp",EDGE,"E49"),sQuery(id+"F0.wireOp",EDGE,"E50"),sQuery(id+"F0.wireOp",EDGE,"E51"),sQuery(id+"F0.wireOp",EDGE,"E52"),sQuery(id+"F0.wireOp",EDGE,"E53"),sQuery(id+"F0.wireOp",EDGE,"E54"),sQuery(id+"F0.wireOp",EDGE,"E55"),sQuery(id+"F0.wireOp",EDGE,"E56"),sQuery(id+"F0.wireOp",EDGE,"E57"),sQuery(id+"F0.wireOp",EDGE,"E58"),sQuery(id+"F0.wireOp",EDGE,"E59"),sQuery(id+"F0.wireOp",EDGE,"E60"),sQuery(id+"F0.wireOp",EDGE,"E61"),sQuery(id+"F0.wireOp",EDGE,"E62"),sQuery(id+"F0.wireOp",EDGE,"E63"),sQuery(id+"F0.wireOp",EDGE,"E64"),sQuery(id+"F0.wireOp",EDGE,"E65"),sQuery(id+"F0.wireOp",EDGE,"E66"),sQuery(id+"F0.wireOp",EDGE,"E67"),sQuery(id+"F0.wireOp",EDGE,"E68"),sQuery(id+"F0.wireOp",EDGE,"E69"),sQuery(id+"F0.wireOp",EDGE,"E70"),sQuery(id+"F0.wireOp",EDGE,"E71"),sQuery(id+"F0.wireOp",EDGE,"E72"),sQuery(id+"F0.wireOp",EDGE,"E73"),sQuery(id+"F0.wireOp",EDGE,"E74"),sQuery(id+"F0.wireOp",EDGE,"E75"),sQuery(id+"F0.wireOp",EDGE,"E76"),sQuery(id+"F0.wireOp",EDGE,"E77"),sQuery(id+"F0.wireOp",EDGE,"E78"),sQuery(id+"F0.wireOp",EDGE,"E79"),sQuery(id+"F0.wireOp",EDGE,"E80"),sQuery(id+"F0.wireOp",EDGE,"E81"),sQuery(id+"F0.wireOp",EDGE,"E82"),sQuery(id+"F0.wireOp",EDGE,"E83"),sQuery(id+"F0.wireOp",EDGE,"E84"),sQuery(id+"F0.wireOp",EDGE,"E85"),sQuery(id+"F0.wireOp",EDGE,"E86"),sQuery(id+"F0.wireOp",EDGE,"E87"),sQuery(id+"F0.wireOp",EDGE,"E88"),sQuery(id+"F0.wireOp",EDGE,"E89"),sQuery(id+"F0.wireOp",EDGE,"E90"),sQuery(id+"F0.wireOp",EDGE,"E91"),sQuery(id+"F0.wireOp",EDGE,"E92"),sQuery(id+"F0.wireOp",EDGE,"E93"),sQuery(id+"F0.wireOp",EDGE,"E94"),sQuery(id+"F0.wireOp",EDGE,"E95"),sQuery(id+"F0.wireOp",EDGE,"E96"),sQuery(id+"F0.wireOp",EDGE,"E97"),sQuery(id+"F0.wireOp",EDGE,"E98"),sQuery(id+"F0.wireOp",EDGE,"E99"),sQuery(id+"F0.wireOp",EDGE,"E100"),sQuery(id+"F0.wireOp",EDGE,"E101"),sQuery(id+"F0.wireOp",EDGE,"E102"),sQuery(id+"F0.wireOp",EDGE,"E103"),sQuery(id+"F0.wireOp",EDGE,"E104"),sQuery(id+"F0.wireOp",EDGE,"E105"),sQuery(id+"F0.wireOp",EDGE,"E106"),sQuery(id+"F0.wireOp",EDGE,"E107"),sQuery(id+"F0.wireOp",EDGE,"E108"),sQuery(id+"F0.wireOp",EDGE,"E109"),sQuery(id+"F0.wireOp",EDGE,"E110"),sQuery(id+"F0.wireOp",EDGE,"E111"),sQuery(id+"F0.wireOp",EDGE,"E112"),sQuery(id+"F0.wireOp",EDGE,"E113"),sQuery(id+"F0.wireOp",EDGE,"E114"),sQuery(id+"F0.wireOp",EDGE,"E115"),sQuery(id+"F0.wireOp",EDGE,"E116"),sQuery(id+"F0.wireOp",EDGE,"E117"),sQuery(id+"F0.wireOp",EDGE,"E118"),sQuery(id+"F0.wireOp",EDGE,"E119"),sQuery(id+"F0.wireOp",EDGE,"E120"),sQuery(id+"F0.wireOp",EDGE,"E121"),sQuery(id+"F0.wireOp",EDGE,"E122"),sQuery(id+"F0.wireOp",EDGE,"E123"),sQuery(id+"F0.wireOp",EDGE,"E124"),sQuery(id+"F0.wireOp",EDGE,"E125"),sQuery(id+"F0.wireOp",EDGE,"E126"),sQuery(id+"F0.wireOp",EDGE,"E127"),sQuery(id+"F0.wireOp",EDGE,"E128"),sQuery(id+"F0.wireOp",EDGE,"E129"),sQuery(id+"F0.wireOp",EDGE,"E130"),sQuery(id+"F0.wireOp",EDGE,"E131"),sQuery(id+"F0.wireOp",EDGE,"E132"),sQuery(id+"F0.wireOp",EDGE,"E133"),sQuery(id+"F0.wireOp",EDGE,"E134"),sQuery(id+"F0.wireOp",EDGE,"E135"),sQuery(id+"F0.wireOp",EDGE,"E136"),sQuery(id+"F0.wireOp",EDGE,"E137"),sQuery(id+"F0.wireOp",EDGE,"E138"),sQuery(id+"F0.wireOp",EDGE,"E139"),sQuery(id+"F0.wireOp",EDGE,"E140"),sQuery(id+"F0.wireOp",EDGE,"E141"),sQuery(id+"F0.wireOp",EDGE,"E142"),sQuery(id+"F0.wireOp",EDGE,"E143"),sQuery(id+"F0.wireOp",EDGE,"E144"),sQuery(id+"F0.wireOp",EDGE,"E145"),sQuery(id+"F0.wireOp",EDGE,"E146"),sQuery(id+"F0.wireOp",EDGE,"E147"),sQuery(id+"F0.wireOp",EDGE,"E148"),sQuery(id+"F0.wireOp",EDGE,"E149"),sQuery(id+"F0.wireOp",EDGE,"E150"),sQuery(id+"F0.wireOp",EDGE,"E151"),sQuery(id+"F0.wireOp",EDGE,"E152"),sQuery(id+"F0.wireOp",EDGE,"E153"),sQuery(id+"F0.wireOp",EDGE,"E154"),sQuery(id+"F0.wireOp",EDGE,"E155"),sQuery(id+"F0.wireOp",EDGE,"E156"),sQuery(id+"F0.wireOp",EDGE,"E157"),sQuery(id+"F0.wireOp",EDGE,"E158"),sQuery(id+"F0.wireOp",EDGE,"E159"),sQuery(id+"F0.wireOp",EDGE,"E160"),sQuery(id+"F0.wireOp",EDGE,"E161"),sQuery(id+"F0.wireOp",EDGE,"E162"),sQuery(id+"F0.wireOp",EDGE,"E163"),sQuery(id+"F0.wireOp",EDGE,"E164"),sQuery(id+"F0.wireOp",EDGE,"E165"),sQuery(id+"F0.wireOp",EDGE,"E166"),sQuery(id+"F0.wireOp",EDGE,"E167"),sQuery(id+"F0.wireOp",EDGE,"E168"),sQuery(id+"F0.wireOp",EDGE,"E169"),sQuery(id+"F0.wireOp",EDGE,"E170"),sQuery(id+"F0.wireOp",EDGE,"E171"),sQuery(id+"F0.wireOp",EDGE,"E172"),sQuery(id+"F0.wireOp",EDGE,"E173"),sQuery(id+"F0.wireOp",EDGE,"E174"),sQuery(id+"F0.wireOp",EDGE,"E175"),sQuery(id+"F0.wireOp",EDGE,"E176"),sQuery(id+"F0.wireOp",EDGE,"E177"),sQuery(id+"F0.wireOp",EDGE,"E178"),sQuery(id+"F0.wireOp",EDGE,"E179"),sQuery(id+"F0.wireOp",EDGE,"E180"),sQuery(id+"F0.wireOp",EDGE,"E181"),sQuery(id+"F0.wireOp",EDGE,"E182"),sQuery(id+"F0.wireOp",EDGE,"E183"),sQuery(id+"F0.wireOp",EDGE,"E184"),sQuery(id+"F0.wireOp",EDGE,"E185"),sQuery(id+"F0.wireOp",EDGE,"E186"),sQuery(id+"F0.wireOp",EDGE,"E187"),sQuery(id+"F0.wireOp",EDGE,"E188"),sQuery(id+"F0.wireOp",EDGE,"E189"),sQuery(id+"F0.wireOp",EDGE,"E190"),sQuery(id+"F0.wireOp",EDGE,"E191"),sQuery(id+"F0.wireOp",EDGE,"E192"),sQuery(id+"F0.wireOp",EDGE,"E193"),sQuery(id+"F0.wireOp",EDGE,"E194"),sQuery(id+"F0.wireOp",EDGE,"E195"),sQuery(id+"F0.wireOp",EDGE,"E196"),sQuery(id+"F0.wireOp",EDGE,"E197"),sQuery(id+"F0.wireOp",EDGE,"E198"),sQuery(id+"F0.wireOp",EDGE,"E199"),sQuery(id+"F0.wireOp",EDGE,"E200"),sQuery(id+"F0.wireOp",EDGE,"E201"),sQuery(id+"F0.wireOp",EDGE,"E202"),sQuery(id+"F0.wireOp",EDGE,"E203"),sQuery(id+"F0.wireOp",EDGE,"E204"),sQuery(id+"F0.wireOp",EDGE,"E205"),sQuery(id+"F0.wireOp",EDGE,"E206"),sQuery(id+"F0.wireOp",EDGE,"E207"),sQuery(id+"F0.wireOp",EDGE,"E208"),sQuery(id+"F0.wireOp",EDGE,"E209"),sQuery(id+"F0.wireOp",EDGE,"E210"),sQuery(id+"F0.wireOp",EDGE,"E211"),sQuery(id+"F0.wireOp",EDGE,"E212"),sQuery(id+"F0.wireOp",EDGE,"E213"),sQuery(id+"F0.wireOp",EDGE,"E214"),sQuery(id+"F0.wireOp",EDGE,"E215"),sQuery(id+"F0.wireOp",EDGE,"E216"),sQuery(id+"F0.wireOp",EDGE,"E217"),sQuery(id+"F0.wireOp",EDGE,"E218"),sQuery(id+"F0.wireOp",EDGE,"E219"),sQuery(id+"F0.wireOp",EDGE,"E220"),sQuery(id+"F0.wireOp",EDGE,"E221"),sQuery(id+"F0.wireOp",EDGE,"E222"),sQuery(id+"F0.wireOp",EDGE,"E223"),sQuery(id+"F0.wireOp",EDGE,"E224"),sQuery(id+"F0.wireOp",EDGE,"E225"),sQuery(id+"F0.wireOp",EDGE,"E226"),sQuery(id+"F0.wireOp",EDGE,"E227"),sQuery(id+"F0.wireOp",EDGE,"E228"),sQuery(id+"F0.wireOp",EDGE,"E229"),sQuery(id+"F0.wireOp",EDGE,"E230"),sQuery(id+"F0.wireOp",EDGE,"E231"),sQuery(id+"F0.wireOp",EDGE,"E232"),sQuery(id+"F0.wireOp",EDGE,"E233"),sQuery(id+"F0.wireOp",EDGE,"E234"),sQuery(id+"F0.wireOp",EDGE,"E235"),sQuery(id+"F0.wireOp",EDGE,"E236"),sQuery(id+"F0.wireOp",EDGE,"E237"),sQuery(id+"F0.wireOp",EDGE,"E238"),sQuery(id+"F0.wireOp",EDGE,"E239"),sQuery(id+"F0.wireOp",EDGE,"E240"),sQuery(id+"F0.wireOp",EDGE,"E241"),sQuery(id+"F0.wireOp",EDGE,"E242"),sQuery(id+"F0.wireOp",EDGE,"E243"),sQuery(id+"F0.wireOp",EDGE,"E244"),sQuery(id+"F0.wireOp",EDGE,"E245"),sQuery(id+"F0.wireOp",EDGE,"E246"),sQuery(id+"F0.wireOp",EDGE,"E247"),sQuery(id+"F0.wireOp",EDGE,"E248"),sQuery(id+"F0.wireOp",EDGE,"E249"),sQuery(id+"F0.wireOp",EDGE,"E250"),sQuery(id+"F0.wireOp",EDGE,"E251"),sQuery(id+"F0.wireOp",EDGE,"E252"),sQuery(id+"F0.wireOp",EDGE,"E253"),sQuery(id+"F0.wireOp",EDGE,"E254"),sQuery(id+"F0.wireOp",EDGE,"E255"),sQuery(id+"F0.wireOp",EDGE,"E256"),sQuery(id+"F0.wireOp",EDGE,"E257"),sQuery(id+"F0.wireOp",EDGE,"E258"),sQuery(id+"F0.wireOp",EDGE,"E259"),sQuery(id+"F0.wireOp",EDGE,"E260"),sQuery(id+"F0.wireOp",EDGE,"E261"),sQuery(id+"F0.wireOp",EDGE,"E262"),sQuery(id+"F0.wireOp",EDGE,"E263"),sQuery(id+"F0.wireOp",EDGE,"E264"),sQuery(id+"F0.wireOp",EDGE,"E265"),sQuery(id+"F0.wireOp",EDGE,"E266"),sQuery(id+"F0.wireOp",EDGE,"E267"),sQuery(id+"F0.wireOp",EDGE,"E268"),sQuery(id+"F0.wireOp",EDGE,"E269"),sQuery(id+"F0.wireOp",EDGE,"E270"),sQuery(id+"F0.wireOp",EDGE,"E271"),sQuery(id+"F0.wireOp",EDGE,"E272"),sQuery(id+"F0.wireOp",EDGE,"E273"),sQuery(id+"F0.wireOp",EDGE,"E274"),sQuery(id+"F0.wireOp",EDGE,"E275"),sQuery(id+"F0.wireOp",EDGE,"E276"),sQuery(id+"F0.wireOp",EDGE,"E277"),sQuery(id+"F0.wireOp",EDGE,"E278"),sQuery(id+"F0.wireOp",EDGE,"E279"),sQuery(id+"F0.wireOp",EDGE,"E280"),sQuery(id+"F0.wireOp",EDGE,"E281"),sQuery(id+"F0.wireOp",EDGE,"E282"),sQuery(id+"F0.wireOp",EDGE,"E283"),sQuery(id+"F0.wireOp",EDGE,"E284"),sQuery(id+"F0.wireOp",EDGE,"E285"),sQuery(id+"F0.wireOp",EDGE,"E286"),sQuery(id+"F0.wireOp",EDGE,"E287"),sQuery(id+"F0.wireOp",EDGE,"E288"),sQuery(id+"F0.wireOp",EDGE,"E289"),sQuery(id+"F0.wireOp",EDGE,"E290"),sQuery(id+"F0.wireOp",EDGE,"E291"),sQuery(id+"F0.wireOp",EDGE,"E292"),sQuery(id+"F0.wireOp",EDGE,"E293"),sQuery(id+"F0.wireOp",EDGE,"E294"),sQuery(id+"F0.wireOp",EDGE,"E295"),sQuery(id+"F0.wireOp",EDGE,"E296"),sQuery(id+"F0.wireOp",EDGE,"E297"),sQuery(id+"F0.wireOp",EDGE,"E298"),sQuery(id+"F0.wireOp",EDGE,"E299"),sQuery(id+"F0.wireOp",EDGE,"E300"),sQuery(id+"F0.wireOp",EDGE,"E301"),sQuery(id+"F0.wireOp",EDGE,"E302"),sQuery(id+"F0.wireOp",EDGE,"E303"),sQuery(id+"F0.wireOp",EDGE,"E304"),sQuery(id+"F0.wireOp",EDGE,"E305"),sQuery(id+"F0.wireOp",EDGE,"E306"),sQuery(id+"F0.wireOp",EDGE,"E307"),sQuery(id+"F0.wireOp",EDGE,"E308"),sQuery(id+"F0.wireOp",EDGE,"E309"),sQuery(id+"F0.wireOp",EDGE,"E310"),sQuery(id+"F0.wireOp",EDGE,"E311"),sQuery(id+"F0.wireOp",EDGE,"E312"),sQuery(id+"F0.wireOp",EDGE,"E313"),sQuery(id+"F0.wireOp",EDGE,"E314"),sQuery(id+"F0.wireOp",EDGE,"E315"),sQuery(id+"F0.wireOp",EDGE,"E316"),sQuery(id+"F0.wireOp",EDGE,"E317"),sQuery(id+"F0.wireOp",EDGE,"E318"),sQuery(id+"F0.wireOp",EDGE,"E319"),sQuery(id+"F0.wireOp",EDGE,"E320"),sQuery(id+"F0.wireOp",EDGE,"E321"),sQuery(id+"F0.wireOp",EDGE,"E322"),sQuery(id+"F0.wireOp",EDGE,"E323"),sQuery(id+"F0.wireOp",EDGE,"E324"),sQuery(id+"F0.wireOp",EDGE,"E325"),sQuery(id+"F0.wireOp",EDGE,"E326"),sQuery(id+"F0.wireOp",EDGE,"E327"),sQuery(id+"F0.wireOp",EDGE,"E328"),sQuery(id+"F0.wireOp",EDGE,"E329"),sQuery(id+"F0.wireOp",EDGE,"E330"),sQuery(id+"F0.wireOp",EDGE,"E331"),sQuery(id+"F0.wireOp",EDGE,"E332"),sQuery(id+"F0.wireOp",EDGE,"E333"),sQuery(id+"F0.wireOp",EDGE,"E334"),sQuery(id+"F0.wireOp",EDGE,"E335"),sQuery(id+"F0.wireOp",EDGE,"E336"),sQuery(id+"F0.wireOp",EDGE,"E337"),sQuery(id+"F0.wireOp",EDGE,"E338"),sQuery(id+"F0.wireOp",EDGE,"E339"),sQuery(id+"F0.wireOp",EDGE,"E340"),sQuery(id+"F0.wireOp",EDGE,"E341"),sQuery(id+"F0.wireOp",EDGE,"E342"),sQuery(id+"F0.wireOp",EDGE,"E343"),sQuery(id+"F0.wireOp",EDGE,"E344"),sQuery(id+"F0.wireOp",EDGE,"E345"),sQuery(id+"F0.wireOp",EDGE,"E346"),sQuery(id+"F0.wireOp",EDGE,"E347"),sQuery(id+"F0.wireOp",EDGE,"E348"),sQuery(id+"F0.wireOp",EDGE,"E349"),sQuery(id+"F0.wireOp",EDGE,"E350"),sQuery(id+"F0.wireOp",EDGE,"E351"),sQuery(id+"F0.wireOp",EDGE,"E352"),sQuery(id+"F0.wireOp",EDGE,"E353"),sQuery(id+"F0.wireOp",EDGE,"E354"),sQuery(id+"F0.wireOp",EDGE,"E355"),sQuery(id+"F0.wireOp",EDGE,"E356"),sQuery(id+"F0.wireOp",EDGE,"E357"),sQuery(id+"F0.wireOp",EDGE,"E358"),sQuery(id+"F0.wireOp",EDGE,"E359"),sQuery(id+"F0.wireOp",EDGE,"E360"),sQuery(id+"F0.wireOp",EDGE,"E361"),sQuery(id+"F0.wireOp",EDGE,"E362"),sQuery(id+"F0.wireOp",EDGE,"E363"),sQuery(id+"F0.wireOp",EDGE,"E364"),sQuery(id+"F0.wireOp",EDGE,"E365"),sQuery(id+"F0.wireOp",EDGE,"E366"),sQuery(id+"F0.wireOp",EDGE,"E367"),sQuery(id+"F0.wireOp",EDGE,"E368"),sQuery(id+"F0.wireOp",EDGE,"E369"),sQuery(id+"F0.wireOp",EDGE,"E370"),sQuery(id+"F0.wireOp",EDGE,"E371"),sQuery(id+"F0.wireOp",EDGE,"E372"),sQuery(id+"F0.wireOp",EDGE,"E373"),sQuery(id+"F0.wireOp",EDGE,"E374"),sQuery(id+"F0.wireOp",EDGE,"E375"),sQuery(id+"F0.wireOp",EDGE,"E376"),sQuery(id+"F0.wireOp",EDGE,"E377"),sQuery(id+"F0.wireOp",EDGE,"E378"),sQuery(id+"F0.wireOp",EDGE,"E379"),sQuery(id+"F0.wireOp",EDGE,"E380"),sQuery(id+"F0.wireOp",EDGE,"E381"),sQuery(id+"F0.wireOp",EDGE,"E382"),sQuery(id+"F0.wireOp",EDGE,"E383"),sQuery(id+"F0.wireOp",EDGE,"E384"),sQuery(id+"F0.wireOp",EDGE,"E385"),sQuery(id+"F0.wireOp",EDGE,"E386"),sQuery(id+"F0.wireOp",EDGE,"E387"),sQuery(id+"F0.wireOp",EDGE,"E388"),sQuery(id+"F0.wireOp",EDGE,"E389"),sQuery(id+"F0.wireOp",EDGE,"E390"),sQuery(id+"F0.wireOp",EDGE,"E391"),sQuery(id+"F0.wireOp",EDGE,"E392"),sQuery(id+"F0.wireOp",EDGE,"E393"),sQuery(id+"F0.wireOp",EDGE,"E394"),sQuery(id+"F0.wireOp",EDGE,"E395"),sQuery(id+"F0.wireOp",EDGE,"E396"),sQuery(id+"F0.wireOp",EDGE,"E397"),sQuery(id+"F0.wireOp",EDGE,"E398"),sQuery(id+"F0.wireOp",EDGE,"E399"),sQuery(id+"F0.wireOp",EDGE,"E400"),sQuery(id+"F0.wireOp",EDGE,"E401"),sQuery(id+"F0.wireOp",EDGE,"E402"),sQuery(id+"F0.wireOp",EDGE,"E403"),sQuery(id+"F0.wireOp",EDGE,"E404"),sQuery(id+"F0.wireOp",EDGE,"E405"),sQuery(id+"F0.wireOp",EDGE,"E406"),sQuery(id+"F0.wireOp",EDGE,"E407"),sQuery(id+"F0.wireOp",EDGE,"E408"),sQuery(id+"F0.wireOp",EDGE,"E409"),sQuery(id+"F0.wireOp",EDGE,"E410"),sQuery(id+"F0.wireOp",EDGE,"E411"),sQuery(id+"F0.wireOp",EDGE,"E412"),sQuery(id+"F0.wireOp",EDGE,"E413"),sQuery(id+"F0.wireOp",EDGE,"E414"),sQuery(id+"F0.wireOp",EDGE,"E415"),sQuery(id+"F0.wireOp",EDGE,"E416"),sQuery(id+"F0.wireOp",EDGE,"E417"),sQuery(id+"F0.wireOp",EDGE,"E418"),sQuery(id+"F0.wireOp",EDGE,"E419"),sQuery(id+"F0.wireOp",EDGE,"E420"),sQuery(id+"F0.wireOp",EDGE,"E421"),sQuery(id+"F0.wireOp",EDGE,"E422"),sQuery(id+"F0.wireOp",EDGE,"E423"),sQuery(id+"F0.wireOp",EDGE,"E424"),sQuery(id+"F0.wireOp",EDGE,"E425"),sQuery(id+"F0.wireOp",EDGE,"E426"),sQuery(id+"F0.wireOp",EDGE,"E427"),sQuery(id+"F0.wireOp",EDGE,"E428"),sQuery(id+"F0.wireOp",EDGE,"E429"),sQuery(id+"F0.wireOp",EDGE,"E430"),sQuery(id+"F0.wireOp",EDGE,"E431"),sQuery(id+"F0.wireOp",EDGE,"E432"),sQuery(id+"F0.wireOp",EDGE,"E433"),sQuery(id+"F0.wireOp",EDGE,"E434"),sQuery(id+"F0.wireOp",EDGE,"E435"),sQuery(id+"F0.wireOp",EDGE,"E436"),sQuery(id+"F0.wireOp",EDGE,"E437"),sQuery(id+"F0.wireOp",EDGE,"E438"),sQuery(id+"F0.wireOp",EDGE,"E439"),sQuery(id+"F0.wireOp",EDGE,"E440"),sQuery(id+"F0.wireOp",EDGE,"E441"),sQuery(id+"F0.wireOp",EDGE,"E442"),sQuery(id+"F0.wireOp",EDGE,"E443"),sQuery(id+"F0.wireOp",EDGE,"E444"),sQuery(id+"F0.wireOp",EDGE,"E445"),sQuery(id+"F0.wireOp",EDGE,"E446"),sQuery(id+"F0.wireOp",EDGE,"E447"),sQuery(id+"F0.wireOp",EDGE,"E448"),sQuery(id+"F0.wireOp",EDGE,"E449"),sQuery(id+"F0.wireOp",EDGE,"E450"),sQuery(id+"F0.wireOp",EDGE,"E451"),sQuery(id+"F0.wireOp",EDGE,"E452"),sQuery(id+"F0.wireOp",EDGE,"E453"),sQuery(id+"F0.wireOp",EDGE,"E454"),sQuery(id+"F0.wireOp",EDGE,"E455"),sQuery(id+"F0.wireOp",EDGE,"E456"),sQuery(id+"F0.wireOp",EDGE,"E457"),sQuery(id+"F0.wireOp",EDGE,"E458"),sQuery(id+"F0.wireOp",EDGE,"E459"),sQuery(id+"F0.wireOp",EDGE,"E460"),sQuery(id+"F0.wireOp",EDGE,"E461"),sQuery(id+"F0.wireOp",EDGE,"E462"),sQuery(id+"F0.wireOp",EDGE,"E463"),sQuery(id+"F0.wireOp",EDGE,"E464"),sQuery(id+"F0.wireOp",EDGE,"E465"),sQuery(id+"F0.wireOp",EDGE,"E466"),sQuery(id+"F0.wireOp",EDGE,"E467"),sQuery(id+"F0.wireOp",EDGE,"E468"),sQuery(id+"F0.wireOp",EDGE,"E469"),sQuery(id+"F0.wireOp",EDGE,"E470"),sQuery(id+"F0.wireOp",EDGE,"E471"),sQuery(id+"F0.wireOp",EDGE,"E472"),sQuery(id+"F0.wireOp",EDGE,"E473"),sQuery(id+"F0.wireOp",EDGE,"E474"),sQuery(id+"F0.wireOp",EDGE,"E475"),sQuery(id+"F0.wireOp",EDGE,"E476"),sQuery(id+"F0.wireOp",EDGE,"E477"),sQuery(id+"F0.wireOp",EDGE,"E478"),sQuery(id+"F0.wireOp",EDGE,"E479"),sQuery(id+"F0.wireOp",EDGE,"E480"),sQuery(id+"F0.wireOp",EDGE,"E481"),sQuery(id+"F0.wireOp",EDGE,"E482"),sQuery(id+"F0.wireOp",EDGE,"E483"),sQuery(id+"F0.wireOp",EDGE,"E484"),sQuery(id+"F0.wireOp",EDGE,"E485"),sQuery(id+"F0.wireOp",EDGE,"E486"),sQuery(id+"F0.wireOp",EDGE,"E487"),sQuery(id+"F0.wireOp",EDGE,"E488"),sQuery(id+"F0.wireOp",EDGE,"E489"),sQuery(id+"F0.wireOp",EDGE,"E490"),sQuery(id+"F0.wireOp",EDGE,"E491"),sQuery(id+"F0.wireOp",EDGE,"E492"),sQuery(id+"F0.wireOp",EDGE,"E493"),sQuery(id+"F0.wireOp",EDGE,"E494"),sQuery(id+"F0.wireOp",EDGE,"E495"),sQuery(id+"F0.wireOp",EDGE,"E496"),sQuery(id+"F0.wireOp",EDGE,"E497"),sQuery(id+"F0.wireOp",EDGE,"E498"),sQuery(id+"F0.wireOp",EDGE,"E499"),sQuery(id+"F0.wireOp",EDGE,"E500"),sQuery(id+"F0.wireOp",EDGE,"E501"),sQuery(id+"F0.wireOp",EDGE,"E502"),sQuery(id+"F0.wireOp",EDGE,"E503"),sQuery(id+"F0.wireOp",EDGE,"E504"),sQuery(id+"F0.wireOp",EDGE,"E505"),sQuery(id+"F0.wireOp",EDGE,"E506"),sQuery(id+"F0.wireOp",EDGE,"E507"),sQuery(id+"F0.wireOp",EDGE,"E508"),sQuery(id+"F0.wireOp",EDGE,"E509"),sQuery(id+"F0.wireOp",EDGE,"E510"),sQuery(id+"F0.wireOp",EDGE,"E511"),sQuery(id+"F0.wireOp",EDGE,"E512"),sQuery(id+"F0.wireOp",EDGE,"E513"),sQuery(id+"F0.wireOp",EDGE,"E514"),sQuery(id+"F0.wireOp",EDGE,"E515"),sQuery(id+"F0.wireOp",EDGE,"E516"),sQuery(id+"F0.wireOp",EDGE,"E517"),sQuery(id+"F0.wireOp",EDGE,"E518"),sQuery(id+"F0.wireOp",EDGE,"E519"),sQuery(id+"F0.wireOp",EDGE,"E520"),sQuery(id+"F0.wireOp",EDGE,"E521"),sQuery(id+"F0.wireOp",EDGE,"E522"),sQuery(id+"F0.wireOp",EDGE,"E523"),sQuery(id+"F0.wireOp",EDGE,"E524"),sQuery(id+"F0.wireOp",EDGE,"E525"),sQuery(id+"F0.wireOp",EDGE,"E526"),sQuery(id+"F0.wireOp",EDGE,"E527"),sQuery(id+"F0.wireOp",EDGE,"E528"),sQuery(id+"F0.wireOp",EDGE,"E529"),sQuery(id+"F0.wireOp",EDGE,"E530"),sQuery(id+"F0.wireOp",EDGE,"E531"),sQuery(id+"F0.wireOp",EDGE,"E532"),sQuery(id+"F0.wireOp",EDGE,"E533"),sQuery(id+"F0.wireOp",EDGE,"E534"),sQuery(id+"F0.wireOp",EDGE,"E535"),sQuery(id+"F0.wireOp",EDGE,"E536"),sQuery(id+"F0.wireOp",EDGE,"E537"),sQuery(id+"F0.wireOp",EDGE,"E538"),sQuery(id+"F0.wireOp",EDGE,"E539"),sQuery(id+"F0.wireOp",EDGE,"E540"),sQuery(id+"F0.wireOp",EDGE,"E541"),sQuery(id+"F0.wireOp",EDGE,"E542"),sQuery(id+"F0.wireOp",EDGE,"E543"),sQuery(id+"F0.wireOp",EDGE,"E544"),sQuery(id+"F0.wireOp",EDGE,"E545"),sQuery(id+"F0.wireOp",EDGE,"E546"),sQuery(id+"F0.wireOp",EDGE,"E547"),sQuery(id+"F0.wireOp",EDGE,"E548"),sQuery(id+"F0.wireOp",EDGE,"E549"),sQuery(id+"F0.wireOp",EDGE,"E550"),sQuery(id+"F0.wireOp",EDGE,"E551"),sQuery(id+"F0.wireOp",EDGE,"E552"),sQuery(id+"F0.wireOp",EDGE,"E553"),sQuery(id+"F0.wireOp",EDGE,"E554"),sQuery(id+"F0.wireOp",EDGE,"E555"),sQuery(id+"F0.wireOp",EDGE,"E556"),sQuery(id+"F0.wireOp",EDGE,"E557"),sQuery(id+"F0.wireOp",EDGE,"E558"),sQuery(id+"F0.wireOp",EDGE,"E559"),sQuery(id+"F0.wireOp",EDGE,"E560"),sQuery(id+"F0.wireOp",EDGE,"E561"),sQuery(id+"F0.wireOp",EDGE,"E562"),sQuery(id+"F0.wireOp",EDGE,"E563"),sQuery(id+"F0.wireOp",EDGE,"E564"),sQuery(id+"F0.wireOp",EDGE,"E565"),sQuery(id+"F0.wireOp",EDGE,"E566"),sQuery(id+"F0.wireOp",EDGE,"E567"),sQuery(id+"F0.wireOp",EDGE,"E568"),sQuery(id+"F0.wireOp",EDGE,"E569"),sQuery(id+"F0.wireOp",EDGE,"E570"),sQuery(id+"F0.wireOp",EDGE,"E571"),sQuery(id+"F0.wireOp",EDGE,"E572"),sQuery(id+"F0.wireOp",EDGE,"E573"),sQuery(id+"F0.wireOp",EDGE,"E574"),sQuery(id+"F0.wireOp",EDGE,"E575"),sQuery(id+"F0.wireOp",EDGE,"E576"),sQuery(id+"F0.wireOp",EDGE,"E577"),sQuery(id+"F0.wireOp",EDGE,"E578"),sQuery(id+"F0.wireOp",EDGE,"E579"),sQuery(id+"F0.wireOp",EDGE,"E580"),sQuery(id+"F0.wireOp",EDGE,"E581"),sQuery(id+"F0.wireOp",EDGE,"E582"),sQuery(id+"F0.wireOp",EDGE,"E583"),sQuery(id+"F0.wireOp",EDGE,"E584"),sQuery(id+"F0.wireOp",EDGE,"E585"),sQuery(id+"F0.wireOp",EDGE,"E586"),sQuery(id+"F0.wireOp",EDGE,"E587"),sQuery(id+"F0.wireOp",EDGE,"E588"),sQuery(id+"F0.wireOp",EDGE,"E589"),sQuery(id+"F0.wireOp",EDGE,"E590"),sQuery(id+"F0.wireOp",EDGE,"E591"),sQuery(id+"F0.wireOp",EDGE,"E592"),sQuery(id+"F0.wireOp",EDGE,"E593"),sQuery(id+"F0.wireOp",EDGE,"E594"),sQuery(id+"F0.wireOp",EDGE,"E595"),sQuery(id+"F0.wireOp",EDGE,"E596"),sQuery(id+"F0.wireOp",EDGE,"E597"),sQuery(id+"F0.wireOp",EDGE,"E598"),sQuery(id+"F0.wireOp",EDGE,"E599"),sQuery(id+"F0.wireOp",EDGE,"E600"),sQuery(id+"F0.wireOp",EDGE,"E601"),sQuery(id+"F0.wireOp",EDGE,"E602"),sQuery(id+"F0.wireOp",EDGE,"E603"),sQuery(id+"F0.wireOp",EDGE,"E604"),sQuery(id+"F0.wireOp",EDGE,"E605"),sQuery(id+"F0.wireOp",EDGE,"E606"),sQuery(id+"F0.wireOp",EDGE,"E607"),sQuery(id+"F0.wireOp",EDGE,"E608"),sQuery(id+"F0.wireOp",EDGE,"E609"),sQuery(id+"F0.wireOp",EDGE,"E610"),sQuery(id+"F0.wireOp",EDGE,"E611"),sQuery(id+"F0.wireOp",EDGE,"E612"),sQuery(id+"F0.wireOp",EDGE,"E613"),sQuery(id+"F0.wireOp",EDGE,"E614"),sQuery(id+"F0.wireOp",EDGE,"E615"),sQuery(id+"F0.wireOp",EDGE,"E616"),sQuery(id+"F0.wireOp",EDGE,"E617"),sQuery(id+"F0.wireOp",EDGE,"E618"),sQuery(id+"F0.wireOp",EDGE,"E619"),sQuery(id+"F0.wireOp",EDGE,"E620"),sQuery(id+"F0.wireOp",EDGE,"E621"),sQuery(id+"F0.wireOp",EDGE,"E622"),sQuery(id+"F0.wireOp",EDGE,"E623"),sQuery(id+"F0.wireOp",EDGE,"E624"),sQuery(id+"F0.wireOp",EDGE,"E625"),sQuery(id+"F0.wireOp",EDGE,"E626"),sQuery(id+"F0.wireOp",EDGE,"E627"),sQuery(id+"F0.wireOp",EDGE,"E628"),sQuery(id+"F0.wireOp",EDGE,"E629"),sQuery(id+"F0.wireOp",EDGE,"E630"),sQuery(id+"F0.wireOp",EDGE,"E631"),sQuery(id+"F0.wireOp",EDGE,"E632"),sQuery(id+"F0.wireOp",EDGE,"E633"),sQuery(id+"F0.wireOp",EDGE,"E634"),sQuery(id+"F0.wireOp",EDGE,"E635"),sQuery(id+"F0.wireOp",EDGE,"E636"),sQuery(id+"F0.wireOp",EDGE,"E637"),sQuery(id+"F0.wireOp",EDGE,"E638"),sQuery(id+"F0.wireOp",EDGE,"E639"),sQuery(id+"F0.wireOp",EDGE,"E640"),sQuery(id+"F0.wireOp",EDGE,"E641"),sQuery(id+"F0.wireOp",EDGE,"E642"),sQuery(id+"F0.wireOp",EDGE,"E643"),sQuery(id+"F0.wireOp",EDGE,"E644"),sQuery(id+"F0.wireOp",EDGE,"E645"),sQuery(id+"F0.wireOp",EDGE,"E646"),sQuery(id+"F0.wireOp",EDGE,"E647"),sQuery(id+"F0.wireOp",EDGE,"E648"),sQuery(id+"F0.wireOp",EDGE,"E649"),sQuery(id+"F0.wireOp",EDGE,"E650"),sQuery(id+"F0.wireOp",EDGE,"E651"),sQuery(id+"F0.wireOp",EDGE,"E652"),sQuery(id+"F0.wireOp",EDGE,"E653"),sQuery(id+"F0.wireOp",EDGE,"E654"),sQuery(id+"F0.wireOp",EDGE,"E655"),sQuery(id+"F0.wireOp",EDGE,"E656"),sQuery(id+"F0.wireOp",EDGE,"E657"),sQuery(id+"F0.wireOp",EDGE,"E658"),sQuery(id+"F0.wireOp",EDGE,"E659"),sQuery(id+"F0.wireOp",EDGE,"E660"),sQuery(id+"F0.wireOp",EDGE,"E661"),sQuery(id+"F0.wireOp",EDGE,"E662"),sQuery(id+"F0.wireOp",EDGE,"E663"),sQuery(id+"F0.wireOp",EDGE,"E664"),sQuery(id+"F0.wireOp",EDGE,"E665"),sQuery(id+"F0.wireOp",EDGE,"E666"),sQuery(id+"F0.wireOp",EDGE,"E667"),sQuery(id+"F0.wireOp",EDGE,"E668"),sQuery(id+"F0.wireOp",EDGE,"E669"),sQuery(id+"F0.wireOp",EDGE,"E670"),sQuery(id+"F0.wireOp",EDGE,"E671"),sQuery(id+"F0.wireOp",EDGE,"E672"),sQuery(id+"F0.wireOp",EDGE,"E673"),sQuery(id+"F0.wireOp",EDGE,"E674"),sQuery(id+"F0.wireOp",EDGE,"E675"),sQuery(id+"F0.wireOp",EDGE,"E676"),sQuery(id+"F0.wireOp",EDGE,"E677"),sQuery(id+"F0.wireOp",EDGE,"E678"),sQuery(id+"F0.wireOp",EDGE,"E679"),sQuery(id+"F0.wireOp",EDGE,"E680"),sQuery(id+"F0.wireOp",EDGE,"E681"),sQuery(id+"F0.wireOp",EDGE,"E682"),sQuery(id+"F0.wireOp",EDGE,"E683"),sQuery(id+"F0.wireOp",EDGE,"E684"),sQuery(id+"F0.wireOp",EDGE,"E685"),sQuery(id+"F0.wireOp",EDGE,"E686"),sQuery(id+"F0.wireOp",EDGE,"E687"),sQuery(id+"F0.wireOp",EDGE,"E688"),sQuery(id+"F0.wireOp",EDGE,"E689"),sQuery(id+"F0.wireOp",EDGE,"E690"),sQuery(id+"F0.wireOp",EDGE,"E691"),sQuery(id+"F0.wireOp",EDGE,"E692"),sQuery(id+"F0.wireOp",EDGE,"E693"),sQuery(id+"F0.wireOp",EDGE,"E694"),sQuery(id+"F0.wireOp",EDGE,"E695"),sQuery(id+"F0.wireOp",EDGE,"E696"),sQuery(id+"F0.wireOp",EDGE,"E697"),sQuery(id+"F0.wireOp",EDGE,"E698"),sQuery(id+"F0.wireOp",EDGE,"E699"),sQuery(id+"F0.wireOp",EDGE,"E700"),sQuery(id+"F0.wireOp",EDGE,"E701"),sQuery(id+"F0.wireOp",EDGE,"E702"),sQuery(id+"F0.wireOp",EDGE,"E703"),sQuery(id+"F0.wireOp",EDGE,"E704"),sQuery(id+"F0.wireOp",EDGE,"E705"),sQuery(id+"F0.wireOp",EDGE,"E706"),sQuery(id+"F0.wireOp",EDGE,"E707"),sQuery(id+"F0.wireOp",EDGE,"E708"),sQuery(id+"F0.wireOp",EDGE,"E709"),sQuery(id+"F0.wireOp",EDGE,"E710"),sQuery(id+"F0.wireOp",EDGE,"E711"),sQuery(id+"F0.wireOp",EDGE,"E712"),sQuery(id+"F0.wireOp",EDGE,"E713"),sQuery(id+"F0.wireOp",EDGE,"E714"),sQuery(id+"F0.wireOp",EDGE,"E715"),sQuery(id+"F0.wireOp",EDGE,"E716"),sQuery(id+"F0.wireOp",EDGE,"E717"),sQuery(id+"F0.wireOp",EDGE,"E718"),sQuery(id+"F0.wireOp",EDGE,"E719"),sQuery(id+"F0.wireOp",EDGE,"E720"),sQuery(id+"F0.wireOp",EDGE,"E721"),sQuery(id+"F0.wireOp",EDGE,"E722"),sQuery(id+"F0.wireOp",EDGE,"E723"),sQuery(id+"F0.wireOp",EDGE,"E724"),sQuery(id+"F0.wireOp",EDGE,"E725"),sQuery(id+"F0.wireOp",EDGE,"E726"),sQuery(id+"F0.wireOp",EDGE,"E727"),sQuery(id+"F0.wireOp",EDGE,"E728"),sQuery(id+"F0.wireOp",EDGE,"E729"),sQuery(id+"F0.wireOp",EDGE,"E730"),sQuery(id+"F0.wireOp",EDGE,"E731"),sQuery(id+"F0.wireOp",EDGE,"E732"),sQuery(id+"F0.wireOp",EDGE,"E733"),sQuery(id+"F0.wireOp",EDGE,"E734"),sQuery(id+"F0.wireOp",EDGE,"E735"),sQuery(id+"F0.wireOp",EDGE,"E736"),sQuery(id+"F0.wireOp",EDGE,"E737"),sQuery(id+"F0.wireOp",EDGE,"E738"),sQuery(id+"F0.wireOp",EDGE,"E739"),sQuery(id+"F0.wireOp",EDGE,"E740"),sQuery(id+"F0.wireOp",EDGE,"E741"),sQuery(id+"F0.wireOp",EDGE,"E742"),sQuery(id+"F0.wireOp",EDGE,"E743"),sQuery(id+"F0.wireOp",EDGE,"E744"),sQuery(id+"F0.wireOp",EDGE,"E745"),sQuery(id+"F0.wireOp",EDGE,"E746"),sQuery(id+"F0.wireOp",EDGE,"E747"),sQuery(id+"F0.wireOp",EDGE,"E748"),sQuery(id+"F0.wireOp",EDGE,"E749"),sQuery(id+"F0.wireOp",EDGE,"E750"),sQuery(id+"F0.wireOp",EDGE,"E751"),sQuery(id+"F0.wireOp",EDGE,"E752"),sQuery(id+"F0.wireOp",EDGE,"E753"),sQuery(id+"F0.wireOp",EDGE,"E754"),sQuery(id+"F0.wireOp",EDGE,"E755"),sQuery(id+"F0.wireOp",EDGE,"E756"),sQuery(id+"F0.wireOp",EDGE,"E757"),sQuery(id+"F0.wireOp",EDGE,"E758"),sQuery(id+"F0.wireOp",EDGE,"E759"),sQuery(id+"F0.wireOp",EDGE,"E760"),sQuery(id+"F0.wireOp",EDGE,"E761"),sQuery(id+"F0.wireOp",EDGE,"E762"),sQuery(id+"F0.wireOp",EDGE,"E763"),sQuery(id+"F0.wireOp",EDGE,"E764"),sQuery(id+"F0.wireOp",EDGE,"E765"),sQuery(id+"F0.wireOp",EDGE,"E766"),sQuery(id+"F0.wireOp",EDGE,"E767"),sQuery(id+"F0.wireOp",EDGE,"E768"),sQuery(id+"F0.wireOp",EDGE,"E769"),sQuery(id+"F0.wireOp",EDGE,"E770"),sQuery(id+"F0.wireOp",EDGE,"E771"),sQuery(id+"F0.wireOp",EDGE,"E772"),sQuery(id+"F0.wireOp",EDGE,"E773"),sQuery(id+"F0.wireOp",EDGE,"E774"),sQuery(id+"F0.wireOp",EDGE,"E775"),sQuery(id+"F0.wireOp",EDGE,"E776"),sQuery(id+"F0.wireOp",EDGE,"E777"),sQuery(id+"F0.wireOp",EDGE,"E778"),sQuery(id+"F0.wireOp",EDGE,"E779"),sQuery(id+"F0.wireOp",EDGE,"E780"),sQuery(id+"F0.wireOp",EDGE,"E781"),sQuery(id+"F0.wireOp",EDGE,"E782"),sQuery(id+"F0.wireOp",EDGE,"E783"),sQuery(id+"F0.wireOp",EDGE,"E784"),sQuery(id+"F0.wireOp",EDGE,"E785"),sQuery(id+"F0.wireOp",EDGE,"E786"),sQuery(id+"F0.wireOp",EDGE,"E787"),sQuery(id+"F0.wireOp",EDGE,"E788"),sQuery(id+"F0.wireOp",EDGE,"E789"),sQuery(id+"F0.wireOp",EDGE,"E790"),sQuery(id+"F0.wireOp",EDGE,"E791"),sQuery(id+"F0.wireOp",EDGE,"E792"),sQuery(id+"F0.wireOp",EDGE,"E793"),sQuery(id+"F0.wireOp",EDGE,"E794"),sQuery(id+"F0.wireOp",EDGE,"E795"),sQuery(id+"F0.wireOp",EDGE,"E796"),sQuery(id+"F0.wireOp",EDGE,"E797"),sQuery(id+"F0.wireOp",EDGE,"E798"),sQuery(id+"F0.wireOp",EDGE,"E799"),sQuery(id+"F0.wireOp",EDGE,"E800"),sQuery(id+"F0.wireOp",EDGE,"E801"),sQuery(id+"F0.wireOp",EDGE,"E802"),sQuery(id+"F0.wireOp",EDGE,"E803"),sQuery(id+"F0.wireOp",EDGE,"E804"),sQuery(id+"F0.wireOp",EDGE,"E805"),sQuery(id+"F0.wireOp",EDGE,"E806"),sQuery(id+"F0.wireOp",EDGE,"E807"),sQuery(id+"F0.wireOp",EDGE,"E808"),sQuery(id+"F0.wireOp",EDGE,"E809"),sQuery(id+"F0.wireOp",EDGE,"E810"),sQuery(id+"F0.wireOp",EDGE,"E811"),sQuery(id+"F0.wireOp",EDGE,"E812"),sQuery(id+"F0.wireOp",EDGE,"E813"),sQuery(id+"F0.wireOp",EDGE,"E814"),sQuery(id+"F0.wireOp",EDGE,"E815"),sQuery(id+"F0.wireOp",EDGE,"E816"),sQuery(id+"F0.wireOp",EDGE,"E817"),sQuery(id+"F0.wireOp",EDGE,"E818"),sQuery(id+"F0.wireOp",EDGE,"E819"),sQuery(id+"F0.wireOp",EDGE,"E820"),sQuery(id+"F0.wireOp",EDGE,"E821"),sQuery(id+"F0.wireOp",EDGE,"E822"),sQuery(id+"F0.wireOp",EDGE,"E823"),sQuery(id+"F0.wireOp",EDGE,"E824"),sQuery(id+"F0.wireOp",EDGE,"E825"),sQuery(id+"F0.wireOp",EDGE,"E826"),sQuery(id+"F0.wireOp",EDGE,"E827"),sQuery(id+"F0.wireOp",EDGE,"E828"),sQuery(id+"F0.wireOp",EDGE,"E829"),sQuery(id+"F0.wireOp",EDGE,"E830"),sQuery(id+"F0.wireOp",EDGE,"E831"),sQuery(id+"F0.wireOp",EDGE,"E832"),sQuery(id+"F0.wireOp",EDGE,"E833"),sQuery(id+"F0.wireOp",EDGE,"E834"),sQuery(id+"F0.wireOp",EDGE,"E835"),sQuery(id+"F0.wireOp",EDGE,"E836"),sQuery(id+"F0.wireOp",EDGE,"E837"),sQuery(id+"F0.wireOp",EDGE,"E838"),sQuery(id+"F0.wireOp",EDGE,"E839"),sQuery(id+"F0.wireOp",EDGE,"E840"),sQuery(id+"F0.wireOp",EDGE,"E841"),sQuery(id+"F0.wireOp",EDGE,"E842"),sQuery(id+"F0.wireOp",EDGE,"E843"),sQuery(id+"F0.wireOp",EDGE,"E844"),sQuery(id+"F0.wireOp",EDGE,"E845"),sQuery(id+"F0.wireOp",EDGE,"E846"),sQuery(id+"F0.wireOp",EDGE,"E847"),sQuery(id+"F0.wireOp",EDGE,"E848"),sQuery(id+"F0.wireOp",EDGE,"E849"),sQuery(id+"F0.wireOp",EDGE,"E850"),sQuery(id+"F0.wireOp",EDGE,"E851"),sQuery(id+"F0.wireOp",EDGE,"E852"),sQuery(id+"F0.wireOp",EDGE,"E853"),sQuery(id+"F0.wireOp",EDGE,"E854"),sQuery(id+"F0.wireOp",EDGE,"E855"),sQuery(id+"F0.wireOp",EDGE,"E856"),sQuery(id+"F0.wireOp",EDGE,"E857"),sQuery(id+"F0.wireOp",EDGE,"E858"),sQuery(id+"F0.wireOp",EDGE,"E859"),sQuery(id+"F0.wireOp",EDGE,"E860"),sQuery(id+"F0.wireOp",EDGE,"E861"),sQuery(id+"F0.wireOp",EDGE,"E862"),sQuery(id+"F0.wireOp",EDGE,"E863"),sQuery(id+"F0.wireOp",EDGE,"E864"),sQuery(id+"F0.wireOp",EDGE,"E865"),sQuery(id+"F0.wireOp",EDGE,"E866"),sQuery(id+"F0.wireOp",EDGE,"E867"),sQuery(id+"F0.wireOp",EDGE,"E868"),sQuery(id+"F0.wireOp",EDGE,"E869"),sQuery(id+"F0.wireOp",EDGE,"E870"),sQuery(id+"F0.wireOp",EDGE,"E871"),sQuery(id+"F0.wireOp",EDGE,"E872"),sQuery(id+"F0.wireOp",EDGE,"E873"),sQuery(id+"F0.wireOp",EDGE,"E874"),sQuery(id+"F0.wireOp",EDGE,"E875"),sQuery(id+"F0.wireOp",EDGE,"E876"),sQuery(id+"F0.wireOp",EDGE,"E877"),sQuery(id+"F0.wireOp",EDGE,"E878"),sQuery(id+"F0.wireOp",EDGE,"E879"),sQuery(id+"F0.wireOp",EDGE,"E880"),sQuery(id+"F0.wireOp",EDGE,"E881"),sQuery(id+"F0.wireOp",EDGE,"E882"),sQuery(id+"F0.wireOp",EDGE,"E883"),sQuery(id+"F0.wireOp",EDGE,"E884"),sQuery(id+"F0.wireOp",EDGE,"E885"),sQuery(id+"F0.wireOp",EDGE,"E886"),sQuery(id+"F0.wireOp",EDGE,"E887"),sQuery(id+"F0.wireOp",EDGE,"E888"),sQuery(id+"F0.wireOp",EDGE,"E889"),sQuery(id+"F0.wireOp",EDGE,"E890"),sQuery(id+"F0.wireOp",EDGE,"E891"),sQuery(id+"F0.wireOp",EDGE,"E892"),sQuery(id+"F0.wireOp",EDGE,"E893"),sQuery(id+"F0.wireOp",EDGE,"E894"),sQuery(id+"F0.wireOp",EDGE,"E895"),sQuery(id+"F0.wireOp",EDGE,"E896"),sQuery(id+"F0.wireOp",EDGE,"E897"),sQuery(id+"F0.wireOp",EDGE,"E898"),sQuery(id+"F0.wireOp",EDGE,"E899"),sQuery(id+"F0.wireOp",EDGE,"E900"),sQuery(id+"F0.wireOp",EDGE,"E901"),sQuery(id+"F0.wireOp",EDGE,"E902"),sQuery(id+"F0.wireOp",EDGE,"E903"),sQuery(id+"F0.wireOp",EDGE,"E904"),sQuery(id+"F0.wireOp",EDGE,"E905"),sQuery(id+"F0.wireOp",EDGE,"E906"),sQuery(id+"F0.wireOp",EDGE,"E907"),sQuery(id+"F0.wireOp",EDGE,"E908"),sQuery(id+"F0.wireOp",EDGE,"E909"),sQuery(id+"F0.wireOp",EDGE,"E910"),sQuery(id+"F0.wireOp",EDGE,"E911"),sQuery(id+"F0.wireOp",EDGE,"E912"),sQuery(id+"F0.wireOp",EDGE,"E913"),sQuery(id+"F0.wireOp",EDGE,"E914"),sQuery(id+"F0.wireOp",EDGE,"E915"),sQuery(id+"F0.wireOp",EDGE,"E916"),sQuery(id+"F0.wireOp",EDGE,"E917"),sQuery(id+"F0.wireOp",EDGE,"E918"),sQuery(id+"F0.wireOp",EDGE,"E919"),sQuery(id+"F0.wireOp",EDGE,"E920"),sQuery(id+"F0.wireOp",EDGE,"E921"),sQuery(id+"F0.wireOp",EDGE,"E922"),sQuery(id+"F0.wireOp",EDGE,"E923"),sQuery(id+"F0.wireOp",EDGE,"E924"),sQuery(id+"F0.wireOp",EDGE,"E925"),sQuery(id+"F0.wireOp",EDGE,"E926"),sQuery(id+"F0.wireOp",EDGE,"E927"),sQuery(id+"F0.wireOp",EDGE,"E928"),sQuery(id+"F0.wireOp",EDGE,"E929"),sQuery(id+"F0.wireOp",EDGE,"E930"),sQuery(id+"F0.wireOp",EDGE,"E931"),sQuery(id+"F0.wireOp",EDGE,"E932"),sQuery(id+"F0.wireOp",EDGE,"E933"),sQuery(id+"F0.wireOp",EDGE,"E934"),sQuery(id+"F0.wireOp",EDGE,"E935"),sQuery(id+"F0.wireOp",EDGE,"E936"),sQuery(id+"F0.wireOp",EDGE,"E937"),sQuery(id+"F0.wireOp",EDGE,"E938"),sQuery(id+"F0.wireOp",EDGE,"E939"),sQuery(id+"F0.wireOp",EDGE,"E940"),sQuery(id+"F0.wireOp",EDGE,"E941"),sQuery(id+"F0.wireOp",EDGE,"E942"),sQuery(id+"F0.wireOp",EDGE,"E943"),sQuery(id+"F0.wireOp",EDGE,"E944"),sQuery(id+"F0.wireOp",EDGE,"E945"),sQuery(id+"F0.wireOp",EDGE,"E946"),sQuery(id+"F0.wireOp",EDGE,"E947"),sQuery(id+"F0.wireOp",EDGE,"E948"),sQuery(id+"F0.wireOp",EDGE,"E949"),sQuery(id+"F0.wireOp",EDGE,"E950"),sQuery(id+"F0.wireOp",EDGE,"E951"),sQuery(id+"F0.wireOp",EDGE,"E952"),sQuery(id+"F0.wireOp",EDGE,"E953"),sQuery(id+"F0.wireOp",EDGE,"E954"),sQuery(id+"F0.wireOp",EDGE,"E955"),sQuery(id+"F0.wireOp",EDGE,"E956"),sQuery(id+"F0.wireOp",EDGE,"E957"),sQuery(id+"F0.wireOp",EDGE,"E958"),sQuery(id+"F0.wireOp",EDGE,"E959"),sQuery(id+"F0.wireOp",EDGE,"E960"),sQuery(id+"F0.wireOp",EDGE,"E961"),sQuery(id+"F0.wireOp",EDGE,"E962"),sQuery(id+"F0.wireOp",EDGE,"E963"),sQuery(id+"F0.wireOp",EDGE,"E964"),sQuery(id+"F0.wireOp",EDGE,"E965"),sQuery(id+"F0.wireOp",EDGE,"E966"),sQuery(id+"F0.wireOp",EDGE,"E967"),sQuery(id+"F0.wireOp",EDGE,"E968"),sQuery(id+"F0.wireOp",EDGE,"E969"),sQuery(id+"F0.wireOp",EDGE,"E970"),sQuery(id+"F0.wireOp",EDGE,"E971"),sQuery(id+"F0.wireOp",EDGE,"E972"),sQuery(id+"F0.wireOp",EDGE,"E973"),sQuery(id+"F0.wireOp",EDGE,"E974"),sQuery(id+"F0.wireOp",EDGE,"E975"),sQuery(id+"F0.wireOp",EDGE,"E976"),sQuery(id+"F0.wireOp",EDGE,"E977"),sQuery(id+"F0.wireOp",EDGE,"E978"),sQuery(id+"F0.wireOp",EDGE,"E979"),sQuery(id+"F0.wireOp",EDGE,"E980"),sQuery(id+"F0.wireOp",EDGE,"E981"),sQuery(id+"F0.wireOp",EDGE,"E982"),sQuery(id+"F0.wireOp",EDGE,"E983"),sQuery(id+"F0.wireOp",EDGE,"E984"),sQuery(id+"F0.wireOp",EDGE,"E985"),sQuery(id+"F0.wireOp",EDGE,"E986"),sQuery(id+"F0.wireOp",EDGE,"E987"),sQuery(id+"F0.wireOp",EDGE,"E988"),sQuery(id+"F0.wireOp",EDGE,"E989"),sQuery(id+"F0.wireOp",EDGE,"E990"),sQuery(id+"F0.wireOp",EDGE,"E991"),sQuery(id+"F0.wireOp",EDGE,"E992"),sQuery(id+"F0.wireOp",EDGE,"E993"),sQuery(id+"F0.wireOp",EDGE,"E994"),sQuery(id+"F0.wireOp",EDGE,"E995"),sQuery(id+"F0.wireOp",EDGE,"E996"),sQuery(id+"F0.wireOp",EDGE,"E997"),sQuery(id+"F0.wireOp",EDGE,"E998"),sQuery(id+"F0.wireOp",EDGE,"E999"),sQuery(id+"F0.wireOp",EDGE,"E1000"),sQuery(id+"F0.wireOp",EDGE,"E1001"),sQuery(id+"F0.wireOp",EDGE,"E1002"),sQuery(id+"F0.wireOp",EDGE,"E1003"),sQuery(id+"F0.wireOp",EDGE,"E1004"),sQuery(id+"F0.wireOp",EDGE,"E1005"),sQuery(id+"F0.wireOp",EDGE,"E1006"),sQuery(id+"F0.wireOp",EDGE,"E1007"),sQuery(id+"F0.wireOp",EDGE,"E1008"),sQuery(id+"F0.wireOp",EDGE,"E1009"),sQuery(id+"F0.wireOp",EDGE,"E1010"),sQuery(id+"F0.wireOp",EDGE,"E1011"),sQuery(id+"F0.wireOp",EDGE,"E1012"),sQuery(id+"F0.wireOp",EDGE,"E1013"),sQuery(id+"F0.wireOp",EDGE,"E1014"),sQuery(id+"F0.wireOp",EDGE,"E1015"),sQuery(id+"F0.wireOp",EDGE,"E1016"),sQuery(id+"F0.wireOp",EDGE,"E1017"),sQuery(id+"F0.wireOp",EDGE,"E1018"),sQuery(id+"F0.wireOp",EDGE,"E1019"),sQuery(id+"F0.wireOp",EDGE,"E1020"),sQuery(id+"F0.wireOp",EDGE,"E1021"),sQuery(id+"F0.wireOp",EDGE,"E1022"),sQuery(id+"F0.wireOp",EDGE,"E1023"),sQuery(id+"F0.wireOp",EDGE,"E1024"),sQuery(id+"F0.wireOp",EDGE,"E1025"),sQuery(id+"F0.wireOp",EDGE,"E1026"),sQuery(id+"F0.wireOp",EDGE,"E1027"),sQuery(id+"F0.wireOp",EDGE,"E1028"),sQuery(id+"F0.wireOp",EDGE,"E1029"),sQuery(id+"F0.wireOp",EDGE,"E1030"),sQuery(id+"F0.wireOp",EDGE,"E1031"),sQuery(id+"F0.wireOp",EDGE,"E1032"),sQuery(id+"F0.wireOp",EDGE,"E1033"),sQuery(id+"F0.wireOp",EDGE,"E1034"),sQuery(id+"F0.wireOp",EDGE,"E1035"),sQuery(id+"F0.wireOp",EDGE,"E1036"),sQuery(id+"F0.wireOp",EDGE,"E1037"),sQuery(id+"F0.wireOp",EDGE,"E1038"),sQuery(id+"F0.wireOp",EDGE,"E1039"),sQuery(id+"F0.wireOp",EDGE,"E1040"),sQuery(id+"F0.wireOp",EDGE,"E1041"),sQuery(id+"F0.wireOp",EDGE,"E1042"),sQuery(id+"F0.wireOp",EDGE,"E1043"),sQuery(id+"F0.wireOp",EDGE,"E1044"),sQuery(id+"F0.wireOp",EDGE,"E1045"),sQuery(id+"F0.wireOp",EDGE,"E1046"),sQuery(id+"F0.wireOp",EDGE,"E1047"),sQuery(id+"F0.wireOp",EDGE,"E1048"),sQuery(id+"F0.wireOp",EDGE,"E1049"),sQuery(id+"F0.wireOp",EDGE,"E1050"),sQuery(id+"F0.wireOp",EDGE,"E1051"),sQuery(id+"F0.wireOp",EDGE,"E1052"),sQuery(id+"F0.wireOp",EDGE,"E1053"),sQuery(id+"F0.wireOp",EDGE,"E1054"),sQuery(id+"F0.wireOp",EDGE,"E1055"),sQuery(id+"F0.wireOp",EDGE,"E1056"),sQuery(id+"F0.wireOp",EDGE,"E1057"),sQuery(id+"F0.wireOp",EDGE,"E1058"),sQuery(id+"F0.wireOp",EDGE,"E1059"),sQuery(id+"F0.wireOp",EDGE,"E1060"),sQuery(id+"F0.wireOp",EDGE,"E1061"),sQuery(id+"F0.wireOp",EDGE,"E1062"),sQuery(id+"F0.wireOp",EDGE,"E1063"),sQuery(id+"F0.wireOp",EDGE,"E1064"),sQuery(id+"F0.wireOp",EDGE,"E1065"),sQuery(id+"F0.wireOp",EDGE,"E1066"),sQuery(id+"F0.wireOp",EDGE,"E1067"),sQuery(id+"F0.wireOp",EDGE,"E1068"),sQuery(id+"F0.wireOp",EDGE,"E1069"),sQuery(id+"F0.wireOp",EDGE,"E1070"),sQuery(id+"F0.wireOp",EDGE,"E1071"),sQuery(id+"F0.wireOp",EDGE,"E1072"),sQuery(id+"F0.wireOp",EDGE,"E1073"),sQuery(id+"F0.wireOp",EDGE,"E1074"),sQuery(id+"F0.wireOp",EDGE,"E1075"),sQuery(id+"F0.wireOp",EDGE,"E1076"),sQuery(id+"F0.wireOp",EDGE,"E1077"),sQuery(id+"F0.wireOp",EDGE,"E1078"),sQuery(id+"F0.wireOp",EDGE,"E1079"),sQuery(id+"F0.wireOp",EDGE,"E1080"),sQuery(id+"F0.wireOp",EDGE,"E1081"),sQuery(id+"F0.wireOp",EDGE,"E1082"),sQuery(id+"F0.wireOp",EDGE,"E1083"),sQuery(id+"F0.wireOp",EDGE,"E1084"),sQuery(id+"F0.wireOp",EDGE,"E1085"),sQuery(id+"F0.wireOp",EDGE,"E1086"),sQuery(id+"F0.wireOp",EDGE,"E1087"),sQuery(id+"F0.wireOp",EDGE,"E1088"),sQuery(id+"F0.wireOp",EDGE,"E1089"),sQuery(id+"F0.wireOp",EDGE,"E1090"),sQuery(id+"F0.wireOp",EDGE,"E1091"),sQuery(id+"F0.wireOp",EDGE,"E1092"),sQuery(id+"F0.wireOp",EDGE,"E1093"),sQuery(id+"F0.wireOp",EDGE,"E1094"),sQuery(id+"F0.wireOp",EDGE,"E1095"),sQuery(id+"F0.wireOp",EDGE,"E1096"),sQuery(id+"F0.wireOp",EDGE,"E1097"),sQuery(id+"F0.wireOp",EDGE,"E1098"),sQuery(id+"F0.wireOp",EDGE,"E1099"),sQuery(id+"F0.wireOp",EDGE,"E1100"),sQuery(id+"F0.wireOp",EDGE,"E1101"),sQuery(id+"F0.wireOp",EDGE,"E1102"),sQuery(id+"F0.wireOp",EDGE,"E1103"),sQuery(id+"F0.wireOp",EDGE,"E1104"),sQuery(id+"F0.wireOp",EDGE,"E1105"),sQuery(id+"F0.wireOp",EDGE,"E1106"),sQuery(id+"F0.wireOp",EDGE,"E1107"),sQuery(id+"F0.wireOp",EDGE,"E1108"),sQuery(id+"F0.wireOp",EDGE,"E1109"),sQuery(id+"F0.wireOp",EDGE,"E1110"),sQuery(id+"F0.wireOp",EDGE,"E1111"),sQuery(id+"F0.wireOp",EDGE,"E1112"),sQuery(id+"F0.wireOp",EDGE,"E1113"),sQuery(id+"F0.wireOp",EDGE,"E1114"),sQuery(id+"F0.wireOp",EDGE,"E1115"),sQuery(id+"F0.wireOp",EDGE,"E1116"),sQuery(id+"F0.wireOp",EDGE,"E1117"),sQuery(id+"F0.wireOp",EDGE,"E1118"),sQuery(id+"F0.wireOp",EDGE,"E1119"),sQuery(id+"F0.wireOp",EDGE,"E1120"),sQuery(id+"F0.wireOp",EDGE,"E1121"),sQuery(id+"F0.wireOp",EDGE,"E1122"),sQuery(id+"F0.wireOp",EDGE,"E1123"),sQuery(id+"F0.wireOp",EDGE,"E1124"),sQuery(id+"F0.wireOp",EDGE,"E1125"),sQuery(id+"F0.wireOp",EDGE,"E1126"),sQuery(id+"F0.wireOp",EDGE,"E1127"),sQuery(id+"F0.wireOp",EDGE,"E1128"),sQuery(id+"F0.wireOp",EDGE,"E1129"),sQuery(id+"F0.wireOp",EDGE,"E1130"),sQuery(id+"F0.wireOp",EDGE,"E1131"),sQuery(id+"F0.wireOp",EDGE,"E1132"),sQuery(id+"F0.wireOp",EDGE,"E1133"),sQuery(id+"F0.wireOp",EDGE,"E1134"),sQuery(id+"F0.wireOp",EDGE,"E1135"),sQuery(id+"F0.wireOp",EDGE,"E1136"),sQuery(id+"F0.wireOp",EDGE,"E1137"),sQuery(id+"F0.wireOp",EDGE,"E1138"),sQuery(id+"F0.wireOp",EDGE,"E1139"),sQuery(id+"F0.wireOp",EDGE,"E1140"),sQuery(id+"F0.wireOp",EDGE,"E1141"),sQuery(id+"F0.wireOp",EDGE,"E1142"),sQuery(id+"F0.wireOp",EDGE,"E1143"),sQuery(id+"F0.wireOp",EDGE,"E1144"),sQuery(id+"F0.wireOp",EDGE,"E1145"),sQuery(id+"F0.wireOp",EDGE,"E1146"),sQuery(id+"F0.wireOp",EDGE,"E1147"),sQuery(id+"F0.wireOp",EDGE,"E1148"),sQuery(id+"F0.wireOp",EDGE,"E1149"),sQuery(id+"F0.wireOp",EDGE,"E1150"),sQuery(id+"F0.wireOp",EDGE,"E1151"),sQuery(id+"F0.wireOp",EDGE,"E1152"),sQuery(id+"F0.wireOp",EDGE,"E1153"),sQuery(id+"F0.wireOp",EDGE,"E1154"),sQuery(id+"F0.wireOp",EDGE,"E1155"),sQuery(id+"F0.wireOp",EDGE,"E1156"),sQuery(id+"F0.wireOp",EDGE,"E1157"),sQuery(id+"F0.wireOp",EDGE,"E1158"),sQuery(id+"F0.wireOp",EDGE,"E1159"),sQuery(id+"F0.wireOp",EDGE,"E1160"),sQuery(id+"F0.wireOp",EDGE,"E1161"),sQuery(id+"F0.wireOp",EDGE,"E1162"),sQuery(id+"F0.wireOp",EDGE,"E1163"),sQuery(id+"F0.wireOp",EDGE,"E1164"),sQuery(id+"F0.wireOp",EDGE,"E1165"),sQuery(id+"F0.wireOp",EDGE,"E1166"),sQuery(id+"F0.wireOp",EDGE,"E1167"),sQuery(id+"F0.wireOp",EDGE,"E1168"),sQuery(id+"F0.wireOp",EDGE,"E1169"),sQuery(id+"F0.wireOp",EDGE,"E1170"),sQuery(id+"F0.wireOp",EDGE,"E1171"),sQuery(id+"F0.wireOp",EDGE,"E1172"),sQuery(id+"F0.wireOp",EDGE,"E1173"),sQuery(id+"F0.wireOp",EDGE,"E1174"),sQuery(id+"F0.wireOp",EDGE,"E1175"),sQuery(id+"F0.wireOp",EDGE,"E1176"),sQuery(id+"F0.wireOp",EDGE,"E1177"),sQuery(id+"F0.wireOp",EDGE,"E1178"),sQuery(id+"F0.wireOp",EDGE,"E1179"),sQuery(id+"F0.wireOp",EDGE,"E1180"),sQuery(id+"F0.wireOp",EDGE,"E1181"),sQuery(id+"F0.wireOp",EDGE,"E1182"),sQuery(id+"F0.wireOp",EDGE,"E1183"),sQuery(id+"F0.wireOp",EDGE,"E1184"),sQuery(id+"F0.wireOp",EDGE,"E1185"),sQuery(id+"F0.wireOp",EDGE,"E1186"),sQuery(id+"F0.wireOp",EDGE,"E1187"),sQuery(id+"F0.wireOp",EDGE,"E1188"),sQuery(id+"F0.wireOp",EDGE,"E1189"),sQuery(id+"F0.wireOp",EDGE,"E1190"),sQuery(id+"F0.wireOp",EDGE,"E1191"),sQuery(id+"F0.wireOp",EDGE,"E1192"),sQuery(id+"F0.wireOp",EDGE,"E1193"),sQuery(id+"F0.wireOp",EDGE,"E1194"),sQuery(id+"F0.wireOp",EDGE,"E1195"),sQuery(id+"F0.wireOp",EDGE,"E1196"),sQuery(id+"F0.wireOp",EDGE,"E1197"),sQuery(id+"F0.wireOp",EDGE,"E1198"),sQuery(id+"F0.wireOp",EDGE,"E1199"),sQuery(id+"F0.wireOp",EDGE,"E1200"),sQuery(id+"F0.wireOp",EDGE,"E1201"),sQuery(id+"F0.wireOp",EDGE,"E1202"),sQuery(id+"F0.wireOp",EDGE,"E1203"),sQuery(id+"F0.wireOp",EDGE,"E1204"),sQuery(id+"F0.wireOp",EDGE,"E1205"),sQuery(id+"F0.wireOp",EDGE,"E1206"),sQuery(id+"F0.wireOp",EDGE,"E1207"),sQuery(id+"F0.wireOp",EDGE,"E1208"),sQuery(id+"F0.wireOp",EDGE,"E1209"),sQuery(id+"F0.wireOp",EDGE,"E1210"),sQuery(id+"F0.wireOp",EDGE,"E1211"),sQuery(id+"F0.wireOp",EDGE,"E1212"),sQuery(id+"F0.wireOp",EDGE,"E1213"),sQuery(id+"F0.wireOp",EDGE,"E1214"),sQuery(id+"F0.wireOp",EDGE,"E1215"),sQuery(id+"F0.wireOp",EDGE,"E1216"),sQuery(id+"F0.wireOp",EDGE,"E1217"),sQuery(id+"F0.wireOp",EDGE,"E1218"),sQuery(id+"F0.wireOp",EDGE,"E1219"),sQuery(id+"F0.wireOp",EDGE,"E1220"),sQuery(id+"F0.wireOp",EDGE,"E1221"),sQuery(id+"F0.wireOp",EDGE,"E1222"),sQuery(id+"F0.wireOp",EDGE,"E1223"),sQuery(id+"F0.wireOp",EDGE,"E1224"),sQuery(id+"F0.wireOp",EDGE,"E1225"),sQuery(id+"F0.wireOp",EDGE,"E1226"),sQuery(id+"F0.wireOp",EDGE,"E1227"),sQuery(id+"F0.wireOp",EDGE,"E1228"),sQuery(id+"F0.wireOp",EDGE,"E1229"),sQuery(id+"F0.wireOp",EDGE,"E1230"),sQuery(id+"F0.wireOp",EDGE,"E1231"),sQuery(id+"F0.wireOp",EDGE,"E1232"),sQuery(id+"F0.wireOp",EDGE,"E1233"),sQuery(id+"F0.wireOp",EDGE,"E1234"),sQuery(id+"F0.wireOp",EDGE,"E1235"),sQuery(id+"F0.wireOp",EDGE,"E1236"),sQuery(id+"F0.wireOp",EDGE,"E1237"),sQuery(id+"F0.wireOp",EDGE,"E1238"),sQuery(id+"F0.wireOp",EDGE,"E1239"),sQuery(id+"F0.wireOp",EDGE,"E1240"),sQuery(id+"F0.wireOp",EDGE,"E1241"),sQuery(id+"F0.wireOp",EDGE,"E1242"),sQuery(id+"F0.wireOp",EDGE,"E1243"),sQuery(id+"F0.wireOp",EDGE,"E1244"),sQuery(id+"F0.wireOp",EDGE,"E1245"),sQuery(id+"F0.wireOp",EDGE,"E1246"),sQuery(id+"F0.wireOp",EDGE,"E1247"),sQuery(id+"F0.wireOp",EDGE,"E1248"),sQuery(id+"F0.wireOp",EDGE,"E1249"),sQuery(id+"F0.wireOp",EDGE,"E1250"),sQuery(id+"F0.wireOp",EDGE,"E1251"),sQuery(id+"F0.wireOp",EDGE,"E1252"),sQuery(id+"F0.wireOp",EDGE,"E1253"),sQuery(id+"F0.wireOp",EDGE,"E1254"),sQuery(id+"F0.wireOp",EDGE,"E1255"),sQuery(id+"F0.wireOp",EDGE,"E1256"),sQuery(id+"F0.wireOp",EDGE,"E1257"),sQuery(id+"F0.wireOp",EDGE,"E1258"),sQuery(id+"F0.wireOp",EDGE,"E1259"),sQuery(id+"F0.wireOp",EDGE,"E1260"),sQuery(id+"F0.wireOp",EDGE,"E1261"),sQuery(id+"F0.wireOp",EDGE,"E1262"),sQuery(id+"F0.wireOp",EDGE,"E1263"),sQuery(id+"F0.wireOp",EDGE,"E1264"),sQuery(id+"F0.wireOp",EDGE,"E1265"),sQuery(id+"F0.wireOp",EDGE,"E1266"),sQuery(id+"F0.wireOp",EDGE,"E1267"),sQuery(id+"F0.wireOp",EDGE,"E1268"),sQuery(id+"F0.wireOp",EDGE,"E1269"),sQuery(id+"F0.wireOp",EDGE,"E1270"),sQuery(id+"F0.wireOp",EDGE,"E1271"),sQuery(id+"F0.wireOp",EDGE,"E1272"),sQuery(id+"F0.wireOp",EDGE,"E1273"),sQuery(id+"F0.wireOp",EDGE,"E1274"),sQuery(id+"F0.wireOp",EDGE,"E1275"),sQuery(id+"F0.wireOp",EDGE,"E1276"),sQuery(id+"F0.wireOp",EDGE,"E1277"),sQuery(id+"F0.wireOp",EDGE,"E1278"),sQuery(id+"F0.wireOp",EDGE,"E1279"),sQuery(id+"F0.wireOp",EDGE,"E1280"),sQuery(id+"F0.wireOp",EDGE,"E1281"),sQuery(id+"F0.wireOp",EDGE,"E1282"),sQuery(id+"F0.wireOp",EDGE,"E1283"),sQuery(id+"F0.wireOp",EDGE,"E1284"),sQuery(id+"F0.wireOp",EDGE,"E1285"),sQuery(id+"F0.wireOp",EDGE,"E1286"),sQuery(id+"F0.wireOp",EDGE,"E1287"),sQuery(id+"F0.wireOp",EDGE,"E1288"),sQuery(id+"F0.wireOp",EDGE,"E1289"),sQuery(id+"F0.wireOp",EDGE,"E1290"),sQuery(id+"F0.wireOp",EDGE,"E1291"),sQuery(id+"F0.wireOp",EDGE,"E1292"),sQuery(id+"F0.wireOp",EDGE,"E1293"),sQuery(id+"F0.wireOp",EDGE,"E1294"),sQuery(id+"F0.wireOp",EDGE,"E1295"),sQuery(id+"F0.wireOp",EDGE,"E1296"),sQuery(id+"F0.wireOp",EDGE,"E1297"),sQuery(id+"F0.wireOp",EDGE,"E1298"),sQuery(id+"F0.wireOp",EDGE,"E1299"),sQuery(id+"F0.wireOp",EDGE,"E1300"),sQuery(id+"F0.wireOp",EDGE,"E1301"),sQuery(id+"F0.wireOp",EDGE,"E1302"),sQuery(id+"F0.wireOp",EDGE,"E1303"),sQuery(id+"F0.wireOp",EDGE,"E1304"),sQuery(id+"F0.wireOp",EDGE,"E1305"),sQuery(id+"F0.wireOp",EDGE,"E1306"),sQuery(id+"F0.wireOp",EDGE,"E1307"),sQuery(id+"F0.wireOp",EDGE,"E1308"),sQuery(id+"F0.wireOp",EDGE,"E1309"),sQuery(id+"F0.wireOp",EDGE,"E1310"),sQuery(id+"F0.wireOp",EDGE,"E1311"),sQuery(id+"F0.wireOp",EDGE,"E1312"),sQuery(id+"F0.wireOp",EDGE,"E1313"),sQuery(id+"F0.wireOp",EDGE,"E1314"),sQuery(id+"F0.wireOp",EDGE,"E1315"),sQuery(id+"F0.wireOp",EDGE,"E1316"),sQuery(id+"F0.wireOp",EDGE,"E1317"),sQuery(id+"F0.wireOp",EDGE,"E1318"),sQuery(id+"F0.wireOp",EDGE,"E1319"),sQuery(id+"F0.wireOp",EDGE,"E1320"),sQuery(id+"F0.wireOp",EDGE,"E1321"),sQuery(id+"F0.wireOp",EDGE,"E1322"),sQuery(id+"F0.wireOp",EDGE,"E1323"),sQuery(id+"F0.wireOp",EDGE,"E1324"),sQuery(id+"F0.wireOp",EDGE,"E1325"),sQuery(id+"F0.wireOp",EDGE,"E1326"),sQuery(id+"F0.wireOp",EDGE,"E1327"),sQuery(id+"F0.wireOp",EDGE,"E1328"),sQuery(id+"F0.wireOp",EDGE,"E1329"),sQuery(id+"F0.wireOp",EDGE,"E1330"),sQuery(id+"F0.wireOp",EDGE,"E1331"),sQuery(id+"F0.wireOp",EDGE,"E1332"),sQuery(id+"F0.wireOp",EDGE,"E1333"),sQuery(id+"F0.wireOp",EDGE,"E1334"),sQuery(id+"F0.wireOp",EDGE,"E1335"),sQuery(id+"F0.wireOp",EDGE,"E1336"),sQuery(id+"F0.wireOp",EDGE,"E1337"),sQuery(id+"F0.wireOp",EDGE,"E1338"),sQuery(id+"F0.wireOp",EDGE,"E1339"),sQuery(id+"F0.wireOp",EDGE,"E1340"),sQuery(id+"F0.wireOp",EDGE,"E1341"),sQuery(id+"F0.wireOp",EDGE,"E1342"),sQuery(id+"F0.wireOp",EDGE,"E1343"),sQuery(id+"F0.wireOp",EDGE,"E1344"),sQuery(id+"F0.wireOp",EDGE,"E1345"),sQuery(id+"F0.wireOp",EDGE,"E1346"),sQuery(id+"F0.wireOp",EDGE,"E1347"),sQuery(id+"F0.wireOp",EDGE,"E1348"),sQuery(id+"F0.wireOp",EDGE,"E1349"),sQuery(id+"F0.wireOp",EDGE,"E1350"),sQuery(id+"F0.wireOp",EDGE,"E1351"),sQuery(id+"F0.wireOp",EDGE,"E1352"),sQuery(id+"F0.wireOp",EDGE,"E1353"),sQuery(id+"F0.wireOp",EDGE,"E1354"),sQuery(id+"F0.wireOp",EDGE,"E1355"),sQuery(id+"F0.wireOp",EDGE,"E1356"),sQuery(id+"F0.wireOp",EDGE,"E1357"),sQuery(id+"F0.wireOp",EDGE,"E1358"),sQuery(id+"F0.wireOp",EDGE,"E1359"),sQuery(id+"F0.wireOp",EDGE,"E1360"),sQuery(id+"F0.wireOp",EDGE,"E1361"),sQuery(id+"F0.wireOp",EDGE,"E1362"),sQuery(id+"F0.wireOp",EDGE,"E1363"),sQuery(id+"F0.wireOp",EDGE,"E1364"),sQuery(id+"F0.wireOp",EDGE,"E1365"),sQuery(id+"F0.wireOp",EDGE,"E1366"),sQuery(id+"F0.wireOp",EDGE,"E1367"),sQuery(id+"F0.wireOp",EDGE,"E1368"),sQuery(id+"F0.wireOp",EDGE,"E1369"),sQuery(id+"F0.wireOp",EDGE,"E1370"),sQuery(id+"F0.wireOp",EDGE,"E1371"),sQuery(id+"F0.wireOp",EDGE,"E1372"),sQuery(id+"F0.wireOp",EDGE,"E1373"),sQuery(id+"F0.wireOp",EDGE,"E1374"),sQuery(id+"F0.wireOp",EDGE,"E1375"),sQuery(id+"F0.wireOp",EDGE,"E1376"),sQuery(id+"F0.wireOp",EDGE,"E1377"),sQuery(id+"F0.wireOp",EDGE,"E1378"),sQuery(id+"F0.wireOp",EDGE,"E1379"),sQuery(id+"F0.wireOp",EDGE,"E1380"),sQuery(id+"F0.wireOp",EDGE,"E1381"),sQuery(id+"F0.wireOp",EDGE,"E1382"),sQuery(id+"F0.wireOp",EDGE,"E1383"),sQuery(id+"F0.wireOp",EDGE,"E1384"),sQuery(id+"F0.wireOp",EDGE,"E1385"),sQuery(id+"F0.wireOp",EDGE,"E1386"),sQuery(id+"F0.wireOp",EDGE,"E1387"),sQuery(id+"F0.wireOp",EDGE,"E1388"),sQuery(id+"F0.wireOp",EDGE,"E1389"),sQuery(id+"F0.wireOp",EDGE,"E1390"),sQuery(id+"F0.wireOp",EDGE,"E1391"),sQuery(id+"F0.wireOp",EDGE,"E1392"),sQuery(id+"F0.wireOp",EDGE,"E1393"),sQuery(id+"F0.wireOp",EDGE,"E1394"),sQuery(id+"F0.wireOp",EDGE,"E1395"),sQuery(id+"F0.wireOp",EDGE,"E1396"),sQuery(id+"F0.wireOp",EDGE,"E1397"),sQuery(id+"F0.wireOp",EDGE,"E1398"),sQuery(id+"F0.wireOp",EDGE,"E1399"),sQuery(id+"F0.wireOp",EDGE,"E1400"),sQuery(id+"F0.wireOp",EDGE,"E1401"),sQuery(id+"F0.wireOp",EDGE,"E1402"),sQuery(id+"F0.wireOp",EDGE,"E1403"),sQuery(id+"F0.wireOp",EDGE,"E1404"),sQuery(id+"F0.wireOp",EDGE,"E1405"),sQuery(id+"F0.wireOp",EDGE,"E1406"),sQuery(id+"F0.wireOp",EDGE,"E1407"),sQuery(id+"F0.wireOp",EDGE,"E1408"),sQuery(id+"F0.wireOp",EDGE,"E1409"),sQuery(id+"F0.wireOp",EDGE,"E1410"),sQuery(id+"F0.wireOp",EDGE,"E1411"),sQuery(id+"F0.wireOp",EDGE,"E1412"),sQuery(id+"F0.wireOp",EDGE,"E1413"),sQuery(id+"F0.wireOp",EDGE,"E1414"),sQuery(id+"F0.wireOp",EDGE,"E1415"),sQuery(id+"F0.wireOp",EDGE,"E1416"),sQuery(id+"F0.wireOp",EDGE,"E1417"),sQuery(id+"F0.wireOp",EDGE,"E1418"),sQuery(id+"F0.wireOp",EDGE,"E1419"),sQuery(id+"F0.wireOp",EDGE,"E1420"),sQuery(id+"F0.wireOp",EDGE,"E1421"),sQuery(id+"F0.wireOp",EDGE,"E1422"),sQuery(id+"F0.wireOp",EDGE,"E1423"),sQuery(id+"F0.wireOp",EDGE,"E1424"),sQuery(id+"F0.wireOp",EDGE,"E1425"),sQuery(id+"F0.wireOp",EDGE,"E1426"),sQuery(id+"F0.wireOp",EDGE,"E1427"),sQuery(id+"F0.wireOp",EDGE,"E1428"),sQuery(id+"F0.wireOp",EDGE,"E1429"),sQuery(id+"F0.wireOp",EDGE,"E1430"),sQuery(id+"F0.wireOp",EDGE,"E1431"),sQuery(id+"F0.wireOp",EDGE,"E1432"),sQuery(id+"F0.wireOp",EDGE,"E1433"),sQuery(id+"F0.wireOp",EDGE,"E1434"),sQuery(id+"F0.wireOp",EDGE,"E1435"),sQuery(id+"F0.wireOp",EDGE,"E1436"),sQuery(id+"F0.wireOp",EDGE,"E1437"),sQuery(id+"F0.wireOp",EDGE,"E1438"),sQuery(id+"F0.wireOp",EDGE,"E1439"),sQuery(id+"F0.wireOp",EDGE,"E1440"),sQuery(id+"F0.wireOp",EDGE,"E1441"),sQuery(id+"F0.wireOp",EDGE,"E1442"),sQuery(id+"F0.wireOp",EDGE,"E1443"),sQuery(id+"F0.wireOp",EDGE,"E1444"),sQuery(id+"F0.wireOp",EDGE,"E1445"),sQuery(id+"F0.wireOp",EDGE,"E1446"),sQuery(id+"F0.wireOp",EDGE,"E1447"),sQuery(id+"F0.wireOp",EDGE,"E1448"),sQuery(id+"F0.wireOp",EDGE,"E1449"),sQuery(id+"F0.wireOp",EDGE,"E1450"),sQuery(id+"F0.wireOp",EDGE,"E1451"),sQuery(id+"F0.wireOp",EDGE,"E1452"),sQuery(id+"F0.wireOp",EDGE,"E1453"),sQuery(id+"F0.wireOp",EDGE,"E1454"),sQuery(id+"F0.wireOp",EDGE,"E1455"),sQuery(id+"F0.wireOp",EDGE,"E1456"),sQuery(id+"F0.wireOp",EDGE,"E1457"),sQuery(id+"F0.wireOp",EDGE,"E1458"),sQuery(id+"F0.wireOp",EDGE,"E1459"),sQuery(id+"F0.wireOp",EDGE,"E1460"),sQuery(id+"F0.wireOp",EDGE,"E1461"),sQuery(id+"F0.wireOp",EDGE,"E1462"),sQuery(id+"F0.wireOp",EDGE,"E1463"),sQuery(id+"F0.wireOp",EDGE,"E1464"),sQuery(id+"F0.wireOp",EDGE,"E1465"),sQuery(id+"F0.wireOp",EDGE,"E1466"),sQuery(id+"F0.wireOp",EDGE,"E1467"),sQuery(id+"F0.wireOp",EDGE,"E1468"),sQuery(id+"F0.wireOp",EDGE,"E1469"),sQuery(id+"F0.wireOp",EDGE,"E1470"),sQuery(id+"F0.wireOp",EDGE,"E1471"),sQuery(id+"F0.wireOp",EDGE,"E1472"),sQuery(id+"F0.wireOp",EDGE,"E1473"),sQuery(id+"F0.wireOp",EDGE,"E1474"),sQuery(id+"F0.wireOp",EDGE,"E1475"),sQuery(id+"F0.wireOp",EDGE,"E1476"),sQuery(id+"F0.wireOp",EDGE,"E1477"),sQuery(id+"F0.wireOp",EDGE,"E1478"),sQuery(id+"F0.wireOp",EDGE,"E1479"),sQuery(id+"F0.wireOp",EDGE,"E1480"),sQuery(id+"F0.wireOp",EDGE,"E1481"),sQuery(id+"F0.wireOp",EDGE,"E1482"),sQuery(id+"F0.wireOp",EDGE,"E1483"),sQuery(id+"F0.wireOp",EDGE,"E1484"),sQuery(id+"F0.wireOp",EDGE,"E1485"),sQuery(id+"F0.wireOp",EDGE,"E1486"),sQuery(id+"F0.wireOp",EDGE,"E1487"),sQuery(id+"F0.wireOp",EDGE,"E1488"),sQuery(id+"F0.wireOp",EDGE,"E1489"),sQuery(id+"F0.wireOp",EDGE,"E1490"),sQuery(id+"F0.wireOp",EDGE,"E1491"),sQuery(id+"F0.wireOp",EDGE,"E1492"),sQuery(id+"F0.wireOp",EDGE,"E1493"),sQuery(id+"F0.wireOp",EDGE,"E1494"),sQuery(id+"F0.wireOp",EDGE,"E1495"),sQuery(id+"F0.wireOp",EDGE,"E1496"),sQuery(id+"F0.wireOp",EDGE,"E1497"),sQuery(id+"F0.wireOp",EDGE,"E1498"),sQuery(id+"F0.wireOp",EDGE,"E1499"),sQuery(id+"F0.wireOp",EDGE,"E1500"),sQuery(id+"F0.wireOp",EDGE,"E1501"),sQuery(id+"F0.wireOp",EDGE,"E1502"),sQuery(id+"F0.wireOp",EDGE,"E1503"),sQuery(id+"F0.wireOp",EDGE,"E1504"),sQuery(id+"F0.wireOp",EDGE,"E1505"),sQuery(id+"F0.wireOp",EDGE,"E1506"),sQuery(id+"F0.wireOp",EDGE,"E1507"),sQuery(id+"F0.wireOp",EDGE,"E1508"),sQuery(id+"F0.wireOp",EDGE,"E1509"),sQuery(id+"F0.wireOp",EDGE,"E1510"),sQuery(id+"F0.wireOp",EDGE,"E1511"),sQuery(id+"F0.wireOp",EDGE,"E1512"),sQuery(id+"F0.wireOp",EDGE,"E1513"),sQuery(id+"F0.wireOp",EDGE,"E1514"),sQuery(id+"F0.wireOp",EDGE,"E1515"),sQuery(id+"F0.wireOp",EDGE,"E1516"),sQuery(id+"F0.wireOp",EDGE,"E1517"),sQuery(id+"F0.wireOp",EDGE,"E1518"),sQuery(id+"F0.wireOp",EDGE,"E1519"),sQuery(id+"F0.wireOp",EDGE,"E1520"),sQuery(id+"F0.wireOp",EDGE,"E1521"),sQuery(id+"F0.wireOp",EDGE,"E1522"),sQuery(id+"F0.wireOp",EDGE,"E1523"),sQuery(id+"F0.wireOp",EDGE,"E1524"),sQuery(id+"F0.wireOp",EDGE,"E1525"),sQuery(id+"F0.wireOp",EDGE,"E1526"),sQuery(id+"F0.wireOp",EDGE,"E1527"),sQuery(id+"F0.wireOp",EDGE,"E1528"),sQuery(id+"F0.wireOp",EDGE,"E1529"),sQuery(id+"F0.wireOp",EDGE,"E1530"),sQuery(id+"F0.wireOp",EDGE,"E1531"),sQuery(id+"F0.wireOp",EDGE,"E1532"),sQuery(id+"F0.wireOp",EDGE,"E1533"),sQuery(id+"F0.wireOp",EDGE,"E1534"),sQuery(id+"F0.wireOp",EDGE,"E1535"),sQuery(id+"F0.wireOp",EDGE,"E1536"),sQuery(id+"F0.wireOp",EDGE,"E1537"),sQuery(id+"F0.wireOp",EDGE,"E1538"),sQuery(id+"F0.wireOp",EDGE,"E1539"),sQuery(id+"F0.wireOp",EDGE,"E1540"),sQuery(id+"F0.wireOp",EDGE,"E1541"),sQuery(id+"F0.wireOp",EDGE,"E1542"),sQuery(id+"F0.wireOp",EDGE,"E1543"),sQuery(id+"F0.wireOp",EDGE,"E1544"),sQuery(id+"F0.wireOp",EDGE,"E1545"),sQuery(id+"F0.wireOp",EDGE,"E1546"),sQuery(id+"F0.wireOp",EDGE,"E1547"),sQuery(id+"F0.wireOp",EDGE,"E1548"),sQuery(id+"F0.wireOp",EDGE,"E1549"),sQuery(id+"F0.wireOp",EDGE,"E1550"),sQuery(id+"F0.wireOp",EDGE,"E1551"),sQuery(id+"F0.wireOp",EDGE,"E1552"),sQuery(id+"F0.wireOp",EDGE,"E1553"),sQuery(id+"F0.wireOp",EDGE,"E1554"),sQuery(id+"F0.wireOp",EDGE,"E1555"),sQuery(id+"F0.wireOp",EDGE,"E1556"),sQuery(id+"F0.wireOp",EDGE,"E1557"),sQuery(id+"F0.wireOp",EDGE,"E1558"),sQuery(id+"F0.wireOp",EDGE,"E1559"),sQuery(id+"F0.wireOp",EDGE,"E1560"),sQuery(id+"F0.wireOp",EDGE,"E1561"),sQuery(id+"F0.wireOp",EDGE,"E1562"),sQuery(id+"F0.wireOp",EDGE,"E1563"),sQuery(id+"F0.wireOp",EDGE,"E1564"),sQuery(id+"F0.wireOp",EDGE,"E1565"),sQuery(id+"F0.wireOp",EDGE,"E1566"),sQuery(id+"F0.wireOp",EDGE,"E1567"),sQuery(id+"F0.wireOp",EDGE,"E1568"),sQuery(id+"F0.wireOp",EDGE,"E1569"),sQuery(id+"F0.wireOp",EDGE,"E1570"),sQuery(id+"F0.wireOp",EDGE,"E1571"),sQuery(id+"F0.wireOp",EDGE,"E1572"),sQuery(id+"F0.wireOp",EDGE,"E1573"),sQuery(id+"F0.wireOp",EDGE,"E1574"),sQuery(id+"F0.wireOp",EDGE,"E1575"),sQuery(id+"F0.wireOp",EDGE,"E1576"),sQuery(id+"F0.wireOp",EDGE,"E1577"),sQuery(id+"F0.wireOp",EDGE,"E1578"),sQuery(id+"F0.wireOp",EDGE,"E1579"),sQuery(id+"F0.wireOp",EDGE,"E1580"),sQuery(id+"F0.wireOp",EDGE,"E1581"),sQuery(id+"F0.wireOp",EDGE,"E1582"),sQuery(id+"F0.wireOp",EDGE,"E1583"),sQuery(id+"F0.wireOp",EDGE,"E1584"),sQuery(id+"F0.wireOp",EDGE,"E1585"),sQuery(id+"F0.wireOp",EDGE,"E1586"),sQuery(id+"F0.wireOp",EDGE,"E1587"),sQuery(id+"F0.wireOp",EDGE,"E1588"),sQuery(id+"F0.wireOp",EDGE,"E1589"),sQuery(id+"F0.wireOp",EDGE,"E1590"),sQuery(id+"F0.wireOp",EDGE,"E1591"),sQuery(id+"F0.wireOp",EDGE,"E1592"),sQuery(id+"F0.wireOp",EDGE,"E1593"),sQuery(id+"F0.wireOp",EDGE,"E1594"),sQuery(id+"F0.wireOp",EDGE,"E1595"),sQuery(id+"F0.wireOp",EDGE,"E1596"),sQuery(id+"F0.wireOp",EDGE,"E1597"),sQuery(id+"F0.wireOp",EDGE,"E1598"),sQuery(id+"F0.wireOp",EDGE,"E1599"),sQuery(id+"F0.wireOp",EDGE,"E1600"),sQuery(id+"F0.wireOp",EDGE,"E1601"),sQuery(id+"F0.wireOp",EDGE,"E1602"),sQuery(id+"F0.wireOp",EDGE,"E1603"),sQuery(id+"F0.wireOp",EDGE,"E1604"),sQuery(id+"F0.wireOp",EDGE,"E1605"),sQuery(id+"F0.wireOp",EDGE,"E1606"),sQuery(id+"F0.wireOp",EDGE,"E1607"),sQuery(id+"F0.wireOp",EDGE,"E1608"),sQuery(id+"F0.wireOp",EDGE,"E1609"),sQuery(id+"F0.wireOp",EDGE,"E1610"),sQuery(id+"F0.wireOp",EDGE,"E1611"),sQuery(id+"F0.wireOp",EDGE,"E1612"),sQuery(id+"F0.wireOp",EDGE,"E1613"),sQuery(id+"F0.wireOp",EDGE,"E1614"),sQuery(id+"F0.wireOp",EDGE,"E1615"),sQuery(id+"F0.wireOp",EDGE,"E1616"),sQuery(id+"F0.wireOp",EDGE,"E1617"),sQuery(id+"F0.wireOp",EDGE,"E1618"),sQuery(id+"F0.wireOp",EDGE,"E1619"),sQuery(id+"F0.wireOp",EDGE,"E1620"),sQuery(id+"F0.wireOp",EDGE,"E1621"),sQuery(id+"F0.wireOp",EDGE,"E1622"),sQuery(id+"F0.wireOp",EDGE,"E1623"),sQuery(id+"F0.wireOp",EDGE,"E1624"),sQuery(id+"F0.wireOp",EDGE,"E1625"),sQuery(id+"F0.wireOp",EDGE,"E1626"),sQuery(id+"F0.wireOp",EDGE,"E1627"),sQuery(id+"F0.wireOp",EDGE,"E1628"),sQuery(id+"F0.wireOp",EDGE,"E1629"),sQuery(id+"F0.wireOp",EDGE,"E1630"),sQuery(id+"F0.wireOp",EDGE,"E1631"),sQuery(id+"F0.wireOp",EDGE,"E1632"),sQuery(id+"F0.wireOp",EDGE,"E1633"),sQuery(id+"F0.wireOp",EDGE,"E1634"),sQuery(id+"F0.wireOp",EDGE,"E1635"),sQuery(id+"F0.wireOp",EDGE,"E1636"),sQuery(id+"F0.wireOp",EDGE,"E1637"),sQuery(id+"F0.wireOp",EDGE,"E1638"),sQuery(id+"F0.wireOp",EDGE,"E1639"),sQuery(id+"F0.wireOp",EDGE,"E1640"),sQuery(id+"F0.wireOp",EDGE,"E1641"),sQuery(id+"F0.wireOp",EDGE,"E1642"),sQuery(id+"F0.wireOp",EDGE,"E1643"),sQuery(id+"F0.wireOp",EDGE,"E1644"),sQuery(id+"F0.wireOp",EDGE,"E1645"),sQuery(id+"F0.wireOp",EDGE,"E1646"),sQuery(id+"F0.wireOp",EDGE,"E1647"),sQuery(id+"F0.wireOp",EDGE,"E1648"),sQuery(id+"F0.wireOp",EDGE,"E1649"),sQuery(id+"F0.wireOp",EDGE,"E1650"),sQuery(id+"F0.wireOp",EDGE,"E1651"),sQuery(id+"F0.wireOp",EDGE,"E1652"),sQuery(id+"F0.wireOp",EDGE,"E1653"),sQuery(id+"F0.wireOp",EDGE,"E1654"),sQuery(id+"F0.wireOp",EDGE,"E1655"),sQuery(id+"F0.wireOp",EDGE,"E1656"),sQuery(id+"F0.wireOp",EDGE,"E1657"),sQuery(id+"F0.wireOp",EDGE,"E1658"),sQuery(id+"F0.wireOp",EDGE,"E1659"),sQuery(id+"F0.wireOp",EDGE,"E1660"),sQuery(id+"F0.wireOp",EDGE,"E1661"),sQuery(id+"F0.wireOp",EDGE,"E1662"),sQuery(id+"F0.wireOp",EDGE,"E1663"),sQuery(id+"F0.wireOp",EDGE,"E1664"),sQuery(id+"F0.wireOp",EDGE,"E1665"),sQuery(id+"F0.wireOp",EDGE,"E1666"),sQuery(id+"F0.wireOp",EDGE,"E1667"),sQuery(id+"F0.wireOp",EDGE,"E1668"),sQuery(id+"F0.wireOp",EDGE,"E1669"),sQuery(id+"F0.wireOp",EDGE,"E1670"),sQuery(id+"F0.wireOp",EDGE,"E1671"),sQuery(id+"F0.wireOp",EDGE,"E1672"),sQuery(id+"F0.wireOp",EDGE,"E1673"),sQuery(id+"F0.wireOp",EDGE,"E1674"),sQuery(id+"F0.wireOp",EDGE,"E1675"),sQuery(id+"F0.wireOp",EDGE,"E1676"),sQuery(id+"F0.wireOp",EDGE,"E1677"),sQuery(id+"F0.wireOp",EDGE,"E1678"),sQuery(id+"F0.wireOp",EDGE,"E1679"),sQuery(id+"F0.wireOp",EDGE,"E1680"),sQuery(id+"F0.wireOp",EDGE,"E1681"),sQuery(id+"F0.wireOp",EDGE,"E1682"),sQuery(id+"F0.wireOp",EDGE,"E1683"),sQuery(id+"F0.wireOp",EDGE,"E1684"),sQuery(id+"F0.wireOp",EDGE,"E1685"),sQuery(id+"F0.wireOp",EDGE,"E1686"),sQuery(id+"F0.wireOp",EDGE,"E1687"),sQuery(id+"F0.wireOp",EDGE,"E1688"),sQuery(id+"F0.wireOp",EDGE,"E1689"),sQuery(id+"F0.wireOp",EDGE,"E1690"),sQuery(id+"F0.wireOp",EDGE,"E1691"),sQuery(id+"F0.wireOp",EDGE,"E1692"),sQuery(id+"F0.wireOp",EDGE,"E1693"),sQuery(id+"F0.wireOp",EDGE,"E1694"),sQuery(id+"F0.wireOp",EDGE,"E1695"),sQuery(id+"F0.wireOp",EDGE,"E1696"),sQuery(id+"F0.wireOp",EDGE,"E1697"),sQuery(id+"F0.wireOp",EDGE,"E1698"),sQuery(id+"F0.wireOp",EDGE,"E1699"),sQuery(id+"F0.wireOp",EDGE,"E1700"),sQuery(id+"F0.wireOp",EDGE,"E1701"),sQuery(id+"F0.wireOp",EDGE,"E1702"),sQuery(id+"F0.wireOp",EDGE,"E1703"),sQuery(id+"F0.wireOp",EDGE,"E1704"),sQuery(id+"F0.wireOp",EDGE,"E1705"),sQuery(id+"F0.wireOp",EDGE,"E1706"),sQuery(id+"F0.wireOp",EDGE,"E1707"),sQuery(id+"F0.wireOp",EDGE,"E1708"),sQuery(id+"F0.wireOp",EDGE,"E1709"),sQuery(id+"F0.wireOp",EDGE,"E1710"),sQuery(id+"F0.wireOp",EDGE,"E1711"),sQuery(id+"F0.wireOp",EDGE,"E1712"),sQuery(id+"F0.wireOp",EDGE,"E1713"),sQuery(id+"F0.wireOp",EDGE,"E1714"),sQuery(id+"F0.wireOp",EDGE,"E1715"),sQuery(id+"F0.wireOp",EDGE,"E1716"),sQuery(id+"F0.wireOp",EDGE,"E1717"),sQuery(id+"F0.wireOp",EDGE,"E1718"),sQuery(id+"F0.wireOp",EDGE,"E1719"),sQuery(id+"F0.wireOp",EDGE,"E1720"),sQuery(id+"F0.wireOp",EDGE,"E1721"),sQuery(id+"F0.wireOp",EDGE,"E1722"),sQuery(id+"F0.wireOp",EDGE,"E1723"),sQuery(id+"F0.wireOp",EDGE,"E1724"),sQuery(id+"F0.wireOp",EDGE,"E1725"),sQuery(id+"F0.wireOp",EDGE,"E1726"),sQuery(id+"F0.wireOp",EDGE,"E1727"),sQuery(id+"F0.wireOp",EDGE,"E1728"),sQuery(id+"F0.wireOp",EDGE,"E1729"),sQuery(id+"F0.wireOp",EDGE,"E1730"),sQuery(id+"F0.wireOp",EDGE,"E1731"),sQuery(id+"F0.wireOp",EDGE,"E1732"),sQuery(id+"F0.wireOp",EDGE,"E1733"),sQuery(id+"F0.wireOp",EDGE,"E1734"),sQuery(id+"F0.wireOp",EDGE,"E1735"),sQuery(id+"F0.wireOp",EDGE,"E1736"),sQuery(id+"F0.wireOp",EDGE,"E1737"),sQuery(id+"F0.wireOp",EDGE,"E1738"),sQuery(id+"F0.wireOp",EDGE,"E1739"),sQuery(id+"F0.wireOp",EDGE,"E1740"),sQuery(id+"F0.wireOp",EDGE,"E1741"),sQuery(id+"F0.wireOp",EDGE,"E1742"),sQuery(id+"F0.wireOp",EDGE,"E1743"),sQuery(id+"F0.wireOp",EDGE,"E1744"),sQuery(id+"F0.wireOp",EDGE,"E1745"),sQuery(id+"F0.wireOp",EDGE,"E1746"),sQuery(id+"F0.wireOp",EDGE,"E1747"),sQuery(id+"F0.wireOp",EDGE,"E1748"),sQuery(id+"F0.wireOp",EDGE,"E1749"),sQuery(id+"F0.wireOp",EDGE,"E1750"),sQuery(id+"F0.wireOp",EDGE,"E1751"),sQuery(id+"F0.wireOp",EDGE,"E1752"),sQuery(id+"F0.wireOp",EDGE,"E1753"),sQuery(id+"F0.wireOp",EDGE,"E1754"),sQuery(id+"F0.wireOp",EDGE,"E1755"),sQuery(id+"F0.wireOp",EDGE,"E1756"),sQuery(id+"F0.wireOp",EDGE,"E1757"),sQuery(id+"F0.wireOp",EDGE,"E1758"),sQuery(id+"F0.wireOp",EDGE,"E1759"),sQuery(id+"F0.wireOp",EDGE,"E1760"),sQuery(id+"F0.wireOp",EDGE,"E1761"),sQuery(id+"F0.wireOp",EDGE,"E1762"),sQuery(id+"F0.wireOp",EDGE,"E1763"),sQuery(id+"F0.wireOp",EDGE,"E1764"),sQuery(id+"F0.wireOp",EDGE,"E1765"),sQuery(id+"F0.wireOp",EDGE,"E1766"),sQuery(id+"F0.wireOp",EDGE,"E1767"),sQuery(id+"F0.wireOp",EDGE,"E1768"),sQuery(id+"F0.wireOp",EDGE,"E1769"),sQuery(id+"F0.wireOp",EDGE,"E1770"),sQuery(id+"F0.wireOp",EDGE,"E1771"),sQuery(id+"F0.wireOp",EDGE,"E1772"),sQuery(id+"F0.wireOp",EDGE,"E1773"),sQuery(id+"F0.wireOp",EDGE,"E1774"),sQuery(id+"F0.wireOp",EDGE,"E1775"),sQuery(id+"F0.wireOp",EDGE,"E1776"),sQuery(id+"F0.wireOp",EDGE,"E1777"),sQuery(id+"F0.wireOp",EDGE,"E1778"),sQuery(id+"F0.wireOp",EDGE,"E1779"),sQuery(id+"F0.wireOp",EDGE,"E1780"),sQuery(id+"F0.wireOp",EDGE,"E1781"),sQuery(id+"F0.wireOp",EDGE,"E1782"),sQuery(id+"F0.wireOp",EDGE,"E1783"),sQuery(id+"F0.wireOp",EDGE,"E1784"),sQuery(id+"F0.wireOp",EDGE,"E1785"),sQuery(id+"F0.wireOp",EDGE,"E1786"),sQuery(id+"F0.wireOp",EDGE,"E1787"),sQuery(id+"F0.wireOp",EDGE,"E1788"),sQuery(id+"F0.wireOp",EDGE,"E1789"),sQuery(id+"F0.wireOp",EDGE,"E1790"),sQuery(id+"F0.wireOp",EDGE,"E1791"),sQuery(id+"F0.wireOp",EDGE,"E1792"),sQuery(id+"F0.wireOp",EDGE,"E1793"),sQuery(id+"F0.wireOp",EDGE,"E1794"),sQuery(id+"F0.wireOp",EDGE,"E1795"),sQuery(id+"F0.wireOp",EDGE,"E1796"),sQuery(id+"F0.wireOp",EDGE,"E1797"),sQuery(id+"F0.wireOp",EDGE,"E1798"),sQuery(id+"F0.wireOp",EDGE,"E1799"),sQuery(id+"F0.wireOp",EDGE,"E1800"),sQuery(id+"F0.wireOp",EDGE,"E1801"),sQuery(id+"F0.wireOp",EDGE,"E1802"),sQuery(id+"F0.wireOp",EDGE,"E1803"),sQuery(id+"F0.wireOp",EDGE,"E1804"),sQuery(id+"F0.wireOp",EDGE,"E1805"),sQuery(id+"F0.wireOp",EDGE,"E1806"),sQuery(id+"F0.wireOp",EDGE,"E1807"),sQuery(id+"F0.wireOp",EDGE,"E1808"),sQuery(id+"F0.wireOp",EDGE,"E1809"),sQuery(id+"F0.wireOp",EDGE,"E1810"),sQuery(id+"F0.wireOp",EDGE,"E1811"),sQuery(id+"F0.wireOp",EDGE,"E1812"),sQuery(id+"F0.wireOp",EDGE,"E1813"),sQuery(id+"F0.wireOp",EDGE,"E1814"),sQuery(id+"F0.wireOp",EDGE,"E1815"),sQuery(id+"F0.wireOp",EDGE,"E1816"),sQuery(id+"F0.wireOp",EDGE,"E1817"),sQuery(id+"F0.wireOp",EDGE,"E1818"),sQuery(id+"F0.wireOp",EDGE,"E1819"),sQuery(id+"F0.wireOp",EDGE,"E1820"),sQuery(id+"F0.wireOp",EDGE,"E1821"),sQuery(id+"F0.wireOp",EDGE,"E1822"),sQuery(id+"F0.wireOp",EDGE,"E1823"),sQuery(id+"F0.wireOp",EDGE,"E1824"),sQuery(id+"F0.wireOp",EDGE,"E1825"),sQuery(id+"F0.wireOp",EDGE,"E1826"),sQuery(id+"F0.wireOp",EDGE,"E1827"),sQuery(id+"F0.wireOp",EDGE,"E1828"),sQuery(id+"F0.wireOp",EDGE,"E1829"),sQuery(id+"F0.wireOp",EDGE,"E1830"),sQuery(id+"F0.wireOp",EDGE,"E1831"),sQuery(id+"F0.wireOp",EDGE,"E1832"),sQuery(id+"F0.wireOp",EDGE,"E1833"),sQuery(id+"F0.wireOp",EDGE,"E1834"),sQuery(id+"F0.wireOp",EDGE,"E1835"),sQuery(id+"F0.wireOp",EDGE,"E1836"),sQuery(id+"F0.wireOp",EDGE,"E1837"),sQuery(id+"F0.wireOp",EDGE,"E1838"),sQuery(id+"F0.wireOp",EDGE,"E1839"),sQuery(id+"F0.wireOp",EDGE,"E1840"),sQuery(id+"F0.wireOp",EDGE,"E1841"),sQuery(id+"F0.wireOp",EDGE,"E1842"),sQuery(id+"F0.wireOp",EDGE,"E1843"),sQuery(id+"F0.wireOp",EDGE,"E1844"),sQuery(id+"F0.wireOp",EDGE,"E1845"),sQuery(id+"F0.wireOp",EDGE,"E1846"),sQuery(id+"F0.wireOp",EDGE,"E1847"),sQuery(id+"F0.wireOp",EDGE,"E1848"),sQuery(id+"F0.wireOp",EDGE,"E1849"),sQuery(id+"F0.wireOp",EDGE,"E1850"),sQuery(id+"F0.wireOp",EDGE,"E1851"),sQuery(id+"F0.wireOp",EDGE,"E1852"),sQuery(id+"F0.wireOp",EDGE,"E1853"),sQuery(id+"F0.wireOp",EDGE,"E1854"),sQuery(id+"F0.wireOp",EDGE,"E1855"),sQuery(id+"F0.wireOp",EDGE,"E1856"),sQuery(id+"F0.wireOp",EDGE,"E1857"),sQuery(id+"F0.wireOp",EDGE,"E1858"),sQuery(id+"F0.wireOp",EDGE,"E1859"),sQuery(id+"F0.wireOp",EDGE,"E1860"),sQuery(id+"F0.wireOp",EDGE,"E1861"),sQuery(id+"F0.wireOp",EDGE,"E1862"),sQuery(id+"F0.wireOp",EDGE,"E1863"),sQuery(id+"F0.wireOp",EDGE,"E1864"),sQuery(id+"F0.wireOp",EDGE,"E1865"),sQuery(id+"F0.wireOp",EDGE,"E1866"),sQuery(id+"F0.wireOp",EDGE,"E1867"),sQuery(id+"F0.wireOp",EDGE,"E1868"),sQuery(id+"F0.wireOp",EDGE,"E1869"),sQuery(id+"F0.wireOp",EDGE,"E1870"),sQuery(id+"F0.wireOp",EDGE,"E1871"),sQuery(id+"F0.wireOp",EDGE,"E1872"),sQuery(id+"F0.wireOp",EDGE,"E1873"),sQuery(id+"F0.wireOp",EDGE,"E1874"),sQuery(id+"F0.wireOp",EDGE,"E1875"),sQuery(id+"F0.wireOp",EDGE,"E1876"),sQuery(id+"F0.wireOp",EDGE,"E1877"),sQuery(id+"F0.wireOp",EDGE,"E1878"),sQuery(id+"F0.wireOp",EDGE,"E1879"),sQuery(id+"F0.wireOp",EDGE,"E1880"),sQuery(id+"F0.wireOp",EDGE,"E1881"),sQuery(id+"F0.wireOp",EDGE,"E1882"),sQuery(id+"F0.wireOp",EDGE,"E1883"),sQuery(id+"F0.wireOp",EDGE,"E1884"),sQuery(id+"F0.wireOp",EDGE,"E1885"),sQuery(id+"F0.wireOp",EDGE,"E1886"),sQuery(id+"F0.wireOp",EDGE,"E1887"),sQuery(id+"F0.wireOp",EDGE,"E1888"),sQuery(id+"F0.wireOp",EDGE,"E1889"),sQuery(id+"F0.wireOp",EDGE,"E1890"),sQuery(id+"F0.wireOp",EDGE,"E1891"),sQuery(id+"F0.wireOp",EDGE,"E1892"),sQuery(id+"F0.wireOp",EDGE,"E1893"),sQuery(id+"F0.wireOp",EDGE,"E1894"),sQuery(id+"F0.wireOp",EDGE,"E1895"),sQuery(id+"F0.wireOp",EDGE,"E1896"),sQuery(id+"F0.wireOp",EDGE,"E1897"),sQuery(id+"F0.wireOp",EDGE,"E1898"),sQuery(id+"F0.wireOp",EDGE,"E1899"),sQuery(id+"F0.wireOp",EDGE,"E1900"),sQuery(id+"F0.wireOp",EDGE,"E1901"),sQuery(id+"F0.wireOp",EDGE,"E1902"),sQuery(id+"F0.wireOp",EDGE,"E1903"),sQuery(id+"F0.wireOp",EDGE,"E1904"),sQuery(id+"F0.wireOp",EDGE,"E1905"),sQuery(id+"F0.wireOp",EDGE,"E1906"),sQuery(id+"F0.wireOp",EDGE,"E1907"),sQuery(id+"F0.wireOp",EDGE,"E1908"),sQuery(id+"F0.wireOp",EDGE,"E1909"),sQuery(id+"F0.wireOp",EDGE,"E1910"),sQuery(id+"F0.wireOp",EDGE,"E1911"),sQuery(id+"F0.wireOp",EDGE,"E1912"),sQuery(id+"F0.wireOp",EDGE,"E1913"),sQuery(id+"F0.wireOp",EDGE,"E1914"),sQuery(id+"F0.wireOp",EDGE,"E1915"),sQuery(id+"F0.wireOp",EDGE,"E1916"),sQuery(id+"F0.wireOp",EDGE,"E1917"),sQuery(id+"F0.wireOp",EDGE,"E1918"),sQuery(id+"F0.wireOp",EDGE,"E1919"),sQuery(id+"F0.wireOp",EDGE,"E1920"),sQuery(id+"F0.wireOp",EDGE,"E1921"),sQuery(id+"F0.wireOp",EDGE,"E1922"),sQuery(id+"F0.wireOp",EDGE,"E1923"),sQuery(id+"F0.wireOp",EDGE,"E1924"),sQuery(id+"F0.wireOp",EDGE,"E1925"),sQuery(id+"F0.wireOp",EDGE,"E1926"),sQuery(id+"F0.wireOp",EDGE,"E1927"),sQuery(id+"F0.wireOp",EDGE,"E1928"),sQuery(id+"F0.wireOp",EDGE,"E1929"),sQuery(id+"F0.wireOp",EDGE,"E1930"),sQuery(id+"F0.wireOp",EDGE,"E1931"),sQuery(id+"F0.wireOp",EDGE,"E1932"),sQuery(id+"F0.wireOp",EDGE,"E1933"),sQuery(id+"F0.wireOp",EDGE,"E1934"),sQuery(id+"F0.wireOp",EDGE,"E1935"),sQuery(id+"F0.wireOp",EDGE,"E1936"),sQuery(id+"F0.wireOp",EDGE,"E1937"),sQuery(id+"F0.wireOp",EDGE,"E1938"),sQuery(id+"F0.wireOp",EDGE,"E1939"),sQuery(id+"F0.wireOp",EDGE,"E1940"),sQuery(id+"F0.wireOp",EDGE,"E1941"),sQuery(id+"F0.wireOp",EDGE,"E1942"),sQuery(id+"F0.wireOp",EDGE,"E1943"),sQuery(id+"F0.wireOp",EDGE,"E1944"),sQuery(id+"F0.wireOp",EDGE,"E1945"),sQuery(id+"F0.wireOp",EDGE,"E1946"),sQuery(id+"F0.wireOp",EDGE,"E1947"),sQuery(id+"F0.wireOp",EDGE,"E1948"),sQuery(id+"F0.wireOp",EDGE,"E1949"),sQuery(id+"F0.wireOp",EDGE,"E1950"),sQuery(id+"F0.wireOp",EDGE,"E1951"),sQuery(id+"F0.wireOp",EDGE,"E1952"),sQuery(id+"F0.wireOp",EDGE,"E1953"),sQuery(id+"F0.wireOp",EDGE,"E1954"),sQuery(id+"F0.wireOp",EDGE,"E1955"),sQuery(id+"F0.wireOp",EDGE,"E1956"),sQuery(id+"F0.wireOp",EDGE,"E1957"),sQuery(id+"F0.wireOp",EDGE,"E1958"),sQuery(id+"F0.wireOp",EDGE,"E1959"),sQuery(id+"F0.wireOp",EDGE,"E1960"),sQuery(id+"F0.wireOp",EDGE,"E1961"),sQuery(id+"F0.wireOp",EDGE,"E1962"),sQuery(id+"F0.wireOp",EDGE,"E1963"),sQuery(id+"F0.wireOp",EDGE,"E1964"),sQuery(id+"F0.wireOp",EDGE,"E1965"),sQuery(id+"F0.wireOp",EDGE,"E1966"),sQuery(id+"F0.wireOp",EDGE,"E1967"),sQuery(id+"F0.wireOp",EDGE,"E1968"),sQuery(id+"F0.wireOp",EDGE,"E1969"),sQuery(id+"F0.wireOp",EDGE,"E1970"),sQuery(id+"F0.wireOp",EDGE,"E1971"),sQuery(id+"F0.wireOp",EDGE,"E1972"),sQuery(id+"F0.wireOp",EDGE,"E1973"),sQuery(id+"F0.wireOp",EDGE,"E1974"),sQuery(id+"F0.wireOp",EDGE,"E1975"),sQuery(id+"F0.wireOp",EDGE,"E1976"),sQuery(id+"F0.wireOp",EDGE,"E1977"),sQuery(id+"F0.wireOp",EDGE,"E1978"),sQuery(id+"F0.wireOp",EDGE,"E1979"),sQuery(id+"F0.wireOp",EDGE,"E1980"),sQuery(id+"F0.wireOp",EDGE,"E1981"),sQuery(id+"F0.wireOp",EDGE,"E1982"),sQuery(id+"F0.wireOp",EDGE,"E1983"),sQuery(id+"F0.wireOp",EDGE,"E1984"),sQuery(id+"F0.wireOp",EDGE,"E1985"),sQuery(id+"F0.wireOp",EDGE,"E1986"),sQuery(id+"F0.wireOp",EDGE,"E1987"),sQuery(id+"F0.wireOp",EDGE,"E1988"),sQuery(id+"F0.wireOp",EDGE,"E1989"),sQuery(id+"F0.wireOp",EDGE,"E1990"),sQuery(id+"F0.wireOp",EDGE,"E1991"),sQuery(id+"F0.wireOp",EDGE,"E1992"),sQuery(id+"F0.wireOp",EDGE,"E1993"),sQuery(id+"F0.wireOp",EDGE,"E1994"),sQuery(id+"F0.wireOp",EDGE,"E1995"),sQuery(id+"F0.wireOp",EDGE,"E1996"),sQuery(id+"F0.wireOp",EDGE,"E1997"),sQuery(id+"F0.wireOp",EDGE,"E1998"),sQuery(id+"F0.wireOp",EDGE,"E1999"),sQuery(id+"F0.wireOp",EDGE,"E2000"),sQuery(id+"F0.wireOp",EDGE,"E2001"),sQuery(id+"F0.wireOp",EDGE,"E2002"),sQuery(id+"F0.wireOp",EDGE,"E2003"),sQuery(id+"F0.wireOp",EDGE,"E2004"),sQuery(id+"F0.wireOp",EDGE,"E2005"),sQuery(id+"F0.wireOp",EDGE,"E2006"),sQuery(id+"F0.wireOp",EDGE,"E2007"),sQuery(id+"F0.wireOp",EDGE,"E2008"),sQuery(id+"F0.wireOp",EDGE,"E2009"),sQuery(id+"F0.wireOp",EDGE,"E2010"),sQuery(id+"F0.wireOp",EDGE,"E2011"),sQuery(id+"F0.wireOp",EDGE,"E2012"),sQuery(id+"F0.wireOp",EDGE,"E2013"),sQuery(id+"F0.wireOp",EDGE,"E2014"),sQuery(id+"F0.wireOp",EDGE,"E2015"),sQuery(id+"F0.wireOp",EDGE,"E2016"),sQuery(id+"F0.wireOp",EDGE,"E2017"),sQuery(id+"F0.wireOp",EDGE,"E2018"),sQuery(id+"F0.wireOp",EDGE,"E2019"),sQuery(id+"F0.wireOp",EDGE,"E2020"),sQuery(id+"F0.wireOp",EDGE,"E2021"),sQuery(id+"F0.wireOp",EDGE,"E2022"),sQuery(id+"F0.wireOp",EDGE,"E2023"),sQuery(id+"F0.wireOp",EDGE,"E2024"),sQuery(id+"F0.wireOp",EDGE,"E2025"),sQuery(id+"F0.wireOp",EDGE,"E2026"),sQuery(id+"F0.wireOp",EDGE,"E2027"),sQuery(id+"F0.wireOp",EDGE,"E2028"),sQuery(id+"F0.wireOp",EDGE,"E2029"),sQuery(id+"F0.wireOp",EDGE,"E2030"),sQuery(id+"F0.wireOp",EDGE,"E2031"),sQuery(id+"F0.wireOp",EDGE,"E2032"),sQuery(id+"F0.wireOp",EDGE,"E2033"),sQuery(id+"F0.wireOp",EDGE,"E2034"),sQuery(id+"F0.wireOp",EDGE,"E2035"),sQuery(id+"F0.wireOp",EDGE,"E2036"),sQuery(id+"F0.wireOp",EDGE,"E2037"),sQuery(id+"F0.wireOp",EDGE,"E2038"),sQuery(id+"F0.wireOp",EDGE,"E2039"),sQuery(id+"F0.wireOp",EDGE,"E2040"),sQuery(id+"F0.wireOp",EDGE,"E2041"),sQuery(id+"F0.wireOp",EDGE,"E2042"),sQuery(id+"F0.wireOp",EDGE,"E2043"),sQuery(id+"F0.wireOp",EDGE,"E2044"),sQuery(id+"F0.wireOp",EDGE,"E2045"),sQuery(id+"F0.wireOp",EDGE,"E2046"),sQuery(id+"F0.wireOp",EDGE,"E2047"),sQuery(id+"F0.wireOp",EDGE,"E2048"),sQuery(id+"F0.wireOp",EDGE,"E2049"),sQuery(id+"F0.wireOp",EDGE,"E2050"),sQuery(id+"F0.wireOp",EDGE,"E2051"),sQuery(id+"F0.wireOp",EDGE,"E2052"),sQuery(id+"F0.wireOp",EDGE,"E2053"),sQuery(id+"F0.wireOp",EDGE,"E2054"),sQuery(id+"F0.wireOp",EDGE,"E2055"),sQuery(id+"F0.wireOp",EDGE,"E2056"),sQuery(id+"F0.wireOp",EDGE,"E2057"),sQuery(id+"F0.wireOp",EDGE,"E2058"),sQuery(id+"F0.wireOp",EDGE,"E2059"),sQuery(id+"F0.wireOp",EDGE,"E2060"),sQuery(id+"F0.wireOp",EDGE,"E2061"),sQuery(id+"F0.wireOp",EDGE,"E2062"),sQuery(id+"F0.wireOp",EDGE,"E2063"),sQuery(id+"F0.wireOp",EDGE,"E2064"),sQuery(id+"F0.wireOp",EDGE,"E2065"),sQuery(id+"F0.wireOp",EDGE,"E2066"),sQuery(id+"F0.wireOp",EDGE,"E2067"),sQuery(id+"F0.wireOp",EDGE,"E2068"),sQuery(id+"F0.wireOp",EDGE,"E2069"),sQuery(id+"F0.wireOp",EDGE,"E2070"),sQuery(id+"F0.wireOp",EDGE,"E2071"),sQuery(id+"F0.wireOp",EDGE,"E2072"),sQuery(id+"F0.wireOp",EDGE,"E2073"),sQuery(id+"F0.wireOp",EDGE,"E2074"),sQuery(id+"F0.wireOp",EDGE,"E2075"),sQuery(id+"F0.wireOp",EDGE,"E2076"),sQuery(id+"F0.wireOp",EDGE,"E2077"),sQuery(id+"F0.wireOp",EDGE,"E2078"),sQuery(id+"F0.wireOp",EDGE,"E2079"),sQuery(id+"F0.wireOp",EDGE,"E2080"),sQuery(id+"F0.wireOp",EDGE,"E2081"),sQuery(id+"F0.wireOp",EDGE,"E2082"),sQuery(id+"F0.wireOp",EDGE,"E2083"),sQuery(id+"F0.wireOp",EDGE,"E2084"),sQuery(id+"F0.wireOp",EDGE,"E2085"),sQuery(id+"F0.wireOp",EDGE,"E2086"),sQuery(id+"F0.wireOp",EDGE,"E2087"),sQuery(id+"F0.wireOp",EDGE,"E2088"),sQuery(id+"F0.wireOp",EDGE,"E2089"),sQuery(id+"F0.wireOp",EDGE,"E2090"),sQuery(id+"F0.wireOp",EDGE,"E2091"),sQuery(id+"F0.wireOp",EDGE,"E2092"),sQuery(id+"F0.wireOp",EDGE,"E2093"),sQuery(id+"F0.wireOp",EDGE,"E2094"),sQuery(id+"F0.wireOp",EDGE,"E2095"),sQuery(id+"F0.wireOp",EDGE,"E2096"),sQuery(id+"F0.wireOp",EDGE,"E2097"),sQuery(id+"F0.wireOp",EDGE,"E2098"),sQuery(id+"F0.wireOp",EDGE,"E2099"),sQuery(id+"F0.wireOp",EDGE,"E2100"),sQuery(id+"F0.wireOp",EDGE,"E2101"),sQuery(id+"F0.wireOp",EDGE,"E2102"),sQuery(id+"F0.wireOp",EDGE,"E2103"),sQuery(id+"F0.wireOp",EDGE,"E2104"),sQuery(id+"F0.wireOp",EDGE,"E2105"),sQuery(id+"F0.wireOp",EDGE,"E2106"),sQuery(id+"F0.wireOp",EDGE,"E2107"),sQuery(id+"F0.wireOp",EDGE,"E2108"),sQuery(id+"F0.wireOp",EDGE,"E2109"),sQuery(id+"F0.wireOp",EDGE,"E2110"),sQuery(id+"F0.wireOp",EDGE,"E2111"),sQuery(id+"F0.wireOp",EDGE,"E2112"),sQuery(id+"F0.wireOp",EDGE,"E2113"),sQuery(id+"F0.wireOp",EDGE,"E2114"),sQuery(id+"F0.wireOp",EDGE,"E2115"),sQuery(id+"F0.wireOp",EDGE,"E2116"),sQuery(id+"F0.wireOp",EDGE,"E2117"),sQuery(id+"F0.wireOp",EDGE,"E2118"),sQuery(id+"F0.wireOp",EDGE,"E2119"),sQuery(id+"F0.wireOp",EDGE,"E2120"),sQuery(id+"F0.wireOp",EDGE,"E2121"),sQuery(id+"F0.wireOp",EDGE,"E2122"),sQuery(id+"F0.wireOp",EDGE,"E2123"),sQuery(id+"F0.wireOp",EDGE,"E2124"),sQuery(id+"F0.wireOp",EDGE,"E2125"),sQuery(id+"F0.wireOp",EDGE,"E2126"),sQuery(id+"F0.wireOp",EDGE,"E2127"),sQuery(id+"F0.wireOp",EDGE,"E2128"),sQuery(id+"F0.wireOp",EDGE,"E2129"),sQuery(id+"F0.wireOp",EDGE,"E2130"),sQuery(id+"F0.wireOp",EDGE,"E2131"),sQuery(id+"F0.wireOp",EDGE,"E2132"),sQuery(id+"F0.wireOp",EDGE,"E2133"),sQuery(id+"F0.wireOp",EDGE,"E2134"),sQuery(id+"F0.wireOp",EDGE,"E2135"),sQuery(id+"F0.wireOp",EDGE,"E2136"),sQuery(id+"F0.wireOp",EDGE,"E2137"),sQuery(id+"F0.wireOp",EDGE,"E2138"),sQuery(id+"F0.wireOp",EDGE,"E2139"),sQuery(id+"F0.wireOp",EDGE,"E2140"),sQuery(id+"F0.wireOp",EDGE,"E2141"),sQuery(id+"F0.wireOp",EDGE,"E2142"),sQuery(id+"F0.wireOp",EDGE,"E2143"),sQuery(id+"F0.wireOp",EDGE,"E2144"),sQuery(id+"F0.wireOp",EDGE,"E2145"),sQuery(id+"F0.wireOp",EDGE,"E2146"),sQuery(id+"F0.wireOp",EDGE,"E2147"),sQuery(id+"F0.wireOp",EDGE,"E2148"),sQuery(id+"F0.wireOp",EDGE,"E2149"),sQuery(id+"F0.wireOp",EDGE,"E2150"),sQuery(id+"F0.wireOp",EDGE,"E2151"),sQuery(id+"F0.wireOp",EDGE,"E2152"),sQuery(id+"F0.wireOp",EDGE,"E2153"),sQuery(id+"F0.wireOp",EDGE,"E2154"),sQuery(id+"F0.wireOp",EDGE,"E2155"),sQuery(id+"F0.wireOp",EDGE,"E2156"),sQuery(id+"F0.wireOp",EDGE,"E2157"),sQuery(id+"F0.wireOp",EDGE,"E2158"),sQuery(id+"F0.wireOp",EDGE,"E2159"),sQuery(id+"F0.wireOp",EDGE,"E2160"),sQuery(id+"F0.wireOp",EDGE,"E2161"),sQuery(id+"F0.wireOp",EDGE,"E2162"),sQuery(id+"F0.wireOp",EDGE,"E2163"),sQuery(id+"F0.wireOp",EDGE,"E2164"),sQuery(id+"F0.wireOp",EDGE,"E2165"),sQuery(id+"F0.wireOp",EDGE,"E2166"),sQuery(id+"F0.wireOp",EDGE,"E2167"),sQuery(id+"F0.wireOp",EDGE,"E2168"),sQuery(id+"F0.wireOp",EDGE,"E2169"),sQuery(id+"F0.wireOp",EDGE,"E2170"),sQuery(id+"F0.wireOp",EDGE,"E2171"),sQuery(id+"F0.wireOp",EDGE,"E2172"),sQuery(id+"F0.wireOp",EDGE,"E2173"),sQuery(id+"F0.wireOp",EDGE,"E2174"),sQuery(id+"F0.wireOp",EDGE,"E2175"),sQuery(id+"F0.wireOp",EDGE,"E2176"),sQuery(id+"F0.wireOp",EDGE,"E2177"),sQuery(id+"F0.wireOp",EDGE,"E2178"),sQuery(id+"F0.wireOp",EDGE,"E2179"),sQuery(id+"F0.wireOp",EDGE,"E2180"),sQuery(id+"F0.wireOp",EDGE,"E2181"),sQuery(id+"F0.wireOp",EDGE,"E2182"),sQuery(id+"F0.wireOp",EDGE,"E2183"),sQuery(id+"F0.wireOp",EDGE,"E2184"),sQuery(id+"F0.wireOp",EDGE,"E2185"),sQuery(id+"F0.wireOp",EDGE,"E2186"),sQuery(id+"F0.wireOp",EDGE,"E2187"),sQuery(id+"F0.wireOp",EDGE,"E2188"),sQuery(id+"F0.wireOp",EDGE,"E2189"),sQuery(id+"F0.wireOp",EDGE,"E2190"),sQuery(id+"F0.wireOp",EDGE,"E2191"),sQuery(id+"F0.wireOp",EDGE,"E2192"),sQuery(id+"F0.wireOp",EDGE,"E2193"),sQuery(id+"F0.wireOp",EDGE,"E2194"),sQuery(id+"F0.wireOp",EDGE,"E2195"),sQuery(id+"F0.wireOp",EDGE,"E2196"),sQuery(id+"F0.wireOp",EDGE,"E2197"),sQuery(id+"F0.wireOp",EDGE,"E2198"),sQuery(id+"F0.wireOp",EDGE,"E2199"),sQuery(id+"F0.wireOp",EDGE,"E2200"),sQuery(id+"F0.wireOp",EDGE,"E2201"),sQuery(id+"F0.wireOp",EDGE,"E2202"),sQuery(id+"F0.wireOp",EDGE,"E2203"),sQuery(id+"F0.wireOp",EDGE,"E2204"),sQuery(id+"F0.wireOp",EDGE,"E2205"),sQuery(id+"F0.wireOp",EDGE,"E2206"),sQuery(id+"F0.wireOp",EDGE,"E2207"),sQuery(id+"F0.wireOp",EDGE,"E2208"),sQuery(id+"F0.wireOp",EDGE,"E2209"),sQuery(id+"F0.wireOp",EDGE,"E2210"),sQuery(id+"F0.wireOp",EDGE,"E2211"),sQuery(id+"F0.wireOp",EDGE,"E2212"),sQuery(id+"F0.wireOp",EDGE,"E2213"),sQuery(id+"F0.wireOp",EDGE,"E2214"),sQuery(id+"F0.wireOp",EDGE,"E2215"),sQuery(id+"F0.wireOp",EDGE,"E2216"),sQuery(id+"F0.wireOp",EDGE,"E2217"),sQuery(id+"F0.wireOp",EDGE,"E2218"),sQuery(id+"F0.wireOp",EDGE,"E2219"),sQuery(id+"F0.wireOp",EDGE,"E2220"),sQuery(id+"F0.wireOp",EDGE,"E2221"),sQuery(id+"F0.wireOp",EDGE,"E2222"),sQuery(id+"F0.wireOp",EDGE,"E2223"),sQuery(id+"F0.wireOp",EDGE,"E2224"),sQuery(id+"F0.wireOp",EDGE,"E2225"),sQuery(id+"F0.wireOp",EDGE,"E2226"),sQuery(id+"F0.wireOp",EDGE,"E2227"),sQuery(id+"F0.wireOp",EDGE,"E2228"),sQuery(id+"F0.wireOp",EDGE,"E2229"),sQuery(id+"F0.wireOp",EDGE,"E2230"),sQuery(id+"F0.wireOp",EDGE,"E2231"),sQuery(id+"F0.wireOp",EDGE,"E2232"),sQuery(id+"F0.wireOp",EDGE,"E2233"),sQuery(id+"F0.wireOp",EDGE,"E2234"),sQuery(id+"F0.wireOp",EDGE,"E2235"),sQuery(id+"F0.wireOp",EDGE,"E2236"),sQuery(id+"F0.wireOp",EDGE,"E2237"),sQuery(id+"F0.wireOp",EDGE,"E2238"),sQuery(id+"F0.wireOp",EDGE,"E2239"),sQuery(id+"F0.wireOp",EDGE,"E2240"),sQuery(id+"F0.wireOp",EDGE,"E2241"),sQuery(id+"F0.wireOp",EDGE,"E2242"),sQuery(id+"F0.wireOp",EDGE,"E2243"),sQuery(id+"F0.wireOp",EDGE,"E2244"),sQuery(id+"F0.wireOp",EDGE,"E2245"),sQuery(id+"F0.wireOp",EDGE,"E2246"),sQuery(id+"F0.wireOp",EDGE,"E2247"),sQuery(id+"F0.wireOp",EDGE,"E2248"),sQuery(id+"F0.wireOp",EDGE,"E2249"),sQuery(id+"F0.wireOp",EDGE,"E2250"),sQuery(id+"F0.wireOp",EDGE,"E2251"),sQuery(id+"F0.wireOp",EDGE,"E2252"),sQuery(id+"F0.wireOp",EDGE,"E2253"),sQuery(id+"F0.wireOp",EDGE,"E2254"),sQuery(id+"F0.wireOp",EDGE,"E2255"),sQuery(id+"F0.wireOp",EDGE,"E2256"),sQuery(id+"F0.wireOp",EDGE,"E2257"),sQuery(id+"F0.wireOp",EDGE,"E2258"),sQuery(id+"F0.wireOp",EDGE,"E2259"),sQuery(id+"F0.wireOp",EDGE,"E2260"),sQuery(id+"F0.wireOp",EDGE,"E2261"),sQuery(id+"F0.wireOp",EDGE,"E2262"),sQuery(id+"F0.wireOp",EDGE,"E2263"),sQuery(id+"F0.wireOp",EDGE,"E2264"),sQuery(id+"F0.wireOp",EDGE,"E2265"),sQuery(id+"F0.wireOp",EDGE,"E2266"),sQuery(id+"F0.wireOp",EDGE,"E2267"),sQuery(id+"F0.wireOp",EDGE,"E2268"),sQuery(id+"F0.wireOp",EDGE,"E2269"),sQuery(id+"F0.wireOp",EDGE,"E2270"),sQuery(id+"F0.wireOp",EDGE,"E2271"),sQuery(id+"F0.wireOp",EDGE,"E2272"),sQuery(id+"F0.wireOp",EDGE,"E2273"),sQuery(id+"F0.wireOp",EDGE,"E2274"),sQuery(id+"F0.wireOp",EDGE,"E2275"),sQuery(id+"F0.wireOp",EDGE,"E2276"),sQuery(id+"F0.wireOp",EDGE,"E2277"),sQuery(id+"F0.wireOp",EDGE,"E2278"),sQuery(id+"F0.wireOp",EDGE,"E2279"),sQuery(id+"F0.wireOp",EDGE,"E2280"),sQuery(id+"F0.wireOp",EDGE,"E2281"),sQuery(id+"F0.wireOp",EDGE,"E2282"),sQuery(id+"F0.wireOp",EDGE,"E2283"),sQuery(id+"F0.wireOp",EDGE,"E2284"),sQuery(id+"F0.wireOp",EDGE,"E2285"),sQuery(id+"F0.wireOp",EDGE,"E2286"),sQuery(id+"F0.wireOp",EDGE,"E2287"),sQuery(id+"F0.wireOp",EDGE,"E2288"),sQuery(id+"F0.wireOp",EDGE,"E2289"),sQuery(id+"F0.wireOp",EDGE,"E2290"),sQuery(id+"F0.wireOp",EDGE,"E2291"),sQuery(id+"F0.wireOp",EDGE,"E2292"),sQuery(id+"F0.wireOp",EDGE,"E2293"),sQuery(id+"F0.wireOp",EDGE,"E2294"),sQuery(id+"F0.wireOp",EDGE,"E2295"),sQuery(id+"F0.wireOp",EDGE,"E2296"),sQuery(id+"F0.wireOp",EDGE,"E2297"),sQuery(id+"F0.wireOp",EDGE,"E2298"),sQuery(id+"F0.wireOp",EDGE,"E2299"),sQuery(id+"F0.wireOp",EDGE,"E2300"),sQuery(id+"F0.wireOp",EDGE,"E2301"),sQuery(id+"F0.wireOp",EDGE,"E2302"),sQuery(id+"F0.wireOp",EDGE,"E2303"),sQuery(id+"F0.wireOp",EDGE,"E2304"),sQuery(id+"F0.wireOp",EDGE,"E2305"),sQuery(id+"F0.wireOp",EDGE,"E2306"),sQuery(id+"F0.wireOp",EDGE,"E2307"),sQuery(id+"F0.wireOp",EDGE,"E2308"),sQuery(id+"F0.wireOp",EDGE,"E2309"),sQuery(id+"F0.wireOp",EDGE,"E2310"),sQuery(id+"F0.wireOp",EDGE,"E2311"),sQuery(id+"F0.wireOp",EDGE,"E2312"),sQuery(id+"F0.wireOp",EDGE,"E2313"),sQuery(id+"F0.wireOp",EDGE,"E2314"),sQuery(id+"F0.wireOp",EDGE,"E2315"),sQuery(id+"F0.wireOp",EDGE,"E2316"),sQuery(id+"F0.wireOp",EDGE,"E2317"),sQuery(id+"F0.wireOp",EDGE,"E2318"),sQuery(id+"F0.wireOp",EDGE,"E2319"),sQuery(id+"F0.wireOp",EDGE,"E2320"),sQuery(id+"F0.wireOp",EDGE,"E2321"),sQuery(id+"F0.wireOp",EDGE,"E2322"),sQuery(id+"F0.wireOp",EDGE,"E2323"),sQuery(id+"F0.wireOp",EDGE,"E2324"),sQuery(id+"F0.wireOp",EDGE,"E2325"),sQuery(id+"F0.wireOp",EDGE,"E2326"),sQuery(id+"F0.wireOp",EDGE,"E2327"),sQuery(id+"F0.wireOp",EDGE,"E2328"),sQuery(id+"F0.wireOp",EDGE,"E2329"),sQuery(id+"F0.wireOp",EDGE,"E2330"),sQuery(id+"F0.wireOp",EDGE,"E2331"),sQuery(id+"F0.wireOp",EDGE,"E2332"),sQuery(id+"F0.wireOp",EDGE,"E2333"),sQuery(id+"F0.wireOp",EDGE,"E2334"),sQuery(id+"F0.wireOp",EDGE,"E2335"),sQuery(id+"F0.wireOp",EDGE,"E2336"),sQuery(id+"F0.wireOp",EDGE,"E2337"),sQuery(id+"F0.wireOp",EDGE,"E2338"),sQuery(id+"F0.wireOp",EDGE,"E2339"),sQuery(id+"F0.wireOp",EDGE,"E2340"),sQuery(id+"F0.wireOp",EDGE,"E2341"),sQuery(id+"F0.wireOp",EDGE,"E2342"),sQuery(id+"F0.wireOp",EDGE,"E2343"),sQuery(id+"F0.wireOp",EDGE,"E2344"),sQuery(id+"F0.wireOp",EDGE,"E2345"),sQuery(id+"F0.wireOp",EDGE,"E2346"),sQuery(id+"F0.wireOp",EDGE,"E2347"),sQuery(id+"F0.wireOp",EDGE,"E2348"),sQuery(id+"F0.wireOp",EDGE,"E2349"),sQuery(id+"F0.wireOp",EDGE,"E2350"),sQuery(id+"F0.wireOp",EDGE,"E2351"),sQuery(id+"F0.wireOp",EDGE,"E2352"),sQuery(id+"F0.wireOp",EDGE,"E2353"),sQuery(id+"F0.wireOp",EDGE,"E2354"),sQuery(id+"F0.wireOp",EDGE,"E2355"),sQuery(id+"F0.wireOp",EDGE,"E2356"),sQuery(id+"F0.wireOp",EDGE,"E2357"),sQuery(id+"F0.wireOp",EDGE,"E2358"),sQuery(id+"F0.wireOp",EDGE,"E2359"),sQuery(id+"F0.wireOp",EDGE,"E2360"),sQuery(id+"F0.wireOp",EDGE,"E2361"),sQuery(id+"F0.wireOp",EDGE,"E2362"),sQuery(id+"F0.wireOp",EDGE,"E2363"),sQuery(id+"F0.wireOp",EDGE,"E2364"),sQuery(id+"F0.wireOp",EDGE,"E2365"),sQuery(id+"F0.wireOp",EDGE,"E2366"),sQuery(id+"F0.wireOp",EDGE,"E2367"),sQuery(id+"F0.wireOp",EDGE,"E2368"),sQuery(id+"F0.wireOp",EDGE,"E2369"),sQuery(id+"F0.wireOp",EDGE,"E2370"),sQuery(id+"F0.wireOp",EDGE,"E2371"),sQuery(id+"F0.wireOp",EDGE,"E2372"),sQuery(id+"F0.wireOp",EDGE,"E2373"),sQuery(id+"F0.wireOp",EDGE,"E2374"),sQuery(id+"F0.wireOp",EDGE,"E2375"),sQuery(id+"F0.wireOp",EDGE,"E2376"),sQuery(id+"F0.wireOp",EDGE,"E2377"),sQuery(id+"F0.wireOp",EDGE,"E2378"),sQuery(id+"F0.wireOp",EDGE,"E2379"),sQuery(id+"F0.wireOp",EDGE,"E2380"),sQuery(id+"F0.wireOp",EDGE,"E2381"),sQuery(id+"F0.wireOp",EDGE,"E2382"),sQuery(id+"F0.wireOp",EDGE,"E2383"),sQuery(id+"F0.wireOp",EDGE,"E2384"),sQuery(id+"F0.wireOp",EDGE,"E2385"),sQuery(id+"F0.wireOp",EDGE,"E2386"),sQuery(id+"F0.wireOp",EDGE,"E2387"),sQuery(id+"F0.wireOp",EDGE,"E2388"),sQuery(id+"F0.wireOp",EDGE,"E2389"),sQuery(id+"F0.wireOp",EDGE,"E2390"),sQuery(id+"F0.wireOp",EDGE,"E2391"),sQuery(id+"F0.wireOp",EDGE,"E2392"),sQuery(id+"F0.wireOp",EDGE,"E2393"),sQuery(id+"F0.wireOp",EDGE,"E2394"),sQuery(id+"F0.wireOp",EDGE,"E2395"),sQuery(id+"F0.wireOp",EDGE,"E2396"),sQuery(id+"F0.wireOp",EDGE,"E2397"),sQuery(id+"F0.wireOp",EDGE,"E2398"),sQuery(id+"F0.wireOp",EDGE,"E2399"),sQuery(id+"F0.wireOp",EDGE,"E2400"),sQuery(id+"F0.wireOp",EDGE,"E2401"),sQuery(id+"F0.wireOp",EDGE,"E2402"),sQuery(id+"F0.wireOp",EDGE,"E2403"),sQuery(id+"F0.wireOp",EDGE,"E2404"),sQuery(id+"F0.wireOp",EDGE,"E2405"),sQuery(id+"F0.wireOp",EDGE,"E2406"),sQuery(id+"F0.wireOp",EDGE,"E2407"),sQuery(id+"F0.wireOp",EDGE,"E2408"),sQuery(id+"F0.wireOp",EDGE,"E2409"),sQuery(id+"F0.wireOp",EDGE,"E2410"),sQuery(id+"F0.wireOp",EDGE,"E2411"),sQuery(id+"F0.wireOp",EDGE,"E2412"),sQuery(id+"F0.wireOp",EDGE,"E2413"),sQuery(id+"F0.wireOp",EDGE,"E2414"),sQuery(id+"F0.wireOp",EDGE,"E2415"),sQuery(id+"F0.wireOp",EDGE,"E2416"),sQuery(id+"F0.wireOp",EDGE,"E2417"),sQuery(id+"F0.wireOp",EDGE,"E2418"),sQuery(id+"F0.wireOp",EDGE,"E2419"),sQuery(id+"F0.wireOp",EDGE,"E2420"),sQuery(id+"F0.wireOp",EDGE,"E2421"),sQuery(id+"F0.wireOp",EDGE,"E2422"),sQuery(id+"F0.wireOp",EDGE,"E2423"),sQuery(id+"F0.wireOp",EDGE,"E2424"),sQuery(id+"F0.wireOp",EDGE,"E2425"),sQuery(id+"F0.wireOp",EDGE,"E2426"),sQuery(id+"F0.wireOp",EDGE,"E2427"),sQuery(id+"F0.wireOp",EDGE,"E2428"),sQuery(id+"F0.wireOp",EDGE,"E2429"),sQuery(id+"F0.wireOp",EDGE,"E2430"),sQuery(id+"F0.wireOp",EDGE,"E2431"),sQuery(id+"F0.wireOp",EDGE,"E2432"),sQuery(id+"F0.wireOp",EDGE,"E2433"),sQuery(id+"F0.wireOp",EDGE,"E2434"),sQuery(id+"F0.wireOp",EDGE,"E2435"),sQuery(id+"F0.wireOp",EDGE,"E2436"),sQuery(id+"F0.wireOp",EDGE,"E2437"),sQuery(id+"F0.wireOp",EDGE,"E2438"),sQuery(id+"F0.wireOp",EDGE,"E2439"),sQuery(id+"F0.wireOp",EDGE,"E2440"),sQuery(id+"F0.wireOp",EDGE,"E2441"),sQuery(id+"F0.wireOp",EDGE,"E2442"),sQuery(id+"F0.wireOp",EDGE,"E2443"),sQuery(id+"F0.wireOp",EDGE,"E2444"),sQuery(id+"F0.wireOp",EDGE,"E2445"),sQuery(id+"F0.wireOp",EDGE,"E2446"),sQuery(id+"F0.wireOp",EDGE,"E2447"),sQuery(id+"F0.wireOp",EDGE,"E2448"),sQuery(id+"F0.wireOp",EDGE,"E2449"),sQuery(id+"F0.wireOp",EDGE,"E2450"),sQuery(id+"F0.wireOp",EDGE,"E2451"),sQuery(id+"F0.wireOp",EDGE,"E2452"),sQuery(id+"F0.wireOp",EDGE,"E2453"),sQuery(id+"F0.wireOp",EDGE,"E2454"),sQuery(id+"F0.wireOp",EDGE,"E2455"),sQuery(id+"F0.wireOp",EDGE,"E2456"),sQuery(id+"F0.wireOp",EDGE,"E2457"),sQuery(id+"F0.wireOp",EDGE,"E2458"),sQuery(id+"F0.wireOp",EDGE,"E2459"),sQuery(id+"F0.wireOp",EDGE,"E2460"),sQuery(id+"F0.wireOp",EDGE,"E2461"),sQuery(id+"F0.wireOp",EDGE,"E2462"),sQuery(id+"F0.wireOp",EDGE,"E2463"),sQuery(id+"F0.wireOp",EDGE,"E2464"),sQuery(id+"F0.wireOp",EDGE,"E2465"),sQuery(id+"F0.wireOp",EDGE,"E2466"),sQuery(id+"F0.wireOp",EDGE,"E2467"),sQuery(id+"F0.wireOp",EDGE,"E2468"),sQuery(id+"F0.wireOp",EDGE,"E2469"),sQuery(id+"F0.wireOp",EDGE,"E2470"),sQuery(id+"F0.wireOp",EDGE,"E2471"),sQuery(id+"F0.wireOp",EDGE,"E2472"),sQuery(id+"F0.wireOp",EDGE,"E2473"),sQuery(id+"F0.wireOp",EDGE,"E2474"),sQuery(id+"F0.wireOp",EDGE,"E2475"),sQuery(id+"F0.wireOp",EDGE,"E2476"),sQuery(id+"F0.wireOp",EDGE,"E2477"),sQuery(id+"F0.wireOp",EDGE,"E2478"),sQuery(id+"F0.wireOp",EDGE,"E2479"),sQuery(id+"F0.wireOp",EDGE,"E2480"),sQuery(id+"F0.wireOp",EDGE,"E2481"),sQuery(id+"F0.wireOp",EDGE,"E2482"),sQuery(id+"F0.wireOp",EDGE,"E2483"),sQuery(id+"F0.wireOp",EDGE,"E2484"),sQuery(id+"F0.wireOp",EDGE,"E2485"),sQuery(id+"F0.wireOp",EDGE,"E2486"),sQuery(id+"F0.wireOp",EDGE,"E2487"),sQuery(id+"F0.wireOp",EDGE,"E2488"),sQuery(id+"F0.wireOp",EDGE,"E2489"),sQuery(id+"F0.wireOp",EDGE,"E2490"),sQuery(id+"F0.wireOp",EDGE,"E2491"),sQuery(id+"F0.wireOp",EDGE,"E2492"),sQuery(id+"F0.wireOp",EDGE,"E2493"),sQuery(id+"F0.wireOp",EDGE,"E2494"),sQuery(id+"F0.wireOp",EDGE,"E2495"),sQuery(id+"F0.wireOp",EDGE,"E2496"),sQuery(id+"F0.wireOp",EDGE,"E2497"),sQuery(id+"F0.wireOp",EDGE,"E2498"),sQuery(id+"F0.wireOp",EDGE,"E2499"),sQuery(id+"F0.wireOp",EDGE,"E2500"),sQuery(id+"F0.wireOp",EDGE,"E2501"),sQuery(id+"F0.wireOp",EDGE,"E2502"),sQuery(id+"F0.wireOp",EDGE,"E2503"),sQuery(id+"F0.wireOp",EDGE,"E2504"),sQuery(id+"F0.wireOp",EDGE,"E2505"),sQuery(id+"F0.wireOp",EDGE,"E2506"),sQuery(id+"F0.wireOp",EDGE,"E2507"),sQuery(id+"F0.wireOp",EDGE,"E2508"),sQuery(id+"F0.wireOp",EDGE,"E2509"),sQuery(id+"F0.wireOp",EDGE,"E2510"),sQuery(id+"F0.wireOp",EDGE,"E2511"),sQuery(id+"F0.wireOp",EDGE,"E2512"),sQuery(id+"F0.wireOp",EDGE,"E2513"),sQuery(id+"F0.wireOp",EDGE,"E2514"),sQuery(id+"F0.wireOp",EDGE,"E2515"),sQuery(id+"F0.wireOp",EDGE,"E2516"),sQuery(id+"F0.wireOp",EDGE,"E2517"),sQuery(id+"F0.wireOp",EDGE,"E2518"),sQuery(id+"F0.wireOp",EDGE,"E2519"),sQuery(id+"F0.wireOp",EDGE,"E2520"),sQuery(id+"F0.wireOp",EDGE,"E2521"),sQuery(id+"F0.wireOp",EDGE,"E2522"),sQuery(id+"F0.wireOp",EDGE,"E2523"),sQuery(id+"F0.wireOp",EDGE,"E2524"),sQuery(id+"F0.wireOp",EDGE,"E2525"),sQuery(id+"F0.wireOp",EDGE,"E2526"),sQuery(id+"F0.wireOp",EDGE,"E2527"),sQuery(id+"F0.wireOp",EDGE,"E2528"),sQuery(id+"F0.wireOp",EDGE,"E2529"),sQuery(id+"F0.wireOp",EDGE,"E2530"),sQuery(id+"F0.wireOp",EDGE,"E2531"),sQuery(id+"F0.wireOp",EDGE,"E2532"),sQuery(id+"F0.wireOp",EDGE,"E2533"),sQuery(id+"F0.wireOp",EDGE,"E2534"),sQuery(id+"F0.wireOp",EDGE,"E2535"),sQuery(id+"F0.wireOp",EDGE,"E2536"),sQuery(id+"F0.wireOp",EDGE,"E2537"),sQuery(id+"F0.wireOp",EDGE,"E2538"),sQuery(id+"F0.wireOp",EDGE,"E2539"),sQuery(id+"F0.wireOp",EDGE,"E2540"),sQuery(id+"F0.wireOp",EDGE,"E2541"),sQuery(id+"F0.wireOp",EDGE,"E2542"),sQuery(id+"F0.wireOp",EDGE,"E2543"),sQuery(id+"F0.wireOp",EDGE,"E2544"),sQuery(id+"F0.wireOp",EDGE,"E2545"),sQuery(id+"F0.wireOp",EDGE,"E2546"),sQuery(id+"F0.wireOp",EDGE,"E2547"),sQuery(id+"F0.wireOp",EDGE,"E2548"),sQuery(id+"F0.wireOp",EDGE,"E2549"),sQuery(id+"F0.wireOp",EDGE,"E2550"),sQuery(id+"F0.wireOp",EDGE,"E2551"),sQuery(id+"F0.wireOp",EDGE,"E2552"),sQuery(id+"F0.wireOp",EDGE,"E2553"),sQuery(id+"F0.wireOp",EDGE,"E2554"),sQuery(id+"F0.wireOp",EDGE,"E2555"),sQuery(id+"F0.wireOp",EDGE,"E2556"),sQuery(id+"F0.wireOp",EDGE,"E2557"),sQuery(id+"F0.wireOp",EDGE,"E2558"),sQuery(id+"F0.wireOp",EDGE,"E2559")])],"isStart":false});
            var sketch = newSketch(context, id + "F2", { "sketchPlane" : qUnion([Q0])});
            skCircle(sketch, "E2560", {"center": v(6.05, 29.3) * mm, "radius": 1 * mm});
            skSolve(sketch);
        }
        {
            var Q0;
            Q0 = qSketchRegion(id + "F2", true);
            extrude(context, id + "F3", {"entities" : qUnion([Q0]), "operationType" : NewBodyOperationType.REMOVE, "oppositeDirection" : true, "depth" : 25 * mm});
        }
    });
